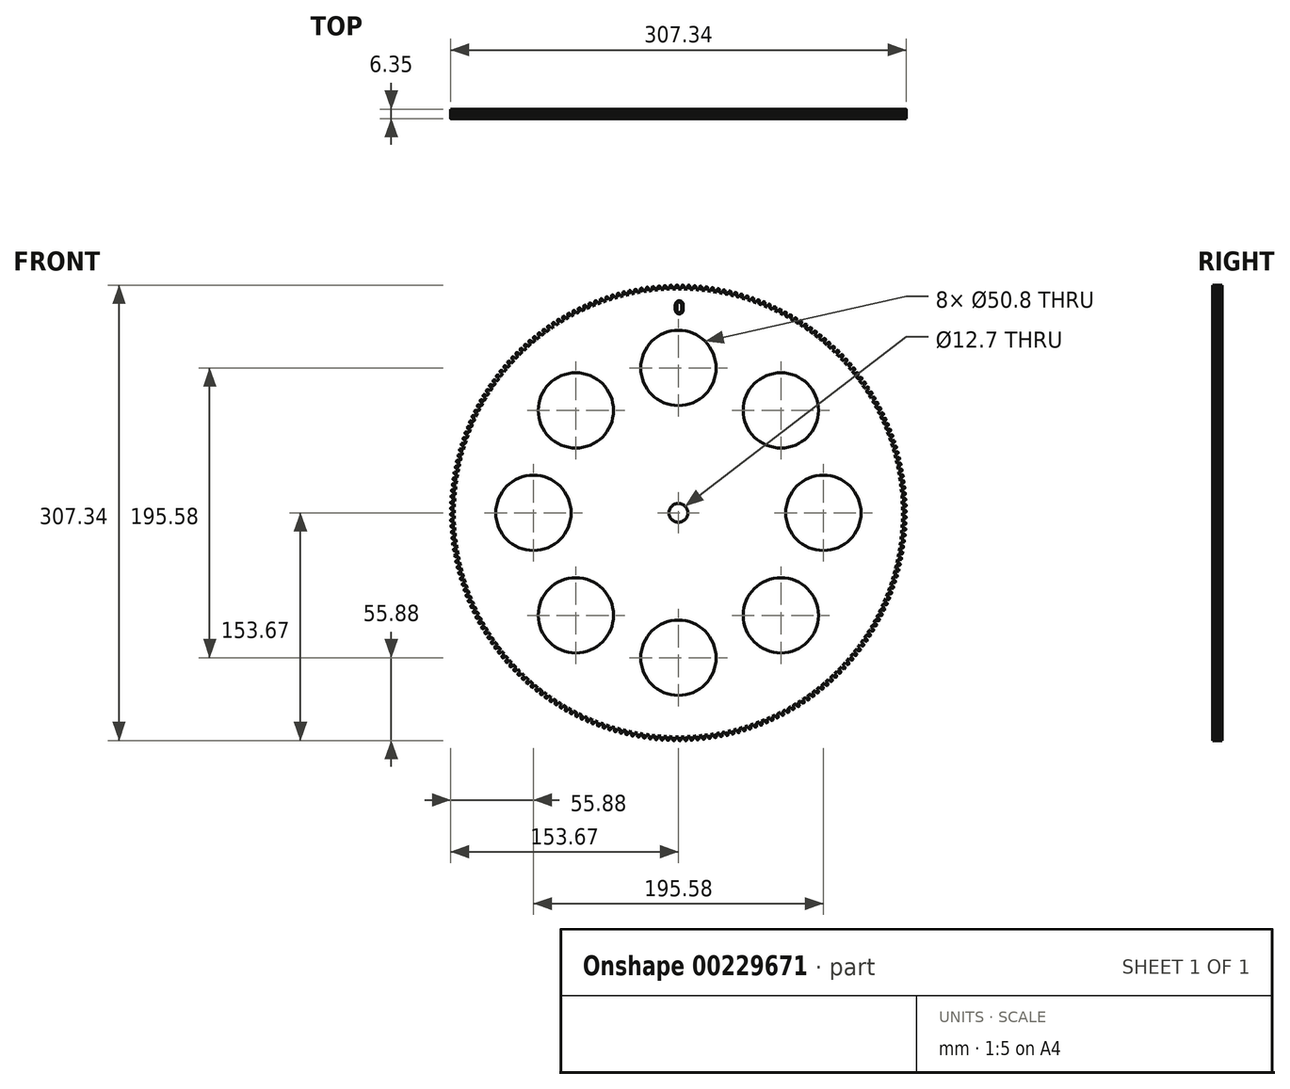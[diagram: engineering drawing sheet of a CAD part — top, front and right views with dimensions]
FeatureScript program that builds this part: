
annotation { "Feature Type Name" : "Feature", "Feature Type Description" : "" }
export const myFeature = defineFeature(function(context is Context, id is Id, definition is map)
    precondition{}
    {
        {
            var Q0;
            Q0=qCreatedBy(makeId("Front.planeOp"),FACE);
            var sketch = newSketch(context, id + "F0", { "sketchPlane" : qUnion([Q0])});
            skArc(sketch, "E0", {"start": v(-1.99, 151.12) * mm, "mid": v(0.99, -151.13) * mm, "end": v(0, 151.13) * mm});
            skArc(sketch, "E1.trimOffspring", {"start": v(0, 152.4) * mm, "mid": v(-0.24, 153.01) * mm, "end": v(-0.5, 153.63) * mm});
            skLineSegment(sketch, "E2", {"start": v(0, 152.4) * mm, "end": v(0, 151.13) * mm});
            skLineSegment(sketch, "E3", {"start": v(-0.56, 153.67) * mm, "end": v(-1, 153.67) * mm});
            skLineSegment(sketch, "E4.MirrorCS", {"start": v(-1.44, 153.66) * mm, "end": v(-1, 153.67) * mm});
            skArc(sketch, "E5.MirrorCS", {"start": v(-2, 152.39) * mm, "mid": v(-1.76, 153) * mm, "end": v(-1.52, 153.6) * mm});
            skLineSegment(sketch, "E6.MirrorCS", {"start": v(-2, 152.39) * mm, "end": v(-1.99, 151.12) * mm});
            skPoint(sketch, "E7.orphan", {"position": v(-1.98, 149.66) * mm});
            skPoint(sketch, "E8.orphan", {"position": v(0.02, 149.67) * mm});
            skPoint(sketch, "E9.visualSharp", {"position": v(-1.5, 153.66) * mm});
            skArc(sketch, "E9.filletArc", {"start": v(-1.44, 153.66) * mm, "mid": v(-1.48, 153.65) * mm, "end": v(-1.52, 153.6) * mm});
            skPoint(sketch, "E10.visualSharp", {"position": v(-0.52, 153.67) * mm});
            skArc(sketch, "E10.filletArc", {"start": v(-0.5, 153.63) * mm, "mid": v(-0.52, 153.66) * mm, "end": v(-0.56, 153.67) * mm});
            skLineSegment(sketch, "E11.1.0", {"start": v(-5.98, 152.28) * mm, "end": v(-5.94, 151.01) * mm});
            skArc(sketch, "E11.1.1", {"start": v(-5.98, 152.28) * mm, "mid": v(-5.77, 152.9) * mm, "end": v(-5.54, 153.52) * mm});
            skArc(sketch, "E11.1.2", {"start": v(-5.46, 153.57) * mm, "mid": v(-5.5, 153.56) * mm, "end": v(-5.54, 153.52) * mm});
            skLineSegment(sketch, "E11.1.3", {"start": v(-5.46, 153.57) * mm, "end": v(-5.03, 153.59) * mm});
            skLineSegment(sketch, "E11.1.4", {"start": v(-4.59, 153.6) * mm, "end": v(-5.03, 153.59) * mm});
            skArc(sketch, "E11.1.5", {"start": v(-4.52, 153.56) * mm, "mid": v(-4.55, 153.6) * mm, "end": v(-4.59, 153.6) * mm});
            skArc(sketch, "E11.1.6", {"start": v(-3.99, 152.35) * mm, "mid": v(-4.25, 152.96) * mm, "end": v(-4.52, 153.56) * mm});
            skLineSegment(sketch, "E11.1.7", {"start": v(-3.99, 152.35) * mm, "end": v(-3.95, 151.08) * mm});
            skLineSegment(sketch, "E11.2.0", {"start": v(-9.97, 152.07) * mm, "end": v(-9.9, 150.8) * mm});
            skArc(sketch, "E11.2.1", {"start": v(-9.97, 152.07) * mm, "mid": v(-9.77, 152.7) * mm, "end": v(-9.55, 153.32) * mm});
            skArc(sketch, "E11.2.2", {"start": v(-9.48, 153.38) * mm, "mid": v(-9.52, 153.36) * mm, "end": v(-9.55, 153.32) * mm});
            skLineSegment(sketch, "E11.2.3", {"start": v(-9.48, 153.38) * mm, "end": v(-9.05, 153.4) * mm});
            skLineSegment(sketch, "E11.2.4", {"start": v(-8.6, 153.43) * mm, "end": v(-9.05, 153.4) * mm});
            skArc(sketch, "E11.2.5", {"start": v(-8.54, 153.39) * mm, "mid": v(-8.57, 153.42) * mm, "end": v(-8.6, 153.43) * mm});
            skArc(sketch, "E11.2.6", {"start": v(-7.98, 152.2) * mm, "mid": v(-8.25, 152.8) * mm, "end": v(-8.54, 153.39) * mm});
            skLineSegment(sketch, "E11.2.7", {"start": v(-7.98, 152.2) * mm, "end": v(-7.9, 150.92) * mm});
            skLineSegment(sketch, "E11.3.0", {"start": v(-13.94, 151.76) * mm, "end": v(-13.84, 150.5) * mm});
            skArc(sketch, "E11.3.1", {"start": v(-13.94, 151.76) * mm, "mid": v(-13.76, 152.39) * mm, "end": v(-13.56, 153.02) * mm});
            skArc(sketch, "E11.3.2", {"start": v(-13.49, 153.08) * mm, "mid": v(-13.54, 153.06) * mm, "end": v(-13.56, 153.02) * mm});
            skLineSegment(sketch, "E11.3.3", {"start": v(-13.49, 153.08) * mm, "end": v(-13.06, 153.11) * mm});
            skLineSegment(sketch, "E11.3.4", {"start": v(-12.62, 153.15) * mm, "end": v(-13.06, 153.11) * mm});
            skArc(sketch, "E11.3.5", {"start": v(-12.55, 153.11) * mm, "mid": v(-12.58, 153.14) * mm, "end": v(-12.62, 153.15) * mm});
            skArc(sketch, "E11.3.6", {"start": v(-11.96, 151.93) * mm, "mid": v(-12.25, 152.52) * mm, "end": v(-12.55, 153.11) * mm});
            skLineSegment(sketch, "E11.3.7", {"start": v(-11.96, 151.93) * mm, "end": v(-11.85, 150.66) * mm});
            skLineSegment(sketch, "E11.4.0", {"start": v(-17.91, 151.34) * mm, "end": v(-17.77, 150.08) * mm});
            skArc(sketch, "E11.4.1", {"start": v(-17.91, 151.34) * mm, "mid": v(-17.74, 151.98) * mm, "end": v(-17.57, 152.6) * mm});
            skArc(sketch, "E11.4.2", {"start": v(-17.5, 152.67) * mm, "mid": v(-17.54, 152.65) * mm, "end": v(-17.57, 152.6) * mm});
            skLineSegment(sketch, "E11.4.3", {"start": v(-17.5, 152.67) * mm, "end": v(-17.06, 152.72) * mm});
            skLineSegment(sketch, "E11.4.4", {"start": v(-16.62, 152.77) * mm, "end": v(-17.06, 152.72) * mm});
            skArc(sketch, "E11.4.5", {"start": v(-16.55, 152.73) * mm, "mid": v(-16.58, 152.76) * mm, "end": v(-16.62, 152.77) * mm});
            skArc(sketch, "E11.4.6", {"start": v(-15.93, 151.57) * mm, "mid": v(-16.24, 152.15) * mm, "end": v(-16.55, 152.73) * mm});
            skLineSegment(sketch, "E11.4.7", {"start": v(-15.93, 151.57) * mm, "end": v(-15.79, 150.3) * mm});
            skLineSegment(sketch, "E11.5.0", {"start": v(-21.87, 150.82) * mm, "end": v(-21.7, 149.56) * mm});
            skArc(sketch, "E11.5.1", {"start": v(-21.87, 150.82) * mm, "mid": v(-21.72, 151.46) * mm, "end": v(-21.55, 152.1) * mm});
            skArc(sketch, "E11.5.2", {"start": v(-21.48, 152.16) * mm, "mid": v(-21.53, 152.14) * mm, "end": v(-21.55, 152.1) * mm});
            skLineSegment(sketch, "E11.5.3", {"start": v(-21.48, 152.16) * mm, "end": v(-21.05, 152.22) * mm});
            skLineSegment(sketch, "E11.5.4", {"start": v(-20.62, 152.28) * mm, "end": v(-21.05, 152.22) * mm});
            skArc(sketch, "E11.5.5", {"start": v(-20.55, 152.25) * mm, "mid": v(-20.58, 152.27) * mm, "end": v(-20.62, 152.28) * mm});
            skArc(sketch, "E11.5.6", {"start": v(-19.9, 151.1) * mm, "mid": v(-20.21, 151.67) * mm, "end": v(-20.55, 152.25) * mm});
            skLineSegment(sketch, "E11.5.7", {"start": v(-19.9, 151.1) * mm, "end": v(-19.72, 149.84) * mm});
            skLineSegment(sketch, "E11.6.0", {"start": v(-25.8, 150.2) * mm, "end": v(-25.6, 148.95) * mm});
            skArc(sketch, "E11.6.1", {"start": v(-25.8, 150.2) * mm, "mid": v(-25.67, 150.84) * mm, "end": v(-25.53, 151.48) * mm});
            skArc(sketch, "E11.6.2", {"start": v(-25.46, 151.55) * mm, "mid": v(-25.5, 151.52) * mm, "end": v(-25.53, 151.48) * mm});
            skLineSegment(sketch, "E11.6.3", {"start": v(-25.46, 151.55) * mm, "end": v(-25.03, 151.62) * mm});
            skLineSegment(sketch, "E11.6.4", {"start": v(-24.6, 151.69) * mm, "end": v(-25.03, 151.62) * mm});
            skArc(sketch, "E11.6.5", {"start": v(-24.52, 151.66) * mm, "mid": v(-24.56, 151.68) * mm, "end": v(-24.6, 151.69) * mm});
            skArc(sketch, "E11.6.6", {"start": v(-23.84, 150.52) * mm, "mid": v(-24.18, 151.1) * mm, "end": v(-24.52, 151.66) * mm});
            skLineSegment(sketch, "E11.6.7", {"start": v(-23.84, 150.52) * mm, "end": v(-23.63, 149.27) * mm});
            skLineSegment(sketch, "E11.7.0", {"start": v(-29.73, 149.47) * mm, "end": v(-29.5, 148.22) * mm});
            skArc(sketch, "E11.7.1", {"start": v(-29.73, 149.47) * mm, "mid": v(-29.61, 150.12) * mm, "end": v(-29.48, 150.76) * mm});
            skArc(sketch, "E11.7.2", {"start": v(-29.41, 150.83) * mm, "mid": v(-29.46, 150.8) * mm, "end": v(-29.48, 150.76) * mm});
            skLineSegment(sketch, "E11.7.3", {"start": v(-29.41, 150.83) * mm, "end": v(-29, 150.91) * mm});
            skLineSegment(sketch, "E11.7.4", {"start": v(-28.56, 151) * mm, "end": v(-29, 150.91) * mm});
            skArc(sketch, "E11.7.5", {"start": v(-28.49, 150.96) * mm, "mid": v(-28.52, 150.99) * mm, "end": v(-28.56, 151) * mm});
            skArc(sketch, "E11.7.6", {"start": v(-27.77, 149.85) * mm, "mid": v(-28.12, 150.4) * mm, "end": v(-28.49, 150.96) * mm});
            skLineSegment(sketch, "E11.7.7", {"start": v(-27.77, 149.85) * mm, "end": v(-27.53, 148.6) * mm});
            skLineSegment(sketch, "E11.8.0", {"start": v(-33.63, 148.64) * mm, "end": v(-33.36, 147.4) * mm});
            skArc(sketch, "E11.8.1", {"start": v(-33.63, 148.64) * mm, "mid": v(-33.53, 149.3) * mm, "end": v(-33.42, 149.94) * mm});
            skArc(sketch, "E11.8.2", {"start": v(-33.35, 150) * mm, "mid": v(-33.4, 149.98) * mm, "end": v(-33.42, 149.94) * mm});
            skLineSegment(sketch, "E11.8.3", {"start": v(-33.35, 150) * mm, "end": v(-32.93, 150.1) * mm});
            skLineSegment(sketch, "E11.8.4", {"start": v(-32.5, 150.2) * mm, "end": v(-32.93, 150.1) * mm});
            skArc(sketch, "E11.8.5", {"start": v(-32.43, 150.16) * mm, "mid": v(-32.46, 150.2) * mm, "end": v(-32.5, 150.2) * mm});
            skArc(sketch, "E11.8.6", {"start": v(-31.69, 149.07) * mm, "mid": v(-32.05, 149.62) * mm, "end": v(-32.43, 150.16) * mm});
            skLineSegment(sketch, "E11.8.7", {"start": v(-31.69, 149.07) * mm, "end": v(-31.41, 147.83) * mm});
            skLineSegment(sketch, "E11.9.0", {"start": v(-37.51, 147.71) * mm, "end": v(-37.2, 146.48) * mm});
            skArc(sketch, "E11.9.1", {"start": v(-37.51, 147.71) * mm, "mid": v(-37.43, 148.36) * mm, "end": v(-37.33, 149.01) * mm});
            skArc(sketch, "E11.9.2", {"start": v(-37.27, 149.08) * mm, "mid": v(-37.31, 149.06) * mm, "end": v(-37.33, 149.01) * mm});
            skLineSegment(sketch, "E11.9.3", {"start": v(-37.27, 149.08) * mm, "end": v(-36.85, 149.19) * mm});
            skLineSegment(sketch, "E11.9.4", {"start": v(-36.42, 149.3) * mm, "end": v(-36.85, 149.19) * mm});
            skArc(sketch, "E11.9.5", {"start": v(-36.35, 149.26) * mm, "mid": v(-36.38, 149.29) * mm, "end": v(-36.42, 149.3) * mm});
            skArc(sketch, "E11.9.6", {"start": v(-35.58, 148.19) * mm, "mid": v(-35.96, 148.73) * mm, "end": v(-36.35, 149.26) * mm});
            skLineSegment(sketch, "E11.9.7", {"start": v(-35.58, 148.19) * mm, "end": v(-35.27, 146.96) * mm});
            skLineSegment(sketch, "E11.10.0", {"start": v(-41.37, 146.68) * mm, "end": v(-41.03, 145.45) * mm});
            skArc(sketch, "E11.10.1", {"start": v(-41.37, 146.68) * mm, "mid": v(-41.3, 147.33) * mm, "end": v(-41.22, 147.98) * mm});
            skArc(sketch, "E11.10.2", {"start": v(-41.16, 148.06) * mm, "mid": v(-41.2, 148.03) * mm, "end": v(-41.22, 147.98) * mm});
            skLineSegment(sketch, "E11.10.3", {"start": v(-41.16, 148.06) * mm, "end": v(-40.74, 148.17) * mm});
            skLineSegment(sketch, "E11.10.4", {"start": v(-40.32, 148.29) * mm, "end": v(-40.74, 148.17) * mm});
            skArc(sketch, "E11.10.5", {"start": v(-40.24, 148.26) * mm, "mid": v(-40.28, 148.29) * mm, "end": v(-40.32, 148.29) * mm});
            skArc(sketch, "E11.10.6", {"start": v(-39.44, 147.2) * mm, "mid": v(-39.84, 147.74) * mm, "end": v(-40.24, 148.26) * mm});
            skLineSegment(sketch, "E11.10.7", {"start": v(-39.44, 147.2) * mm, "end": v(-39.1, 145.98) * mm});
            skLineSegment(sketch, "E11.11.0", {"start": v(-45.2, 145.55) * mm, "end": v(-44.82, 144.33) * mm});
            skArc(sketch, "E11.11.1", {"start": v(-45.2, 145.55) * mm, "mid": v(-45.14, 146.2) * mm, "end": v(-45.08, 146.85) * mm});
            skArc(sketch, "E11.11.2", {"start": v(-45.02, 146.93) * mm, "mid": v(-45.06, 146.9) * mm, "end": v(-45.08, 146.85) * mm});
            skLineSegment(sketch, "E11.11.3", {"start": v(-45.02, 146.93) * mm, "end": v(-44.6, 147.05) * mm});
            skLineSegment(sketch, "E11.11.4", {"start": v(-44.19, 147.18) * mm, "end": v(-44.6, 147.05) * mm});
            skArc(sketch, "E11.11.5", {"start": v(-44.1, 147.16) * mm, "mid": v(-44.14, 147.18) * mm, "end": v(-44.19, 147.18) * mm});
            skArc(sketch, "E11.11.6", {"start": v(-43.28, 146.12) * mm, "mid": v(-43.7, 146.64) * mm, "end": v(-44.1, 147.16) * mm});
            skLineSegment(sketch, "E11.11.7", {"start": v(-43.28, 146.12) * mm, "end": v(-42.92, 144.9) * mm});
            skLineSegment(sketch, "E11.12.0", {"start": v(-48.99, 144.31) * mm, "end": v(-48.59, 143.1) * mm});
            skArc(sketch, "E11.12.1", {"start": v(-48.99, 144.31) * mm, "mid": v(-48.95, 144.97) * mm, "end": v(-48.91, 145.62) * mm});
            skArc(sketch, "E11.12.2", {"start": v(-48.85, 145.7) * mm, "mid": v(-48.9, 145.67) * mm, "end": v(-48.91, 145.62) * mm});
            skLineSegment(sketch, "E11.12.3", {"start": v(-48.85, 145.7) * mm, "end": v(-48.44, 145.84) * mm});
            skLineSegment(sketch, "E11.12.4", {"start": v(-48.02, 145.97) * mm, "end": v(-48.44, 145.84) * mm});
            skArc(sketch, "E11.12.5", {"start": v(-47.95, 145.95) * mm, "mid": v(-47.98, 145.97) * mm, "end": v(-48.02, 145.97) * mm});
            skArc(sketch, "E11.12.6", {"start": v(-47.1, 144.94) * mm, "mid": v(-47.52, 145.45) * mm, "end": v(-47.95, 145.95) * mm});
            skLineSegment(sketch, "E11.12.7", {"start": v(-47.1, 144.94) * mm, "end": v(-46.7, 143.74) * mm});
            skLineSegment(sketch, "E11.13.0", {"start": v(-52.75, 142.98) * mm, "end": v(-52.32, 141.79) * mm});
            skArc(sketch, "E11.13.1", {"start": v(-52.75, 142.98) * mm, "mid": v(-52.73, 143.64) * mm, "end": v(-52.7, 144.3) * mm});
            skArc(sketch, "E11.13.2", {"start": v(-52.65, 144.37) * mm, "mid": v(-52.69, 144.34) * mm, "end": v(-52.7, 144.3) * mm});
            skLineSegment(sketch, "E11.13.3", {"start": v(-52.65, 144.37) * mm, "end": v(-52.24, 144.52) * mm});
            skLineSegment(sketch, "E11.13.4", {"start": v(-51.83, 144.67) * mm, "end": v(-52.24, 144.52) * mm});
            skArc(sketch, "E11.13.5", {"start": v(-51.75, 144.65) * mm, "mid": v(-51.79, 144.67) * mm, "end": v(-51.83, 144.67) * mm});
            skArc(sketch, "E11.13.6", {"start": v(-50.87, 143.66) * mm, "mid": v(-51.3, 144.16) * mm, "end": v(-51.75, 144.65) * mm});
            skLineSegment(sketch, "E11.13.7", {"start": v(-50.87, 143.66) * mm, "end": v(-50.44, 142.46) * mm});
            skLineSegment(sketch, "E11.14.0", {"start": v(-56.47, 141.55) * mm, "end": v(-56.01, 140.37) * mm});
            skArc(sketch, "E11.14.1", {"start": v(-56.47, 141.55) * mm, "mid": v(-56.47, 142.2) * mm, "end": v(-56.46, 142.86) * mm});
            skArc(sketch, "E11.14.2", {"start": v(-56.4, 142.94) * mm, "mid": v(-56.45, 142.91) * mm, "end": v(-56.46, 142.86) * mm});
            skLineSegment(sketch, "E11.14.3", {"start": v(-56.4, 142.94) * mm, "end": v(-56, 143.1) * mm});
            skLineSegment(sketch, "E11.14.4", {"start": v(-55.6, 143.26) * mm, "end": v(-56, 143.1) * mm});
            skArc(sketch, "E11.14.5", {"start": v(-55.52, 143.24) * mm, "mid": v(-55.56, 143.26) * mm, "end": v(-55.6, 143.26) * mm});
            skArc(sketch, "E11.14.6", {"start": v(-54.62, 142.28) * mm, "mid": v(-55.06, 142.76) * mm, "end": v(-55.52, 143.24) * mm});
            skLineSegment(sketch, "E11.14.7", {"start": v(-54.62, 142.28) * mm, "end": v(-54.15, 141.1) * mm});
            skLineSegment(sketch, "E11.15.0", {"start": v(-60.16, 140.02) * mm, "end": v(-59.67, 138.85) * mm});
            skArc(sketch, "E11.15.1", {"start": v(-60.16, 140.02) * mm, "mid": v(-60.18, 140.68) * mm, "end": v(-60.18, 141.34) * mm});
            skArc(sketch, "E11.15.2", {"start": v(-60.13, 141.42) * mm, "mid": v(-60.17, 141.38) * mm, "end": v(-60.18, 141.34) * mm});
            skLineSegment(sketch, "E11.15.3", {"start": v(-60.13, 141.42) * mm, "end": v(-59.74, 141.59) * mm});
            skLineSegment(sketch, "E11.15.4", {"start": v(-59.33, 141.76) * mm, "end": v(-59.74, 141.59) * mm});
            skArc(sketch, "E11.15.5", {"start": v(-59.25, 141.74) * mm, "mid": v(-59.29, 141.76) * mm, "end": v(-59.33, 141.76) * mm});
            skArc(sketch, "E11.15.6", {"start": v(-58.32, 140.8) * mm, "mid": v(-58.78, 141.27) * mm, "end": v(-59.25, 141.74) * mm});
            skLineSegment(sketch, "E11.15.7", {"start": v(-58.32, 140.8) * mm, "end": v(-57.83, 139.63) * mm});
            skLineSegment(sketch, "E11.16.0", {"start": v(-63.8, 138.4) * mm, "end": v(-63.28, 137.24) * mm});
            skArc(sketch, "E11.16.1", {"start": v(-63.8, 138.4) * mm, "mid": v(-63.84, 139.06) * mm, "end": v(-63.86, 139.71) * mm});
            skArc(sketch, "E11.16.2", {"start": v(-63.81, 139.8) * mm, "mid": v(-63.85, 139.76) * mm, "end": v(-63.86, 139.71) * mm});
            skLineSegment(sketch, "E11.16.3", {"start": v(-63.81, 139.8) * mm, "end": v(-63.42, 139.97) * mm});
            skLineSegment(sketch, "E11.16.4", {"start": v(-63.02, 140.15) * mm, "end": v(-63.42, 139.97) * mm});
            skArc(sketch, "E11.16.5", {"start": v(-62.94, 140.14) * mm, "mid": v(-62.98, 140.16) * mm, "end": v(-63.02, 140.15) * mm});
            skArc(sketch, "E11.16.6", {"start": v(-61.99, 139.22) * mm, "mid": v(-62.46, 139.69) * mm, "end": v(-62.94, 140.14) * mm});
            skLineSegment(sketch, "E11.16.7", {"start": v(-61.99, 139.22) * mm, "end": v(-61.46, 138.07) * mm});
            skLineSegment(sketch, "E11.17.0", {"start": v(-67.4, 136.68) * mm, "end": v(-66.85, 135.54) * mm});
            skArc(sketch, "E11.17.1", {"start": v(-67.4, 136.68) * mm, "mid": v(-67.46, 137.34) * mm, "end": v(-67.5, 138) * mm});
            skArc(sketch, "E11.17.2", {"start": v(-67.45, 138.08) * mm, "mid": v(-67.49, 138.04) * mm, "end": v(-67.5, 138) * mm});
            skLineSegment(sketch, "E11.17.3", {"start": v(-67.45, 138.08) * mm, "end": v(-67.06, 138.27) * mm});
            skLineSegment(sketch, "E11.17.4", {"start": v(-66.67, 138.46) * mm, "end": v(-67.06, 138.27) * mm});
            skArc(sketch, "E11.17.5", {"start": v(-66.59, 138.45) * mm, "mid": v(-66.62, 138.46) * mm, "end": v(-66.67, 138.46) * mm});
            skArc(sketch, "E11.17.6", {"start": v(-65.6, 137.55) * mm, "mid": v(-66.1, 138) * mm, "end": v(-66.59, 138.45) * mm});
            skLineSegment(sketch, "E11.17.7", {"start": v(-65.6, 137.55) * mm, "end": v(-65.06, 136.41) * mm});
            skLineSegment(sketch, "E11.18.0", {"start": v(-70.96, 134.87) * mm, "end": v(-70.38, 133.74) * mm});
            skArc(sketch, "E11.18.1", {"start": v(-70.96, 134.87) * mm, "mid": v(-71.03, 135.52) * mm, "end": v(-71.09, 136.18) * mm});
            skArc(sketch, "E11.18.2", {"start": v(-71.04, 136.26) * mm, "mid": v(-71.08, 136.23) * mm, "end": v(-71.09, 136.18) * mm});
            skLineSegment(sketch, "E11.18.3", {"start": v(-71.04, 136.26) * mm, "end": v(-70.66, 136.46) * mm});
            skLineSegment(sketch, "E11.18.4", {"start": v(-70.27, 136.66) * mm, "end": v(-70.66, 136.46) * mm});
            skArc(sketch, "E11.18.5", {"start": v(-70.19, 136.66) * mm, "mid": v(-70.23, 136.67) * mm, "end": v(-70.27, 136.66) * mm});
            skArc(sketch, "E11.18.6", {"start": v(-69.19, 135.79) * mm, "mid": v(-69.68, 136.23) * mm, "end": v(-70.19, 136.66) * mm});
            skLineSegment(sketch, "E11.18.7", {"start": v(-69.19, 135.79) * mm, "end": v(-68.6, 134.66) * mm});
            skLineSegment(sketch, "E11.19.0", {"start": v(-74.47, 132.97) * mm, "end": v(-73.85, 131.86) * mm});
            skArc(sketch, "E11.19.1", {"start": v(-74.47, 132.97) * mm, "mid": v(-74.55, 133.62) * mm, "end": v(-74.63, 134.27) * mm});
            skArc(sketch, "E11.19.2", {"start": v(-74.58, 134.36) * mm, "mid": v(-74.62, 134.32) * mm, "end": v(-74.63, 134.27) * mm});
            skLineSegment(sketch, "E11.19.3", {"start": v(-74.58, 134.36) * mm, "end": v(-74.2, 134.57) * mm});
            skLineSegment(sketch, "E11.19.4", {"start": v(-73.82, 134.78) * mm, "end": v(-74.2, 134.57) * mm});
            skArc(sketch, "E11.19.5", {"start": v(-73.74, 134.77) * mm, "mid": v(-73.78, 134.79) * mm, "end": v(-73.82, 134.78) * mm});
            skArc(sketch, "E11.19.6", {"start": v(-72.72, 133.93) * mm, "mid": v(-73.23, 134.36) * mm, "end": v(-73.74, 134.77) * mm});
            skLineSegment(sketch, "E11.19.7", {"start": v(-72.72, 133.93) * mm, "end": v(-72.1, 132.82) * mm});
            skLineSegment(sketch, "E11.20.0", {"start": v(-77.92, 130.97) * mm, "end": v(-77.28, 129.88) * mm});
            skArc(sketch, "E11.20.1", {"start": v(-77.92, 130.97) * mm, "mid": v(-78.03, 131.62) * mm, "end": v(-78.12, 132.27) * mm});
            skArc(sketch, "E11.20.2", {"start": v(-78.08, 132.36) * mm, "mid": v(-78.1, 132.32) * mm, "end": v(-78.12, 132.27) * mm});
            skLineSegment(sketch, "E11.20.3", {"start": v(-78.08, 132.36) * mm, "end": v(-77.7, 132.58) * mm});
            skLineSegment(sketch, "E11.20.4", {"start": v(-77.32, 132.8) * mm, "end": v(-77.7, 132.58) * mm});
            skArc(sketch, "E11.20.5", {"start": v(-77.24, 132.8) * mm, "mid": v(-77.28, 132.8) * mm, "end": v(-77.32, 132.8) * mm});
            skArc(sketch, "E11.20.6", {"start": v(-76.2, 131.98) * mm, "mid": v(-76.72, 132.4) * mm, "end": v(-77.24, 132.8) * mm});
            skLineSegment(sketch, "E11.20.7", {"start": v(-76.2, 131.98) * mm, "end": v(-75.56, 130.89) * mm});
            skLineSegment(sketch, "E11.21.0", {"start": v(-81.32, 128.89) * mm, "end": v(-80.65, 127.81) * mm});
            skArc(sketch, "E11.21.1", {"start": v(-81.32, 128.89) * mm, "mid": v(-81.44, 129.53) * mm, "end": v(-81.55, 130.18) * mm});
            skArc(sketch, "E11.21.2", {"start": v(-81.51, 130.27) * mm, "mid": v(-81.55, 130.23) * mm, "end": v(-81.55, 130.18) * mm});
            skLineSegment(sketch, "E11.21.3", {"start": v(-81.51, 130.27) * mm, "end": v(-81.15, 130.5) * mm});
            skLineSegment(sketch, "E11.21.4", {"start": v(-80.77, 130.73) * mm, "end": v(-81.15, 130.5) * mm});
            skArc(sketch, "E11.21.5", {"start": v(-80.7, 130.73) * mm, "mid": v(-80.73, 130.74) * mm, "end": v(-80.77, 130.73) * mm});
            skArc(sketch, "E11.21.6", {"start": v(-79.63, 129.94) * mm, "mid": v(-80.16, 130.34) * mm, "end": v(-80.7, 130.73) * mm});
            skLineSegment(sketch, "E11.21.7", {"start": v(-79.63, 129.94) * mm, "end": v(-78.96, 128.86) * mm});
            skLineSegment(sketch, "E11.22.0", {"start": v(-84.67, 126.72) * mm, "end": v(-83.97, 125.66) * mm});
            skArc(sketch, "E11.22.1", {"start": v(-84.67, 126.72) * mm, "mid": v(-84.8, 127.36) * mm, "end": v(-84.93, 128) * mm});
            skArc(sketch, "E11.22.2", {"start": v(-84.9, 128.1) * mm, "mid": v(-84.93, 128.05) * mm, "end": v(-84.93, 128) * mm});
            skLineSegment(sketch, "E11.22.3", {"start": v(-84.9, 128.1) * mm, "end": v(-84.54, 128.33) * mm});
            skLineSegment(sketch, "E11.22.4", {"start": v(-84.17, 128.57) * mm, "end": v(-84.54, 128.33) * mm});
            skArc(sketch, "E11.22.5", {"start": v(-84.09, 128.57) * mm, "mid": v(-84.13, 128.58) * mm, "end": v(-84.17, 128.57) * mm});
            skArc(sketch, "E11.22.6", {"start": v(-83, 127.81) * mm, "mid": v(-83.54, 128.2) * mm, "end": v(-84.09, 128.57) * mm});
            skLineSegment(sketch, "E11.22.7", {"start": v(-83, 127.81) * mm, "end": v(-82.3, 126.75) * mm});
            skLineSegment(sketch, "E11.23.0", {"start": v(-87.96, 124.46) * mm, "end": v(-87.23, 123.41) * mm});
            skArc(sketch, "E11.23.1", {"start": v(-87.96, 124.46) * mm, "mid": v(-88.11, 125.1) * mm, "end": v(-88.25, 125.73) * mm});
            skArc(sketch, "E11.23.2", {"start": v(-88.22, 125.82) * mm, "mid": v(-88.25, 125.78) * mm, "end": v(-88.25, 125.73) * mm});
            skLineSegment(sketch, "E11.23.3", {"start": v(-88.22, 125.82) * mm, "end": v(-87.87, 126.07) * mm});
            skLineSegment(sketch, "E11.23.4", {"start": v(-87.5, 126.32) * mm, "end": v(-87.87, 126.07) * mm});
            skArc(sketch, "E11.23.5", {"start": v(-87.43, 126.32) * mm, "mid": v(-87.46, 126.34) * mm, "end": v(-87.5, 126.32) * mm});
            skArc(sketch, "E11.23.6", {"start": v(-86.32, 125.6) * mm, "mid": v(-86.87, 125.97) * mm, "end": v(-87.43, 126.32) * mm});
            skLineSegment(sketch, "E11.23.7", {"start": v(-86.32, 125.6) * mm, "end": v(-85.6, 124.55) * mm});
            skLineSegment(sketch, "E11.24.0", {"start": v(-91.18, 122.11) * mm, "end": v(-90.43, 121.09) * mm});
            skArc(sketch, "E11.24.1", {"start": v(-91.18, 122.11) * mm, "mid": v(-91.36, 122.74) * mm, "end": v(-91.52, 123.38) * mm});
            skArc(sketch, "E11.24.2", {"start": v(-91.48, 123.47) * mm, "mid": v(-91.51, 123.43) * mm, "end": v(-91.52, 123.38) * mm});
            skLineSegment(sketch, "E11.24.3", {"start": v(-91.48, 123.47) * mm, "end": v(-91.14, 123.73) * mm});
            skLineSegment(sketch, "E11.24.4", {"start": v(-90.78, 123.99) * mm, "end": v(-91.14, 123.73) * mm});
            skArc(sketch, "E11.24.5", {"start": v(-90.7, 124) * mm, "mid": v(-90.74, 124) * mm, "end": v(-90.78, 123.99) * mm});
            skArc(sketch, "E11.24.6", {"start": v(-89.58, 123.3) * mm, "mid": v(-90.14, 123.65) * mm, "end": v(-90.7, 124) * mm});
            skLineSegment(sketch, "E11.24.7", {"start": v(-89.58, 123.3) * mm, "end": v(-88.83, 122.27) * mm});
            skLineSegment(sketch, "E11.25.0", {"start": v(-94.35, 119.68) * mm, "end": v(-93.57, 118.68) * mm});
            skArc(sketch, "E11.25.1", {"start": v(-94.35, 119.68) * mm, "mid": v(-94.54, 120.31) * mm, "end": v(-94.71, 120.94) * mm});
            skArc(sketch, "E11.25.2", {"start": v(-94.68, 121.04) * mm, "mid": v(-94.71, 121) * mm, "end": v(-94.71, 120.94) * mm});
            skLineSegment(sketch, "E11.25.3", {"start": v(-94.68, 121.04) * mm, "end": v(-94.34, 121.3) * mm});
            skLineSegment(sketch, "E11.25.4", {"start": v(-94, 121.57) * mm, "end": v(-94.34, 121.3) * mm});
            skArc(sketch, "E11.25.5", {"start": v(-93.92, 121.58) * mm, "mid": v(-93.96, 121.58) * mm, "end": v(-94, 121.57) * mm});
            skArc(sketch, "E11.25.6", {"start": v(-92.78, 120.9) * mm, "mid": v(-93.34, 121.25) * mm, "end": v(-93.92, 121.58) * mm});
            skLineSegment(sketch, "E11.25.7", {"start": v(-92.78, 120.9) * mm, "end": v(-92, 119.9) * mm});
            skLineSegment(sketch, "E11.26.0", {"start": v(-97.45, 117.17) * mm, "end": v(-96.64, 116.19) * mm});
            skArc(sketch, "E11.26.1", {"start": v(-97.45, 117.17) * mm, "mid": v(-97.65, 117.8) * mm, "end": v(-97.85, 118.42) * mm});
            skArc(sketch, "E11.26.2", {"start": v(-97.82, 118.52) * mm, "mid": v(-97.85, 118.47) * mm, "end": v(-97.85, 118.42) * mm});
            skLineSegment(sketch, "E11.26.3", {"start": v(-97.82, 118.52) * mm, "end": v(-97.49, 118.79) * mm});
            skLineSegment(sketch, "E11.26.4", {"start": v(-97.15, 119.07) * mm, "end": v(-97.49, 118.79) * mm});
            skArc(sketch, "E11.26.5", {"start": v(-97.07, 119.08) * mm, "mid": v(-97.1, 119.08) * mm, "end": v(-97.15, 119.07) * mm});
            skArc(sketch, "E11.26.6", {"start": v(-95.9, 118.44) * mm, "mid": v(-96.48, 118.76) * mm, "end": v(-97.07, 119.08) * mm});
            skLineSegment(sketch, "E11.26.7", {"start": v(-95.9, 118.44) * mm, "end": v(-95.1, 117.46) * mm});
            skLineSegment(sketch, "E11.27.0", {"start": v(-100.48, 114.58) * mm, "end": v(-99.65, 113.62) * mm});
            skArc(sketch, "E11.27.1", {"start": v(-100.48, 114.58) * mm, "mid": v(-100.7, 115.2) * mm, "end": v(-100.91, 115.82) * mm});
            skArc(sketch, "E11.27.2", {"start": v(-100.89, 115.91) * mm, "mid": v(-100.92, 115.87) * mm, "end": v(-100.91, 115.82) * mm});
            skLineSegment(sketch, "E11.27.3", {"start": v(-100.89, 115.91) * mm, "end": v(-100.56, 116.2) * mm});
            skLineSegment(sketch, "E11.27.4", {"start": v(-100.23, 116.48) * mm, "end": v(-100.56, 116.2) * mm});
            skArc(sketch, "E11.27.5", {"start": v(-100.15, 116.5) * mm, "mid": v(-100.2, 116.5) * mm, "end": v(-100.23, 116.48) * mm});
            skArc(sketch, "E11.27.6", {"start": v(-98.98, 115.89) * mm, "mid": v(-99.56, 116.2) * mm, "end": v(-100.15, 116.5) * mm});
            skLineSegment(sketch, "E11.27.7", {"start": v(-98.98, 115.89) * mm, "end": v(-98.14, 114.93) * mm});
            skLineSegment(sketch, "E11.28.0", {"start": v(-103.45, 111.91) * mm, "end": v(-102.6, 110.97) * mm});
            skArc(sketch, "E11.28.1", {"start": v(-103.45, 111.91) * mm, "mid": v(-103.69, 112.52) * mm, "end": v(-103.91, 113.14) * mm});
            skArc(sketch, "E11.28.2", {"start": v(-103.89, 113.23) * mm, "mid": v(-103.91, 113.19) * mm, "end": v(-103.91, 113.14) * mm});
            skLineSegment(sketch, "E11.28.3", {"start": v(-103.89, 113.23) * mm, "end": v(-103.57, 113.52) * mm});
            skLineSegment(sketch, "E11.28.4", {"start": v(-103.24, 113.82) * mm, "end": v(-103.57, 113.52) * mm});
            skArc(sketch, "E11.28.5", {"start": v(-103.17, 113.83) * mm, "mid": v(-103.2, 113.84) * mm, "end": v(-103.24, 113.82) * mm});
            skArc(sketch, "E11.28.6", {"start": v(-101.98, 113.26) * mm, "mid": v(-102.57, 113.55) * mm, "end": v(-103.17, 113.83) * mm});
            skLineSegment(sketch, "E11.28.7", {"start": v(-101.98, 113.26) * mm, "end": v(-101.12, 112.32) * mm});
            skLineSegment(sketch, "E11.29.0", {"start": v(-106.34, 109.16) * mm, "end": v(-105.46, 108.25) * mm});
            skArc(sketch, "E11.29.1", {"start": v(-106.34, 109.16) * mm, "mid": v(-106.6, 109.77) * mm, "end": v(-106.84, 110.38) * mm});
            skArc(sketch, "E11.29.2", {"start": v(-106.82, 110.48) * mm, "mid": v(-106.84, 110.43) * mm, "end": v(-106.84, 110.38) * mm});
            skLineSegment(sketch, "E11.29.3", {"start": v(-106.82, 110.48) * mm, "end": v(-106.5, 110.77) * mm});
            skLineSegment(sketch, "E11.29.4", {"start": v(-106.19, 111.08) * mm, "end": v(-106.5, 110.77) * mm});
            skArc(sketch, "E11.29.5", {"start": v(-106.11, 111.1) * mm, "mid": v(-106.15, 111.1) * mm, "end": v(-106.19, 111.08) * mm});
            skArc(sketch, "E11.29.6", {"start": v(-104.9, 110.55) * mm, "mid": v(-105.5, 110.83) * mm, "end": v(-106.11, 111.1) * mm});
            skLineSegment(sketch, "E11.29.7", {"start": v(-104.9, 110.55) * mm, "end": v(-104.02, 109.63) * mm});
            skLineSegment(sketch, "E11.30.0", {"start": v(-109.16, 106.34) * mm, "end": v(-108.26, 105.45) * mm});
            skArc(sketch, "E11.30.1", {"start": v(-109.16, 106.34) * mm, "mid": v(-109.43, 106.94) * mm, "end": v(-109.7, 107.54) * mm});
            skArc(sketch, "E11.30.2", {"start": v(-109.67, 107.64) * mm, "mid": v(-109.7, 107.6) * mm, "end": v(-109.7, 107.54) * mm});
            skLineSegment(sketch, "E11.30.3", {"start": v(-109.67, 107.64) * mm, "end": v(-109.37, 107.95) * mm});
            skLineSegment(sketch, "E11.30.4", {"start": v(-109.06, 108.26) * mm, "end": v(-109.37, 107.95) * mm});
            skArc(sketch, "E11.30.5", {"start": v(-108.98, 108.28) * mm, "mid": v(-109.02, 108.28) * mm, "end": v(-109.06, 108.26) * mm});
            skArc(sketch, "E11.30.6", {"start": v(-107.76, 107.76) * mm, "mid": v(-108.37, 108.03) * mm, "end": v(-108.98, 108.28) * mm});
            skLineSegment(sketch, "E11.30.7", {"start": v(-107.76, 107.76) * mm, "end": v(-106.86, 106.87) * mm});
            skLineSegment(sketch, "E11.31.0", {"start": v(-111.91, 103.45) * mm, "end": v(-110.98, 102.58) * mm});
            skArc(sketch, "E11.31.1", {"start": v(-111.91, 103.45) * mm, "mid": v(-112.2, 104.04) * mm, "end": v(-112.47, 104.64) * mm});
            skArc(sketch, "E11.31.2", {"start": v(-112.45, 104.73) * mm, "mid": v(-112.47, 104.69) * mm, "end": v(-112.47, 104.64) * mm});
            skLineSegment(sketch, "E11.31.3", {"start": v(-112.45, 104.73) * mm, "end": v(-112.16, 105.05) * mm});
            skLineSegment(sketch, "E11.31.4", {"start": v(-111.86, 105.37) * mm, "end": v(-112.16, 105.05) * mm});
            skArc(sketch, "E11.31.5", {"start": v(-111.78, 105.39) * mm, "mid": v(-111.82, 105.39) * mm, "end": v(-111.86, 105.37) * mm});
            skArc(sketch, "E11.31.6", {"start": v(-110.55, 104.9) * mm, "mid": v(-111.16, 105.15) * mm, "end": v(-111.78, 105.39) * mm});
            skLineSegment(sketch, "E11.31.7", {"start": v(-110.55, 104.9) * mm, "end": v(-109.62, 104.04) * mm});
            skLineSegment(sketch, "E11.32.0", {"start": v(-114.58, 100.48) * mm, "end": v(-113.63, 99.64) * mm});
            skArc(sketch, "E11.32.1", {"start": v(-114.58, 100.48) * mm, "mid": v(-114.88, 101.07) * mm, "end": v(-115.17, 101.66) * mm});
            skArc(sketch, "E11.32.2", {"start": v(-115.15, 101.75) * mm, "mid": v(-115.18, 101.7) * mm, "end": v(-115.17, 101.66) * mm});
            skLineSegment(sketch, "E11.32.3", {"start": v(-115.15, 101.75) * mm, "end": v(-114.87, 102.08) * mm});
            skLineSegment(sketch, "E11.32.4", {"start": v(-114.58, 102.4) * mm, "end": v(-114.87, 102.08) * mm});
            skArc(sketch, "E11.32.5", {"start": v(-114.5, 102.43) * mm, "mid": v(-114.54, 102.43) * mm, "end": v(-114.58, 102.4) * mm});
            skArc(sketch, "E11.32.6", {"start": v(-113.26, 101.98) * mm, "mid": v(-113.88, 102.2) * mm, "end": v(-114.5, 102.43) * mm});
            skLineSegment(sketch, "E11.32.7", {"start": v(-113.26, 101.98) * mm, "end": v(-112.3, 101.13) * mm});
            skLineSegment(sketch, "E11.33.0", {"start": v(-117.17, 97.45) * mm, "end": v(-116.2, 96.63) * mm});
            skArc(sketch, "E11.33.1", {"start": v(-117.17, 97.45) * mm, "mid": v(-117.49, 98.03) * mm, "end": v(-117.79, 98.6) * mm});
            skArc(sketch, "E11.33.2", {"start": v(-117.78, 98.7) * mm, "mid": v(-117.8, 98.66) * mm, "end": v(-117.79, 98.6) * mm});
            skLineSegment(sketch, "E11.33.3", {"start": v(-117.78, 98.7) * mm, "end": v(-117.5, 99.03) * mm});
            skLineSegment(sketch, "E11.33.4", {"start": v(-117.22, 99.37) * mm, "end": v(-117.5, 99.03) * mm});
            skArc(sketch, "E11.33.5", {"start": v(-117.14, 99.4) * mm, "mid": v(-117.18, 99.4) * mm, "end": v(-117.22, 99.37) * mm});
            skArc(sketch, "E11.33.6", {"start": v(-115.89, 98.98) * mm, "mid": v(-116.51, 99.19) * mm, "end": v(-117.14, 99.4) * mm});
            skLineSegment(sketch, "E11.33.7", {"start": v(-115.89, 98.98) * mm, "end": v(-114.91, 98.16) * mm});
            skLineSegment(sketch, "E11.34.0", {"start": v(-119.68, 94.35) * mm, "end": v(-118.7, 93.56) * mm});
            skArc(sketch, "E11.34.1", {"start": v(-119.68, 94.35) * mm, "mid": v(-120.01, 94.92) * mm, "end": v(-120.33, 95.5) * mm});
            skArc(sketch, "E11.34.2", {"start": v(-120.32, 95.59) * mm, "mid": v(-120.34, 95.54) * mm, "end": v(-120.33, 95.5) * mm});
            skLineSegment(sketch, "E11.34.3", {"start": v(-120.32, 95.59) * mm, "end": v(-120.06, 95.92) * mm});
            skLineSegment(sketch, "E11.34.4", {"start": v(-119.78, 96.27) * mm, "end": v(-120.06, 95.92) * mm});
            skArc(sketch, "E11.34.5", {"start": v(-119.7, 96.3) * mm, "mid": v(-119.74, 96.3) * mm, "end": v(-119.78, 96.27) * mm});
            skArc(sketch, "E11.34.6", {"start": v(-118.44, 95.9) * mm, "mid": v(-119.07, 96.1) * mm, "end": v(-119.7, 96.3) * mm});
            skLineSegment(sketch, "E11.34.7", {"start": v(-118.44, 95.9) * mm, "end": v(-117.44, 95.12) * mm});
            skLineSegment(sketch, "E11.35.0", {"start": v(-122.11, 91.18) * mm, "end": v(-121.1, 90.42) * mm});
            skArc(sketch, "E11.35.1", {"start": v(-122.11, 91.18) * mm, "mid": v(-122.45, 91.74) * mm, "end": v(-122.79, 92.3) * mm});
            skArc(sketch, "E11.35.2", {"start": v(-122.78, 92.4) * mm, "mid": v(-122.8, 92.36) * mm, "end": v(-122.79, 92.3) * mm});
            skLineSegment(sketch, "E11.35.3", {"start": v(-122.78, 92.4) * mm, "end": v(-122.52, 92.75) * mm});
            skLineSegment(sketch, "E11.35.4", {"start": v(-122.26, 93.1) * mm, "end": v(-122.52, 92.75) * mm});
            skArc(sketch, "E11.35.5", {"start": v(-122.18, 93.13) * mm, "mid": v(-122.22, 93.12) * mm, "end": v(-122.26, 93.1) * mm});
            skArc(sketch, "E11.35.6", {"start": v(-120.9, 92.78) * mm, "mid": v(-121.54, 92.96) * mm, "end": v(-122.18, 93.13) * mm});
            skLineSegment(sketch, "E11.35.7", {"start": v(-120.9, 92.78) * mm, "end": v(-119.9, 92) * mm});
            skLineSegment(sketch, "E11.36.0", {"start": v(-124.46, 87.96) * mm, "end": v(-123.42, 87.22) * mm});
            skArc(sketch, "E11.36.1", {"start": v(-124.46, 87.96) * mm, "mid": v(-124.81, 88.5) * mm, "end": v(-125.16, 89.06) * mm});
            skArc(sketch, "E11.36.2", {"start": v(-125.16, 89.16) * mm, "mid": v(-125.18, 89.11) * mm, "end": v(-125.16, 89.06) * mm});
            skLineSegment(sketch, "E11.36.3", {"start": v(-125.16, 89.16) * mm, "end": v(-124.91, 89.5) * mm});
            skLineSegment(sketch, "E11.36.4", {"start": v(-124.65, 89.87) * mm, "end": v(-124.91, 89.5) * mm});
            skArc(sketch, "E11.36.5", {"start": v(-124.58, 89.9) * mm, "mid": v(-124.62, 89.9) * mm, "end": v(-124.65, 89.87) * mm});
            skArc(sketch, "E11.36.6", {"start": v(-123.3, 89.58) * mm, "mid": v(-123.94, 89.74) * mm, "end": v(-124.58, 89.9) * mm});
            skLineSegment(sketch, "E11.36.7", {"start": v(-123.3, 89.58) * mm, "end": v(-122.26, 88.84) * mm});
            skLineSegment(sketch, "E11.37.0", {"start": v(-126.72, 84.67) * mm, "end": v(-125.66, 83.96) * mm});
            skArc(sketch, "E11.37.1", {"start": v(-126.72, 84.67) * mm, "mid": v(-127.09, 85.2) * mm, "end": v(-127.45, 85.75) * mm});
            skArc(sketch, "E11.37.2", {"start": v(-127.45, 85.85) * mm, "mid": v(-127.47, 85.8) * mm, "end": v(-127.45, 85.75) * mm});
            skLineSegment(sketch, "E11.37.3", {"start": v(-127.45, 85.85) * mm, "end": v(-127.21, 86.2) * mm});
            skLineSegment(sketch, "E11.37.4", {"start": v(-126.96, 86.57) * mm, "end": v(-127.21, 86.2) * mm});
            skArc(sketch, "E11.37.5", {"start": v(-126.89, 86.6) * mm, "mid": v(-126.93, 86.6) * mm, "end": v(-126.96, 86.57) * mm});
            skArc(sketch, "E11.37.6", {"start": v(-125.6, 86.32) * mm, "mid": v(-126.24, 86.47) * mm, "end": v(-126.89, 86.6) * mm});
            skLineSegment(sketch, "E11.37.7", {"start": v(-125.6, 86.32) * mm, "end": v(-124.55, 85.6) * mm});
            skLineSegment(sketch, "E11.38.0", {"start": v(-128.89, 81.32) * mm, "end": v(-127.82, 80.64) * mm});
            skArc(sketch, "E11.38.1", {"start": v(-128.89, 81.32) * mm, "mid": v(-129.28, 81.85) * mm, "end": v(-129.65, 82.39) * mm});
            skArc(sketch, "E11.38.2", {"start": v(-129.65, 82.49) * mm, "mid": v(-129.67, 82.44) * mm, "end": v(-129.65, 82.39) * mm});
            skLineSegment(sketch, "E11.38.3", {"start": v(-129.65, 82.49) * mm, "end": v(-129.42, 82.85) * mm});
            skLineSegment(sketch, "E11.38.4", {"start": v(-129.19, 83.22) * mm, "end": v(-129.42, 82.85) * mm});
            skArc(sketch, "E11.38.5", {"start": v(-129.11, 83.25) * mm, "mid": v(-129.15, 83.25) * mm, "end": v(-129.19, 83.22) * mm});
            skArc(sketch, "E11.38.6", {"start": v(-127.81, 83) * mm, "mid": v(-128.46, 83.13) * mm, "end": v(-129.11, 83.25) * mm});
            skLineSegment(sketch, "E11.38.7", {"start": v(-127.81, 83) * mm, "end": v(-126.74, 82.32) * mm});
            skLineSegment(sketch, "E11.39.0", {"start": v(-130.97, 77.92) * mm, "end": v(-129.89, 77.26) * mm});
            skArc(sketch, "E11.39.1", {"start": v(-130.97, 77.92) * mm, "mid": v(-131.37, 78.44) * mm, "end": v(-131.77, 78.97) * mm});
            skArc(sketch, "E11.39.2", {"start": v(-131.77, 79.06) * mm, "mid": v(-131.78, 79.02) * mm, "end": v(-131.77, 78.97) * mm});
            skLineSegment(sketch, "E11.39.3", {"start": v(-131.77, 79.06) * mm, "end": v(-131.55, 79.43) * mm});
            skLineSegment(sketch, "E11.39.4", {"start": v(-131.32, 79.81) * mm, "end": v(-131.55, 79.43) * mm});
            skArc(sketch, "E11.39.5", {"start": v(-131.25, 79.84) * mm, "mid": v(-131.29, 79.84) * mm, "end": v(-131.32, 79.81) * mm});
            skArc(sketch, "E11.39.6", {"start": v(-129.94, 79.63) * mm, "mid": v(-130.6, 79.74) * mm, "end": v(-131.25, 79.84) * mm});
            skLineSegment(sketch, "E11.39.7", {"start": v(-129.94, 79.63) * mm, "end": v(-128.86, 78.97) * mm});
            skLineSegment(sketch, "E11.40.0", {"start": v(-132.97, 74.47) * mm, "end": v(-131.86, 73.84) * mm});
            skArc(sketch, "E11.40.1", {"start": v(-132.97, 74.47) * mm, "mid": v(-133.38, 74.97) * mm, "end": v(-133.79, 75.5) * mm});
            skArc(sketch, "E11.40.2", {"start": v(-133.8, 75.59) * mm, "mid": v(-133.8, 75.54) * mm, "end": v(-133.79, 75.5) * mm});
            skLineSegment(sketch, "E11.40.3", {"start": v(-133.8, 75.59) * mm, "end": v(-133.58, 75.96) * mm});
            skLineSegment(sketch, "E11.40.4", {"start": v(-133.36, 76.35) * mm, "end": v(-133.58, 75.96) * mm});
            skArc(sketch, "E11.40.5", {"start": v(-133.3, 76.38) * mm, "mid": v(-133.33, 76.37) * mm, "end": v(-133.36, 76.35) * mm});
            skArc(sketch, "E11.40.6", {"start": v(-131.98, 76.2) * mm, "mid": v(-132.64, 76.3) * mm, "end": v(-133.3, 76.38) * mm});
            skLineSegment(sketch, "E11.40.7", {"start": v(-131.98, 76.2) * mm, "end": v(-130.88, 75.57) * mm});
            skLineSegment(sketch, "E11.41.0", {"start": v(-134.87, 70.96) * mm, "end": v(-133.75, 70.36) * mm});
            skArc(sketch, "E11.41.1", {"start": v(-134.87, 70.96) * mm, "mid": v(-135.3, 71.46) * mm, "end": v(-135.72, 71.96) * mm});
            skArc(sketch, "E11.41.2", {"start": v(-135.73, 72.06) * mm, "mid": v(-135.74, 72) * mm, "end": v(-135.72, 71.96) * mm});
            skLineSegment(sketch, "E11.41.3", {"start": v(-135.73, 72.06) * mm, "end": v(-135.53, 72.44) * mm});
            skLineSegment(sketch, "E11.41.4", {"start": v(-135.32, 72.83) * mm, "end": v(-135.53, 72.44) * mm});
            skArc(sketch, "E11.41.5", {"start": v(-135.25, 72.87) * mm, "mid": v(-135.29, 72.86) * mm, "end": v(-135.32, 72.83) * mm});
            skArc(sketch, "E11.41.6", {"start": v(-133.93, 72.72) * mm, "mid": v(-134.59, 72.8) * mm, "end": v(-135.25, 72.87) * mm});
            skLineSegment(sketch, "E11.41.7", {"start": v(-133.93, 72.72) * mm, "end": v(-132.81, 72.12) * mm});
            skLineSegment(sketch, "E11.42.0", {"start": v(-136.68, 67.4) * mm, "end": v(-135.55, 66.84) * mm});
            skArc(sketch, "E11.42.1", {"start": v(-136.68, 67.4) * mm, "mid": v(-137.12, 67.9) * mm, "end": v(-137.55, 68.39) * mm});
            skArc(sketch, "E11.42.2", {"start": v(-137.57, 68.48) * mm, "mid": v(-137.58, 68.43) * mm, "end": v(-137.55, 68.39) * mm});
            skLineSegment(sketch, "E11.42.3", {"start": v(-137.57, 68.48) * mm, "end": v(-137.38, 68.87) * mm});
            skLineSegment(sketch, "E11.42.4", {"start": v(-137.18, 69.26) * mm, "end": v(-137.38, 68.87) * mm});
            skArc(sketch, "E11.42.5", {"start": v(-137.1, 69.3) * mm, "mid": v(-137.15, 69.3) * mm, "end": v(-137.18, 69.26) * mm});
            skArc(sketch, "E11.42.6", {"start": v(-135.79, 69.19) * mm, "mid": v(-136.45, 69.25) * mm, "end": v(-137.1, 69.3) * mm});
            skLineSegment(sketch, "E11.42.7", {"start": v(-135.79, 69.19) * mm, "end": v(-134.65, 68.62) * mm});
            skLineSegment(sketch, "E11.43.0", {"start": v(-138.4, 63.8) * mm, "end": v(-137.25, 63.26) * mm});
            skArc(sketch, "E11.43.1", {"start": v(-138.4, 63.8) * mm, "mid": v(-138.85, 64.28) * mm, "end": v(-139.3, 64.76) * mm});
            skArc(sketch, "E11.43.2", {"start": v(-139.31, 64.86) * mm, "mid": v(-139.32, 64.8) * mm, "end": v(-139.3, 64.76) * mm});
            skLineSegment(sketch, "E11.43.3", {"start": v(-139.31, 64.86) * mm, "end": v(-139.13, 65.25) * mm});
            skLineSegment(sketch, "E11.43.4", {"start": v(-138.94, 65.65) * mm, "end": v(-139.13, 65.25) * mm});
            skArc(sketch, "E11.43.5", {"start": v(-138.87, 65.69) * mm, "mid": v(-138.91, 65.68) * mm, "end": v(-138.94, 65.65) * mm});
            skArc(sketch, "E11.43.6", {"start": v(-137.55, 65.6) * mm, "mid": v(-138.21, 65.65) * mm, "end": v(-138.87, 65.69) * mm});
            skLineSegment(sketch, "E11.43.7", {"start": v(-137.55, 65.6) * mm, "end": v(-136.4, 65.07) * mm});
            skLineSegment(sketch, "E11.44.0", {"start": v(-140.02, 60.16) * mm, "end": v(-138.86, 59.65) * mm});
            skArc(sketch, "E11.44.1", {"start": v(-140.02, 60.16) * mm, "mid": v(-140.49, 60.62) * mm, "end": v(-140.95, 61.1) * mm});
            skArc(sketch, "E11.44.2", {"start": v(-140.96, 61.19) * mm, "mid": v(-140.97, 61.14) * mm, "end": v(-140.95, 61.1) * mm});
            skLineSegment(sketch, "E11.44.3", {"start": v(-140.96, 61.19) * mm, "end": v(-140.8, 61.58) * mm});
            skLineSegment(sketch, "E11.44.4", {"start": v(-140.61, 61.99) * mm, "end": v(-140.8, 61.58) * mm});
            skArc(sketch, "E11.44.5", {"start": v(-140.55, 62.03) * mm, "mid": v(-140.59, 62.02) * mm, "end": v(-140.61, 61.99) * mm});
            skArc(sketch, "E11.44.6", {"start": v(-139.22, 61.99) * mm, "mid": v(-139.89, 62.01) * mm, "end": v(-140.55, 62.03) * mm});
            skLineSegment(sketch, "E11.44.7", {"start": v(-139.22, 61.99) * mm, "end": v(-138.06, 61.48) * mm});
            skLineSegment(sketch, "E11.45.0", {"start": v(-141.55, 56.47) * mm, "end": v(-140.37, 56) * mm});
            skArc(sketch, "E11.45.1", {"start": v(-141.55, 56.47) * mm, "mid": v(-142.03, 56.92) * mm, "end": v(-142.5, 57.38) * mm});
            skArc(sketch, "E11.45.2", {"start": v(-142.52, 57.48) * mm, "mid": v(-142.52, 57.43) * mm, "end": v(-142.5, 57.38) * mm});
            skLineSegment(sketch, "E11.45.3", {"start": v(-142.52, 57.48) * mm, "end": v(-142.36, 57.88) * mm});
            skLineSegment(sketch, "E11.45.4", {"start": v(-142.19, 58.29) * mm, "end": v(-142.36, 57.88) * mm});
            skArc(sketch, "E11.45.5", {"start": v(-142.12, 58.33) * mm, "mid": v(-142.16, 58.32) * mm, "end": v(-142.19, 58.29) * mm});
            skArc(sketch, "E11.45.6", {"start": v(-140.8, 58.32) * mm, "mid": v(-141.46, 58.33) * mm, "end": v(-142.12, 58.33) * mm});
            skLineSegment(sketch, "E11.45.7", {"start": v(-140.8, 58.32) * mm, "end": v(-139.62, 57.84) * mm});
            skLineSegment(sketch, "E11.46.0", {"start": v(-142.98, 52.75) * mm, "end": v(-141.8, 52.3) * mm});
            skArc(sketch, "E11.46.1", {"start": v(-142.98, 52.75) * mm, "mid": v(-143.47, 53.19) * mm, "end": v(-143.95, 53.63) * mm});
            skArc(sketch, "E11.46.2", {"start": v(-143.97, 53.73) * mm, "mid": v(-143.97, 53.68) * mm, "end": v(-143.95, 53.63) * mm});
            skLineSegment(sketch, "E11.46.3", {"start": v(-143.97, 53.73) * mm, "end": v(-143.82, 54.13) * mm});
            skLineSegment(sketch, "E11.46.4", {"start": v(-143.66, 54.54) * mm, "end": v(-143.82, 54.13) * mm});
            skArc(sketch, "E11.46.5", {"start": v(-143.6, 54.59) * mm, "mid": v(-143.64, 54.58) * mm, "end": v(-143.66, 54.54) * mm});
            skArc(sketch, "E11.46.6", {"start": v(-142.28, 54.62) * mm, "mid": v(-142.94, 54.6) * mm, "end": v(-143.6, 54.59) * mm});
            skLineSegment(sketch, "E11.46.7", {"start": v(-142.28, 54.62) * mm, "end": v(-141.09, 54.17) * mm});
            skLineSegment(sketch, "E11.47.0", {"start": v(-144.31, 48.99) * mm, "end": v(-143.11, 48.57) * mm});
            skArc(sketch, "E11.47.1", {"start": v(-144.31, 48.99) * mm, "mid": v(-144.81, 49.41) * mm, "end": v(-145.3, 49.85) * mm});
            skArc(sketch, "E11.47.2", {"start": v(-145.33, 49.94) * mm, "mid": v(-145.33, 49.89) * mm, "end": v(-145.3, 49.85) * mm});
            skLineSegment(sketch, "E11.47.3", {"start": v(-145.33, 49.94) * mm, "end": v(-145.19, 50.35) * mm});
            skLineSegment(sketch, "E11.47.4", {"start": v(-145.04, 50.76) * mm, "end": v(-145.19, 50.35) * mm});
            skArc(sketch, "E11.47.5", {"start": v(-144.98, 50.81) * mm, "mid": v(-145.02, 50.8) * mm, "end": v(-145.04, 50.76) * mm});
            skArc(sketch, "E11.47.6", {"start": v(-143.66, 50.87) * mm, "mid": v(-144.32, 50.85) * mm, "end": v(-144.98, 50.81) * mm});
            skLineSegment(sketch, "E11.47.7", {"start": v(-143.66, 50.87) * mm, "end": v(-142.46, 50.46) * mm});
            skLineSegment(sketch, "E11.48.0", {"start": v(-145.55, 45.2) * mm, "end": v(-144.33, 44.8) * mm});
            skArc(sketch, "E11.48.1", {"start": v(-145.55, 45.2) * mm, "mid": v(-146.06, 45.6) * mm, "end": v(-146.56, 46.02) * mm});
            skArc(sketch, "E11.48.2", {"start": v(-146.59, 46.12) * mm, "mid": v(-146.59, 46.07) * mm, "end": v(-146.56, 46.02) * mm});
            skLineSegment(sketch, "E11.48.3", {"start": v(-146.59, 46.12) * mm, "end": v(-146.46, 46.53) * mm});
            skLineSegment(sketch, "E11.48.4", {"start": v(-146.32, 46.95) * mm, "end": v(-146.46, 46.53) * mm});
            skArc(sketch, "E11.48.5", {"start": v(-146.26, 47) * mm, "mid": v(-146.3, 46.98) * mm, "end": v(-146.32, 46.95) * mm});
            skArc(sketch, "E11.48.6", {"start": v(-144.94, 47.1) * mm, "mid": v(-145.6, 47.05) * mm, "end": v(-146.26, 47) * mm});
            skLineSegment(sketch, "E11.48.7", {"start": v(-144.94, 47.1) * mm, "end": v(-143.73, 46.7) * mm});
            skLineSegment(sketch, "E11.49.0", {"start": v(-146.68, 41.37) * mm, "end": v(-145.46, 41.01) * mm});
            skArc(sketch, "E11.49.1", {"start": v(-146.68, 41.37) * mm, "mid": v(-147.2, 41.77) * mm, "end": v(-147.71, 42.17) * mm});
            skArc(sketch, "E11.49.2", {"start": v(-147.74, 42.27) * mm, "mid": v(-147.74, 42.21) * mm, "end": v(-147.71, 42.17) * mm});
            skLineSegment(sketch, "E11.49.3", {"start": v(-147.74, 42.27) * mm, "end": v(-147.63, 42.68) * mm});
            skLineSegment(sketch, "E11.49.4", {"start": v(-147.5, 43.1) * mm, "end": v(-147.63, 42.68) * mm});
            skArc(sketch, "E11.49.5", {"start": v(-147.44, 43.15) * mm, "mid": v(-147.48, 43.14) * mm, "end": v(-147.5, 43.1) * mm});
            skArc(sketch, "E11.49.6", {"start": v(-146.12, 43.28) * mm, "mid": v(-146.78, 43.22) * mm, "end": v(-147.44, 43.15) * mm});
            skLineSegment(sketch, "E11.49.7", {"start": v(-146.12, 43.28) * mm, "end": v(-144.9, 42.93) * mm});
            skLineSegment(sketch, "E11.50.0", {"start": v(-147.71, 37.51) * mm, "end": v(-146.48, 37.2) * mm});
            skArc(sketch, "E11.50.1", {"start": v(-147.71, 37.51) * mm, "mid": v(-148.24, 37.9) * mm, "end": v(-148.77, 38.3) * mm});
            skArc(sketch, "E11.50.2", {"start": v(-148.8, 38.38) * mm, "mid": v(-148.8, 38.33) * mm, "end": v(-148.77, 38.3) * mm});
            skLineSegment(sketch, "E11.50.3", {"start": v(-148.8, 38.38) * mm, "end": v(-148.7, 38.8) * mm});
            skLineSegment(sketch, "E11.50.4", {"start": v(-148.58, 39.23) * mm, "end": v(-148.7, 38.8) * mm});
            skArc(sketch, "E11.50.5", {"start": v(-148.52, 39.28) * mm, "mid": v(-148.56, 39.26) * mm, "end": v(-148.58, 39.23) * mm});
            skArc(sketch, "E11.50.6", {"start": v(-147.2, 39.44) * mm, "mid": v(-147.86, 39.37) * mm, "end": v(-148.52, 39.28) * mm});
            skLineSegment(sketch, "E11.50.7", {"start": v(-147.2, 39.44) * mm, "end": v(-145.98, 39.12) * mm});
            skLineSegment(sketch, "E11.51.0", {"start": v(-148.64, 33.63) * mm, "end": v(-147.4, 33.35) * mm});
            skArc(sketch, "E11.51.1", {"start": v(-148.64, 33.63) * mm, "mid": v(-149.18, 34) * mm, "end": v(-149.72, 34.38) * mm});
            skArc(sketch, "E11.51.2", {"start": v(-149.75, 34.48) * mm, "mid": v(-149.75, 34.42) * mm, "end": v(-149.72, 34.38) * mm});
            skLineSegment(sketch, "E11.51.3", {"start": v(-149.75, 34.48) * mm, "end": v(-149.66, 34.9) * mm});
            skLineSegment(sketch, "E11.51.4", {"start": v(-149.55, 35.32) * mm, "end": v(-149.66, 34.9) * mm});
            skArc(sketch, "E11.51.5", {"start": v(-149.5, 35.38) * mm, "mid": v(-149.53, 35.36) * mm, "end": v(-149.55, 35.32) * mm});
            skArc(sketch, "E11.51.6", {"start": v(-148.19, 35.58) * mm, "mid": v(-148.84, 35.48) * mm, "end": v(-149.5, 35.38) * mm});
            skLineSegment(sketch, "E11.51.7", {"start": v(-148.19, 35.58) * mm, "end": v(-146.95, 35.29) * mm});
            skLineSegment(sketch, "E11.52.0", {"start": v(-149.47, 29.73) * mm, "end": v(-148.23, 29.48) * mm});
            skArc(sketch, "E11.52.1", {"start": v(-149.47, 29.73) * mm, "mid": v(-150.02, 30.09) * mm, "end": v(-150.57, 30.45) * mm});
            skArc(sketch, "E11.52.2", {"start": v(-150.6, 30.54) * mm, "mid": v(-150.6, 30.5) * mm, "end": v(-150.57, 30.45) * mm});
            skLineSegment(sketch, "E11.52.3", {"start": v(-150.6, 30.54) * mm, "end": v(-150.52, 30.97) * mm});
            skLineSegment(sketch, "E11.52.4", {"start": v(-150.43, 31.4) * mm, "end": v(-150.52, 30.97) * mm});
            skArc(sketch, "E11.52.5", {"start": v(-150.37, 31.45) * mm, "mid": v(-150.4, 31.43) * mm, "end": v(-150.43, 31.4) * mm});
            skArc(sketch, "E11.52.6", {"start": v(-149.07, 31.69) * mm, "mid": v(-149.72, 31.58) * mm, "end": v(-150.37, 31.45) * mm});
            skLineSegment(sketch, "E11.52.7", {"start": v(-149.07, 31.69) * mm, "end": v(-147.83, 31.43) * mm});
            skLineSegment(sketch, "E11.53.0", {"start": v(-150.2, 25.8) * mm, "end": v(-148.95, 25.59) * mm});
            skArc(sketch, "E11.53.1", {"start": v(-150.2, 25.8) * mm, "mid": v(-150.76, 26.15) * mm, "end": v(-151.31, 26.5) * mm});
            skArc(sketch, "E11.53.2", {"start": v(-151.35, 26.6) * mm, "mid": v(-151.35, 26.54) * mm, "end": v(-151.31, 26.5) * mm});
            skLineSegment(sketch, "E11.53.3", {"start": v(-151.35, 26.6) * mm, "end": v(-151.28, 27.01) * mm});
            skLineSegment(sketch, "E11.53.4", {"start": v(-151.2, 27.45) * mm, "end": v(-151.28, 27.01) * mm});
            skArc(sketch, "E11.53.5", {"start": v(-151.14, 27.5) * mm, "mid": v(-151.18, 27.49) * mm, "end": v(-151.2, 27.45) * mm});
            skArc(sketch, "E11.53.6", {"start": v(-149.85, 27.77) * mm, "mid": v(-150.5, 27.64) * mm, "end": v(-151.14, 27.5) * mm});
            skLineSegment(sketch, "E11.53.7", {"start": v(-149.85, 27.77) * mm, "end": v(-148.6, 27.55) * mm});
            skLineSegment(sketch, "E11.54.0", {"start": v(-150.82, 21.87) * mm, "end": v(-149.57, 21.68) * mm});
            skArc(sketch, "E11.54.1", {"start": v(-150.82, 21.87) * mm, "mid": v(-151.4, 22.2) * mm, "end": v(-151.95, 22.53) * mm});
            skArc(sketch, "E11.54.2", {"start": v(-152, 22.62) * mm, "mid": v(-151.99, 22.57) * mm, "end": v(-151.95, 22.53) * mm});
            skLineSegment(sketch, "E11.54.3", {"start": v(-152, 22.62) * mm, "end": v(-151.93, 23.05) * mm});
            skLineSegment(sketch, "E11.54.4", {"start": v(-151.87, 23.48) * mm, "end": v(-151.93, 23.05) * mm});
            skArc(sketch, "E11.54.5", {"start": v(-151.81, 23.54) * mm, "mid": v(-151.85, 23.52) * mm, "end": v(-151.87, 23.48) * mm});
            skArc(sketch, "E11.54.6", {"start": v(-150.52, 23.84) * mm, "mid": v(-151.17, 23.7) * mm, "end": v(-151.81, 23.54) * mm});
            skLineSegment(sketch, "E11.54.7", {"start": v(-150.52, 23.84) * mm, "end": v(-149.27, 23.65) * mm});
            skLineSegment(sketch, "E11.55.0", {"start": v(-151.34, 17.91) * mm, "end": v(-150.08, 17.76) * mm});
            skArc(sketch, "E11.55.1", {"start": v(-151.34, 17.91) * mm, "mid": v(-151.92, 18.22) * mm, "end": v(-152.5, 18.55) * mm});
            skArc(sketch, "E11.55.2", {"start": v(-152.54, 18.63) * mm, "mid": v(-152.53, 18.58) * mm, "end": v(-152.5, 18.55) * mm});
            skLineSegment(sketch, "E11.55.3", {"start": v(-152.54, 18.63) * mm, "end": v(-152.48, 19.06) * mm});
            skLineSegment(sketch, "E11.55.4", {"start": v(-152.43, 19.5) * mm, "end": v(-152.48, 19.06) * mm});
            skArc(sketch, "E11.55.5", {"start": v(-152.38, 19.56) * mm, "mid": v(-152.41, 19.54) * mm, "end": v(-152.43, 19.5) * mm});
            skArc(sketch, "E11.55.6", {"start": v(-151.1, 19.9) * mm, "mid": v(-151.74, 19.73) * mm, "end": v(-152.38, 19.56) * mm});
            skLineSegment(sketch, "E11.55.7", {"start": v(-151.1, 19.9) * mm, "end": v(-149.84, 19.73) * mm});
            skLineSegment(sketch, "E11.56.0", {"start": v(-151.76, 13.94) * mm, "end": v(-150.5, 13.82) * mm});
            skArc(sketch, "E11.56.1", {"start": v(-151.76, 13.94) * mm, "mid": v(-152.35, 14.24) * mm, "end": v(-152.93, 14.55) * mm});
            skArc(sketch, "E11.56.2", {"start": v(-152.97, 14.63) * mm, "mid": v(-152.96, 14.58) * mm, "end": v(-152.93, 14.55) * mm});
            skLineSegment(sketch, "E11.56.3", {"start": v(-152.97, 14.63) * mm, "end": v(-152.93, 15.06) * mm});
            skLineSegment(sketch, "E11.56.4", {"start": v(-152.89, 15.5) * mm, "end": v(-152.93, 15.06) * mm});
            skArc(sketch, "E11.56.5", {"start": v(-152.84, 15.56) * mm, "mid": v(-152.87, 15.54) * mm, "end": v(-152.89, 15.5) * mm});
            skArc(sketch, "E11.56.6", {"start": v(-151.57, 15.93) * mm, "mid": v(-152.2, 15.75) * mm, "end": v(-152.84, 15.56) * mm});
            skLineSegment(sketch, "E11.56.7", {"start": v(-151.57, 15.93) * mm, "end": v(-150.3, 15.8) * mm});
            skLineSegment(sketch, "E11.57.0", {"start": v(-152.07, 9.97) * mm, "end": v(-150.8, 9.88) * mm});
            skArc(sketch, "E11.57.1", {"start": v(-152.07, 9.97) * mm, "mid": v(-152.67, 10.25) * mm, "end": v(-153.25, 10.54) * mm});
            skArc(sketch, "E11.57.2", {"start": v(-153.3, 10.62) * mm, "mid": v(-153.3, 10.58) * mm, "end": v(-153.25, 10.54) * mm});
            skLineSegment(sketch, "E11.57.3", {"start": v(-153.3, 10.62) * mm, "end": v(-153.27, 11.05) * mm});
            skLineSegment(sketch, "E11.57.4", {"start": v(-153.24, 11.5) * mm, "end": v(-153.27, 11.05) * mm});
            skArc(sketch, "E11.57.5", {"start": v(-153.2, 11.56) * mm, "mid": v(-153.22, 11.53) * mm, "end": v(-153.24, 11.5) * mm});
            skArc(sketch, "E11.57.6", {"start": v(-151.93, 11.96) * mm, "mid": v(-152.56, 11.76) * mm, "end": v(-153.2, 11.56) * mm});
            skLineSegment(sketch, "E11.57.7", {"start": v(-151.93, 11.96) * mm, "end": v(-150.66, 11.87) * mm});
            skLineSegment(sketch, "E11.58.0", {"start": v(-152.28, 5.98) * mm, "end": v(-151.01, 5.93) * mm});
            skArc(sketch, "E11.58.1", {"start": v(-152.28, 5.98) * mm, "mid": v(-152.88, 6.25) * mm, "end": v(-153.48, 6.52) * mm});
            skArc(sketch, "E11.58.2", {"start": v(-153.53, 6.6) * mm, "mid": v(-153.52, 6.56) * mm, "end": v(-153.48, 6.52) * mm});
            skLineSegment(sketch, "E11.58.3", {"start": v(-153.53, 6.6) * mm, "end": v(-153.5, 7.04) * mm});
            skLineSegment(sketch, "E11.58.4", {"start": v(-153.49, 7.48) * mm, "end": v(-153.5, 7.04) * mm});
            skArc(sketch, "E11.58.5", {"start": v(-153.44, 7.54) * mm, "mid": v(-153.47, 7.52) * mm, "end": v(-153.49, 7.48) * mm});
            skArc(sketch, "E11.58.6", {"start": v(-152.2, 7.98) * mm, "mid": v(-152.82, 7.76) * mm, "end": v(-153.44, 7.54) * mm});
            skLineSegment(sketch, "E11.58.7", {"start": v(-152.2, 7.98) * mm, "end": v(-150.92, 7.92) * mm});
            skLineSegment(sketch, "E11.59.0", {"start": v(-152.39, 2) * mm, "end": v(-151.12, 1.97) * mm});
            skArc(sketch, "E11.59.1", {"start": v(-152.39, 2) * mm, "mid": v(-153, 2.24) * mm, "end": v(-153.6, 2.5) * mm});
            skArc(sketch, "E11.59.2", {"start": v(-153.65, 2.59) * mm, "mid": v(-153.63, 2.54) * mm, "end": v(-153.6, 2.5) * mm});
            skLineSegment(sketch, "E11.59.3", {"start": v(-153.65, 2.59) * mm, "end": v(-153.64, 3.02) * mm});
            skLineSegment(sketch, "E11.59.4", {"start": v(-153.63, 3.46) * mm, "end": v(-153.64, 3.02) * mm});
            skArc(sketch, "E11.59.5", {"start": v(-153.59, 3.52) * mm, "mid": v(-153.62, 3.5) * mm, "end": v(-153.63, 3.46) * mm});
            skArc(sketch, "E11.59.6", {"start": v(-152.35, 3.99) * mm, "mid": v(-152.97, 3.76) * mm, "end": v(-153.59, 3.52) * mm});
            skLineSegment(sketch, "E11.59.7", {"start": v(-152.35, 3.99) * mm, "end": v(-151.08, 3.96) * mm});
            skLineSegment(sketch, "E11.60.0", {"start": v(-152.39, -2) * mm, "end": v(-151.12, -1.99) * mm});
            skArc(sketch, "E11.60.1", {"start": v(-152.39, -2) * mm, "mid": v(-153, -1.76) * mm, "end": v(-153.6, -1.52) * mm});
            skArc(sketch, "E11.60.2", {"start": v(-153.66, -1.44) * mm, "mid": v(-153.65, -1.48) * mm, "end": v(-153.6, -1.52) * mm});
            skLineSegment(sketch, "E11.60.3", {"start": v(-153.66, -1.44) * mm, "end": v(-153.67, -1) * mm});
            skLineSegment(sketch, "E11.60.4", {"start": v(-153.67, -0.56) * mm, "end": v(-153.67, -1) * mm});
            skArc(sketch, "E11.60.5", {"start": v(-153.63, -0.5) * mm, "mid": v(-153.66, -0.52) * mm, "end": v(-153.67, -0.56) * mm});
            skArc(sketch, "E11.60.6", {"start": v(-152.4, 0) * mm, "mid": v(-153.01, -0.24) * mm, "end": v(-153.63, -0.5) * mm});
            skLineSegment(sketch, "E11.60.7", {"start": v(-152.4, 0) * mm, "end": v(-151.13, 0) * mm});
            skLineSegment(sketch, "E11.61.0", {"start": v(-152.28, -5.98) * mm, "end": v(-151.01, -5.94) * mm});
            skArc(sketch, "E11.61.1", {"start": v(-152.28, -5.98) * mm, "mid": v(-152.9, -5.77) * mm, "end": v(-153.52, -5.54) * mm});
            skArc(sketch, "E11.61.2", {"start": v(-153.57, -5.46) * mm, "mid": v(-153.56, -5.5) * mm, "end": v(-153.52, -5.54) * mm});
            skLineSegment(sketch, "E11.61.3", {"start": v(-153.57, -5.46) * mm, "end": v(-153.59, -5.03) * mm});
            skLineSegment(sketch, "E11.61.4", {"start": v(-153.6, -4.59) * mm, "end": v(-153.59, -5.03) * mm});
            skArc(sketch, "E11.61.5", {"start": v(-153.56, -4.52) * mm, "mid": v(-153.6, -4.55) * mm, "end": v(-153.6, -4.59) * mm});
            skArc(sketch, "E11.61.6", {"start": v(-152.35, -3.99) * mm, "mid": v(-152.96, -4.25) * mm, "end": v(-153.56, -4.52) * mm});
            skLineSegment(sketch, "E11.61.7", {"start": v(-152.35, -3.99) * mm, "end": v(-151.08, -3.95) * mm});
            skLineSegment(sketch, "E11.62.0", {"start": v(-152.07, -9.97) * mm, "end": v(-150.8, -9.9) * mm});
            skArc(sketch, "E11.62.1", {"start": v(-152.07, -9.97) * mm, "mid": v(-152.7, -9.77) * mm, "end": v(-153.32, -9.55) * mm});
            skArc(sketch, "E11.62.2", {"start": v(-153.38, -9.48) * mm, "mid": v(-153.36, -9.52) * mm, "end": v(-153.32, -9.55) * mm});
            skLineSegment(sketch, "E11.62.3", {"start": v(-153.38, -9.48) * mm, "end": v(-153.4, -9.05) * mm});
            skLineSegment(sketch, "E11.62.4", {"start": v(-153.43, -8.6) * mm, "end": v(-153.4, -9.05) * mm});
            skArc(sketch, "E11.62.5", {"start": v(-153.39, -8.54) * mm, "mid": v(-153.42, -8.57) * mm, "end": v(-153.43, -8.6) * mm});
            skArc(sketch, "E11.62.6", {"start": v(-152.2, -7.98) * mm, "mid": v(-152.8, -8.25) * mm, "end": v(-153.39, -8.54) * mm});
            skLineSegment(sketch, "E11.62.7", {"start": v(-152.2, -7.98) * mm, "end": v(-150.92, -7.9) * mm});
            skLineSegment(sketch, "E11.63.0", {"start": v(-151.76, -13.94) * mm, "end": v(-150.5, -13.84) * mm});
            skArc(sketch, "E11.63.1", {"start": v(-151.76, -13.94) * mm, "mid": v(-152.39, -13.76) * mm, "end": v(-153.02, -13.56) * mm});
            skArc(sketch, "E11.63.2", {"start": v(-153.08, -13.49) * mm, "mid": v(-153.06, -13.54) * mm, "end": v(-153.02, -13.56) * mm});
            skLineSegment(sketch, "E11.63.3", {"start": v(-153.08, -13.49) * mm, "end": v(-153.11, -13.06) * mm});
            skLineSegment(sketch, "E11.63.4", {"start": v(-153.15, -12.62) * mm, "end": v(-153.11, -13.06) * mm});
            skArc(sketch, "E11.63.5", {"start": v(-153.11, -12.55) * mm, "mid": v(-153.14, -12.58) * mm, "end": v(-153.15, -12.62) * mm});
            skArc(sketch, "E11.63.6", {"start": v(-151.93, -11.96) * mm, "mid": v(-152.52, -12.25) * mm, "end": v(-153.11, -12.55) * mm});
            skLineSegment(sketch, "E11.63.7", {"start": v(-151.93, -11.96) * mm, "end": v(-150.66, -11.85) * mm});
            skLineSegment(sketch, "E11.64.0", {"start": v(-151.34, -17.91) * mm, "end": v(-150.08, -17.77) * mm});
            skArc(sketch, "E11.64.1", {"start": v(-151.34, -17.91) * mm, "mid": v(-151.98, -17.74) * mm, "end": v(-152.6, -17.57) * mm});
            skArc(sketch, "E11.64.2", {"start": v(-152.67, -17.5) * mm, "mid": v(-152.65, -17.54) * mm, "end": v(-152.6, -17.57) * mm});
            skLineSegment(sketch, "E11.64.3", {"start": v(-152.67, -17.5) * mm, "end": v(-152.72, -17.06) * mm});
            skLineSegment(sketch, "E11.64.4", {"start": v(-152.77, -16.62) * mm, "end": v(-152.72, -17.06) * mm});
            skArc(sketch, "E11.64.5", {"start": v(-152.73, -16.55) * mm, "mid": v(-152.76, -16.58) * mm, "end": v(-152.77, -16.62) * mm});
            skArc(sketch, "E11.64.6", {"start": v(-151.57, -15.93) * mm, "mid": v(-152.15, -16.24) * mm, "end": v(-152.73, -16.55) * mm});
            skLineSegment(sketch, "E11.64.7", {"start": v(-151.57, -15.93) * mm, "end": v(-150.3, -15.79) * mm});
            skLineSegment(sketch, "E11.65.0", {"start": v(-150.82, -21.87) * mm, "end": v(-149.56, -21.7) * mm});
            skArc(sketch, "E11.65.1", {"start": v(-150.82, -21.87) * mm, "mid": v(-151.46, -21.72) * mm, "end": v(-152.1, -21.55) * mm});
            skArc(sketch, "E11.65.2", {"start": v(-152.16, -21.48) * mm, "mid": v(-152.14, -21.53) * mm, "end": v(-152.1, -21.55) * mm});
            skLineSegment(sketch, "E11.65.3", {"start": v(-152.16, -21.48) * mm, "end": v(-152.22, -21.05) * mm});
            skLineSegment(sketch, "E11.65.4", {"start": v(-152.28, -20.62) * mm, "end": v(-152.22, -21.05) * mm});
            skArc(sketch, "E11.65.5", {"start": v(-152.25, -20.55) * mm, "mid": v(-152.27, -20.58) * mm, "end": v(-152.28, -20.62) * mm});
            skArc(sketch, "E11.65.6", {"start": v(-151.1, -19.9) * mm, "mid": v(-151.67, -20.21) * mm, "end": v(-152.25, -20.55) * mm});
            skLineSegment(sketch, "E11.65.7", {"start": v(-151.1, -19.9) * mm, "end": v(-149.84, -19.72) * mm});
            skLineSegment(sketch, "E11.66.0", {"start": v(-150.2, -25.8) * mm, "end": v(-148.95, -25.6) * mm});
            skArc(sketch, "E11.66.1", {"start": v(-150.2, -25.8) * mm, "mid": v(-150.84, -25.67) * mm, "end": v(-151.48, -25.53) * mm});
            skArc(sketch, "E11.66.2", {"start": v(-151.55, -25.46) * mm, "mid": v(-151.52, -25.5) * mm, "end": v(-151.48, -25.53) * mm});
            skLineSegment(sketch, "E11.66.3", {"start": v(-151.55, -25.46) * mm, "end": v(-151.62, -25.03) * mm});
            skLineSegment(sketch, "E11.66.4", {"start": v(-151.69, -24.6) * mm, "end": v(-151.62, -25.03) * mm});
            skArc(sketch, "E11.66.5", {"start": v(-151.66, -24.52) * mm, "mid": v(-151.68, -24.56) * mm, "end": v(-151.69, -24.6) * mm});
            skArc(sketch, "E11.66.6", {"start": v(-150.52, -23.84) * mm, "mid": v(-151.1, -24.18) * mm, "end": v(-151.66, -24.52) * mm});
            skLineSegment(sketch, "E11.66.7", {"start": v(-150.52, -23.84) * mm, "end": v(-149.27, -23.63) * mm});
            skLineSegment(sketch, "E11.67.0", {"start": v(-149.47, -29.73) * mm, "end": v(-148.22, -29.5) * mm});
            skArc(sketch, "E11.67.1", {"start": v(-149.47, -29.73) * mm, "mid": v(-150.12, -29.61) * mm, "end": v(-150.76, -29.48) * mm});
            skArc(sketch, "E11.67.2", {"start": v(-150.83, -29.41) * mm, "mid": v(-150.8, -29.46) * mm, "end": v(-150.76, -29.48) * mm});
            skLineSegment(sketch, "E11.67.3", {"start": v(-150.83, -29.41) * mm, "end": v(-150.91, -29) * mm});
            skLineSegment(sketch, "E11.67.4", {"start": v(-151, -28.56) * mm, "end": v(-150.91, -29) * mm});
            skArc(sketch, "E11.67.5", {"start": v(-150.96, -28.49) * mm, "mid": v(-150.99, -28.52) * mm, "end": v(-151, -28.56) * mm});
            skArc(sketch, "E11.67.6", {"start": v(-149.85, -27.77) * mm, "mid": v(-150.4, -28.12) * mm, "end": v(-150.96, -28.49) * mm});
            skLineSegment(sketch, "E11.67.7", {"start": v(-149.85, -27.77) * mm, "end": v(-148.6, -27.53) * mm});
            skLineSegment(sketch, "E11.68.0", {"start": v(-148.64, -33.63) * mm, "end": v(-147.4, -33.36) * mm});
            skArc(sketch, "E11.68.1", {"start": v(-148.64, -33.63) * mm, "mid": v(-149.3, -33.53) * mm, "end": v(-149.94, -33.42) * mm});
            skArc(sketch, "E11.68.2", {"start": v(-150, -33.35) * mm, "mid": v(-149.98, -33.4) * mm, "end": v(-149.94, -33.42) * mm});
            skLineSegment(sketch, "E11.68.3", {"start": v(-150, -33.35) * mm, "end": v(-150.1, -32.93) * mm});
            skLineSegment(sketch, "E11.68.4", {"start": v(-150.2, -32.5) * mm, "end": v(-150.1, -32.93) * mm});
            skArc(sketch, "E11.68.5", {"start": v(-150.16, -32.43) * mm, "mid": v(-150.2, -32.46) * mm, "end": v(-150.2, -32.5) * mm});
            skArc(sketch, "E11.68.6", {"start": v(-149.07, -31.69) * mm, "mid": v(-149.62, -32.05) * mm, "end": v(-150.16, -32.43) * mm});
            skLineSegment(sketch, "E11.68.7", {"start": v(-149.07, -31.69) * mm, "end": v(-147.83, -31.41) * mm});
            skLineSegment(sketch, "E11.69.0", {"start": v(-147.71, -37.51) * mm, "end": v(-146.48, -37.2) * mm});
            skArc(sketch, "E11.69.1", {"start": v(-147.71, -37.51) * mm, "mid": v(-148.36, -37.43) * mm, "end": v(-149.01, -37.33) * mm});
            skArc(sketch, "E11.69.2", {"start": v(-149.08, -37.27) * mm, "mid": v(-149.06, -37.31) * mm, "end": v(-149.01, -37.33) * mm});
            skLineSegment(sketch, "E11.69.3", {"start": v(-149.08, -37.27) * mm, "end": v(-149.19, -36.85) * mm});
            skLineSegment(sketch, "E11.69.4", {"start": v(-149.3, -36.42) * mm, "end": v(-149.19, -36.85) * mm});
            skArc(sketch, "E11.69.5", {"start": v(-149.26, -36.35) * mm, "mid": v(-149.29, -36.38) * mm, "end": v(-149.3, -36.42) * mm});
            skArc(sketch, "E11.69.6", {"start": v(-148.19, -35.58) * mm, "mid": v(-148.73, -35.96) * mm, "end": v(-149.26, -36.35) * mm});
            skLineSegment(sketch, "E11.69.7", {"start": v(-148.19, -35.58) * mm, "end": v(-146.96, -35.27) * mm});
            skLineSegment(sketch, "E11.70.0", {"start": v(-146.68, -41.37) * mm, "end": v(-145.45, -41.03) * mm});
            skArc(sketch, "E11.70.1", {"start": v(-146.68, -41.37) * mm, "mid": v(-147.33, -41.3) * mm, "end": v(-147.98, -41.22) * mm});
            skArc(sketch, "E11.70.2", {"start": v(-148.06, -41.16) * mm, "mid": v(-148.03, -41.2) * mm, "end": v(-147.98, -41.22) * mm});
            skLineSegment(sketch, "E11.70.3", {"start": v(-148.06, -41.16) * mm, "end": v(-148.17, -40.74) * mm});
            skLineSegment(sketch, "E11.70.4", {"start": v(-148.29, -40.32) * mm, "end": v(-148.17, -40.74) * mm});
            skArc(sketch, "E11.70.5", {"start": v(-148.26, -40.24) * mm, "mid": v(-148.29, -40.28) * mm, "end": v(-148.29, -40.32) * mm});
            skArc(sketch, "E11.70.6", {"start": v(-147.2, -39.44) * mm, "mid": v(-147.74, -39.84) * mm, "end": v(-148.26, -40.24) * mm});
            skLineSegment(sketch, "E11.70.7", {"start": v(-147.2, -39.44) * mm, "end": v(-145.98, -39.1) * mm});
            skLineSegment(sketch, "E11.71.0", {"start": v(-145.55, -45.2) * mm, "end": v(-144.33, -44.82) * mm});
            skArc(sketch, "E11.71.1", {"start": v(-145.55, -45.2) * mm, "mid": v(-146.2, -45.14) * mm, "end": v(-146.85, -45.08) * mm});
            skArc(sketch, "E11.71.2", {"start": v(-146.93, -45.02) * mm, "mid": v(-146.9, -45.06) * mm, "end": v(-146.85, -45.08) * mm});
            skLineSegment(sketch, "E11.71.3", {"start": v(-146.93, -45.02) * mm, "end": v(-147.05, -44.6) * mm});
            skLineSegment(sketch, "E11.71.4", {"start": v(-147.18, -44.19) * mm, "end": v(-147.05, -44.6) * mm});
            skArc(sketch, "E11.71.5", {"start": v(-147.16, -44.1) * mm, "mid": v(-147.18, -44.14) * mm, "end": v(-147.18, -44.19) * mm});
            skArc(sketch, "E11.71.6", {"start": v(-146.12, -43.28) * mm, "mid": v(-146.64, -43.7) * mm, "end": v(-147.16, -44.1) * mm});
            skLineSegment(sketch, "E11.71.7", {"start": v(-146.12, -43.28) * mm, "end": v(-144.9, -42.92) * mm});
            skLineSegment(sketch, "E11.72.0", {"start": v(-144.31, -48.99) * mm, "end": v(-143.1, -48.59) * mm});
            skArc(sketch, "E11.72.1", {"start": v(-144.31, -48.99) * mm, "mid": v(-144.97, -48.95) * mm, "end": v(-145.62, -48.91) * mm});
            skArc(sketch, "E11.72.2", {"start": v(-145.7, -48.85) * mm, "mid": v(-145.67, -48.9) * mm, "end": v(-145.62, -48.91) * mm});
            skLineSegment(sketch, "E11.72.3", {"start": v(-145.7, -48.85) * mm, "end": v(-145.84, -48.44) * mm});
            skLineSegment(sketch, "E11.72.4", {"start": v(-145.97, -48.02) * mm, "end": v(-145.84, -48.44) * mm});
            skArc(sketch, "E11.72.5", {"start": v(-145.95, -47.95) * mm, "mid": v(-145.97, -47.98) * mm, "end": v(-145.97, -48.02) * mm});
            skArc(sketch, "E11.72.6", {"start": v(-144.94, -47.1) * mm, "mid": v(-145.45, -47.52) * mm, "end": v(-145.95, -47.95) * mm});
            skLineSegment(sketch, "E11.72.7", {"start": v(-144.94, -47.1) * mm, "end": v(-143.74, -46.7) * mm});
            skLineSegment(sketch, "E11.73.0", {"start": v(-142.98, -52.75) * mm, "end": v(-141.79, -52.32) * mm});
            skArc(sketch, "E11.73.1", {"start": v(-142.98, -52.75) * mm, "mid": v(-143.64, -52.73) * mm, "end": v(-144.3, -52.7) * mm});
            skArc(sketch, "E11.73.2", {"start": v(-144.37, -52.65) * mm, "mid": v(-144.34, -52.69) * mm, "end": v(-144.3, -52.7) * mm});
            skLineSegment(sketch, "E11.73.3", {"start": v(-144.37, -52.65) * mm, "end": v(-144.52, -52.24) * mm});
            skLineSegment(sketch, "E11.73.4", {"start": v(-144.67, -51.83) * mm, "end": v(-144.52, -52.24) * mm});
            skArc(sketch, "E11.73.5", {"start": v(-144.65, -51.75) * mm, "mid": v(-144.67, -51.79) * mm, "end": v(-144.67, -51.83) * mm});
            skArc(sketch, "E11.73.6", {"start": v(-143.66, -50.87) * mm, "mid": v(-144.16, -51.3) * mm, "end": v(-144.65, -51.75) * mm});
            skLineSegment(sketch, "E11.73.7", {"start": v(-143.66, -50.87) * mm, "end": v(-142.46, -50.44) * mm});
            skLineSegment(sketch, "E11.74.0", {"start": v(-141.55, -56.47) * mm, "end": v(-140.37, -56.01) * mm});
            skArc(sketch, "E11.74.1", {"start": v(-141.55, -56.47) * mm, "mid": v(-142.2, -56.47) * mm, "end": v(-142.86, -56.46) * mm});
            skArc(sketch, "E11.74.2", {"start": v(-142.94, -56.4) * mm, "mid": v(-142.91, -56.45) * mm, "end": v(-142.86, -56.46) * mm});
            skLineSegment(sketch, "E11.74.3", {"start": v(-142.94, -56.4) * mm, "end": v(-143.1, -56) * mm});
            skLineSegment(sketch, "E11.74.4", {"start": v(-143.26, -55.6) * mm, "end": v(-143.1, -56) * mm});
            skArc(sketch, "E11.74.5", {"start": v(-143.24, -55.52) * mm, "mid": v(-143.26, -55.56) * mm, "end": v(-143.26, -55.6) * mm});
            skArc(sketch, "E11.74.6", {"start": v(-142.28, -54.62) * mm, "mid": v(-142.76, -55.06) * mm, "end": v(-143.24, -55.52) * mm});
            skLineSegment(sketch, "E11.74.7", {"start": v(-142.28, -54.62) * mm, "end": v(-141.1, -54.15) * mm});
            skLineSegment(sketch, "E11.75.0", {"start": v(-140.02, -60.16) * mm, "end": v(-138.85, -59.67) * mm});
            skArc(sketch, "E11.75.1", {"start": v(-140.02, -60.16) * mm, "mid": v(-140.68, -60.18) * mm, "end": v(-141.34, -60.18) * mm});
            skArc(sketch, "E11.75.2", {"start": v(-141.42, -60.13) * mm, "mid": v(-141.38, -60.17) * mm, "end": v(-141.34, -60.18) * mm});
            skLineSegment(sketch, "E11.75.3", {"start": v(-141.42, -60.13) * mm, "end": v(-141.59, -59.74) * mm});
            skLineSegment(sketch, "E11.75.4", {"start": v(-141.76, -59.33) * mm, "end": v(-141.59, -59.74) * mm});
            skArc(sketch, "E11.75.5", {"start": v(-141.74, -59.25) * mm, "mid": v(-141.76, -59.29) * mm, "end": v(-141.76, -59.33) * mm});
            skArc(sketch, "E11.75.6", {"start": v(-140.8, -58.32) * mm, "mid": v(-141.27, -58.78) * mm, "end": v(-141.74, -59.25) * mm});
            skLineSegment(sketch, "E11.75.7", {"start": v(-140.8, -58.32) * mm, "end": v(-139.63, -57.83) * mm});
            skLineSegment(sketch, "E11.76.0", {"start": v(-138.4, -63.8) * mm, "end": v(-137.24, -63.28) * mm});
            skArc(sketch, "E11.76.1", {"start": v(-138.4, -63.8) * mm, "mid": v(-139.06, -63.84) * mm, "end": v(-139.71, -63.86) * mm});
            skArc(sketch, "E11.76.2", {"start": v(-139.8, -63.81) * mm, "mid": v(-139.76, -63.85) * mm, "end": v(-139.71, -63.86) * mm});
            skLineSegment(sketch, "E11.76.3", {"start": v(-139.8, -63.81) * mm, "end": v(-139.97, -63.42) * mm});
            skLineSegment(sketch, "E11.76.4", {"start": v(-140.15, -63.02) * mm, "end": v(-139.97, -63.42) * mm});
            skArc(sketch, "E11.76.5", {"start": v(-140.14, -62.94) * mm, "mid": v(-140.16, -62.98) * mm, "end": v(-140.15, -63.02) * mm});
            skArc(sketch, "E11.76.6", {"start": v(-139.22, -61.99) * mm, "mid": v(-139.69, -62.46) * mm, "end": v(-140.14, -62.94) * mm});
            skLineSegment(sketch, "E11.76.7", {"start": v(-139.22, -61.99) * mm, "end": v(-138.07, -61.46) * mm});
            skLineSegment(sketch, "E11.77.0", {"start": v(-136.68, -67.4) * mm, "end": v(-135.54, -66.85) * mm});
            skArc(sketch, "E11.77.1", {"start": v(-136.68, -67.4) * mm, "mid": v(-137.34, -67.46) * mm, "end": v(-138, -67.5) * mm});
            skArc(sketch, "E11.77.2", {"start": v(-138.08, -67.45) * mm, "mid": v(-138.04, -67.49) * mm, "end": v(-138, -67.5) * mm});
            skLineSegment(sketch, "E11.77.3", {"start": v(-138.08, -67.45) * mm, "end": v(-138.27, -67.06) * mm});
            skLineSegment(sketch, "E11.77.4", {"start": v(-138.46, -66.67) * mm, "end": v(-138.27, -67.06) * mm});
            skArc(sketch, "E11.77.5", {"start": v(-138.45, -66.59) * mm, "mid": v(-138.46, -66.62) * mm, "end": v(-138.46, -66.67) * mm});
            skArc(sketch, "E11.77.6", {"start": v(-137.55, -65.6) * mm, "mid": v(-138, -66.1) * mm, "end": v(-138.45, -66.59) * mm});
            skLineSegment(sketch, "E11.77.7", {"start": v(-137.55, -65.6) * mm, "end": v(-136.41, -65.06) * mm});
            skLineSegment(sketch, "E11.78.0", {"start": v(-134.87, -70.96) * mm, "end": v(-133.74, -70.38) * mm});
            skArc(sketch, "E11.78.1", {"start": v(-134.87, -70.96) * mm, "mid": v(-135.52, -71.03) * mm, "end": v(-136.18, -71.09) * mm});
            skArc(sketch, "E11.78.2", {"start": v(-136.26, -71.04) * mm, "mid": v(-136.23, -71.08) * mm, "end": v(-136.18, -71.09) * mm});
            skLineSegment(sketch, "E11.78.3", {"start": v(-136.26, -71.04) * mm, "end": v(-136.46, -70.66) * mm});
            skLineSegment(sketch, "E11.78.4", {"start": v(-136.66, -70.27) * mm, "end": v(-136.46, -70.66) * mm});
            skArc(sketch, "E11.78.5", {"start": v(-136.66, -70.19) * mm, "mid": v(-136.67, -70.23) * mm, "end": v(-136.66, -70.27) * mm});
            skArc(sketch, "E11.78.6", {"start": v(-135.79, -69.19) * mm, "mid": v(-136.23, -69.68) * mm, "end": v(-136.66, -70.19) * mm});
            skLineSegment(sketch, "E11.78.7", {"start": v(-135.79, -69.19) * mm, "end": v(-134.66, -68.6) * mm});
            skLineSegment(sketch, "E11.79.0", {"start": v(-132.97, -74.47) * mm, "end": v(-131.86, -73.85) * mm});
            skArc(sketch, "E11.79.1", {"start": v(-132.97, -74.47) * mm, "mid": v(-133.62, -74.55) * mm, "end": v(-134.27, -74.63) * mm});
            skArc(sketch, "E11.79.2", {"start": v(-134.36, -74.58) * mm, "mid": v(-134.32, -74.62) * mm, "end": v(-134.27, -74.63) * mm});
            skLineSegment(sketch, "E11.79.3", {"start": v(-134.36, -74.58) * mm, "end": v(-134.57, -74.2) * mm});
            skLineSegment(sketch, "E11.79.4", {"start": v(-134.78, -73.82) * mm, "end": v(-134.57, -74.2) * mm});
            skArc(sketch, "E11.79.5", {"start": v(-134.77, -73.74) * mm, "mid": v(-134.79, -73.78) * mm, "end": v(-134.78, -73.82) * mm});
            skArc(sketch, "E11.79.6", {"start": v(-133.93, -72.72) * mm, "mid": v(-134.36, -73.23) * mm, "end": v(-134.77, -73.74) * mm});
            skLineSegment(sketch, "E11.79.7", {"start": v(-133.93, -72.72) * mm, "end": v(-132.82, -72.1) * mm});
            skLineSegment(sketch, "E11.80.0", {"start": v(-130.97, -77.92) * mm, "end": v(-129.88, -77.28) * mm});
            skArc(sketch, "E11.80.1", {"start": v(-130.97, -77.92) * mm, "mid": v(-131.62, -78.03) * mm, "end": v(-132.27, -78.12) * mm});
            skArc(sketch, "E11.80.2", {"start": v(-132.36, -78.08) * mm, "mid": v(-132.32, -78.1) * mm, "end": v(-132.27, -78.12) * mm});
            skLineSegment(sketch, "E11.80.3", {"start": v(-132.36, -78.08) * mm, "end": v(-132.58, -77.7) * mm});
            skLineSegment(sketch, "E11.80.4", {"start": v(-132.8, -77.32) * mm, "end": v(-132.58, -77.7) * mm});
            skArc(sketch, "E11.80.5", {"start": v(-132.8, -77.24) * mm, "mid": v(-132.8, -77.28) * mm, "end": v(-132.8, -77.32) * mm});
            skArc(sketch, "E11.80.6", {"start": v(-131.98, -76.2) * mm, "mid": v(-132.4, -76.72) * mm, "end": v(-132.8, -77.24) * mm});
            skLineSegment(sketch, "E11.80.7", {"start": v(-131.98, -76.2) * mm, "end": v(-130.89, -75.56) * mm});
            skLineSegment(sketch, "E11.81.0", {"start": v(-128.89, -81.32) * mm, "end": v(-127.81, -80.65) * mm});
            skArc(sketch, "E11.81.1", {"start": v(-128.89, -81.32) * mm, "mid": v(-129.53, -81.44) * mm, "end": v(-130.18, -81.55) * mm});
            skArc(sketch, "E11.81.2", {"start": v(-130.27, -81.51) * mm, "mid": v(-130.23, -81.55) * mm, "end": v(-130.18, -81.55) * mm});
            skLineSegment(sketch, "E11.81.3", {"start": v(-130.27, -81.51) * mm, "end": v(-130.5, -81.15) * mm});
            skLineSegment(sketch, "E11.81.4", {"start": v(-130.73, -80.77) * mm, "end": v(-130.5, -81.15) * mm});
            skArc(sketch, "E11.81.5", {"start": v(-130.73, -80.7) * mm, "mid": v(-130.74, -80.73) * mm, "end": v(-130.73, -80.77) * mm});
            skArc(sketch, "E11.81.6", {"start": v(-129.94, -79.63) * mm, "mid": v(-130.34, -80.16) * mm, "end": v(-130.73, -80.7) * mm});
            skLineSegment(sketch, "E11.81.7", {"start": v(-129.94, -79.63) * mm, "end": v(-128.86, -78.96) * mm});
            skLineSegment(sketch, "E11.82.0", {"start": v(-126.72, -84.67) * mm, "end": v(-125.66, -83.97) * mm});
            skArc(sketch, "E11.82.1", {"start": v(-126.72, -84.67) * mm, "mid": v(-127.36, -84.8) * mm, "end": v(-128, -84.93) * mm});
            skArc(sketch, "E11.82.2", {"start": v(-128.1, -84.9) * mm, "mid": v(-128.05, -84.93) * mm, "end": v(-128, -84.93) * mm});
            skLineSegment(sketch, "E11.82.3", {"start": v(-128.1, -84.9) * mm, "end": v(-128.33, -84.54) * mm});
            skLineSegment(sketch, "E11.82.4", {"start": v(-128.57, -84.17) * mm, "end": v(-128.33, -84.54) * mm});
            skArc(sketch, "E11.82.5", {"start": v(-128.57, -84.09) * mm, "mid": v(-128.58, -84.13) * mm, "end": v(-128.57, -84.17) * mm});
            skArc(sketch, "E11.82.6", {"start": v(-127.81, -83) * mm, "mid": v(-128.2, -83.54) * mm, "end": v(-128.57, -84.09) * mm});
            skLineSegment(sketch, "E11.82.7", {"start": v(-127.81, -83) * mm, "end": v(-126.75, -82.3) * mm});
            skLineSegment(sketch, "E11.83.0", {"start": v(-124.46, -87.96) * mm, "end": v(-123.41, -87.23) * mm});
            skArc(sketch, "E11.83.1", {"start": v(-124.46, -87.96) * mm, "mid": v(-125.1, -88.11) * mm, "end": v(-125.73, -88.25) * mm});
            skArc(sketch, "E11.83.2", {"start": v(-125.82, -88.22) * mm, "mid": v(-125.78, -88.25) * mm, "end": v(-125.73, -88.25) * mm});
            skLineSegment(sketch, "E11.83.3", {"start": v(-125.82, -88.22) * mm, "end": v(-126.07, -87.87) * mm});
            skLineSegment(sketch, "E11.83.4", {"start": v(-126.32, -87.5) * mm, "end": v(-126.07, -87.87) * mm});
            skArc(sketch, "E11.83.5", {"start": v(-126.32, -87.43) * mm, "mid": v(-126.34, -87.46) * mm, "end": v(-126.32, -87.5) * mm});
            skArc(sketch, "E11.83.6", {"start": v(-125.6, -86.32) * mm, "mid": v(-125.97, -86.87) * mm, "end": v(-126.32, -87.43) * mm});
            skLineSegment(sketch, "E11.83.7", {"start": v(-125.6, -86.32) * mm, "end": v(-124.55, -85.6) * mm});
            skLineSegment(sketch, "E11.84.0", {"start": v(-122.11, -91.18) * mm, "end": v(-121.09, -90.43) * mm});
            skArc(sketch, "E11.84.1", {"start": v(-122.11, -91.18) * mm, "mid": v(-122.74, -91.36) * mm, "end": v(-123.38, -91.52) * mm});
            skArc(sketch, "E11.84.2", {"start": v(-123.47, -91.48) * mm, "mid": v(-123.43, -91.51) * mm, "end": v(-123.38, -91.52) * mm});
            skLineSegment(sketch, "E11.84.3", {"start": v(-123.47, -91.48) * mm, "end": v(-123.73, -91.14) * mm});
            skLineSegment(sketch, "E11.84.4", {"start": v(-123.99, -90.78) * mm, "end": v(-123.73, -91.14) * mm});
            skArc(sketch, "E11.84.5", {"start": v(-124, -90.7) * mm, "mid": v(-124, -90.74) * mm, "end": v(-123.99, -90.78) * mm});
            skArc(sketch, "E11.84.6", {"start": v(-123.3, -89.58) * mm, "mid": v(-123.65, -90.14) * mm, "end": v(-124, -90.7) * mm});
            skLineSegment(sketch, "E11.84.7", {"start": v(-123.3, -89.58) * mm, "end": v(-122.27, -88.83) * mm});
            skLineSegment(sketch, "E11.85.0", {"start": v(-119.68, -94.35) * mm, "end": v(-118.68, -93.57) * mm});
            skArc(sketch, "E11.85.1", {"start": v(-119.68, -94.35) * mm, "mid": v(-120.31, -94.54) * mm, "end": v(-120.94, -94.71) * mm});
            skArc(sketch, "E11.85.2", {"start": v(-121.04, -94.68) * mm, "mid": v(-121, -94.71) * mm, "end": v(-120.94, -94.71) * mm});
            skLineSegment(sketch, "E11.85.3", {"start": v(-121.04, -94.68) * mm, "end": v(-121.3, -94.34) * mm});
            skLineSegment(sketch, "E11.85.4", {"start": v(-121.57, -94) * mm, "end": v(-121.3, -94.34) * mm});
            skArc(sketch, "E11.85.5", {"start": v(-121.58, -93.92) * mm, "mid": v(-121.58, -93.96) * mm, "end": v(-121.57, -94) * mm});
            skArc(sketch, "E11.85.6", {"start": v(-120.9, -92.78) * mm, "mid": v(-121.25, -93.34) * mm, "end": v(-121.58, -93.92) * mm});
            skLineSegment(sketch, "E11.85.7", {"start": v(-120.9, -92.78) * mm, "end": v(-119.9, -92) * mm});
            skLineSegment(sketch, "E11.86.0", {"start": v(-117.17, -97.45) * mm, "end": v(-116.19, -96.64) * mm});
            skArc(sketch, "E11.86.1", {"start": v(-117.17, -97.45) * mm, "mid": v(-117.8, -97.65) * mm, "end": v(-118.42, -97.85) * mm});
            skArc(sketch, "E11.86.2", {"start": v(-118.52, -97.82) * mm, "mid": v(-118.47, -97.85) * mm, "end": v(-118.42, -97.85) * mm});
            skLineSegment(sketch, "E11.86.3", {"start": v(-118.52, -97.82) * mm, "end": v(-118.79, -97.49) * mm});
            skLineSegment(sketch, "E11.86.4", {"start": v(-119.07, -97.15) * mm, "end": v(-118.79, -97.49) * mm});
            skArc(sketch, "E11.86.5", {"start": v(-119.08, -97.07) * mm, "mid": v(-119.08, -97.1) * mm, "end": v(-119.07, -97.15) * mm});
            skArc(sketch, "E11.86.6", {"start": v(-118.44, -95.9) * mm, "mid": v(-118.76, -96.48) * mm, "end": v(-119.08, -97.07) * mm});
            skLineSegment(sketch, "E11.86.7", {"start": v(-118.44, -95.9) * mm, "end": v(-117.46, -95.1) * mm});
            skLineSegment(sketch, "E11.87.0", {"start": v(-114.58, -100.48) * mm, "end": v(-113.62, -99.65) * mm});
            skArc(sketch, "E11.87.1", {"start": v(-114.58, -100.48) * mm, "mid": v(-115.2, -100.7) * mm, "end": v(-115.82, -100.91) * mm});
            skArc(sketch, "E11.87.2", {"start": v(-115.91, -100.89) * mm, "mid": v(-115.87, -100.92) * mm, "end": v(-115.82, -100.91) * mm});
            skLineSegment(sketch, "E11.87.3", {"start": v(-115.91, -100.89) * mm, "end": v(-116.2, -100.56) * mm});
            skLineSegment(sketch, "E11.87.4", {"start": v(-116.48, -100.23) * mm, "end": v(-116.2, -100.56) * mm});
            skArc(sketch, "E11.87.5", {"start": v(-116.5, -100.15) * mm, "mid": v(-116.5, -100.2) * mm, "end": v(-116.48, -100.23) * mm});
            skArc(sketch, "E11.87.6", {"start": v(-115.89, -98.98) * mm, "mid": v(-116.2, -99.56) * mm, "end": v(-116.5, -100.15) * mm});
            skLineSegment(sketch, "E11.87.7", {"start": v(-115.89, -98.98) * mm, "end": v(-114.93, -98.14) * mm});
            skLineSegment(sketch, "E11.88.0", {"start": v(-111.91, -103.45) * mm, "end": v(-110.97, -102.6) * mm});
            skArc(sketch, "E11.88.1", {"start": v(-111.91, -103.45) * mm, "mid": v(-112.52, -103.69) * mm, "end": v(-113.14, -103.91) * mm});
            skArc(sketch, "E11.88.2", {"start": v(-113.23, -103.89) * mm, "mid": v(-113.19, -103.91) * mm, "end": v(-113.14, -103.91) * mm});
            skLineSegment(sketch, "E11.88.3", {"start": v(-113.23, -103.89) * mm, "end": v(-113.52, -103.57) * mm});
            skLineSegment(sketch, "E11.88.4", {"start": v(-113.82, -103.24) * mm, "end": v(-113.52, -103.57) * mm});
            skArc(sketch, "E11.88.5", {"start": v(-113.83, -103.17) * mm, "mid": v(-113.84, -103.2) * mm, "end": v(-113.82, -103.24) * mm});
            skArc(sketch, "E11.88.6", {"start": v(-113.26, -101.98) * mm, "mid": v(-113.55, -102.57) * mm, "end": v(-113.83, -103.17) * mm});
            skLineSegment(sketch, "E11.88.7", {"start": v(-113.26, -101.98) * mm, "end": v(-112.32, -101.12) * mm});
            skLineSegment(sketch, "E11.89.0", {"start": v(-109.16, -106.34) * mm, "end": v(-108.25, -105.46) * mm});
            skArc(sketch, "E11.89.1", {"start": v(-109.16, -106.34) * mm, "mid": v(-109.77, -106.6) * mm, "end": v(-110.38, -106.84) * mm});
            skArc(sketch, "E11.89.2", {"start": v(-110.48, -106.82) * mm, "mid": v(-110.43, -106.84) * mm, "end": v(-110.38, -106.84) * mm});
            skLineSegment(sketch, "E11.89.3", {"start": v(-110.48, -106.82) * mm, "end": v(-110.77, -106.5) * mm});
            skLineSegment(sketch, "E11.89.4", {"start": v(-111.08, -106.19) * mm, "end": v(-110.77, -106.5) * mm});
            skArc(sketch, "E11.89.5", {"start": v(-111.1, -106.11) * mm, "mid": v(-111.1, -106.15) * mm, "end": v(-111.08, -106.19) * mm});
            skArc(sketch, "E11.89.6", {"start": v(-110.55, -104.9) * mm, "mid": v(-110.83, -105.5) * mm, "end": v(-111.1, -106.11) * mm});
            skLineSegment(sketch, "E11.89.7", {"start": v(-110.55, -104.9) * mm, "end": v(-109.63, -104.02) * mm});
            skLineSegment(sketch, "E11.90.0", {"start": v(-106.34, -109.16) * mm, "end": v(-105.45, -108.26) * mm});
            skArc(sketch, "E11.90.1", {"start": v(-106.34, -109.16) * mm, "mid": v(-106.94, -109.43) * mm, "end": v(-107.54, -109.7) * mm});
            skArc(sketch, "E11.90.2", {"start": v(-107.64, -109.67) * mm, "mid": v(-107.6, -109.7) * mm, "end": v(-107.54, -109.7) * mm});
            skLineSegment(sketch, "E11.90.3", {"start": v(-107.64, -109.67) * mm, "end": v(-107.95, -109.37) * mm});
            skLineSegment(sketch, "E11.90.4", {"start": v(-108.26, -109.06) * mm, "end": v(-107.95, -109.37) * mm});
            skArc(sketch, "E11.90.5", {"start": v(-108.28, -108.98) * mm, "mid": v(-108.28, -109.02) * mm, "end": v(-108.26, -109.06) * mm});
            skArc(sketch, "E11.90.6", {"start": v(-107.76, -107.76) * mm, "mid": v(-108.03, -108.37) * mm, "end": v(-108.28, -108.98) * mm});
            skLineSegment(sketch, "E11.90.7", {"start": v(-107.76, -107.76) * mm, "end": v(-106.87, -106.86) * mm});
            skLineSegment(sketch, "E11.91.0", {"start": v(-103.45, -111.91) * mm, "end": v(-102.58, -110.98) * mm});
            skArc(sketch, "E11.91.1", {"start": v(-103.45, -111.91) * mm, "mid": v(-104.04, -112.2) * mm, "end": v(-104.64, -112.47) * mm});
            skArc(sketch, "E11.91.2", {"start": v(-104.73, -112.45) * mm, "mid": v(-104.69, -112.47) * mm, "end": v(-104.64, -112.47) * mm});
            skLineSegment(sketch, "E11.91.3", {"start": v(-104.73, -112.45) * mm, "end": v(-105.05, -112.16) * mm});
            skLineSegment(sketch, "E11.91.4", {"start": v(-105.37, -111.86) * mm, "end": v(-105.05, -112.16) * mm});
            skArc(sketch, "E11.91.5", {"start": v(-105.39, -111.78) * mm, "mid": v(-105.39, -111.82) * mm, "end": v(-105.37, -111.86) * mm});
            skArc(sketch, "E11.91.6", {"start": v(-104.9, -110.55) * mm, "mid": v(-105.15, -111.16) * mm, "end": v(-105.39, -111.78) * mm});
            skLineSegment(sketch, "E11.91.7", {"start": v(-104.9, -110.55) * mm, "end": v(-104.04, -109.62) * mm});
            skLineSegment(sketch, "E11.92.0", {"start": v(-100.48, -114.58) * mm, "end": v(-99.64, -113.63) * mm});
            skArc(sketch, "E11.92.1", {"start": v(-100.48, -114.58) * mm, "mid": v(-101.07, -114.88) * mm, "end": v(-101.66, -115.17) * mm});
            skArc(sketch, "E11.92.2", {"start": v(-101.75, -115.15) * mm, "mid": v(-101.7, -115.18) * mm, "end": v(-101.66, -115.17) * mm});
            skLineSegment(sketch, "E11.92.3", {"start": v(-101.75, -115.15) * mm, "end": v(-102.08, -114.87) * mm});
            skLineSegment(sketch, "E11.92.4", {"start": v(-102.4, -114.58) * mm, "end": v(-102.08, -114.87) * mm});
            skArc(sketch, "E11.92.5", {"start": v(-102.43, -114.5) * mm, "mid": v(-102.43, -114.54) * mm, "end": v(-102.4, -114.58) * mm});
            skArc(sketch, "E11.92.6", {"start": v(-101.98, -113.26) * mm, "mid": v(-102.2, -113.88) * mm, "end": v(-102.43, -114.5) * mm});
            skLineSegment(sketch, "E11.92.7", {"start": v(-101.98, -113.26) * mm, "end": v(-101.13, -112.3) * mm});
            skLineSegment(sketch, "E11.93.0", {"start": v(-97.45, -117.17) * mm, "end": v(-96.63, -116.2) * mm});
            skArc(sketch, "E11.93.1", {"start": v(-97.45, -117.17) * mm, "mid": v(-98.03, -117.49) * mm, "end": v(-98.6, -117.79) * mm});
            skArc(sketch, "E11.93.2", {"start": v(-98.7, -117.78) * mm, "mid": v(-98.66, -117.8) * mm, "end": v(-98.6, -117.79) * mm});
            skLineSegment(sketch, "E11.93.3", {"start": v(-98.7, -117.78) * mm, "end": v(-99.03, -117.5) * mm});
            skLineSegment(sketch, "E11.93.4", {"start": v(-99.37, -117.22) * mm, "end": v(-99.03, -117.5) * mm});
            skArc(sketch, "E11.93.5", {"start": v(-99.4, -117.14) * mm, "mid": v(-99.4, -117.18) * mm, "end": v(-99.37, -117.22) * mm});
            skArc(sketch, "E11.93.6", {"start": v(-98.98, -115.89) * mm, "mid": v(-99.19, -116.51) * mm, "end": v(-99.4, -117.14) * mm});
            skLineSegment(sketch, "E11.93.7", {"start": v(-98.98, -115.89) * mm, "end": v(-98.16, -114.91) * mm});
            skLineSegment(sketch, "E11.94.0", {"start": v(-94.35, -119.68) * mm, "end": v(-93.56, -118.7) * mm});
            skArc(sketch, "E11.94.1", {"start": v(-94.35, -119.68) * mm, "mid": v(-94.92, -120.01) * mm, "end": v(-95.5, -120.33) * mm});
            skArc(sketch, "E11.94.2", {"start": v(-95.59, -120.32) * mm, "mid": v(-95.54, -120.34) * mm, "end": v(-95.5, -120.33) * mm});
            skLineSegment(sketch, "E11.94.3", {"start": v(-95.59, -120.32) * mm, "end": v(-95.92, -120.06) * mm});
            skLineSegment(sketch, "E11.94.4", {"start": v(-96.27, -119.78) * mm, "end": v(-95.92, -120.06) * mm});
            skArc(sketch, "E11.94.5", {"start": v(-96.3, -119.7) * mm, "mid": v(-96.3, -119.74) * mm, "end": v(-96.27, -119.78) * mm});
            skArc(sketch, "E11.94.6", {"start": v(-95.9, -118.44) * mm, "mid": v(-96.1, -119.07) * mm, "end": v(-96.3, -119.7) * mm});
            skLineSegment(sketch, "E11.94.7", {"start": v(-95.9, -118.44) * mm, "end": v(-95.12, -117.44) * mm});
            skLineSegment(sketch, "E11.95.0", {"start": v(-91.18, -122.11) * mm, "end": v(-90.42, -121.1) * mm});
            skArc(sketch, "E11.95.1", {"start": v(-91.18, -122.11) * mm, "mid": v(-91.74, -122.45) * mm, "end": v(-92.3, -122.79) * mm});
            skArc(sketch, "E11.95.2", {"start": v(-92.4, -122.78) * mm, "mid": v(-92.36, -122.8) * mm, "end": v(-92.3, -122.79) * mm});
            skLineSegment(sketch, "E11.95.3", {"start": v(-92.4, -122.78) * mm, "end": v(-92.75, -122.52) * mm});
            skLineSegment(sketch, "E11.95.4", {"start": v(-93.1, -122.26) * mm, "end": v(-92.75, -122.52) * mm});
            skArc(sketch, "E11.95.5", {"start": v(-93.13, -122.18) * mm, "mid": v(-93.12, -122.22) * mm, "end": v(-93.1, -122.26) * mm});
            skArc(sketch, "E11.95.6", {"start": v(-92.78, -120.9) * mm, "mid": v(-92.96, -121.54) * mm, "end": v(-93.13, -122.18) * mm});
            skLineSegment(sketch, "E11.95.7", {"start": v(-92.78, -120.9) * mm, "end": v(-92, -119.9) * mm});
            skLineSegment(sketch, "E11.96.0", {"start": v(-87.96, -124.46) * mm, "end": v(-87.22, -123.42) * mm});
            skArc(sketch, "E11.96.1", {"start": v(-87.96, -124.46) * mm, "mid": v(-88.5, -124.81) * mm, "end": v(-89.06, -125.16) * mm});
            skArc(sketch, "E11.96.2", {"start": v(-89.16, -125.16) * mm, "mid": v(-89.11, -125.18) * mm, "end": v(-89.06, -125.16) * mm});
            skLineSegment(sketch, "E11.96.3", {"start": v(-89.16, -125.16) * mm, "end": v(-89.5, -124.91) * mm});
            skLineSegment(sketch, "E11.96.4", {"start": v(-89.87, -124.65) * mm, "end": v(-89.5, -124.91) * mm});
            skArc(sketch, "E11.96.5", {"start": v(-89.9, -124.58) * mm, "mid": v(-89.9, -124.62) * mm, "end": v(-89.87, -124.65) * mm});
            skArc(sketch, "E11.96.6", {"start": v(-89.58, -123.3) * mm, "mid": v(-89.74, -123.94) * mm, "end": v(-89.9, -124.58) * mm});
            skLineSegment(sketch, "E11.96.7", {"start": v(-89.58, -123.3) * mm, "end": v(-88.84, -122.26) * mm});
            skLineSegment(sketch, "E11.97.0", {"start": v(-84.67, -126.72) * mm, "end": v(-83.96, -125.66) * mm});
            skArc(sketch, "E11.97.1", {"start": v(-84.67, -126.72) * mm, "mid": v(-85.2, -127.09) * mm, "end": v(-85.75, -127.45) * mm});
            skArc(sketch, "E11.97.2", {"start": v(-85.85, -127.45) * mm, "mid": v(-85.8, -127.47) * mm, "end": v(-85.75, -127.45) * mm});
            skLineSegment(sketch, "E11.97.3", {"start": v(-85.85, -127.45) * mm, "end": v(-86.2, -127.21) * mm});
            skLineSegment(sketch, "E11.97.4", {"start": v(-86.57, -126.96) * mm, "end": v(-86.2, -127.21) * mm});
            skArc(sketch, "E11.97.5", {"start": v(-86.6, -126.89) * mm, "mid": v(-86.6, -126.93) * mm, "end": v(-86.57, -126.96) * mm});
            skArc(sketch, "E11.97.6", {"start": v(-86.32, -125.6) * mm, "mid": v(-86.47, -126.24) * mm, "end": v(-86.6, -126.89) * mm});
            skLineSegment(sketch, "E11.97.7", {"start": v(-86.32, -125.6) * mm, "end": v(-85.6, -124.55) * mm});
            skLineSegment(sketch, "E11.98.0", {"start": v(-81.32, -128.89) * mm, "end": v(-80.64, -127.82) * mm});
            skArc(sketch, "E11.98.1", {"start": v(-81.32, -128.89) * mm, "mid": v(-81.85, -129.28) * mm, "end": v(-82.39, -129.65) * mm});
            skArc(sketch, "E11.98.2", {"start": v(-82.49, -129.65) * mm, "mid": v(-82.44, -129.67) * mm, "end": v(-82.39, -129.65) * mm});
            skLineSegment(sketch, "E11.98.3", {"start": v(-82.49, -129.65) * mm, "end": v(-82.85, -129.42) * mm});
            skLineSegment(sketch, "E11.98.4", {"start": v(-83.22, -129.19) * mm, "end": v(-82.85, -129.42) * mm});
            skArc(sketch, "E11.98.5", {"start": v(-83.25, -129.11) * mm, "mid": v(-83.25, -129.15) * mm, "end": v(-83.22, -129.19) * mm});
            skArc(sketch, "E11.98.6", {"start": v(-83, -127.81) * mm, "mid": v(-83.13, -128.46) * mm, "end": v(-83.25, -129.11) * mm});
            skLineSegment(sketch, "E11.98.7", {"start": v(-83, -127.81) * mm, "end": v(-82.32, -126.74) * mm});
            skLineSegment(sketch, "E11.99.0", {"start": v(-77.92, -130.97) * mm, "end": v(-77.26, -129.89) * mm});
            skArc(sketch, "E11.99.1", {"start": v(-77.92, -130.97) * mm, "mid": v(-78.44, -131.37) * mm, "end": v(-78.97, -131.77) * mm});
            skArc(sketch, "E11.99.2", {"start": v(-79.06, -131.77) * mm, "mid": v(-79.02, -131.78) * mm, "end": v(-78.97, -131.77) * mm});
            skLineSegment(sketch, "E11.99.3", {"start": v(-79.06, -131.77) * mm, "end": v(-79.43, -131.55) * mm});
            skLineSegment(sketch, "E11.99.4", {"start": v(-79.81, -131.32) * mm, "end": v(-79.43, -131.55) * mm});
            skArc(sketch, "E11.99.5", {"start": v(-79.84, -131.25) * mm, "mid": v(-79.84, -131.29) * mm, "end": v(-79.81, -131.32) * mm});
            skArc(sketch, "E11.99.6", {"start": v(-79.63, -129.94) * mm, "mid": v(-79.74, -130.6) * mm, "end": v(-79.84, -131.25) * mm});
            skLineSegment(sketch, "E11.99.7", {"start": v(-79.63, -129.94) * mm, "end": v(-78.97, -128.86) * mm});
            skLineSegment(sketch, "E11.100.0", {"start": v(-74.47, -132.97) * mm, "end": v(-73.84, -131.86) * mm});
            skArc(sketch, "E11.100.1", {"start": v(-74.47, -132.97) * mm, "mid": v(-74.97, -133.38) * mm, "end": v(-75.5, -133.79) * mm});
            skArc(sketch, "E11.100.2", {"start": v(-75.59, -133.8) * mm, "mid": v(-75.54, -133.8) * mm, "end": v(-75.5, -133.79) * mm});
            skLineSegment(sketch, "E11.100.3", {"start": v(-75.59, -133.8) * mm, "end": v(-75.96, -133.58) * mm});
            skLineSegment(sketch, "E11.100.4", {"start": v(-76.35, -133.36) * mm, "end": v(-75.96, -133.58) * mm});
            skArc(sketch, "E11.100.5", {"start": v(-76.38, -133.3) * mm, "mid": v(-76.37, -133.33) * mm, "end": v(-76.35, -133.36) * mm});
            skArc(sketch, "E11.100.6", {"start": v(-76.2, -131.98) * mm, "mid": v(-76.3, -132.64) * mm, "end": v(-76.38, -133.3) * mm});
            skLineSegment(sketch, "E11.100.7", {"start": v(-76.2, -131.98) * mm, "end": v(-75.57, -130.88) * mm});
            skLineSegment(sketch, "E11.101.0", {"start": v(-70.96, -134.87) * mm, "end": v(-70.36, -133.75) * mm});
            skArc(sketch, "E11.101.1", {"start": v(-70.96, -134.87) * mm, "mid": v(-71.46, -135.3) * mm, "end": v(-71.96, -135.72) * mm});
            skArc(sketch, "E11.101.2", {"start": v(-72.06, -135.73) * mm, "mid": v(-72, -135.74) * mm, "end": v(-71.96, -135.72) * mm});
            skLineSegment(sketch, "E11.101.3", {"start": v(-72.06, -135.73) * mm, "end": v(-72.44, -135.53) * mm});
            skLineSegment(sketch, "E11.101.4", {"start": v(-72.83, -135.32) * mm, "end": v(-72.44, -135.53) * mm});
            skArc(sketch, "E11.101.5", {"start": v(-72.87, -135.25) * mm, "mid": v(-72.86, -135.29) * mm, "end": v(-72.83, -135.32) * mm});
            skArc(sketch, "E11.101.6", {"start": v(-72.72, -133.93) * mm, "mid": v(-72.8, -134.59) * mm, "end": v(-72.87, -135.25) * mm});
            skLineSegment(sketch, "E11.101.7", {"start": v(-72.72, -133.93) * mm, "end": v(-72.12, -132.81) * mm});
            skLineSegment(sketch, "E11.102.0", {"start": v(-67.4, -136.68) * mm, "end": v(-66.84, -135.55) * mm});
            skArc(sketch, "E11.102.1", {"start": v(-67.4, -136.68) * mm, "mid": v(-67.9, -137.12) * mm, "end": v(-68.39, -137.55) * mm});
            skArc(sketch, "E11.102.2", {"start": v(-68.48, -137.57) * mm, "mid": v(-68.43, -137.58) * mm, "end": v(-68.39, -137.55) * mm});
            skLineSegment(sketch, "E11.102.3", {"start": v(-68.48, -137.57) * mm, "end": v(-68.87, -137.38) * mm});
            skLineSegment(sketch, "E11.102.4", {"start": v(-69.26, -137.18) * mm, "end": v(-68.87, -137.38) * mm});
            skArc(sketch, "E11.102.5", {"start": v(-69.3, -137.1) * mm, "mid": v(-69.3, -137.15) * mm, "end": v(-69.26, -137.18) * mm});
            skArc(sketch, "E11.102.6", {"start": v(-69.19, -135.79) * mm, "mid": v(-69.25, -136.45) * mm, "end": v(-69.3, -137.1) * mm});
            skLineSegment(sketch, "E11.102.7", {"start": v(-69.19, -135.79) * mm, "end": v(-68.62, -134.65) * mm});
            skLineSegment(sketch, "E11.103.0", {"start": v(-63.8, -138.4) * mm, "end": v(-63.26, -137.25) * mm});
            skArc(sketch, "E11.103.1", {"start": v(-63.8, -138.4) * mm, "mid": v(-64.28, -138.85) * mm, "end": v(-64.76, -139.3) * mm});
            skArc(sketch, "E11.103.2", {"start": v(-64.86, -139.31) * mm, "mid": v(-64.8, -139.32) * mm, "end": v(-64.76, -139.3) * mm});
            skLineSegment(sketch, "E11.103.3", {"start": v(-64.86, -139.31) * mm, "end": v(-65.25, -139.13) * mm});
            skLineSegment(sketch, "E11.103.4", {"start": v(-65.65, -138.94) * mm, "end": v(-65.25, -139.13) * mm});
            skArc(sketch, "E11.103.5", {"start": v(-65.69, -138.87) * mm, "mid": v(-65.68, -138.91) * mm, "end": v(-65.65, -138.94) * mm});
            skArc(sketch, "E11.103.6", {"start": v(-65.6, -137.55) * mm, "mid": v(-65.65, -138.21) * mm, "end": v(-65.69, -138.87) * mm});
            skLineSegment(sketch, "E11.103.7", {"start": v(-65.6, -137.55) * mm, "end": v(-65.07, -136.4) * mm});
            skLineSegment(sketch, "E11.104.0", {"start": v(-60.16, -140.02) * mm, "end": v(-59.65, -138.86) * mm});
            skArc(sketch, "E11.104.1", {"start": v(-60.16, -140.02) * mm, "mid": v(-60.62, -140.49) * mm, "end": v(-61.1, -140.95) * mm});
            skArc(sketch, "E11.104.2", {"start": v(-61.19, -140.96) * mm, "mid": v(-61.14, -140.97) * mm, "end": v(-61.1, -140.95) * mm});
            skLineSegment(sketch, "E11.104.3", {"start": v(-61.19, -140.96) * mm, "end": v(-61.58, -140.8) * mm});
            skLineSegment(sketch, "E11.104.4", {"start": v(-61.99, -140.61) * mm, "end": v(-61.58, -140.8) * mm});
            skArc(sketch, "E11.104.5", {"start": v(-62.03, -140.55) * mm, "mid": v(-62.02, -140.59) * mm, "end": v(-61.99, -140.61) * mm});
            skArc(sketch, "E11.104.6", {"start": v(-61.99, -139.22) * mm, "mid": v(-62.01, -139.89) * mm, "end": v(-62.03, -140.55) * mm});
            skLineSegment(sketch, "E11.104.7", {"start": v(-61.99, -139.22) * mm, "end": v(-61.48, -138.06) * mm});
            skLineSegment(sketch, "E11.105.0", {"start": v(-56.47, -141.55) * mm, "end": v(-56, -140.37) * mm});
            skArc(sketch, "E11.105.1", {"start": v(-56.47, -141.55) * mm, "mid": v(-56.92, -142.03) * mm, "end": v(-57.38, -142.5) * mm});
            skArc(sketch, "E11.105.2", {"start": v(-57.48, -142.52) * mm, "mid": v(-57.43, -142.52) * mm, "end": v(-57.38, -142.5) * mm});
            skLineSegment(sketch, "E11.105.3", {"start": v(-57.48, -142.52) * mm, "end": v(-57.88, -142.36) * mm});
            skLineSegment(sketch, "E11.105.4", {"start": v(-58.29, -142.19) * mm, "end": v(-57.88, -142.36) * mm});
            skArc(sketch, "E11.105.5", {"start": v(-58.33, -142.12) * mm, "mid": v(-58.32, -142.16) * mm, "end": v(-58.29, -142.19) * mm});
            skArc(sketch, "E11.105.6", {"start": v(-58.32, -140.8) * mm, "mid": v(-58.33, -141.46) * mm, "end": v(-58.33, -142.12) * mm});
            skLineSegment(sketch, "E11.105.7", {"start": v(-58.32, -140.8) * mm, "end": v(-57.84, -139.62) * mm});
            skLineSegment(sketch, "E11.106.0", {"start": v(-52.75, -142.98) * mm, "end": v(-52.3, -141.8) * mm});
            skArc(sketch, "E11.106.1", {"start": v(-52.75, -142.98) * mm, "mid": v(-53.19, -143.47) * mm, "end": v(-53.63, -143.95) * mm});
            skArc(sketch, "E11.106.2", {"start": v(-53.73, -143.97) * mm, "mid": v(-53.68, -143.97) * mm, "end": v(-53.63, -143.95) * mm});
            skLineSegment(sketch, "E11.106.3", {"start": v(-53.73, -143.97) * mm, "end": v(-54.13, -143.82) * mm});
            skLineSegment(sketch, "E11.106.4", {"start": v(-54.54, -143.66) * mm, "end": v(-54.13, -143.82) * mm});
            skArc(sketch, "E11.106.5", {"start": v(-54.59, -143.6) * mm, "mid": v(-54.58, -143.64) * mm, "end": v(-54.54, -143.66) * mm});
            skArc(sketch, "E11.106.6", {"start": v(-54.62, -142.28) * mm, "mid": v(-54.6, -142.94) * mm, "end": v(-54.59, -143.6) * mm});
            skLineSegment(sketch, "E11.106.7", {"start": v(-54.62, -142.28) * mm, "end": v(-54.17, -141.09) * mm});
            skLineSegment(sketch, "E11.107.0", {"start": v(-48.99, -144.31) * mm, "end": v(-48.57, -143.11) * mm});
            skArc(sketch, "E11.107.1", {"start": v(-48.99, -144.31) * mm, "mid": v(-49.41, -144.81) * mm, "end": v(-49.85, -145.3) * mm});
            skArc(sketch, "E11.107.2", {"start": v(-49.94, -145.33) * mm, "mid": v(-49.89, -145.33) * mm, "end": v(-49.85, -145.3) * mm});
            skLineSegment(sketch, "E11.107.3", {"start": v(-49.94, -145.33) * mm, "end": v(-50.35, -145.19) * mm});
            skLineSegment(sketch, "E11.107.4", {"start": v(-50.76, -145.04) * mm, "end": v(-50.35, -145.19) * mm});
            skArc(sketch, "E11.107.5", {"start": v(-50.81, -144.98) * mm, "mid": v(-50.8, -145.02) * mm, "end": v(-50.76, -145.04) * mm});
            skArc(sketch, "E11.107.6", {"start": v(-50.87, -143.66) * mm, "mid": v(-50.85, -144.32) * mm, "end": v(-50.81, -144.98) * mm});
            skLineSegment(sketch, "E11.107.7", {"start": v(-50.87, -143.66) * mm, "end": v(-50.46, -142.46) * mm});
            skLineSegment(sketch, "E11.108.0", {"start": v(-45.2, -145.55) * mm, "end": v(-44.8, -144.33) * mm});
            skArc(sketch, "E11.108.1", {"start": v(-45.2, -145.55) * mm, "mid": v(-45.6, -146.06) * mm, "end": v(-46.02, -146.56) * mm});
            skArc(sketch, "E11.108.2", {"start": v(-46.12, -146.59) * mm, "mid": v(-46.07, -146.59) * mm, "end": v(-46.02, -146.56) * mm});
            skLineSegment(sketch, "E11.108.3", {"start": v(-46.12, -146.59) * mm, "end": v(-46.53, -146.46) * mm});
            skLineSegment(sketch, "E11.108.4", {"start": v(-46.95, -146.32) * mm, "end": v(-46.53, -146.46) * mm});
            skArc(sketch, "E11.108.5", {"start": v(-47, -146.26) * mm, "mid": v(-46.98, -146.3) * mm, "end": v(-46.95, -146.32) * mm});
            skArc(sketch, "E11.108.6", {"start": v(-47.1, -144.94) * mm, "mid": v(-47.05, -145.6) * mm, "end": v(-47, -146.26) * mm});
            skLineSegment(sketch, "E11.108.7", {"start": v(-47.1, -144.94) * mm, "end": v(-46.7, -143.73) * mm});
            skLineSegment(sketch, "E11.109.0", {"start": v(-41.37, -146.68) * mm, "end": v(-41.01, -145.46) * mm});
            skArc(sketch, "E11.109.1", {"start": v(-41.37, -146.68) * mm, "mid": v(-41.77, -147.2) * mm, "end": v(-42.17, -147.71) * mm});
            skArc(sketch, "E11.109.2", {"start": v(-42.27, -147.74) * mm, "mid": v(-42.21, -147.74) * mm, "end": v(-42.17, -147.71) * mm});
            skLineSegment(sketch, "E11.109.3", {"start": v(-42.27, -147.74) * mm, "end": v(-42.68, -147.63) * mm});
            skLineSegment(sketch, "E11.109.4", {"start": v(-43.1, -147.5) * mm, "end": v(-42.68, -147.63) * mm});
            skArc(sketch, "E11.109.5", {"start": v(-43.15, -147.44) * mm, "mid": v(-43.14, -147.48) * mm, "end": v(-43.1, -147.5) * mm});
            skArc(sketch, "E11.109.6", {"start": v(-43.28, -146.12) * mm, "mid": v(-43.22, -146.78) * mm, "end": v(-43.15, -147.44) * mm});
            skLineSegment(sketch, "E11.109.7", {"start": v(-43.28, -146.12) * mm, "end": v(-42.93, -144.9) * mm});
            skLineSegment(sketch, "E11.110.0", {"start": v(-37.51, -147.71) * mm, "end": v(-37.2, -146.48) * mm});
            skArc(sketch, "E11.110.1", {"start": v(-37.51, -147.71) * mm, "mid": v(-37.9, -148.24) * mm, "end": v(-38.3, -148.77) * mm});
            skArc(sketch, "E11.110.2", {"start": v(-38.38, -148.8) * mm, "mid": v(-38.33, -148.8) * mm, "end": v(-38.3, -148.77) * mm});
            skLineSegment(sketch, "E11.110.3", {"start": v(-38.38, -148.8) * mm, "end": v(-38.8, -148.7) * mm});
            skLineSegment(sketch, "E11.110.4", {"start": v(-39.23, -148.58) * mm, "end": v(-38.8, -148.7) * mm});
            skArc(sketch, "E11.110.5", {"start": v(-39.28, -148.52) * mm, "mid": v(-39.26, -148.56) * mm, "end": v(-39.23, -148.58) * mm});
            skArc(sketch, "E11.110.6", {"start": v(-39.44, -147.2) * mm, "mid": v(-39.37, -147.86) * mm, "end": v(-39.28, -148.52) * mm});
            skLineSegment(sketch, "E11.110.7", {"start": v(-39.44, -147.2) * mm, "end": v(-39.12, -145.98) * mm});
            skLineSegment(sketch, "E11.111.0", {"start": v(-33.63, -148.64) * mm, "end": v(-33.35, -147.4) * mm});
            skArc(sketch, "E11.111.1", {"start": v(-33.63, -148.64) * mm, "mid": v(-34, -149.18) * mm, "end": v(-34.38, -149.72) * mm});
            skArc(sketch, "E11.111.2", {"start": v(-34.48, -149.75) * mm, "mid": v(-34.42, -149.75) * mm, "end": v(-34.38, -149.72) * mm});
            skLineSegment(sketch, "E11.111.3", {"start": v(-34.48, -149.75) * mm, "end": v(-34.9, -149.66) * mm});
            skLineSegment(sketch, "E11.111.4", {"start": v(-35.32, -149.55) * mm, "end": v(-34.9, -149.66) * mm});
            skArc(sketch, "E11.111.5", {"start": v(-35.38, -149.5) * mm, "mid": v(-35.36, -149.53) * mm, "end": v(-35.32, -149.55) * mm});
            skArc(sketch, "E11.111.6", {"start": v(-35.58, -148.19) * mm, "mid": v(-35.48, -148.84) * mm, "end": v(-35.38, -149.5) * mm});
            skLineSegment(sketch, "E11.111.7", {"start": v(-35.58, -148.19) * mm, "end": v(-35.29, -146.95) * mm});
            skLineSegment(sketch, "E11.112.0", {"start": v(-29.73, -149.47) * mm, "end": v(-29.48, -148.23) * mm});
            skArc(sketch, "E11.112.1", {"start": v(-29.73, -149.47) * mm, "mid": v(-30.09, -150.02) * mm, "end": v(-30.45, -150.57) * mm});
            skArc(sketch, "E11.112.2", {"start": v(-30.54, -150.6) * mm, "mid": v(-30.5, -150.6) * mm, "end": v(-30.45, -150.57) * mm});
            skLineSegment(sketch, "E11.112.3", {"start": v(-30.54, -150.6) * mm, "end": v(-30.97, -150.52) * mm});
            skLineSegment(sketch, "E11.112.4", {"start": v(-31.4, -150.43) * mm, "end": v(-30.97, -150.52) * mm});
            skArc(sketch, "E11.112.5", {"start": v(-31.45, -150.37) * mm, "mid": v(-31.43, -150.4) * mm, "end": v(-31.4, -150.43) * mm});
            skArc(sketch, "E11.112.6", {"start": v(-31.69, -149.07) * mm, "mid": v(-31.58, -149.72) * mm, "end": v(-31.45, -150.37) * mm});
            skLineSegment(sketch, "E11.112.7", {"start": v(-31.69, -149.07) * mm, "end": v(-31.43, -147.83) * mm});
            skLineSegment(sketch, "E11.113.0", {"start": v(-25.8, -150.2) * mm, "end": v(-25.59, -148.95) * mm});
            skArc(sketch, "E11.113.1", {"start": v(-25.8, -150.2) * mm, "mid": v(-26.15, -150.76) * mm, "end": v(-26.5, -151.31) * mm});
            skArc(sketch, "E11.113.2", {"start": v(-26.6, -151.35) * mm, "mid": v(-26.54, -151.35) * mm, "end": v(-26.5, -151.31) * mm});
            skLineSegment(sketch, "E11.113.3", {"start": v(-26.6, -151.35) * mm, "end": v(-27.01, -151.28) * mm});
            skLineSegment(sketch, "E11.113.4", {"start": v(-27.45, -151.2) * mm, "end": v(-27.01, -151.28) * mm});
            skArc(sketch, "E11.113.5", {"start": v(-27.5, -151.14) * mm, "mid": v(-27.49, -151.18) * mm, "end": v(-27.45, -151.2) * mm});
            skArc(sketch, "E11.113.6", {"start": v(-27.77, -149.85) * mm, "mid": v(-27.64, -150.5) * mm, "end": v(-27.5, -151.14) * mm});
            skLineSegment(sketch, "E11.113.7", {"start": v(-27.77, -149.85) * mm, "end": v(-27.55, -148.6) * mm});
            skLineSegment(sketch, "E11.114.0", {"start": v(-21.87, -150.82) * mm, "end": v(-21.68, -149.57) * mm});
            skArc(sketch, "E11.114.1", {"start": v(-21.87, -150.82) * mm, "mid": v(-22.2, -151.4) * mm, "end": v(-22.53, -151.95) * mm});
            skArc(sketch, "E11.114.2", {"start": v(-22.62, -152) * mm, "mid": v(-22.57, -151.99) * mm, "end": v(-22.53, -151.95) * mm});
            skLineSegment(sketch, "E11.114.3", {"start": v(-22.62, -152) * mm, "end": v(-23.05, -151.93) * mm});
            skLineSegment(sketch, "E11.114.4", {"start": v(-23.48, -151.87) * mm, "end": v(-23.05, -151.93) * mm});
            skArc(sketch, "E11.114.5", {"start": v(-23.54, -151.81) * mm, "mid": v(-23.52, -151.85) * mm, "end": v(-23.48, -151.87) * mm});
            skArc(sketch, "E11.114.6", {"start": v(-23.84, -150.52) * mm, "mid": v(-23.7, -151.17) * mm, "end": v(-23.54, -151.81) * mm});
            skLineSegment(sketch, "E11.114.7", {"start": v(-23.84, -150.52) * mm, "end": v(-23.65, -149.27) * mm});
            skLineSegment(sketch, "E11.115.0", {"start": v(-17.91, -151.34) * mm, "end": v(-17.76, -150.08) * mm});
            skArc(sketch, "E11.115.1", {"start": v(-17.91, -151.34) * mm, "mid": v(-18.22, -151.92) * mm, "end": v(-18.55, -152.5) * mm});
            skArc(sketch, "E11.115.2", {"start": v(-18.63, -152.54) * mm, "mid": v(-18.58, -152.53) * mm, "end": v(-18.55, -152.5) * mm});
            skLineSegment(sketch, "E11.115.3", {"start": v(-18.63, -152.54) * mm, "end": v(-19.06, -152.48) * mm});
            skLineSegment(sketch, "E11.115.4", {"start": v(-19.5, -152.43) * mm, "end": v(-19.06, -152.48) * mm});
            skArc(sketch, "E11.115.5", {"start": v(-19.56, -152.38) * mm, "mid": v(-19.54, -152.41) * mm, "end": v(-19.5, -152.43) * mm});
            skArc(sketch, "E11.115.6", {"start": v(-19.9, -151.1) * mm, "mid": v(-19.73, -151.74) * mm, "end": v(-19.56, -152.38) * mm});
            skLineSegment(sketch, "E11.115.7", {"start": v(-19.9, -151.1) * mm, "end": v(-19.73, -149.84) * mm});
            skLineSegment(sketch, "E11.116.0", {"start": v(-13.94, -151.76) * mm, "end": v(-13.82, -150.5) * mm});
            skArc(sketch, "E11.116.1", {"start": v(-13.94, -151.76) * mm, "mid": v(-14.24, -152.35) * mm, "end": v(-14.55, -152.93) * mm});
            skArc(sketch, "E11.116.2", {"start": v(-14.63, -152.97) * mm, "mid": v(-14.58, -152.96) * mm, "end": v(-14.55, -152.93) * mm});
            skLineSegment(sketch, "E11.116.3", {"start": v(-14.63, -152.97) * mm, "end": v(-15.06, -152.93) * mm});
            skLineSegment(sketch, "E11.116.4", {"start": v(-15.5, -152.89) * mm, "end": v(-15.06, -152.93) * mm});
            skArc(sketch, "E11.116.5", {"start": v(-15.56, -152.84) * mm, "mid": v(-15.54, -152.87) * mm, "end": v(-15.5, -152.89) * mm});
            skArc(sketch, "E11.116.6", {"start": v(-15.93, -151.57) * mm, "mid": v(-15.75, -152.2) * mm, "end": v(-15.56, -152.84) * mm});
            skLineSegment(sketch, "E11.116.7", {"start": v(-15.93, -151.57) * mm, "end": v(-15.8, -150.3) * mm});
            skLineSegment(sketch, "E11.117.0", {"start": v(-9.97, -152.07) * mm, "end": v(-9.88, -150.8) * mm});
            skArc(sketch, "E11.117.1", {"start": v(-9.97, -152.07) * mm, "mid": v(-10.25, -152.67) * mm, "end": v(-10.54, -153.25) * mm});
            skArc(sketch, "E11.117.2", {"start": v(-10.62, -153.3) * mm, "mid": v(-10.58, -153.3) * mm, "end": v(-10.54, -153.25) * mm});
            skLineSegment(sketch, "E11.117.3", {"start": v(-10.62, -153.3) * mm, "end": v(-11.05, -153.27) * mm});
            skLineSegment(sketch, "E11.117.4", {"start": v(-11.5, -153.24) * mm, "end": v(-11.05, -153.27) * mm});
            skArc(sketch, "E11.117.5", {"start": v(-11.56, -153.2) * mm, "mid": v(-11.53, -153.22) * mm, "end": v(-11.5, -153.24) * mm});
            skArc(sketch, "E11.117.6", {"start": v(-11.96, -151.93) * mm, "mid": v(-11.76, -152.56) * mm, "end": v(-11.56, -153.2) * mm});
            skLineSegment(sketch, "E11.117.7", {"start": v(-11.96, -151.93) * mm, "end": v(-11.87, -150.66) * mm});
            skLineSegment(sketch, "E11.118.0", {"start": v(-5.98, -152.28) * mm, "end": v(-5.93, -151.01) * mm});
            skArc(sketch, "E11.118.1", {"start": v(-5.98, -152.28) * mm, "mid": v(-6.25, -152.88) * mm, "end": v(-6.52, -153.48) * mm});
            skArc(sketch, "E11.118.2", {"start": v(-6.6, -153.53) * mm, "mid": v(-6.56, -153.52) * mm, "end": v(-6.52, -153.48) * mm});
            skLineSegment(sketch, "E11.118.3", {"start": v(-6.6, -153.53) * mm, "end": v(-7.04, -153.5) * mm});
            skLineSegment(sketch, "E11.118.4", {"start": v(-7.48, -153.49) * mm, "end": v(-7.04, -153.5) * mm});
            skArc(sketch, "E11.118.5", {"start": v(-7.54, -153.44) * mm, "mid": v(-7.52, -153.47) * mm, "end": v(-7.48, -153.49) * mm});
            skArc(sketch, "E11.118.6", {"start": v(-7.98, -152.2) * mm, "mid": v(-7.76, -152.82) * mm, "end": v(-7.54, -153.44) * mm});
            skLineSegment(sketch, "E11.118.7", {"start": v(-7.98, -152.2) * mm, "end": v(-7.92, -150.92) * mm});
            skLineSegment(sketch, "E11.119.0", {"start": v(-2, -152.39) * mm, "end": v(-1.97, -151.12) * mm});
            skArc(sketch, "E11.119.1", {"start": v(-2, -152.39) * mm, "mid": v(-2.24, -153) * mm, "end": v(-2.5, -153.6) * mm});
            skArc(sketch, "E11.119.2", {"start": v(-2.59, -153.65) * mm, "mid": v(-2.54, -153.63) * mm, "end": v(-2.5, -153.6) * mm});
            skLineSegment(sketch, "E11.119.3", {"start": v(-2.59, -153.65) * mm, "end": v(-3.02, -153.64) * mm});
            skLineSegment(sketch, "E11.119.4", {"start": v(-3.46, -153.63) * mm, "end": v(-3.02, -153.64) * mm});
            skArc(sketch, "E11.119.5", {"start": v(-3.52, -153.59) * mm, "mid": v(-3.5, -153.62) * mm, "end": v(-3.46, -153.63) * mm});
            skArc(sketch, "E11.119.6", {"start": v(-3.99, -152.35) * mm, "mid": v(-3.76, -152.97) * mm, "end": v(-3.52, -153.59) * mm});
            skLineSegment(sketch, "E11.119.7", {"start": v(-3.99, -152.35) * mm, "end": v(-3.96, -151.08) * mm});
            skLineSegment(sketch, "E11.120.0", {"start": v(2, -152.39) * mm, "end": v(1.99, -151.12) * mm});
            skArc(sketch, "E11.120.1", {"start": v(2, -152.39) * mm, "mid": v(1.76, -153) * mm, "end": v(1.52, -153.6) * mm});
            skArc(sketch, "E11.120.2", {"start": v(1.44, -153.66) * mm, "mid": v(1.48, -153.65) * mm, "end": v(1.52, -153.6) * mm});
            skLineSegment(sketch, "E11.120.3", {"start": v(1.44, -153.66) * mm, "end": v(1, -153.67) * mm});
            skLineSegment(sketch, "E11.120.4", {"start": v(0.56, -153.67) * mm, "end": v(1, -153.67) * mm});
            skArc(sketch, "E11.120.5", {"start": v(0.5, -153.63) * mm, "mid": v(0.52, -153.66) * mm, "end": v(0.56, -153.67) * mm});
            skArc(sketch, "E11.120.6", {"start": v(0, -152.4) * mm, "mid": v(0.24, -153.01) * mm, "end": v(0.5, -153.63) * mm});
            skLineSegment(sketch, "E11.120.7", {"start": v(0, -152.4) * mm, "end": v(0, -151.13) * mm});
            skLineSegment(sketch, "E11.121.0", {"start": v(5.98, -152.28) * mm, "end": v(5.94, -151.01) * mm});
            skArc(sketch, "E11.121.1", {"start": v(5.98, -152.28) * mm, "mid": v(5.77, -152.9) * mm, "end": v(5.54, -153.52) * mm});
            skArc(sketch, "E11.121.2", {"start": v(5.46, -153.57) * mm, "mid": v(5.5, -153.56) * mm, "end": v(5.54, -153.52) * mm});
            skLineSegment(sketch, "E11.121.3", {"start": v(5.46, -153.57) * mm, "end": v(5.03, -153.59) * mm});
            skLineSegment(sketch, "E11.121.4", {"start": v(4.59, -153.6) * mm, "end": v(5.03, -153.59) * mm});
            skArc(sketch, "E11.121.5", {"start": v(4.52, -153.56) * mm, "mid": v(4.55, -153.6) * mm, "end": v(4.59, -153.6) * mm});
            skArc(sketch, "E11.121.6", {"start": v(3.99, -152.35) * mm, "mid": v(4.25, -152.96) * mm, "end": v(4.52, -153.56) * mm});
            skLineSegment(sketch, "E11.121.7", {"start": v(3.99, -152.35) * mm, "end": v(3.95, -151.08) * mm});
            skLineSegment(sketch, "E11.122.0", {"start": v(9.97, -152.07) * mm, "end": v(9.9, -150.8) * mm});
            skArc(sketch, "E11.122.1", {"start": v(9.97, -152.07) * mm, "mid": v(9.77, -152.7) * mm, "end": v(9.55, -153.32) * mm});
            skArc(sketch, "E11.122.2", {"start": v(9.48, -153.38) * mm, "mid": v(9.52, -153.36) * mm, "end": v(9.55, -153.32) * mm});
            skLineSegment(sketch, "E11.122.3", {"start": v(9.48, -153.38) * mm, "end": v(9.05, -153.4) * mm});
            skLineSegment(sketch, "E11.122.4", {"start": v(8.6, -153.43) * mm, "end": v(9.05, -153.4) * mm});
            skArc(sketch, "E11.122.5", {"start": v(8.54, -153.39) * mm, "mid": v(8.57, -153.42) * mm, "end": v(8.6, -153.43) * mm});
            skArc(sketch, "E11.122.6", {"start": v(7.98, -152.2) * mm, "mid": v(8.25, -152.8) * mm, "end": v(8.54, -153.39) * mm});
            skLineSegment(sketch, "E11.122.7", {"start": v(7.98, -152.2) * mm, "end": v(7.9, -150.92) * mm});
            skLineSegment(sketch, "E11.123.0", {"start": v(13.94, -151.76) * mm, "end": v(13.84, -150.5) * mm});
            skArc(sketch, "E11.123.1", {"start": v(13.94, -151.76) * mm, "mid": v(13.76, -152.39) * mm, "end": v(13.56, -153.02) * mm});
            skArc(sketch, "E11.123.2", {"start": v(13.49, -153.08) * mm, "mid": v(13.54, -153.06) * mm, "end": v(13.56, -153.02) * mm});
            skLineSegment(sketch, "E11.123.3", {"start": v(13.49, -153.08) * mm, "end": v(13.06, -153.11) * mm});
            skLineSegment(sketch, "E11.123.4", {"start": v(12.62, -153.15) * mm, "end": v(13.06, -153.11) * mm});
            skArc(sketch, "E11.123.5", {"start": v(12.55, -153.11) * mm, "mid": v(12.58, -153.14) * mm, "end": v(12.62, -153.15) * mm});
            skArc(sketch, "E11.123.6", {"start": v(11.96, -151.93) * mm, "mid": v(12.25, -152.52) * mm, "end": v(12.55, -153.11) * mm});
            skLineSegment(sketch, "E11.123.7", {"start": v(11.96, -151.93) * mm, "end": v(11.85, -150.66) * mm});
            skLineSegment(sketch, "E11.124.0", {"start": v(17.91, -151.34) * mm, "end": v(17.77, -150.08) * mm});
            skArc(sketch, "E11.124.1", {"start": v(17.91, -151.34) * mm, "mid": v(17.74, -151.98) * mm, "end": v(17.57, -152.6) * mm});
            skArc(sketch, "E11.124.2", {"start": v(17.5, -152.67) * mm, "mid": v(17.54, -152.65) * mm, "end": v(17.57, -152.6) * mm});
            skLineSegment(sketch, "E11.124.3", {"start": v(17.5, -152.67) * mm, "end": v(17.06, -152.72) * mm});
            skLineSegment(sketch, "E11.124.4", {"start": v(16.62, -152.77) * mm, "end": v(17.06, -152.72) * mm});
            skArc(sketch, "E11.124.5", {"start": v(16.55, -152.73) * mm, "mid": v(16.58, -152.76) * mm, "end": v(16.62, -152.77) * mm});
            skArc(sketch, "E11.124.6", {"start": v(15.93, -151.57) * mm, "mid": v(16.24, -152.15) * mm, "end": v(16.55, -152.73) * mm});
            skLineSegment(sketch, "E11.124.7", {"start": v(15.93, -151.57) * mm, "end": v(15.79, -150.3) * mm});
            skLineSegment(sketch, "E11.125.0", {"start": v(21.87, -150.82) * mm, "end": v(21.7, -149.56) * mm});
            skArc(sketch, "E11.125.1", {"start": v(21.87, -150.82) * mm, "mid": v(21.72, -151.46) * mm, "end": v(21.55, -152.1) * mm});
            skArc(sketch, "E11.125.2", {"start": v(21.48, -152.16) * mm, "mid": v(21.53, -152.14) * mm, "end": v(21.55, -152.1) * mm});
            skLineSegment(sketch, "E11.125.3", {"start": v(21.48, -152.16) * mm, "end": v(21.05, -152.22) * mm});
            skLineSegment(sketch, "E11.125.4", {"start": v(20.62, -152.28) * mm, "end": v(21.05, -152.22) * mm});
            skArc(sketch, "E11.125.5", {"start": v(20.55, -152.25) * mm, "mid": v(20.58, -152.27) * mm, "end": v(20.62, -152.28) * mm});
            skArc(sketch, "E11.125.6", {"start": v(19.9, -151.1) * mm, "mid": v(20.21, -151.67) * mm, "end": v(20.55, -152.25) * mm});
            skLineSegment(sketch, "E11.125.7", {"start": v(19.9, -151.1) * mm, "end": v(19.72, -149.84) * mm});
            skLineSegment(sketch, "E11.126.0", {"start": v(25.8, -150.2) * mm, "end": v(25.6, -148.95) * mm});
            skArc(sketch, "E11.126.1", {"start": v(25.8, -150.2) * mm, "mid": v(25.67, -150.84) * mm, "end": v(25.53, -151.48) * mm});
            skArc(sketch, "E11.126.2", {"start": v(25.46, -151.55) * mm, "mid": v(25.5, -151.52) * mm, "end": v(25.53, -151.48) * mm});
            skLineSegment(sketch, "E11.126.3", {"start": v(25.46, -151.55) * mm, "end": v(25.03, -151.62) * mm});
            skLineSegment(sketch, "E11.126.4", {"start": v(24.6, -151.69) * mm, "end": v(25.03, -151.62) * mm});
            skArc(sketch, "E11.126.5", {"start": v(24.52, -151.66) * mm, "mid": v(24.56, -151.68) * mm, "end": v(24.6, -151.69) * mm});
            skArc(sketch, "E11.126.6", {"start": v(23.84, -150.52) * mm, "mid": v(24.18, -151.1) * mm, "end": v(24.52, -151.66) * mm});
            skLineSegment(sketch, "E11.126.7", {"start": v(23.84, -150.52) * mm, "end": v(23.63, -149.27) * mm});
            skLineSegment(sketch, "E11.127.0", {"start": v(29.73, -149.47) * mm, "end": v(29.5, -148.22) * mm});
            skArc(sketch, "E11.127.1", {"start": v(29.73, -149.47) * mm, "mid": v(29.61, -150.12) * mm, "end": v(29.48, -150.76) * mm});
            skArc(sketch, "E11.127.2", {"start": v(29.41, -150.83) * mm, "mid": v(29.46, -150.8) * mm, "end": v(29.48, -150.76) * mm});
            skLineSegment(sketch, "E11.127.3", {"start": v(29.41, -150.83) * mm, "end": v(29, -150.91) * mm});
            skLineSegment(sketch, "E11.127.4", {"start": v(28.56, -151) * mm, "end": v(29, -150.91) * mm});
            skArc(sketch, "E11.127.5", {"start": v(28.49, -150.96) * mm, "mid": v(28.52, -150.99) * mm, "end": v(28.56, -151) * mm});
            skArc(sketch, "E11.127.6", {"start": v(27.77, -149.85) * mm, "mid": v(28.12, -150.4) * mm, "end": v(28.49, -150.96) * mm});
            skLineSegment(sketch, "E11.127.7", {"start": v(27.77, -149.85) * mm, "end": v(27.53, -148.6) * mm});
            skLineSegment(sketch, "E11.128.0", {"start": v(33.63, -148.64) * mm, "end": v(33.36, -147.4) * mm});
            skArc(sketch, "E11.128.1", {"start": v(33.63, -148.64) * mm, "mid": v(33.53, -149.3) * mm, "end": v(33.42, -149.94) * mm});
            skArc(sketch, "E11.128.2", {"start": v(33.35, -150) * mm, "mid": v(33.4, -149.98) * mm, "end": v(33.42, -149.94) * mm});
            skLineSegment(sketch, "E11.128.3", {"start": v(33.35, -150) * mm, "end": v(32.93, -150.1) * mm});
            skLineSegment(sketch, "E11.128.4", {"start": v(32.5, -150.2) * mm, "end": v(32.93, -150.1) * mm});
            skArc(sketch, "E11.128.5", {"start": v(32.43, -150.16) * mm, "mid": v(32.46, -150.2) * mm, "end": v(32.5, -150.2) * mm});
            skArc(sketch, "E11.128.6", {"start": v(31.69, -149.07) * mm, "mid": v(32.05, -149.62) * mm, "end": v(32.43, -150.16) * mm});
            skLineSegment(sketch, "E11.128.7", {"start": v(31.69, -149.07) * mm, "end": v(31.41, -147.83) * mm});
            skLineSegment(sketch, "E11.129.0", {"start": v(37.51, -147.71) * mm, "end": v(37.2, -146.48) * mm});
            skArc(sketch, "E11.129.1", {"start": v(37.51, -147.71) * mm, "mid": v(37.43, -148.36) * mm, "end": v(37.33, -149.01) * mm});
            skArc(sketch, "E11.129.2", {"start": v(37.27, -149.08) * mm, "mid": v(37.31, -149.06) * mm, "end": v(37.33, -149.01) * mm});
            skLineSegment(sketch, "E11.129.3", {"start": v(37.27, -149.08) * mm, "end": v(36.85, -149.19) * mm});
            skLineSegment(sketch, "E11.129.4", {"start": v(36.42, -149.3) * mm, "end": v(36.85, -149.19) * mm});
            skArc(sketch, "E11.129.5", {"start": v(36.35, -149.26) * mm, "mid": v(36.38, -149.29) * mm, "end": v(36.42, -149.3) * mm});
            skArc(sketch, "E11.129.6", {"start": v(35.58, -148.19) * mm, "mid": v(35.96, -148.73) * mm, "end": v(36.35, -149.26) * mm});
            skLineSegment(sketch, "E11.129.7", {"start": v(35.58, -148.19) * mm, "end": v(35.27, -146.96) * mm});
            skLineSegment(sketch, "E11.130.0", {"start": v(41.37, -146.68) * mm, "end": v(41.03, -145.45) * mm});
            skArc(sketch, "E11.130.1", {"start": v(41.37, -146.68) * mm, "mid": v(41.3, -147.33) * mm, "end": v(41.22, -147.98) * mm});
            skArc(sketch, "E11.130.2", {"start": v(41.16, -148.06) * mm, "mid": v(41.2, -148.03) * mm, "end": v(41.22, -147.98) * mm});
            skLineSegment(sketch, "E11.130.3", {"start": v(41.16, -148.06) * mm, "end": v(40.74, -148.17) * mm});
            skLineSegment(sketch, "E11.130.4", {"start": v(40.32, -148.29) * mm, "end": v(40.74, -148.17) * mm});
            skArc(sketch, "E11.130.5", {"start": v(40.24, -148.26) * mm, "mid": v(40.28, -148.29) * mm, "end": v(40.32, -148.29) * mm});
            skArc(sketch, "E11.130.6", {"start": v(39.44, -147.2) * mm, "mid": v(39.84, -147.74) * mm, "end": v(40.24, -148.26) * mm});
            skLineSegment(sketch, "E11.130.7", {"start": v(39.44, -147.2) * mm, "end": v(39.1, -145.98) * mm});
            skLineSegment(sketch, "E11.131.0", {"start": v(45.2, -145.55) * mm, "end": v(44.82, -144.33) * mm});
            skArc(sketch, "E11.131.1", {"start": v(45.2, -145.55) * mm, "mid": v(45.14, -146.2) * mm, "end": v(45.08, -146.85) * mm});
            skArc(sketch, "E11.131.2", {"start": v(45.02, -146.93) * mm, "mid": v(45.06, -146.9) * mm, "end": v(45.08, -146.85) * mm});
            skLineSegment(sketch, "E11.131.3", {"start": v(45.02, -146.93) * mm, "end": v(44.6, -147.05) * mm});
            skLineSegment(sketch, "E11.131.4", {"start": v(44.19, -147.18) * mm, "end": v(44.6, -147.05) * mm});
            skArc(sketch, "E11.131.5", {"start": v(44.1, -147.16) * mm, "mid": v(44.14, -147.18) * mm, "end": v(44.19, -147.18) * mm});
            skArc(sketch, "E11.131.6", {"start": v(43.28, -146.12) * mm, "mid": v(43.7, -146.64) * mm, "end": v(44.1, -147.16) * mm});
            skLineSegment(sketch, "E11.131.7", {"start": v(43.28, -146.12) * mm, "end": v(42.92, -144.9) * mm});
            skLineSegment(sketch, "E11.132.0", {"start": v(48.99, -144.31) * mm, "end": v(48.59, -143.1) * mm});
            skArc(sketch, "E11.132.1", {"start": v(48.99, -144.31) * mm, "mid": v(48.95, -144.97) * mm, "end": v(48.91, -145.62) * mm});
            skArc(sketch, "E11.132.2", {"start": v(48.85, -145.7) * mm, "mid": v(48.9, -145.67) * mm, "end": v(48.91, -145.62) * mm});
            skLineSegment(sketch, "E11.132.3", {"start": v(48.85, -145.7) * mm, "end": v(48.44, -145.84) * mm});
            skLineSegment(sketch, "E11.132.4", {"start": v(48.02, -145.97) * mm, "end": v(48.44, -145.84) * mm});
            skArc(sketch, "E11.132.5", {"start": v(47.95, -145.95) * mm, "mid": v(47.98, -145.97) * mm, "end": v(48.02, -145.97) * mm});
            skArc(sketch, "E11.132.6", {"start": v(47.1, -144.94) * mm, "mid": v(47.52, -145.45) * mm, "end": v(47.95, -145.95) * mm});
            skLineSegment(sketch, "E11.132.7", {"start": v(47.1, -144.94) * mm, "end": v(46.7, -143.74) * mm});
            skLineSegment(sketch, "E11.133.0", {"start": v(52.75, -142.98) * mm, "end": v(52.32, -141.79) * mm});
            skArc(sketch, "E11.133.1", {"start": v(52.75, -142.98) * mm, "mid": v(52.73, -143.64) * mm, "end": v(52.7, -144.3) * mm});
            skArc(sketch, "E11.133.2", {"start": v(52.65, -144.37) * mm, "mid": v(52.69, -144.34) * mm, "end": v(52.7, -144.3) * mm});
            skLineSegment(sketch, "E11.133.3", {"start": v(52.65, -144.37) * mm, "end": v(52.24, -144.52) * mm});
            skLineSegment(sketch, "E11.133.4", {"start": v(51.83, -144.67) * mm, "end": v(52.24, -144.52) * mm});
            skArc(sketch, "E11.133.5", {"start": v(51.75, -144.65) * mm, "mid": v(51.79, -144.67) * mm, "end": v(51.83, -144.67) * mm});
            skArc(sketch, "E11.133.6", {"start": v(50.87, -143.66) * mm, "mid": v(51.3, -144.16) * mm, "end": v(51.75, -144.65) * mm});
            skLineSegment(sketch, "E11.133.7", {"start": v(50.87, -143.66) * mm, "end": v(50.44, -142.46) * mm});
            skLineSegment(sketch, "E11.134.0", {"start": v(56.47, -141.55) * mm, "end": v(56.01, -140.37) * mm});
            skArc(sketch, "E11.134.1", {"start": v(56.47, -141.55) * mm, "mid": v(56.47, -142.2) * mm, "end": v(56.46, -142.86) * mm});
            skArc(sketch, "E11.134.2", {"start": v(56.4, -142.94) * mm, "mid": v(56.45, -142.91) * mm, "end": v(56.46, -142.86) * mm});
            skLineSegment(sketch, "E11.134.3", {"start": v(56.4, -142.94) * mm, "end": v(56, -143.1) * mm});
            skLineSegment(sketch, "E11.134.4", {"start": v(55.6, -143.26) * mm, "end": v(56, -143.1) * mm});
            skArc(sketch, "E11.134.5", {"start": v(55.52, -143.24) * mm, "mid": v(55.56, -143.26) * mm, "end": v(55.6, -143.26) * mm});
            skArc(sketch, "E11.134.6", {"start": v(54.62, -142.28) * mm, "mid": v(55.06, -142.76) * mm, "end": v(55.52, -143.24) * mm});
            skLineSegment(sketch, "E11.134.7", {"start": v(54.62, -142.28) * mm, "end": v(54.15, -141.1) * mm});
            skLineSegment(sketch, "E11.135.0", {"start": v(60.16, -140.02) * mm, "end": v(59.67, -138.85) * mm});
            skArc(sketch, "E11.135.1", {"start": v(60.16, -140.02) * mm, "mid": v(60.18, -140.68) * mm, "end": v(60.18, -141.34) * mm});
            skArc(sketch, "E11.135.2", {"start": v(60.13, -141.42) * mm, "mid": v(60.17, -141.38) * mm, "end": v(60.18, -141.34) * mm});
            skLineSegment(sketch, "E11.135.3", {"start": v(60.13, -141.42) * mm, "end": v(59.74, -141.59) * mm});
            skLineSegment(sketch, "E11.135.4", {"start": v(59.33, -141.76) * mm, "end": v(59.74, -141.59) * mm});
            skArc(sketch, "E11.135.5", {"start": v(59.25, -141.74) * mm, "mid": v(59.29, -141.76) * mm, "end": v(59.33, -141.76) * mm});
            skArc(sketch, "E11.135.6", {"start": v(58.32, -140.8) * mm, "mid": v(58.78, -141.27) * mm, "end": v(59.25, -141.74) * mm});
            skLineSegment(sketch, "E11.135.7", {"start": v(58.32, -140.8) * mm, "end": v(57.83, -139.63) * mm});
            skLineSegment(sketch, "E11.136.0", {"start": v(63.8, -138.4) * mm, "end": v(63.28, -137.24) * mm});
            skArc(sketch, "E11.136.1", {"start": v(63.8, -138.4) * mm, "mid": v(63.84, -139.06) * mm, "end": v(63.86, -139.71) * mm});
            skArc(sketch, "E11.136.2", {"start": v(63.81, -139.8) * mm, "mid": v(63.85, -139.76) * mm, "end": v(63.86, -139.71) * mm});
            skLineSegment(sketch, "E11.136.3", {"start": v(63.81, -139.8) * mm, "end": v(63.42, -139.97) * mm});
            skLineSegment(sketch, "E11.136.4", {"start": v(63.02, -140.15) * mm, "end": v(63.42, -139.97) * mm});
            skArc(sketch, "E11.136.5", {"start": v(62.94, -140.14) * mm, "mid": v(62.98, -140.16) * mm, "end": v(63.02, -140.15) * mm});
            skArc(sketch, "E11.136.6", {"start": v(61.99, -139.22) * mm, "mid": v(62.46, -139.69) * mm, "end": v(62.94, -140.14) * mm});
            skLineSegment(sketch, "E11.136.7", {"start": v(61.99, -139.22) * mm, "end": v(61.46, -138.07) * mm});
            skLineSegment(sketch, "E11.137.0", {"start": v(67.4, -136.68) * mm, "end": v(66.85, -135.54) * mm});
            skArc(sketch, "E11.137.1", {"start": v(67.4, -136.68) * mm, "mid": v(67.46, -137.34) * mm, "end": v(67.5, -138) * mm});
            skArc(sketch, "E11.137.2", {"start": v(67.45, -138.08) * mm, "mid": v(67.49, -138.04) * mm, "end": v(67.5, -138) * mm});
            skLineSegment(sketch, "E11.137.3", {"start": v(67.45, -138.08) * mm, "end": v(67.06, -138.27) * mm});
            skLineSegment(sketch, "E11.137.4", {"start": v(66.67, -138.46) * mm, "end": v(67.06, -138.27) * mm});
            skArc(sketch, "E11.137.5", {"start": v(66.59, -138.45) * mm, "mid": v(66.62, -138.46) * mm, "end": v(66.67, -138.46) * mm});
            skArc(sketch, "E11.137.6", {"start": v(65.6, -137.55) * mm, "mid": v(66.1, -138) * mm, "end": v(66.59, -138.45) * mm});
            skLineSegment(sketch, "E11.137.7", {"start": v(65.6, -137.55) * mm, "end": v(65.06, -136.41) * mm});
            skLineSegment(sketch, "E11.138.0", {"start": v(70.96, -134.87) * mm, "end": v(70.38, -133.74) * mm});
            skArc(sketch, "E11.138.1", {"start": v(70.96, -134.87) * mm, "mid": v(71.03, -135.52) * mm, "end": v(71.09, -136.18) * mm});
            skArc(sketch, "E11.138.2", {"start": v(71.04, -136.26) * mm, "mid": v(71.08, -136.23) * mm, "end": v(71.09, -136.18) * mm});
            skLineSegment(sketch, "E11.138.3", {"start": v(71.04, -136.26) * mm, "end": v(70.66, -136.46) * mm});
            skLineSegment(sketch, "E11.138.4", {"start": v(70.27, -136.66) * mm, "end": v(70.66, -136.46) * mm});
            skArc(sketch, "E11.138.5", {"start": v(70.19, -136.66) * mm, "mid": v(70.23, -136.67) * mm, "end": v(70.27, -136.66) * mm});
            skArc(sketch, "E11.138.6", {"start": v(69.19, -135.79) * mm, "mid": v(69.68, -136.23) * mm, "end": v(70.19, -136.66) * mm});
            skLineSegment(sketch, "E11.138.7", {"start": v(69.19, -135.79) * mm, "end": v(68.6, -134.66) * mm});
            skLineSegment(sketch, "E11.139.0", {"start": v(74.47, -132.97) * mm, "end": v(73.85, -131.86) * mm});
            skArc(sketch, "E11.139.1", {"start": v(74.47, -132.97) * mm, "mid": v(74.55, -133.62) * mm, "end": v(74.63, -134.27) * mm});
            skArc(sketch, "E11.139.2", {"start": v(74.58, -134.36) * mm, "mid": v(74.62, -134.32) * mm, "end": v(74.63, -134.27) * mm});
            skLineSegment(sketch, "E11.139.3", {"start": v(74.58, -134.36) * mm, "end": v(74.2, -134.57) * mm});
            skLineSegment(sketch, "E11.139.4", {"start": v(73.82, -134.78) * mm, "end": v(74.2, -134.57) * mm});
            skArc(sketch, "E11.139.5", {"start": v(73.74, -134.77) * mm, "mid": v(73.78, -134.79) * mm, "end": v(73.82, -134.78) * mm});
            skArc(sketch, "E11.139.6", {"start": v(72.72, -133.93) * mm, "mid": v(73.23, -134.36) * mm, "end": v(73.74, -134.77) * mm});
            skLineSegment(sketch, "E11.139.7", {"start": v(72.72, -133.93) * mm, "end": v(72.1, -132.82) * mm});
            skLineSegment(sketch, "E11.140.0", {"start": v(77.92, -130.97) * mm, "end": v(77.28, -129.88) * mm});
            skArc(sketch, "E11.140.1", {"start": v(77.92, -130.97) * mm, "mid": v(78.03, -131.62) * mm, "end": v(78.12, -132.27) * mm});
            skArc(sketch, "E11.140.2", {"start": v(78.08, -132.36) * mm, "mid": v(78.1, -132.32) * mm, "end": v(78.12, -132.27) * mm});
            skLineSegment(sketch, "E11.140.3", {"start": v(78.08, -132.36) * mm, "end": v(77.7, -132.58) * mm});
            skLineSegment(sketch, "E11.140.4", {"start": v(77.32, -132.8) * mm, "end": v(77.7, -132.58) * mm});
            skArc(sketch, "E11.140.5", {"start": v(77.24, -132.8) * mm, "mid": v(77.28, -132.8) * mm, "end": v(77.32, -132.8) * mm});
            skArc(sketch, "E11.140.6", {"start": v(76.2, -131.98) * mm, "mid": v(76.72, -132.4) * mm, "end": v(77.24, -132.8) * mm});
            skLineSegment(sketch, "E11.140.7", {"start": v(76.2, -131.98) * mm, "end": v(75.56, -130.89) * mm});
            skLineSegment(sketch, "E11.141.0", {"start": v(81.32, -128.89) * mm, "end": v(80.65, -127.81) * mm});
            skArc(sketch, "E11.141.1", {"start": v(81.32, -128.89) * mm, "mid": v(81.44, -129.53) * mm, "end": v(81.55, -130.18) * mm});
            skArc(sketch, "E11.141.2", {"start": v(81.51, -130.27) * mm, "mid": v(81.55, -130.23) * mm, "end": v(81.55, -130.18) * mm});
            skLineSegment(sketch, "E11.141.3", {"start": v(81.51, -130.27) * mm, "end": v(81.15, -130.5) * mm});
            skLineSegment(sketch, "E11.141.4", {"start": v(80.77, -130.73) * mm, "end": v(81.15, -130.5) * mm});
            skArc(sketch, "E11.141.5", {"start": v(80.7, -130.73) * mm, "mid": v(80.73, -130.74) * mm, "end": v(80.77, -130.73) * mm});
            skArc(sketch, "E11.141.6", {"start": v(79.63, -129.94) * mm, "mid": v(80.16, -130.34) * mm, "end": v(80.7, -130.73) * mm});
            skLineSegment(sketch, "E11.141.7", {"start": v(79.63, -129.94) * mm, "end": v(78.96, -128.86) * mm});
            skLineSegment(sketch, "E11.142.0", {"start": v(84.67, -126.72) * mm, "end": v(83.97, -125.66) * mm});
            skArc(sketch, "E11.142.1", {"start": v(84.67, -126.72) * mm, "mid": v(84.8, -127.36) * mm, "end": v(84.93, -128) * mm});
            skArc(sketch, "E11.142.2", {"start": v(84.9, -128.1) * mm, "mid": v(84.93, -128.05) * mm, "end": v(84.93, -128) * mm});
            skLineSegment(sketch, "E11.142.3", {"start": v(84.9, -128.1) * mm, "end": v(84.54, -128.33) * mm});
            skLineSegment(sketch, "E11.142.4", {"start": v(84.17, -128.57) * mm, "end": v(84.54, -128.33) * mm});
            skArc(sketch, "E11.142.5", {"start": v(84.09, -128.57) * mm, "mid": v(84.13, -128.58) * mm, "end": v(84.17, -128.57) * mm});
            skArc(sketch, "E11.142.6", {"start": v(83, -127.81) * mm, "mid": v(83.54, -128.2) * mm, "end": v(84.09, -128.57) * mm});
            skLineSegment(sketch, "E11.142.7", {"start": v(83, -127.81) * mm, "end": v(82.3, -126.75) * mm});
            skLineSegment(sketch, "E11.143.0", {"start": v(87.96, -124.46) * mm, "end": v(87.23, -123.41) * mm});
            skArc(sketch, "E11.143.1", {"start": v(87.96, -124.46) * mm, "mid": v(88.11, -125.1) * mm, "end": v(88.25, -125.73) * mm});
            skArc(sketch, "E11.143.2", {"start": v(88.22, -125.82) * mm, "mid": v(88.25, -125.78) * mm, "end": v(88.25, -125.73) * mm});
            skLineSegment(sketch, "E11.143.3", {"start": v(88.22, -125.82) * mm, "end": v(87.87, -126.07) * mm});
            skLineSegment(sketch, "E11.143.4", {"start": v(87.5, -126.32) * mm, "end": v(87.87, -126.07) * mm});
            skArc(sketch, "E11.143.5", {"start": v(87.43, -126.32) * mm, "mid": v(87.46, -126.34) * mm, "end": v(87.5, -126.32) * mm});
            skArc(sketch, "E11.143.6", {"start": v(86.32, -125.6) * mm, "mid": v(86.87, -125.97) * mm, "end": v(87.43, -126.32) * mm});
            skLineSegment(sketch, "E11.143.7", {"start": v(86.32, -125.6) * mm, "end": v(85.6, -124.55) * mm});
            skLineSegment(sketch, "E11.144.0", {"start": v(91.18, -122.11) * mm, "end": v(90.43, -121.09) * mm});
            skArc(sketch, "E11.144.1", {"start": v(91.18, -122.11) * mm, "mid": v(91.36, -122.74) * mm, "end": v(91.52, -123.38) * mm});
            skArc(sketch, "E11.144.2", {"start": v(91.48, -123.47) * mm, "mid": v(91.51, -123.43) * mm, "end": v(91.52, -123.38) * mm});
            skLineSegment(sketch, "E11.144.3", {"start": v(91.48, -123.47) * mm, "end": v(91.14, -123.73) * mm});
            skLineSegment(sketch, "E11.144.4", {"start": v(90.78, -123.99) * mm, "end": v(91.14, -123.73) * mm});
            skArc(sketch, "E11.144.5", {"start": v(90.7, -124) * mm, "mid": v(90.74, -124) * mm, "end": v(90.78, -123.99) * mm});
            skArc(sketch, "E11.144.6", {"start": v(89.58, -123.3) * mm, "mid": v(90.14, -123.65) * mm, "end": v(90.7, -124) * mm});
            skLineSegment(sketch, "E11.144.7", {"start": v(89.58, -123.3) * mm, "end": v(88.83, -122.27) * mm});
            skLineSegment(sketch, "E11.145.0", {"start": v(94.35, -119.68) * mm, "end": v(93.57, -118.68) * mm});
            skArc(sketch, "E11.145.1", {"start": v(94.35, -119.68) * mm, "mid": v(94.54, -120.31) * mm, "end": v(94.71, -120.94) * mm});
            skArc(sketch, "E11.145.2", {"start": v(94.68, -121.04) * mm, "mid": v(94.71, -121) * mm, "end": v(94.71, -120.94) * mm});
            skLineSegment(sketch, "E11.145.3", {"start": v(94.68, -121.04) * mm, "end": v(94.34, -121.3) * mm});
            skLineSegment(sketch, "E11.145.4", {"start": v(94, -121.57) * mm, "end": v(94.34, -121.3) * mm});
            skArc(sketch, "E11.145.5", {"start": v(93.92, -121.58) * mm, "mid": v(93.96, -121.58) * mm, "end": v(94, -121.57) * mm});
            skArc(sketch, "E11.145.6", {"start": v(92.78, -120.9) * mm, "mid": v(93.34, -121.25) * mm, "end": v(93.92, -121.58) * mm});
            skLineSegment(sketch, "E11.145.7", {"start": v(92.78, -120.9) * mm, "end": v(92, -119.9) * mm});
            skLineSegment(sketch, "E11.146.0", {"start": v(97.45, -117.17) * mm, "end": v(96.64, -116.19) * mm});
            skArc(sketch, "E11.146.1", {"start": v(97.45, -117.17) * mm, "mid": v(97.65, -117.8) * mm, "end": v(97.85, -118.42) * mm});
            skArc(sketch, "E11.146.2", {"start": v(97.82, -118.52) * mm, "mid": v(97.85, -118.47) * mm, "end": v(97.85, -118.42) * mm});
            skLineSegment(sketch, "E11.146.3", {"start": v(97.82, -118.52) * mm, "end": v(97.49, -118.79) * mm});
            skLineSegment(sketch, "E11.146.4", {"start": v(97.15, -119.07) * mm, "end": v(97.49, -118.79) * mm});
            skArc(sketch, "E11.146.5", {"start": v(97.07, -119.08) * mm, "mid": v(97.1, -119.08) * mm, "end": v(97.15, -119.07) * mm});
            skArc(sketch, "E11.146.6", {"start": v(95.9, -118.44) * mm, "mid": v(96.48, -118.76) * mm, "end": v(97.07, -119.08) * mm});
            skLineSegment(sketch, "E11.146.7", {"start": v(95.9, -118.44) * mm, "end": v(95.1, -117.46) * mm});
            skLineSegment(sketch, "E11.147.0", {"start": v(100.48, -114.58) * mm, "end": v(99.65, -113.62) * mm});
            skArc(sketch, "E11.147.1", {"start": v(100.48, -114.58) * mm, "mid": v(100.7, -115.2) * mm, "end": v(100.91, -115.82) * mm});
            skArc(sketch, "E11.147.2", {"start": v(100.89, -115.91) * mm, "mid": v(100.92, -115.87) * mm, "end": v(100.91, -115.82) * mm});
            skLineSegment(sketch, "E11.147.3", {"start": v(100.89, -115.91) * mm, "end": v(100.56, -116.2) * mm});
            skLineSegment(sketch, "E11.147.4", {"start": v(100.23, -116.48) * mm, "end": v(100.56, -116.2) * mm});
            skArc(sketch, "E11.147.5", {"start": v(100.15, -116.5) * mm, "mid": v(100.2, -116.5) * mm, "end": v(100.23, -116.48) * mm});
            skArc(sketch, "E11.147.6", {"start": v(98.98, -115.89) * mm, "mid": v(99.56, -116.2) * mm, "end": v(100.15, -116.5) * mm});
            skLineSegment(sketch, "E11.147.7", {"start": v(98.98, -115.89) * mm, "end": v(98.14, -114.93) * mm});
            skLineSegment(sketch, "E11.148.0", {"start": v(103.45, -111.91) * mm, "end": v(102.6, -110.97) * mm});
            skArc(sketch, "E11.148.1", {"start": v(103.45, -111.91) * mm, "mid": v(103.69, -112.52) * mm, "end": v(103.91, -113.14) * mm});
            skArc(sketch, "E11.148.2", {"start": v(103.89, -113.23) * mm, "mid": v(103.91, -113.19) * mm, "end": v(103.91, -113.14) * mm});
            skLineSegment(sketch, "E11.148.3", {"start": v(103.89, -113.23) * mm, "end": v(103.57, -113.52) * mm});
            skLineSegment(sketch, "E11.148.4", {"start": v(103.24, -113.82) * mm, "end": v(103.57, -113.52) * mm});
            skArc(sketch, "E11.148.5", {"start": v(103.17, -113.83) * mm, "mid": v(103.2, -113.84) * mm, "end": v(103.24, -113.82) * mm});
            skArc(sketch, "E11.148.6", {"start": v(101.98, -113.26) * mm, "mid": v(102.57, -113.55) * mm, "end": v(103.17, -113.83) * mm});
            skLineSegment(sketch, "E11.148.7", {"start": v(101.98, -113.26) * mm, "end": v(101.12, -112.32) * mm});
            skLineSegment(sketch, "E11.149.0", {"start": v(106.34, -109.16) * mm, "end": v(105.46, -108.25) * mm});
            skArc(sketch, "E11.149.1", {"start": v(106.34, -109.16) * mm, "mid": v(106.6, -109.77) * mm, "end": v(106.84, -110.38) * mm});
            skArc(sketch, "E11.149.2", {"start": v(106.82, -110.48) * mm, "mid": v(106.84, -110.43) * mm, "end": v(106.84, -110.38) * mm});
            skLineSegment(sketch, "E11.149.3", {"start": v(106.82, -110.48) * mm, "end": v(106.5, -110.77) * mm});
            skLineSegment(sketch, "E11.149.4", {"start": v(106.19, -111.08) * mm, "end": v(106.5, -110.77) * mm});
            skArc(sketch, "E11.149.5", {"start": v(106.11, -111.1) * mm, "mid": v(106.15, -111.1) * mm, "end": v(106.19, -111.08) * mm});
            skArc(sketch, "E11.149.6", {"start": v(104.9, -110.55) * mm, "mid": v(105.5, -110.83) * mm, "end": v(106.11, -111.1) * mm});
            skLineSegment(sketch, "E11.149.7", {"start": v(104.9, -110.55) * mm, "end": v(104.02, -109.63) * mm});
            skLineSegment(sketch, "E11.150.0", {"start": v(109.16, -106.34) * mm, "end": v(108.26, -105.45) * mm});
            skArc(sketch, "E11.150.1", {"start": v(109.16, -106.34) * mm, "mid": v(109.43, -106.94) * mm, "end": v(109.7, -107.54) * mm});
            skArc(sketch, "E11.150.2", {"start": v(109.67, -107.64) * mm, "mid": v(109.7, -107.6) * mm, "end": v(109.7, -107.54) * mm});
            skLineSegment(sketch, "E11.150.3", {"start": v(109.67, -107.64) * mm, "end": v(109.37, -107.95) * mm});
            skLineSegment(sketch, "E11.150.4", {"start": v(109.06, -108.26) * mm, "end": v(109.37, -107.95) * mm});
            skArc(sketch, "E11.150.5", {"start": v(108.98, -108.28) * mm, "mid": v(109.02, -108.28) * mm, "end": v(109.06, -108.26) * mm});
            skArc(sketch, "E11.150.6", {"start": v(107.76, -107.76) * mm, "mid": v(108.37, -108.03) * mm, "end": v(108.98, -108.28) * mm});
            skLineSegment(sketch, "E11.150.7", {"start": v(107.76, -107.76) * mm, "end": v(106.86, -106.87) * mm});
            skLineSegment(sketch, "E11.151.0", {"start": v(111.91, -103.45) * mm, "end": v(110.98, -102.58) * mm});
            skArc(sketch, "E11.151.1", {"start": v(111.91, -103.45) * mm, "mid": v(112.2, -104.04) * mm, "end": v(112.47, -104.64) * mm});
            skArc(sketch, "E11.151.2", {"start": v(112.45, -104.73) * mm, "mid": v(112.47, -104.69) * mm, "end": v(112.47, -104.64) * mm});
            skLineSegment(sketch, "E11.151.3", {"start": v(112.45, -104.73) * mm, "end": v(112.16, -105.05) * mm});
            skLineSegment(sketch, "E11.151.4", {"start": v(111.86, -105.37) * mm, "end": v(112.16, -105.05) * mm});
            skArc(sketch, "E11.151.5", {"start": v(111.78, -105.39) * mm, "mid": v(111.82, -105.39) * mm, "end": v(111.86, -105.37) * mm});
            skArc(sketch, "E11.151.6", {"start": v(110.55, -104.9) * mm, "mid": v(111.16, -105.15) * mm, "end": v(111.78, -105.39) * mm});
            skLineSegment(sketch, "E11.151.7", {"start": v(110.55, -104.9) * mm, "end": v(109.62, -104.04) * mm});
            skLineSegment(sketch, "E11.152.0", {"start": v(114.58, -100.48) * mm, "end": v(113.63, -99.64) * mm});
            skArc(sketch, "E11.152.1", {"start": v(114.58, -100.48) * mm, "mid": v(114.88, -101.07) * mm, "end": v(115.17, -101.66) * mm});
            skArc(sketch, "E11.152.2", {"start": v(115.15, -101.75) * mm, "mid": v(115.18, -101.7) * mm, "end": v(115.17, -101.66) * mm});
            skLineSegment(sketch, "E11.152.3", {"start": v(115.15, -101.75) * mm, "end": v(114.87, -102.08) * mm});
            skLineSegment(sketch, "E11.152.4", {"start": v(114.58, -102.4) * mm, "end": v(114.87, -102.08) * mm});
            skArc(sketch, "E11.152.5", {"start": v(114.5, -102.43) * mm, "mid": v(114.54, -102.43) * mm, "end": v(114.58, -102.4) * mm});
            skArc(sketch, "E11.152.6", {"start": v(113.26, -101.98) * mm, "mid": v(113.88, -102.2) * mm, "end": v(114.5, -102.43) * mm});
            skLineSegment(sketch, "E11.152.7", {"start": v(113.26, -101.98) * mm, "end": v(112.3, -101.13) * mm});
            skLineSegment(sketch, "E11.153.0", {"start": v(117.17, -97.45) * mm, "end": v(116.2, -96.63) * mm});
            skArc(sketch, "E11.153.1", {"start": v(117.17, -97.45) * mm, "mid": v(117.49, -98.03) * mm, "end": v(117.79, -98.6) * mm});
            skArc(sketch, "E11.153.2", {"start": v(117.78, -98.7) * mm, "mid": v(117.8, -98.66) * mm, "end": v(117.79, -98.6) * mm});
            skLineSegment(sketch, "E11.153.3", {"start": v(117.78, -98.7) * mm, "end": v(117.5, -99.03) * mm});
            skLineSegment(sketch, "E11.153.4", {"start": v(117.22, -99.37) * mm, "end": v(117.5, -99.03) * mm});
            skArc(sketch, "E11.153.5", {"start": v(117.14, -99.4) * mm, "mid": v(117.18, -99.4) * mm, "end": v(117.22, -99.37) * mm});
            skArc(sketch, "E11.153.6", {"start": v(115.89, -98.98) * mm, "mid": v(116.51, -99.19) * mm, "end": v(117.14, -99.4) * mm});
            skLineSegment(sketch, "E11.153.7", {"start": v(115.89, -98.98) * mm, "end": v(114.91, -98.16) * mm});
            skLineSegment(sketch, "E11.154.0", {"start": v(119.68, -94.35) * mm, "end": v(118.7, -93.56) * mm});
            skArc(sketch, "E11.154.1", {"start": v(119.68, -94.35) * mm, "mid": v(120.01, -94.92) * mm, "end": v(120.33, -95.5) * mm});
            skArc(sketch, "E11.154.2", {"start": v(120.32, -95.59) * mm, "mid": v(120.34, -95.54) * mm, "end": v(120.33, -95.5) * mm});
            skLineSegment(sketch, "E11.154.3", {"start": v(120.32, -95.59) * mm, "end": v(120.06, -95.92) * mm});
            skLineSegment(sketch, "E11.154.4", {"start": v(119.78, -96.27) * mm, "end": v(120.06, -95.92) * mm});
            skArc(sketch, "E11.154.5", {"start": v(119.7, -96.3) * mm, "mid": v(119.74, -96.3) * mm, "end": v(119.78, -96.27) * mm});
            skArc(sketch, "E11.154.6", {"start": v(118.44, -95.9) * mm, "mid": v(119.07, -96.1) * mm, "end": v(119.7, -96.3) * mm});
            skLineSegment(sketch, "E11.154.7", {"start": v(118.44, -95.9) * mm, "end": v(117.44, -95.12) * mm});
            skLineSegment(sketch, "E11.155.0", {"start": v(122.11, -91.18) * mm, "end": v(121.1, -90.42) * mm});
            skArc(sketch, "E11.155.1", {"start": v(122.11, -91.18) * mm, "mid": v(122.45, -91.74) * mm, "end": v(122.79, -92.3) * mm});
            skArc(sketch, "E11.155.2", {"start": v(122.78, -92.4) * mm, "mid": v(122.8, -92.36) * mm, "end": v(122.79, -92.3) * mm});
            skLineSegment(sketch, "E11.155.3", {"start": v(122.78, -92.4) * mm, "end": v(122.52, -92.75) * mm});
            skLineSegment(sketch, "E11.155.4", {"start": v(122.26, -93.1) * mm, "end": v(122.52, -92.75) * mm});
            skArc(sketch, "E11.155.5", {"start": v(122.18, -93.13) * mm, "mid": v(122.22, -93.12) * mm, "end": v(122.26, -93.1) * mm});
            skArc(sketch, "E11.155.6", {"start": v(120.9, -92.78) * mm, "mid": v(121.54, -92.96) * mm, "end": v(122.18, -93.13) * mm});
            skLineSegment(sketch, "E11.155.7", {"start": v(120.9, -92.78) * mm, "end": v(119.9, -92) * mm});
            skLineSegment(sketch, "E11.156.0", {"start": v(124.46, -87.96) * mm, "end": v(123.42, -87.22) * mm});
            skArc(sketch, "E11.156.1", {"start": v(124.46, -87.96) * mm, "mid": v(124.81, -88.5) * mm, "end": v(125.16, -89.06) * mm});
            skArc(sketch, "E11.156.2", {"start": v(125.16, -89.16) * mm, "mid": v(125.18, -89.11) * mm, "end": v(125.16, -89.06) * mm});
            skLineSegment(sketch, "E11.156.3", {"start": v(125.16, -89.16) * mm, "end": v(124.91, -89.5) * mm});
            skLineSegment(sketch, "E11.156.4", {"start": v(124.65, -89.87) * mm, "end": v(124.91, -89.5) * mm});
            skArc(sketch, "E11.156.5", {"start": v(124.58, -89.9) * mm, "mid": v(124.62, -89.9) * mm, "end": v(124.65, -89.87) * mm});
            skArc(sketch, "E11.156.6", {"start": v(123.3, -89.58) * mm, "mid": v(123.94, -89.74) * mm, "end": v(124.58, -89.9) * mm});
            skLineSegment(sketch, "E11.156.7", {"start": v(123.3, -89.58) * mm, "end": v(122.26, -88.84) * mm});
            skLineSegment(sketch, "E11.157.0", {"start": v(126.72, -84.67) * mm, "end": v(125.66, -83.96) * mm});
            skArc(sketch, "E11.157.1", {"start": v(126.72, -84.67) * mm, "mid": v(127.09, -85.2) * mm, "end": v(127.45, -85.75) * mm});
            skArc(sketch, "E11.157.2", {"start": v(127.45, -85.85) * mm, "mid": v(127.47, -85.8) * mm, "end": v(127.45, -85.75) * mm});
            skLineSegment(sketch, "E11.157.3", {"start": v(127.45, -85.85) * mm, "end": v(127.21, -86.2) * mm});
            skLineSegment(sketch, "E11.157.4", {"start": v(126.96, -86.57) * mm, "end": v(127.21, -86.2) * mm});
            skArc(sketch, "E11.157.5", {"start": v(126.89, -86.6) * mm, "mid": v(126.93, -86.6) * mm, "end": v(126.96, -86.57) * mm});
            skArc(sketch, "E11.157.6", {"start": v(125.6, -86.32) * mm, "mid": v(126.24, -86.47) * mm, "end": v(126.89, -86.6) * mm});
            skLineSegment(sketch, "E11.157.7", {"start": v(125.6, -86.32) * mm, "end": v(124.55, -85.6) * mm});
            skLineSegment(sketch, "E11.158.0", {"start": v(128.89, -81.32) * mm, "end": v(127.82, -80.64) * mm});
            skArc(sketch, "E11.158.1", {"start": v(128.89, -81.32) * mm, "mid": v(129.28, -81.85) * mm, "end": v(129.65, -82.39) * mm});
            skArc(sketch, "E11.158.2", {"start": v(129.65, -82.49) * mm, "mid": v(129.67, -82.44) * mm, "end": v(129.65, -82.39) * mm});
            skLineSegment(sketch, "E11.158.3", {"start": v(129.65, -82.49) * mm, "end": v(129.42, -82.85) * mm});
            skLineSegment(sketch, "E11.158.4", {"start": v(129.19, -83.22) * mm, "end": v(129.42, -82.85) * mm});
            skArc(sketch, "E11.158.5", {"start": v(129.11, -83.25) * mm, "mid": v(129.15, -83.25) * mm, "end": v(129.19, -83.22) * mm});
            skArc(sketch, "E11.158.6", {"start": v(127.81, -83) * mm, "mid": v(128.46, -83.13) * mm, "end": v(129.11, -83.25) * mm});
            skLineSegment(sketch, "E11.158.7", {"start": v(127.81, -83) * mm, "end": v(126.74, -82.32) * mm});
            skLineSegment(sketch, "E11.159.0", {"start": v(130.97, -77.92) * mm, "end": v(129.89, -77.26) * mm});
            skArc(sketch, "E11.159.1", {"start": v(130.97, -77.92) * mm, "mid": v(131.37, -78.44) * mm, "end": v(131.77, -78.97) * mm});
            skArc(sketch, "E11.159.2", {"start": v(131.77, -79.06) * mm, "mid": v(131.78, -79.02) * mm, "end": v(131.77, -78.97) * mm});
            skLineSegment(sketch, "E11.159.3", {"start": v(131.77, -79.06) * mm, "end": v(131.55, -79.43) * mm});
            skLineSegment(sketch, "E11.159.4", {"start": v(131.32, -79.81) * mm, "end": v(131.55, -79.43) * mm});
            skArc(sketch, "E11.159.5", {"start": v(131.25, -79.84) * mm, "mid": v(131.29, -79.84) * mm, "end": v(131.32, -79.81) * mm});
            skArc(sketch, "E11.159.6", {"start": v(129.94, -79.63) * mm, "mid": v(130.6, -79.74) * mm, "end": v(131.25, -79.84) * mm});
            skLineSegment(sketch, "E11.159.7", {"start": v(129.94, -79.63) * mm, "end": v(128.86, -78.97) * mm});
            skLineSegment(sketch, "E11.160.0", {"start": v(132.97, -74.47) * mm, "end": v(131.86, -73.84) * mm});
            skArc(sketch, "E11.160.1", {"start": v(132.97, -74.47) * mm, "mid": v(133.38, -74.97) * mm, "end": v(133.79, -75.5) * mm});
            skArc(sketch, "E11.160.2", {"start": v(133.8, -75.59) * mm, "mid": v(133.8, -75.54) * mm, "end": v(133.79, -75.5) * mm});
            skLineSegment(sketch, "E11.160.3", {"start": v(133.8, -75.59) * mm, "end": v(133.58, -75.96) * mm});
            skLineSegment(sketch, "E11.160.4", {"start": v(133.36, -76.35) * mm, "end": v(133.58, -75.96) * mm});
            skArc(sketch, "E11.160.5", {"start": v(133.3, -76.38) * mm, "mid": v(133.33, -76.37) * mm, "end": v(133.36, -76.35) * mm});
            skArc(sketch, "E11.160.6", {"start": v(131.98, -76.2) * mm, "mid": v(132.64, -76.3) * mm, "end": v(133.3, -76.38) * mm});
            skLineSegment(sketch, "E11.160.7", {"start": v(131.98, -76.2) * mm, "end": v(130.88, -75.57) * mm});
            skLineSegment(sketch, "E11.161.0", {"start": v(134.87, -70.96) * mm, "end": v(133.75, -70.36) * mm});
            skArc(sketch, "E11.161.1", {"start": v(134.87, -70.96) * mm, "mid": v(135.3, -71.46) * mm, "end": v(135.72, -71.96) * mm});
            skArc(sketch, "E11.161.2", {"start": v(135.73, -72.06) * mm, "mid": v(135.74, -72) * mm, "end": v(135.72, -71.96) * mm});
            skLineSegment(sketch, "E11.161.3", {"start": v(135.73, -72.06) * mm, "end": v(135.53, -72.44) * mm});
            skLineSegment(sketch, "E11.161.4", {"start": v(135.32, -72.83) * mm, "end": v(135.53, -72.44) * mm});
            skArc(sketch, "E11.161.5", {"start": v(135.25, -72.87) * mm, "mid": v(135.29, -72.86) * mm, "end": v(135.32, -72.83) * mm});
            skArc(sketch, "E11.161.6", {"start": v(133.93, -72.72) * mm, "mid": v(134.59, -72.8) * mm, "end": v(135.25, -72.87) * mm});
            skLineSegment(sketch, "E11.161.7", {"start": v(133.93, -72.72) * mm, "end": v(132.81, -72.12) * mm});
            skLineSegment(sketch, "E11.162.0", {"start": v(136.68, -67.4) * mm, "end": v(135.55, -66.84) * mm});
            skArc(sketch, "E11.162.1", {"start": v(136.68, -67.4) * mm, "mid": v(137.12, -67.9) * mm, "end": v(137.55, -68.39) * mm});
            skArc(sketch, "E11.162.2", {"start": v(137.57, -68.48) * mm, "mid": v(137.58, -68.43) * mm, "end": v(137.55, -68.39) * mm});
            skLineSegment(sketch, "E11.162.3", {"start": v(137.57, -68.48) * mm, "end": v(137.38, -68.87) * mm});
            skLineSegment(sketch, "E11.162.4", {"start": v(137.18, -69.26) * mm, "end": v(137.38, -68.87) * mm});
            skArc(sketch, "E11.162.5", {"start": v(137.1, -69.3) * mm, "mid": v(137.15, -69.3) * mm, "end": v(137.18, -69.26) * mm});
            skArc(sketch, "E11.162.6", {"start": v(135.79, -69.19) * mm, "mid": v(136.45, -69.25) * mm, "end": v(137.1, -69.3) * mm});
            skLineSegment(sketch, "E11.162.7", {"start": v(135.79, -69.19) * mm, "end": v(134.65, -68.62) * mm});
            skLineSegment(sketch, "E11.163.0", {"start": v(138.4, -63.8) * mm, "end": v(137.25, -63.26) * mm});
            skArc(sketch, "E11.163.1", {"start": v(138.4, -63.8) * mm, "mid": v(138.85, -64.28) * mm, "end": v(139.3, -64.76) * mm});
            skArc(sketch, "E11.163.2", {"start": v(139.31, -64.86) * mm, "mid": v(139.32, -64.8) * mm, "end": v(139.3, -64.76) * mm});
            skLineSegment(sketch, "E11.163.3", {"start": v(139.31, -64.86) * mm, "end": v(139.13, -65.25) * mm});
            skLineSegment(sketch, "E11.163.4", {"start": v(138.94, -65.65) * mm, "end": v(139.13, -65.25) * mm});
            skArc(sketch, "E11.163.5", {"start": v(138.87, -65.69) * mm, "mid": v(138.91, -65.68) * mm, "end": v(138.94, -65.65) * mm});
            skArc(sketch, "E11.163.6", {"start": v(137.55, -65.6) * mm, "mid": v(138.21, -65.65) * mm, "end": v(138.87, -65.69) * mm});
            skLineSegment(sketch, "E11.163.7", {"start": v(137.55, -65.6) * mm, "end": v(136.4, -65.07) * mm});
            skLineSegment(sketch, "E11.164.0", {"start": v(140.02, -60.16) * mm, "end": v(138.86, -59.65) * mm});
            skArc(sketch, "E11.164.1", {"start": v(140.02, -60.16) * mm, "mid": v(140.49, -60.62) * mm, "end": v(140.95, -61.1) * mm});
            skArc(sketch, "E11.164.2", {"start": v(140.96, -61.19) * mm, "mid": v(140.97, -61.14) * mm, "end": v(140.95, -61.1) * mm});
            skLineSegment(sketch, "E11.164.3", {"start": v(140.96, -61.19) * mm, "end": v(140.8, -61.58) * mm});
            skLineSegment(sketch, "E11.164.4", {"start": v(140.61, -61.99) * mm, "end": v(140.8, -61.58) * mm});
            skArc(sketch, "E11.164.5", {"start": v(140.55, -62.03) * mm, "mid": v(140.59, -62.02) * mm, "end": v(140.61, -61.99) * mm});
            skArc(sketch, "E11.164.6", {"start": v(139.22, -61.99) * mm, "mid": v(139.89, -62.01) * mm, "end": v(140.55, -62.03) * mm});
            skLineSegment(sketch, "E11.164.7", {"start": v(139.22, -61.99) * mm, "end": v(138.06, -61.48) * mm});
            skLineSegment(sketch, "E11.165.0", {"start": v(141.55, -56.47) * mm, "end": v(140.37, -56) * mm});
            skArc(sketch, "E11.165.1", {"start": v(141.55, -56.47) * mm, "mid": v(142.03, -56.92) * mm, "end": v(142.5, -57.38) * mm});
            skArc(sketch, "E11.165.2", {"start": v(142.52, -57.48) * mm, "mid": v(142.52, -57.43) * mm, "end": v(142.5, -57.38) * mm});
            skLineSegment(sketch, "E11.165.3", {"start": v(142.52, -57.48) * mm, "end": v(142.36, -57.88) * mm});
            skLineSegment(sketch, "E11.165.4", {"start": v(142.19, -58.29) * mm, "end": v(142.36, -57.88) * mm});
            skArc(sketch, "E11.165.5", {"start": v(142.12, -58.33) * mm, "mid": v(142.16, -58.32) * mm, "end": v(142.19, -58.29) * mm});
            skArc(sketch, "E11.165.6", {"start": v(140.8, -58.32) * mm, "mid": v(141.46, -58.33) * mm, "end": v(142.12, -58.33) * mm});
            skLineSegment(sketch, "E11.165.7", {"start": v(140.8, -58.32) * mm, "end": v(139.62, -57.84) * mm});
            skLineSegment(sketch, "E11.166.0", {"start": v(142.98, -52.75) * mm, "end": v(141.8, -52.3) * mm});
            skArc(sketch, "E11.166.1", {"start": v(142.98, -52.75) * mm, "mid": v(143.47, -53.19) * mm, "end": v(143.95, -53.63) * mm});
            skArc(sketch, "E11.166.2", {"start": v(143.97, -53.73) * mm, "mid": v(143.97, -53.68) * mm, "end": v(143.95, -53.63) * mm});
            skLineSegment(sketch, "E11.166.3", {"start": v(143.97, -53.73) * mm, "end": v(143.82, -54.13) * mm});
            skLineSegment(sketch, "E11.166.4", {"start": v(143.66, -54.54) * mm, "end": v(143.82, -54.13) * mm});
            skArc(sketch, "E11.166.5", {"start": v(143.6, -54.59) * mm, "mid": v(143.64, -54.58) * mm, "end": v(143.66, -54.54) * mm});
            skArc(sketch, "E11.166.6", {"start": v(142.28, -54.62) * mm, "mid": v(142.94, -54.6) * mm, "end": v(143.6, -54.59) * mm});
            skLineSegment(sketch, "E11.166.7", {"start": v(142.28, -54.62) * mm, "end": v(141.09, -54.17) * mm});
            skLineSegment(sketch, "E11.167.0", {"start": v(144.31, -48.99) * mm, "end": v(143.11, -48.57) * mm});
            skArc(sketch, "E11.167.1", {"start": v(144.31, -48.99) * mm, "mid": v(144.81, -49.41) * mm, "end": v(145.3, -49.85) * mm});
            skArc(sketch, "E11.167.2", {"start": v(145.33, -49.94) * mm, "mid": v(145.33, -49.89) * mm, "end": v(145.3, -49.85) * mm});
            skLineSegment(sketch, "E11.167.3", {"start": v(145.33, -49.94) * mm, "end": v(145.19, -50.35) * mm});
            skLineSegment(sketch, "E11.167.4", {"start": v(145.04, -50.76) * mm, "end": v(145.19, -50.35) * mm});
            skArc(sketch, "E11.167.5", {"start": v(144.98, -50.81) * mm, "mid": v(145.02, -50.8) * mm, "end": v(145.04, -50.76) * mm});
            skArc(sketch, "E11.167.6", {"start": v(143.66, -50.87) * mm, "mid": v(144.32, -50.85) * mm, "end": v(144.98, -50.81) * mm});
            skLineSegment(sketch, "E11.167.7", {"start": v(143.66, -50.87) * mm, "end": v(142.46, -50.46) * mm});
            skLineSegment(sketch, "E11.168.0", {"start": v(145.55, -45.2) * mm, "end": v(144.33, -44.8) * mm});
            skArc(sketch, "E11.168.1", {"start": v(145.55, -45.2) * mm, "mid": v(146.06, -45.6) * mm, "end": v(146.56, -46.02) * mm});
            skArc(sketch, "E11.168.2", {"start": v(146.59, -46.12) * mm, "mid": v(146.59, -46.07) * mm, "end": v(146.56, -46.02) * mm});
            skLineSegment(sketch, "E11.168.3", {"start": v(146.59, -46.12) * mm, "end": v(146.46, -46.53) * mm});
            skLineSegment(sketch, "E11.168.4", {"start": v(146.32, -46.95) * mm, "end": v(146.46, -46.53) * mm});
            skArc(sketch, "E11.168.5", {"start": v(146.26, -47) * mm, "mid": v(146.3, -46.98) * mm, "end": v(146.32, -46.95) * mm});
            skArc(sketch, "E11.168.6", {"start": v(144.94, -47.1) * mm, "mid": v(145.6, -47.05) * mm, "end": v(146.26, -47) * mm});
            skLineSegment(sketch, "E11.168.7", {"start": v(144.94, -47.1) * mm, "end": v(143.73, -46.7) * mm});
            skLineSegment(sketch, "E11.169.0", {"start": v(146.68, -41.37) * mm, "end": v(145.46, -41.01) * mm});
            skArc(sketch, "E11.169.1", {"start": v(146.68, -41.37) * mm, "mid": v(147.2, -41.77) * mm, "end": v(147.71, -42.17) * mm});
            skArc(sketch, "E11.169.2", {"start": v(147.74, -42.27) * mm, "mid": v(147.74, -42.21) * mm, "end": v(147.71, -42.17) * mm});
            skLineSegment(sketch, "E11.169.3", {"start": v(147.74, -42.27) * mm, "end": v(147.63, -42.68) * mm});
            skLineSegment(sketch, "E11.169.4", {"start": v(147.5, -43.1) * mm, "end": v(147.63, -42.68) * mm});
            skArc(sketch, "E11.169.5", {"start": v(147.44, -43.15) * mm, "mid": v(147.48, -43.14) * mm, "end": v(147.5, -43.1) * mm});
            skArc(sketch, "E11.169.6", {"start": v(146.12, -43.28) * mm, "mid": v(146.78, -43.22) * mm, "end": v(147.44, -43.15) * mm});
            skLineSegment(sketch, "E11.169.7", {"start": v(146.12, -43.28) * mm, "end": v(144.9, -42.93) * mm});
            skLineSegment(sketch, "E11.170.0", {"start": v(147.71, -37.51) * mm, "end": v(146.48, -37.2) * mm});
            skArc(sketch, "E11.170.1", {"start": v(147.71, -37.51) * mm, "mid": v(148.24, -37.9) * mm, "end": v(148.77, -38.3) * mm});
            skArc(sketch, "E11.170.2", {"start": v(148.8, -38.38) * mm, "mid": v(148.8, -38.33) * mm, "end": v(148.77, -38.3) * mm});
            skLineSegment(sketch, "E11.170.3", {"start": v(148.8, -38.38) * mm, "end": v(148.7, -38.8) * mm});
            skLineSegment(sketch, "E11.170.4", {"start": v(148.58, -39.23) * mm, "end": v(148.7, -38.8) * mm});
            skArc(sketch, "E11.170.5", {"start": v(148.52, -39.28) * mm, "mid": v(148.56, -39.26) * mm, "end": v(148.58, -39.23) * mm});
            skArc(sketch, "E11.170.6", {"start": v(147.2, -39.44) * mm, "mid": v(147.86, -39.37) * mm, "end": v(148.52, -39.28) * mm});
            skLineSegment(sketch, "E11.170.7", {"start": v(147.2, -39.44) * mm, "end": v(145.98, -39.12) * mm});
            skLineSegment(sketch, "E11.171.0", {"start": v(148.64, -33.63) * mm, "end": v(147.4, -33.35) * mm});
            skArc(sketch, "E11.171.1", {"start": v(148.64, -33.63) * mm, "mid": v(149.18, -34) * mm, "end": v(149.72, -34.38) * mm});
            skArc(sketch, "E11.171.2", {"start": v(149.75, -34.48) * mm, "mid": v(149.75, -34.42) * mm, "end": v(149.72, -34.38) * mm});
            skLineSegment(sketch, "E11.171.3", {"start": v(149.75, -34.48) * mm, "end": v(149.66, -34.9) * mm});
            skLineSegment(sketch, "E11.171.4", {"start": v(149.55, -35.32) * mm, "end": v(149.66, -34.9) * mm});
            skArc(sketch, "E11.171.5", {"start": v(149.5, -35.38) * mm, "mid": v(149.53, -35.36) * mm, "end": v(149.55, -35.32) * mm});
            skArc(sketch, "E11.171.6", {"start": v(148.19, -35.58) * mm, "mid": v(148.84, -35.48) * mm, "end": v(149.5, -35.38) * mm});
            skLineSegment(sketch, "E11.171.7", {"start": v(148.19, -35.58) * mm, "end": v(146.95, -35.29) * mm});
            skLineSegment(sketch, "E11.172.0", {"start": v(149.47, -29.73) * mm, "end": v(148.23, -29.48) * mm});
            skArc(sketch, "E11.172.1", {"start": v(149.47, -29.73) * mm, "mid": v(150.02, -30.09) * mm, "end": v(150.57, -30.45) * mm});
            skArc(sketch, "E11.172.2", {"start": v(150.6, -30.54) * mm, "mid": v(150.6, -30.5) * mm, "end": v(150.57, -30.45) * mm});
            skLineSegment(sketch, "E11.172.3", {"start": v(150.6, -30.54) * mm, "end": v(150.52, -30.97) * mm});
            skLineSegment(sketch, "E11.172.4", {"start": v(150.43, -31.4) * mm, "end": v(150.52, -30.97) * mm});
            skArc(sketch, "E11.172.5", {"start": v(150.37, -31.45) * mm, "mid": v(150.4, -31.43) * mm, "end": v(150.43, -31.4) * mm});
            skArc(sketch, "E11.172.6", {"start": v(149.07, -31.69) * mm, "mid": v(149.72, -31.58) * mm, "end": v(150.37, -31.45) * mm});
            skLineSegment(sketch, "E11.172.7", {"start": v(149.07, -31.69) * mm, "end": v(147.83, -31.43) * mm});
            skLineSegment(sketch, "E11.173.0", {"start": v(150.2, -25.8) * mm, "end": v(148.95, -25.59) * mm});
            skArc(sketch, "E11.173.1", {"start": v(150.2, -25.8) * mm, "mid": v(150.76, -26.15) * mm, "end": v(151.31, -26.5) * mm});
            skArc(sketch, "E11.173.2", {"start": v(151.35, -26.6) * mm, "mid": v(151.35, -26.54) * mm, "end": v(151.31, -26.5) * mm});
            skLineSegment(sketch, "E11.173.3", {"start": v(151.35, -26.6) * mm, "end": v(151.28, -27.01) * mm});
            skLineSegment(sketch, "E11.173.4", {"start": v(151.2, -27.45) * mm, "end": v(151.28, -27.01) * mm});
            skArc(sketch, "E11.173.5", {"start": v(151.14, -27.5) * mm, "mid": v(151.18, -27.49) * mm, "end": v(151.2, -27.45) * mm});
            skArc(sketch, "E11.173.6", {"start": v(149.85, -27.77) * mm, "mid": v(150.5, -27.64) * mm, "end": v(151.14, -27.5) * mm});
            skLineSegment(sketch, "E11.173.7", {"start": v(149.85, -27.77) * mm, "end": v(148.6, -27.55) * mm});
            skLineSegment(sketch, "E11.174.0", {"start": v(150.82, -21.87) * mm, "end": v(149.57, -21.68) * mm});
            skArc(sketch, "E11.174.1", {"start": v(150.82, -21.87) * mm, "mid": v(151.4, -22.2) * mm, "end": v(151.95, -22.53) * mm});
            skArc(sketch, "E11.174.2", {"start": v(152, -22.62) * mm, "mid": v(151.99, -22.57) * mm, "end": v(151.95, -22.53) * mm});
            skLineSegment(sketch, "E11.174.3", {"start": v(152, -22.62) * mm, "end": v(151.93, -23.05) * mm});
            skLineSegment(sketch, "E11.174.4", {"start": v(151.87, -23.48) * mm, "end": v(151.93, -23.05) * mm});
            skArc(sketch, "E11.174.5", {"start": v(151.81, -23.54) * mm, "mid": v(151.85, -23.52) * mm, "end": v(151.87, -23.48) * mm});
            skArc(sketch, "E11.174.6", {"start": v(150.52, -23.84) * mm, "mid": v(151.17, -23.7) * mm, "end": v(151.81, -23.54) * mm});
            skLineSegment(sketch, "E11.174.7", {"start": v(150.52, -23.84) * mm, "end": v(149.27, -23.65) * mm});
            skLineSegment(sketch, "E11.175.0", {"start": v(151.34, -17.91) * mm, "end": v(150.08, -17.76) * mm});
            skArc(sketch, "E11.175.1", {"start": v(151.34, -17.91) * mm, "mid": v(151.92, -18.22) * mm, "end": v(152.5, -18.55) * mm});
            skArc(sketch, "E11.175.2", {"start": v(152.54, -18.63) * mm, "mid": v(152.53, -18.58) * mm, "end": v(152.5, -18.55) * mm});
            skLineSegment(sketch, "E11.175.3", {"start": v(152.54, -18.63) * mm, "end": v(152.48, -19.06) * mm});
            skLineSegment(sketch, "E11.175.4", {"start": v(152.43, -19.5) * mm, "end": v(152.48, -19.06) * mm});
            skArc(sketch, "E11.175.5", {"start": v(152.38, -19.56) * mm, "mid": v(152.41, -19.54) * mm, "end": v(152.43, -19.5) * mm});
            skArc(sketch, "E11.175.6", {"start": v(151.1, -19.9) * mm, "mid": v(151.74, -19.73) * mm, "end": v(152.38, -19.56) * mm});
            skLineSegment(sketch, "E11.175.7", {"start": v(151.1, -19.9) * mm, "end": v(149.84, -19.73) * mm});
            skLineSegment(sketch, "E11.176.0", {"start": v(151.76, -13.94) * mm, "end": v(150.5, -13.82) * mm});
            skArc(sketch, "E11.176.1", {"start": v(151.76, -13.94) * mm, "mid": v(152.35, -14.24) * mm, "end": v(152.93, -14.55) * mm});
            skArc(sketch, "E11.176.2", {"start": v(152.97, -14.63) * mm, "mid": v(152.96, -14.58) * mm, "end": v(152.93, -14.55) * mm});
            skLineSegment(sketch, "E11.176.3", {"start": v(152.97, -14.63) * mm, "end": v(152.93, -15.06) * mm});
            skLineSegment(sketch, "E11.176.4", {"start": v(152.89, -15.5) * mm, "end": v(152.93, -15.06) * mm});
            skArc(sketch, "E11.176.5", {"start": v(152.84, -15.56) * mm, "mid": v(152.87, -15.54) * mm, "end": v(152.89, -15.5) * mm});
            skArc(sketch, "E11.176.6", {"start": v(151.57, -15.93) * mm, "mid": v(152.2, -15.75) * mm, "end": v(152.84, -15.56) * mm});
            skLineSegment(sketch, "E11.176.7", {"start": v(151.57, -15.93) * mm, "end": v(150.3, -15.8) * mm});
            skLineSegment(sketch, "E11.177.0", {"start": v(152.07, -9.97) * mm, "end": v(150.8, -9.88) * mm});
            skArc(sketch, "E11.177.1", {"start": v(152.07, -9.97) * mm, "mid": v(152.67, -10.25) * mm, "end": v(153.25, -10.54) * mm});
            skArc(sketch, "E11.177.2", {"start": v(153.3, -10.62) * mm, "mid": v(153.3, -10.58) * mm, "end": v(153.25, -10.54) * mm});
            skLineSegment(sketch, "E11.177.3", {"start": v(153.3, -10.62) * mm, "end": v(153.27, -11.05) * mm});
            skLineSegment(sketch, "E11.177.4", {"start": v(153.24, -11.5) * mm, "end": v(153.27, -11.05) * mm});
            skArc(sketch, "E11.177.5", {"start": v(153.2, -11.56) * mm, "mid": v(153.22, -11.53) * mm, "end": v(153.24, -11.5) * mm});
            skArc(sketch, "E11.177.6", {"start": v(151.93, -11.96) * mm, "mid": v(152.56, -11.76) * mm, "end": v(153.2, -11.56) * mm});
            skLineSegment(sketch, "E11.177.7", {"start": v(151.93, -11.96) * mm, "end": v(150.66, -11.87) * mm});
            skLineSegment(sketch, "E11.178.0", {"start": v(152.28, -5.98) * mm, "end": v(151.01, -5.93) * mm});
            skArc(sketch, "E11.178.1", {"start": v(152.28, -5.98) * mm, "mid": v(152.88, -6.25) * mm, "end": v(153.48, -6.52) * mm});
            skArc(sketch, "E11.178.2", {"start": v(153.53, -6.6) * mm, "mid": v(153.52, -6.56) * mm, "end": v(153.48, -6.52) * mm});
            skLineSegment(sketch, "E11.178.3", {"start": v(153.53, -6.6) * mm, "end": v(153.5, -7.04) * mm});
            skLineSegment(sketch, "E11.178.4", {"start": v(153.49, -7.48) * mm, "end": v(153.5, -7.04) * mm});
            skArc(sketch, "E11.178.5", {"start": v(153.44, -7.54) * mm, "mid": v(153.47, -7.52) * mm, "end": v(153.49, -7.48) * mm});
            skArc(sketch, "E11.178.6", {"start": v(152.2, -7.98) * mm, "mid": v(152.82, -7.76) * mm, "end": v(153.44, -7.54) * mm});
            skLineSegment(sketch, "E11.178.7", {"start": v(152.2, -7.98) * mm, "end": v(150.92, -7.92) * mm});
            skLineSegment(sketch, "E11.179.0", {"start": v(152.39, -2) * mm, "end": v(151.12, -1.97) * mm});
            skArc(sketch, "E11.179.1", {"start": v(152.39, -2) * mm, "mid": v(153, -2.24) * mm, "end": v(153.6, -2.5) * mm});
            skArc(sketch, "E11.179.2", {"start": v(153.65, -2.59) * mm, "mid": v(153.63, -2.54) * mm, "end": v(153.6, -2.5) * mm});
            skLineSegment(sketch, "E11.179.3", {"start": v(153.65, -2.59) * mm, "end": v(153.64, -3.02) * mm});
            skLineSegment(sketch, "E11.179.4", {"start": v(153.63, -3.46) * mm, "end": v(153.64, -3.02) * mm});
            skArc(sketch, "E11.179.5", {"start": v(153.59, -3.52) * mm, "mid": v(153.62, -3.5) * mm, "end": v(153.63, -3.46) * mm});
            skArc(sketch, "E11.179.6", {"start": v(152.35, -3.99) * mm, "mid": v(152.97, -3.76) * mm, "end": v(153.59, -3.52) * mm});
            skLineSegment(sketch, "E11.179.7", {"start": v(152.35, -3.99) * mm, "end": v(151.08, -3.96) * mm});
            skLineSegment(sketch, "E11.180.0", {"start": v(152.39, 2) * mm, "end": v(151.12, 1.99) * mm});
            skArc(sketch, "E11.180.1", {"start": v(152.39, 2) * mm, "mid": v(153, 1.76) * mm, "end": v(153.6, 1.52) * mm});
            skArc(sketch, "E11.180.2", {"start": v(153.66, 1.44) * mm, "mid": v(153.65, 1.48) * mm, "end": v(153.6, 1.52) * mm});
            skLineSegment(sketch, "E11.180.3", {"start": v(153.66, 1.44) * mm, "end": v(153.67, 1) * mm});
            skLineSegment(sketch, "E11.180.4", {"start": v(153.67, 0.56) * mm, "end": v(153.67, 1) * mm});
            skArc(sketch, "E11.180.5", {"start": v(153.63, 0.5) * mm, "mid": v(153.66, 0.52) * mm, "end": v(153.67, 0.56) * mm});
            skArc(sketch, "E11.180.6", {"start": v(152.4, 0) * mm, "mid": v(153.01, 0.24) * mm, "end": v(153.63, 0.5) * mm});
            skLineSegment(sketch, "E11.180.7", {"start": v(152.4, 0) * mm, "end": v(151.13, 0) * mm});
            skLineSegment(sketch, "E11.181.0", {"start": v(152.28, 5.98) * mm, "end": v(151.01, 5.94) * mm});
            skArc(sketch, "E11.181.1", {"start": v(152.28, 5.98) * mm, "mid": v(152.9, 5.77) * mm, "end": v(153.52, 5.54) * mm});
            skArc(sketch, "E11.181.2", {"start": v(153.57, 5.46) * mm, "mid": v(153.56, 5.5) * mm, "end": v(153.52, 5.54) * mm});
            skLineSegment(sketch, "E11.181.3", {"start": v(153.57, 5.46) * mm, "end": v(153.59, 5.03) * mm});
            skLineSegment(sketch, "E11.181.4", {"start": v(153.6, 4.59) * mm, "end": v(153.59, 5.03) * mm});
            skArc(sketch, "E11.181.5", {"start": v(153.56, 4.52) * mm, "mid": v(153.6, 4.55) * mm, "end": v(153.6, 4.59) * mm});
            skArc(sketch, "E11.181.6", {"start": v(152.35, 3.99) * mm, "mid": v(152.96, 4.25) * mm, "end": v(153.56, 4.52) * mm});
            skLineSegment(sketch, "E11.181.7", {"start": v(152.35, 3.99) * mm, "end": v(151.08, 3.95) * mm});
            skLineSegment(sketch, "E11.182.0", {"start": v(152.07, 9.97) * mm, "end": v(150.8, 9.9) * mm});
            skArc(sketch, "E11.182.1", {"start": v(152.07, 9.97) * mm, "mid": v(152.7, 9.77) * mm, "end": v(153.32, 9.55) * mm});
            skArc(sketch, "E11.182.2", {"start": v(153.38, 9.48) * mm, "mid": v(153.36, 9.52) * mm, "end": v(153.32, 9.55) * mm});
            skLineSegment(sketch, "E11.182.3", {"start": v(153.38, 9.48) * mm, "end": v(153.4, 9.05) * mm});
            skLineSegment(sketch, "E11.182.4", {"start": v(153.43, 8.6) * mm, "end": v(153.4, 9.05) * mm});
            skArc(sketch, "E11.182.5", {"start": v(153.39, 8.54) * mm, "mid": v(153.42, 8.57) * mm, "end": v(153.43, 8.6) * mm});
            skArc(sketch, "E11.182.6", {"start": v(152.2, 7.98) * mm, "mid": v(152.8, 8.25) * mm, "end": v(153.39, 8.54) * mm});
            skLineSegment(sketch, "E11.182.7", {"start": v(152.2, 7.98) * mm, "end": v(150.92, 7.9) * mm});
            skLineSegment(sketch, "E11.183.0", {"start": v(151.76, 13.94) * mm, "end": v(150.5, 13.84) * mm});
            skArc(sketch, "E11.183.1", {"start": v(151.76, 13.94) * mm, "mid": v(152.39, 13.76) * mm, "end": v(153.02, 13.56) * mm});
            skArc(sketch, "E11.183.2", {"start": v(153.08, 13.49) * mm, "mid": v(153.06, 13.54) * mm, "end": v(153.02, 13.56) * mm});
            skLineSegment(sketch, "E11.183.3", {"start": v(153.08, 13.49) * mm, "end": v(153.11, 13.06) * mm});
            skLineSegment(sketch, "E11.183.4", {"start": v(153.15, 12.62) * mm, "end": v(153.11, 13.06) * mm});
            skArc(sketch, "E11.183.5", {"start": v(153.11, 12.55) * mm, "mid": v(153.14, 12.58) * mm, "end": v(153.15, 12.62) * mm});
            skArc(sketch, "E11.183.6", {"start": v(151.93, 11.96) * mm, "mid": v(152.52, 12.25) * mm, "end": v(153.11, 12.55) * mm});
            skLineSegment(sketch, "E11.183.7", {"start": v(151.93, 11.96) * mm, "end": v(150.66, 11.85) * mm});
            skLineSegment(sketch, "E11.184.0", {"start": v(151.34, 17.91) * mm, "end": v(150.08, 17.77) * mm});
            skArc(sketch, "E11.184.1", {"start": v(151.34, 17.91) * mm, "mid": v(151.98, 17.74) * mm, "end": v(152.6, 17.57) * mm});
            skArc(sketch, "E11.184.2", {"start": v(152.67, 17.5) * mm, "mid": v(152.65, 17.54) * mm, "end": v(152.6, 17.57) * mm});
            skLineSegment(sketch, "E11.184.3", {"start": v(152.67, 17.5) * mm, "end": v(152.72, 17.06) * mm});
            skLineSegment(sketch, "E11.184.4", {"start": v(152.77, 16.62) * mm, "end": v(152.72, 17.06) * mm});
            skArc(sketch, "E11.184.5", {"start": v(152.73, 16.55) * mm, "mid": v(152.76, 16.58) * mm, "end": v(152.77, 16.62) * mm});
            skArc(sketch, "E11.184.6", {"start": v(151.57, 15.93) * mm, "mid": v(152.15, 16.24) * mm, "end": v(152.73, 16.55) * mm});
            skLineSegment(sketch, "E11.184.7", {"start": v(151.57, 15.93) * mm, "end": v(150.3, 15.79) * mm});
            skLineSegment(sketch, "E11.185.0", {"start": v(150.82, 21.87) * mm, "end": v(149.56, 21.7) * mm});
            skArc(sketch, "E11.185.1", {"start": v(150.82, 21.87) * mm, "mid": v(151.46, 21.72) * mm, "end": v(152.1, 21.55) * mm});
            skArc(sketch, "E11.185.2", {"start": v(152.16, 21.48) * mm, "mid": v(152.14, 21.53) * mm, "end": v(152.1, 21.55) * mm});
            skLineSegment(sketch, "E11.185.3", {"start": v(152.16, 21.48) * mm, "end": v(152.22, 21.05) * mm});
            skLineSegment(sketch, "E11.185.4", {"start": v(152.28, 20.62) * mm, "end": v(152.22, 21.05) * mm});
            skArc(sketch, "E11.185.5", {"start": v(152.25, 20.55) * mm, "mid": v(152.27, 20.58) * mm, "end": v(152.28, 20.62) * mm});
            skArc(sketch, "E11.185.6", {"start": v(151.1, 19.9) * mm, "mid": v(151.67, 20.21) * mm, "end": v(152.25, 20.55) * mm});
            skLineSegment(sketch, "E11.185.7", {"start": v(151.1, 19.9) * mm, "end": v(149.84, 19.72) * mm});
            skLineSegment(sketch, "E11.186.0", {"start": v(150.2, 25.8) * mm, "end": v(148.95, 25.6) * mm});
            skArc(sketch, "E11.186.1", {"start": v(150.2, 25.8) * mm, "mid": v(150.84, 25.67) * mm, "end": v(151.48, 25.53) * mm});
            skArc(sketch, "E11.186.2", {"start": v(151.55, 25.46) * mm, "mid": v(151.52, 25.5) * mm, "end": v(151.48, 25.53) * mm});
            skLineSegment(sketch, "E11.186.3", {"start": v(151.55, 25.46) * mm, "end": v(151.62, 25.03) * mm});
            skLineSegment(sketch, "E11.186.4", {"start": v(151.69, 24.6) * mm, "end": v(151.62, 25.03) * mm});
            skArc(sketch, "E11.186.5", {"start": v(151.66, 24.52) * mm, "mid": v(151.68, 24.56) * mm, "end": v(151.69, 24.6) * mm});
            skArc(sketch, "E11.186.6", {"start": v(150.52, 23.84) * mm, "mid": v(151.1, 24.18) * mm, "end": v(151.66, 24.52) * mm});
            skLineSegment(sketch, "E11.186.7", {"start": v(150.52, 23.84) * mm, "end": v(149.27, 23.63) * mm});
            skLineSegment(sketch, "E11.187.0", {"start": v(149.47, 29.73) * mm, "end": v(148.22, 29.5) * mm});
            skArc(sketch, "E11.187.1", {"start": v(149.47, 29.73) * mm, "mid": v(150.12, 29.61) * mm, "end": v(150.76, 29.48) * mm});
            skArc(sketch, "E11.187.2", {"start": v(150.83, 29.41) * mm, "mid": v(150.8, 29.46) * mm, "end": v(150.76, 29.48) * mm});
            skLineSegment(sketch, "E11.187.3", {"start": v(150.83, 29.41) * mm, "end": v(150.91, 29) * mm});
            skLineSegment(sketch, "E11.187.4", {"start": v(151, 28.56) * mm, "end": v(150.91, 29) * mm});
            skArc(sketch, "E11.187.5", {"start": v(150.96, 28.49) * mm, "mid": v(150.99, 28.52) * mm, "end": v(151, 28.56) * mm});
            skArc(sketch, "E11.187.6", {"start": v(149.85, 27.77) * mm, "mid": v(150.4, 28.12) * mm, "end": v(150.96, 28.49) * mm});
            skLineSegment(sketch, "E11.187.7", {"start": v(149.85, 27.77) * mm, "end": v(148.6, 27.53) * mm});
            skLineSegment(sketch, "E11.188.0", {"start": v(148.64, 33.63) * mm, "end": v(147.4, 33.36) * mm});
            skArc(sketch, "E11.188.1", {"start": v(148.64, 33.63) * mm, "mid": v(149.3, 33.53) * mm, "end": v(149.94, 33.42) * mm});
            skArc(sketch, "E11.188.2", {"start": v(150, 33.35) * mm, "mid": v(149.98, 33.4) * mm, "end": v(149.94, 33.42) * mm});
            skLineSegment(sketch, "E11.188.3", {"start": v(150, 33.35) * mm, "end": v(150.1, 32.93) * mm});
            skLineSegment(sketch, "E11.188.4", {"start": v(150.2, 32.5) * mm, "end": v(150.1, 32.93) * mm});
            skArc(sketch, "E11.188.5", {"start": v(150.16, 32.43) * mm, "mid": v(150.2, 32.46) * mm, "end": v(150.2, 32.5) * mm});
            skArc(sketch, "E11.188.6", {"start": v(149.07, 31.69) * mm, "mid": v(149.62, 32.05) * mm, "end": v(150.16, 32.43) * mm});
            skLineSegment(sketch, "E11.188.7", {"start": v(149.07, 31.69) * mm, "end": v(147.83, 31.41) * mm});
            skLineSegment(sketch, "E11.189.0", {"start": v(147.71, 37.51) * mm, "end": v(146.48, 37.2) * mm});
            skArc(sketch, "E11.189.1", {"start": v(147.71, 37.51) * mm, "mid": v(148.36, 37.43) * mm, "end": v(149.01, 37.33) * mm});
            skArc(sketch, "E11.189.2", {"start": v(149.08, 37.27) * mm, "mid": v(149.06, 37.31) * mm, "end": v(149.01, 37.33) * mm});
            skLineSegment(sketch, "E11.189.3", {"start": v(149.08, 37.27) * mm, "end": v(149.19, 36.85) * mm});
            skLineSegment(sketch, "E11.189.4", {"start": v(149.3, 36.42) * mm, "end": v(149.19, 36.85) * mm});
            skArc(sketch, "E11.189.5", {"start": v(149.26, 36.35) * mm, "mid": v(149.29, 36.38) * mm, "end": v(149.3, 36.42) * mm});
            skArc(sketch, "E11.189.6", {"start": v(148.19, 35.58) * mm, "mid": v(148.73, 35.96) * mm, "end": v(149.26, 36.35) * mm});
            skLineSegment(sketch, "E11.189.7", {"start": v(148.19, 35.58) * mm, "end": v(146.96, 35.27) * mm});
            skLineSegment(sketch, "E11.190.0", {"start": v(146.68, 41.37) * mm, "end": v(145.45, 41.03) * mm});
            skArc(sketch, "E11.190.1", {"start": v(146.68, 41.37) * mm, "mid": v(147.33, 41.3) * mm, "end": v(147.98, 41.22) * mm});
            skArc(sketch, "E11.190.2", {"start": v(148.06, 41.16) * mm, "mid": v(148.03, 41.2) * mm, "end": v(147.98, 41.22) * mm});
            skLineSegment(sketch, "E11.190.3", {"start": v(148.06, 41.16) * mm, "end": v(148.17, 40.74) * mm});
            skLineSegment(sketch, "E11.190.4", {"start": v(148.29, 40.32) * mm, "end": v(148.17, 40.74) * mm});
            skArc(sketch, "E11.190.5", {"start": v(148.26, 40.24) * mm, "mid": v(148.29, 40.28) * mm, "end": v(148.29, 40.32) * mm});
            skArc(sketch, "E11.190.6", {"start": v(147.2, 39.44) * mm, "mid": v(147.74, 39.84) * mm, "end": v(148.26, 40.24) * mm});
            skLineSegment(sketch, "E11.190.7", {"start": v(147.2, 39.44) * mm, "end": v(145.98, 39.1) * mm});
            skLineSegment(sketch, "E11.191.0", {"start": v(145.55, 45.2) * mm, "end": v(144.33, 44.82) * mm});
            skArc(sketch, "E11.191.1", {"start": v(145.55, 45.2) * mm, "mid": v(146.2, 45.14) * mm, "end": v(146.85, 45.08) * mm});
            skArc(sketch, "E11.191.2", {"start": v(146.93, 45.02) * mm, "mid": v(146.9, 45.06) * mm, "end": v(146.85, 45.08) * mm});
            skLineSegment(sketch, "E11.191.3", {"start": v(146.93, 45.02) * mm, "end": v(147.05, 44.6) * mm});
            skLineSegment(sketch, "E11.191.4", {"start": v(147.18, 44.19) * mm, "end": v(147.05, 44.6) * mm});
            skArc(sketch, "E11.191.5", {"start": v(147.16, 44.1) * mm, "mid": v(147.18, 44.14) * mm, "end": v(147.18, 44.19) * mm});
            skArc(sketch, "E11.191.6", {"start": v(146.12, 43.28) * mm, "mid": v(146.64, 43.7) * mm, "end": v(147.16, 44.1) * mm});
            skLineSegment(sketch, "E11.191.7", {"start": v(146.12, 43.28) * mm, "end": v(144.9, 42.92) * mm});
            skLineSegment(sketch, "E11.192.0", {"start": v(144.31, 48.99) * mm, "end": v(143.1, 48.59) * mm});
            skArc(sketch, "E11.192.1", {"start": v(144.31, 48.99) * mm, "mid": v(144.97, 48.95) * mm, "end": v(145.62, 48.91) * mm});
            skArc(sketch, "E11.192.2", {"start": v(145.7, 48.85) * mm, "mid": v(145.67, 48.9) * mm, "end": v(145.62, 48.91) * mm});
            skLineSegment(sketch, "E11.192.3", {"start": v(145.7, 48.85) * mm, "end": v(145.84, 48.44) * mm});
            skLineSegment(sketch, "E11.192.4", {"start": v(145.97, 48.02) * mm, "end": v(145.84, 48.44) * mm});
            skArc(sketch, "E11.192.5", {"start": v(145.95, 47.95) * mm, "mid": v(145.97, 47.98) * mm, "end": v(145.97, 48.02) * mm});
            skArc(sketch, "E11.192.6", {"start": v(144.94, 47.1) * mm, "mid": v(145.45, 47.52) * mm, "end": v(145.95, 47.95) * mm});
            skLineSegment(sketch, "E11.192.7", {"start": v(144.94, 47.1) * mm, "end": v(143.74, 46.7) * mm});
            skLineSegment(sketch, "E11.193.0", {"start": v(142.98, 52.75) * mm, "end": v(141.79, 52.32) * mm});
            skArc(sketch, "E11.193.1", {"start": v(142.98, 52.75) * mm, "mid": v(143.64, 52.73) * mm, "end": v(144.3, 52.7) * mm});
            skArc(sketch, "E11.193.2", {"start": v(144.37, 52.65) * mm, "mid": v(144.34, 52.69) * mm, "end": v(144.3, 52.7) * mm});
            skLineSegment(sketch, "E11.193.3", {"start": v(144.37, 52.65) * mm, "end": v(144.52, 52.24) * mm});
            skLineSegment(sketch, "E11.193.4", {"start": v(144.67, 51.83) * mm, "end": v(144.52, 52.24) * mm});
            skArc(sketch, "E11.193.5", {"start": v(144.65, 51.75) * mm, "mid": v(144.67, 51.79) * mm, "end": v(144.67, 51.83) * mm});
            skArc(sketch, "E11.193.6", {"start": v(143.66, 50.87) * mm, "mid": v(144.16, 51.3) * mm, "end": v(144.65, 51.75) * mm});
            skLineSegment(sketch, "E11.193.7", {"start": v(143.66, 50.87) * mm, "end": v(142.46, 50.44) * mm});
            skLineSegment(sketch, "E11.194.0", {"start": v(141.55, 56.47) * mm, "end": v(140.37, 56.01) * mm});
            skArc(sketch, "E11.194.1", {"start": v(141.55, 56.47) * mm, "mid": v(142.2, 56.47) * mm, "end": v(142.86, 56.46) * mm});
            skArc(sketch, "E11.194.2", {"start": v(142.94, 56.4) * mm, "mid": v(142.91, 56.45) * mm, "end": v(142.86, 56.46) * mm});
            skLineSegment(sketch, "E11.194.3", {"start": v(142.94, 56.4) * mm, "end": v(143.1, 56) * mm});
            skLineSegment(sketch, "E11.194.4", {"start": v(143.26, 55.6) * mm, "end": v(143.1, 56) * mm});
            skArc(sketch, "E11.194.5", {"start": v(143.24, 55.52) * mm, "mid": v(143.26, 55.56) * mm, "end": v(143.26, 55.6) * mm});
            skArc(sketch, "E11.194.6", {"start": v(142.28, 54.62) * mm, "mid": v(142.76, 55.06) * mm, "end": v(143.24, 55.52) * mm});
            skLineSegment(sketch, "E11.194.7", {"start": v(142.28, 54.62) * mm, "end": v(141.1, 54.15) * mm});
            skLineSegment(sketch, "E11.195.0", {"start": v(140.02, 60.16) * mm, "end": v(138.85, 59.67) * mm});
            skArc(sketch, "E11.195.1", {"start": v(140.02, 60.16) * mm, "mid": v(140.68, 60.18) * mm, "end": v(141.34, 60.18) * mm});
            skArc(sketch, "E11.195.2", {"start": v(141.42, 60.13) * mm, "mid": v(141.38, 60.17) * mm, "end": v(141.34, 60.18) * mm});
            skLineSegment(sketch, "E11.195.3", {"start": v(141.42, 60.13) * mm, "end": v(141.59, 59.74) * mm});
            skLineSegment(sketch, "E11.195.4", {"start": v(141.76, 59.33) * mm, "end": v(141.59, 59.74) * mm});
            skArc(sketch, "E11.195.5", {"start": v(141.74, 59.25) * mm, "mid": v(141.76, 59.29) * mm, "end": v(141.76, 59.33) * mm});
            skArc(sketch, "E11.195.6", {"start": v(140.8, 58.32) * mm, "mid": v(141.27, 58.78) * mm, "end": v(141.74, 59.25) * mm});
            skLineSegment(sketch, "E11.195.7", {"start": v(140.8, 58.32) * mm, "end": v(139.63, 57.83) * mm});
            skLineSegment(sketch, "E11.196.0", {"start": v(138.4, 63.8) * mm, "end": v(137.24, 63.28) * mm});
            skArc(sketch, "E11.196.1", {"start": v(138.4, 63.8) * mm, "mid": v(139.06, 63.84) * mm, "end": v(139.71, 63.86) * mm});
            skArc(sketch, "E11.196.2", {"start": v(139.8, 63.81) * mm, "mid": v(139.76, 63.85) * mm, "end": v(139.71, 63.86) * mm});
            skLineSegment(sketch, "E11.196.3", {"start": v(139.8, 63.81) * mm, "end": v(139.97, 63.42) * mm});
            skLineSegment(sketch, "E11.196.4", {"start": v(140.15, 63.02) * mm, "end": v(139.97, 63.42) * mm});
            skArc(sketch, "E11.196.5", {"start": v(140.14, 62.94) * mm, "mid": v(140.16, 62.98) * mm, "end": v(140.15, 63.02) * mm});
            skArc(sketch, "E11.196.6", {"start": v(139.22, 61.99) * mm, "mid": v(139.69, 62.46) * mm, "end": v(140.14, 62.94) * mm});
            skLineSegment(sketch, "E11.196.7", {"start": v(139.22, 61.99) * mm, "end": v(138.07, 61.46) * mm});
            skLineSegment(sketch, "E11.197.0", {"start": v(136.68, 67.4) * mm, "end": v(135.54, 66.85) * mm});
            skArc(sketch, "E11.197.1", {"start": v(136.68, 67.4) * mm, "mid": v(137.34, 67.46) * mm, "end": v(138, 67.5) * mm});
            skArc(sketch, "E11.197.2", {"start": v(138.08, 67.45) * mm, "mid": v(138.04, 67.49) * mm, "end": v(138, 67.5) * mm});
            skLineSegment(sketch, "E11.197.3", {"start": v(138.08, 67.45) * mm, "end": v(138.27, 67.06) * mm});
            skLineSegment(sketch, "E11.197.4", {"start": v(138.46, 66.67) * mm, "end": v(138.27, 67.06) * mm});
            skArc(sketch, "E11.197.5", {"start": v(138.45, 66.59) * mm, "mid": v(138.46, 66.62) * mm, "end": v(138.46, 66.67) * mm});
            skArc(sketch, "E11.197.6", {"start": v(137.55, 65.6) * mm, "mid": v(138, 66.1) * mm, "end": v(138.45, 66.59) * mm});
            skLineSegment(sketch, "E11.197.7", {"start": v(137.55, 65.6) * mm, "end": v(136.41, 65.06) * mm});
            skLineSegment(sketch, "E11.198.0", {"start": v(134.87, 70.96) * mm, "end": v(133.74, 70.38) * mm});
            skArc(sketch, "E11.198.1", {"start": v(134.87, 70.96) * mm, "mid": v(135.52, 71.03) * mm, "end": v(136.18, 71.09) * mm});
            skArc(sketch, "E11.198.2", {"start": v(136.26, 71.04) * mm, "mid": v(136.23, 71.08) * mm, "end": v(136.18, 71.09) * mm});
            skLineSegment(sketch, "E11.198.3", {"start": v(136.26, 71.04) * mm, "end": v(136.46, 70.66) * mm});
            skLineSegment(sketch, "E11.198.4", {"start": v(136.66, 70.27) * mm, "end": v(136.46, 70.66) * mm});
            skArc(sketch, "E11.198.5", {"start": v(136.66, 70.19) * mm, "mid": v(136.67, 70.23) * mm, "end": v(136.66, 70.27) * mm});
            skArc(sketch, "E11.198.6", {"start": v(135.79, 69.19) * mm, "mid": v(136.23, 69.68) * mm, "end": v(136.66, 70.19) * mm});
            skLineSegment(sketch, "E11.198.7", {"start": v(135.79, 69.19) * mm, "end": v(134.66, 68.6) * mm});
            skLineSegment(sketch, "E11.199.0", {"start": v(132.97, 74.47) * mm, "end": v(131.86, 73.85) * mm});
            skArc(sketch, "E11.199.1", {"start": v(132.97, 74.47) * mm, "mid": v(133.62, 74.55) * mm, "end": v(134.27, 74.63) * mm});
            skArc(sketch, "E11.199.2", {"start": v(134.36, 74.58) * mm, "mid": v(134.32, 74.62) * mm, "end": v(134.27, 74.63) * mm});
            skLineSegment(sketch, "E11.199.3", {"start": v(134.36, 74.58) * mm, "end": v(134.57, 74.2) * mm});
            skLineSegment(sketch, "E11.199.4", {"start": v(134.78, 73.82) * mm, "end": v(134.57, 74.2) * mm});
            skArc(sketch, "E11.199.5", {"start": v(134.77, 73.74) * mm, "mid": v(134.79, 73.78) * mm, "end": v(134.78, 73.82) * mm});
            skArc(sketch, "E11.199.6", {"start": v(133.93, 72.72) * mm, "mid": v(134.36, 73.23) * mm, "end": v(134.77, 73.74) * mm});
            skLineSegment(sketch, "E11.199.7", {"start": v(133.93, 72.72) * mm, "end": v(132.82, 72.1) * mm});
            skLineSegment(sketch, "E11.200.0", {"start": v(130.97, 77.92) * mm, "end": v(129.88, 77.28) * mm});
            skArc(sketch, "E11.200.1", {"start": v(130.97, 77.92) * mm, "mid": v(131.62, 78.03) * mm, "end": v(132.27, 78.12) * mm});
            skArc(sketch, "E11.200.2", {"start": v(132.36, 78.08) * mm, "mid": v(132.32, 78.1) * mm, "end": v(132.27, 78.12) * mm});
            skLineSegment(sketch, "E11.200.3", {"start": v(132.36, 78.08) * mm, "end": v(132.58, 77.7) * mm});
            skLineSegment(sketch, "E11.200.4", {"start": v(132.8, 77.32) * mm, "end": v(132.58, 77.7) * mm});
            skArc(sketch, "E11.200.5", {"start": v(132.8, 77.24) * mm, "mid": v(132.8, 77.28) * mm, "end": v(132.8, 77.32) * mm});
            skArc(sketch, "E11.200.6", {"start": v(131.98, 76.2) * mm, "mid": v(132.4, 76.72) * mm, "end": v(132.8, 77.24) * mm});
            skLineSegment(sketch, "E11.200.7", {"start": v(131.98, 76.2) * mm, "end": v(130.89, 75.56) * mm});
            skLineSegment(sketch, "E11.201.0", {"start": v(128.89, 81.32) * mm, "end": v(127.81, 80.65) * mm});
            skArc(sketch, "E11.201.1", {"start": v(128.89, 81.32) * mm, "mid": v(129.53, 81.44) * mm, "end": v(130.18, 81.55) * mm});
            skArc(sketch, "E11.201.2", {"start": v(130.27, 81.51) * mm, "mid": v(130.23, 81.55) * mm, "end": v(130.18, 81.55) * mm});
            skLineSegment(sketch, "E11.201.3", {"start": v(130.27, 81.51) * mm, "end": v(130.5, 81.15) * mm});
            skLineSegment(sketch, "E11.201.4", {"start": v(130.73, 80.77) * mm, "end": v(130.5, 81.15) * mm});
            skArc(sketch, "E11.201.5", {"start": v(130.73, 80.7) * mm, "mid": v(130.74, 80.73) * mm, "end": v(130.73, 80.77) * mm});
            skArc(sketch, "E11.201.6", {"start": v(129.94, 79.63) * mm, "mid": v(130.34, 80.16) * mm, "end": v(130.73, 80.7) * mm});
            skLineSegment(sketch, "E11.201.7", {"start": v(129.94, 79.63) * mm, "end": v(128.86, 78.96) * mm});
            skLineSegment(sketch, "E11.202.0", {"start": v(126.72, 84.67) * mm, "end": v(125.66, 83.97) * mm});
            skArc(sketch, "E11.202.1", {"start": v(126.72, 84.67) * mm, "mid": v(127.36, 84.8) * mm, "end": v(128, 84.93) * mm});
            skArc(sketch, "E11.202.2", {"start": v(128.1, 84.9) * mm, "mid": v(128.05, 84.93) * mm, "end": v(128, 84.93) * mm});
            skLineSegment(sketch, "E11.202.3", {"start": v(128.1, 84.9) * mm, "end": v(128.33, 84.54) * mm});
            skLineSegment(sketch, "E11.202.4", {"start": v(128.57, 84.17) * mm, "end": v(128.33, 84.54) * mm});
            skArc(sketch, "E11.202.5", {"start": v(128.57, 84.09) * mm, "mid": v(128.58, 84.13) * mm, "end": v(128.57, 84.17) * mm});
            skArc(sketch, "E11.202.6", {"start": v(127.81, 83) * mm, "mid": v(128.2, 83.54) * mm, "end": v(128.57, 84.09) * mm});
            skLineSegment(sketch, "E11.202.7", {"start": v(127.81, 83) * mm, "end": v(126.75, 82.3) * mm});
            skLineSegment(sketch, "E11.203.0", {"start": v(124.46, 87.96) * mm, "end": v(123.41, 87.23) * mm});
            skArc(sketch, "E11.203.1", {"start": v(124.46, 87.96) * mm, "mid": v(125.1, 88.11) * mm, "end": v(125.73, 88.25) * mm});
            skArc(sketch, "E11.203.2", {"start": v(125.82, 88.22) * mm, "mid": v(125.78, 88.25) * mm, "end": v(125.73, 88.25) * mm});
            skLineSegment(sketch, "E11.203.3", {"start": v(125.82, 88.22) * mm, "end": v(126.07, 87.87) * mm});
            skLineSegment(sketch, "E11.203.4", {"start": v(126.32, 87.5) * mm, "end": v(126.07, 87.87) * mm});
            skArc(sketch, "E11.203.5", {"start": v(126.32, 87.43) * mm, "mid": v(126.34, 87.46) * mm, "end": v(126.32, 87.5) * mm});
            skArc(sketch, "E11.203.6", {"start": v(125.6, 86.32) * mm, "mid": v(125.97, 86.87) * mm, "end": v(126.32, 87.43) * mm});
            skLineSegment(sketch, "E11.203.7", {"start": v(125.6, 86.32) * mm, "end": v(124.55, 85.6) * mm});
            skLineSegment(sketch, "E11.204.0", {"start": v(122.11, 91.18) * mm, "end": v(121.09, 90.43) * mm});
            skArc(sketch, "E11.204.1", {"start": v(122.11, 91.18) * mm, "mid": v(122.74, 91.36) * mm, "end": v(123.38, 91.52) * mm});
            skArc(sketch, "E11.204.2", {"start": v(123.47, 91.48) * mm, "mid": v(123.43, 91.51) * mm, "end": v(123.38, 91.52) * mm});
            skLineSegment(sketch, "E11.204.3", {"start": v(123.47, 91.48) * mm, "end": v(123.73, 91.14) * mm});
            skLineSegment(sketch, "E11.204.4", {"start": v(123.99, 90.78) * mm, "end": v(123.73, 91.14) * mm});
            skArc(sketch, "E11.204.5", {"start": v(124, 90.7) * mm, "mid": v(124, 90.74) * mm, "end": v(123.99, 90.78) * mm});
            skArc(sketch, "E11.204.6", {"start": v(123.3, 89.58) * mm, "mid": v(123.65, 90.14) * mm, "end": v(124, 90.7) * mm});
            skLineSegment(sketch, "E11.204.7", {"start": v(123.3, 89.58) * mm, "end": v(122.27, 88.83) * mm});
            skLineSegment(sketch, "E11.205.0", {"start": v(119.68, 94.35) * mm, "end": v(118.68, 93.57) * mm});
            skArc(sketch, "E11.205.1", {"start": v(119.68, 94.35) * mm, "mid": v(120.31, 94.54) * mm, "end": v(120.94, 94.71) * mm});
            skArc(sketch, "E11.205.2", {"start": v(121.04, 94.68) * mm, "mid": v(121, 94.71) * mm, "end": v(120.94, 94.71) * mm});
            skLineSegment(sketch, "E11.205.3", {"start": v(121.04, 94.68) * mm, "end": v(121.3, 94.34) * mm});
            skLineSegment(sketch, "E11.205.4", {"start": v(121.57, 94) * mm, "end": v(121.3, 94.34) * mm});
            skArc(sketch, "E11.205.5", {"start": v(121.58, 93.92) * mm, "mid": v(121.58, 93.96) * mm, "end": v(121.57, 94) * mm});
            skArc(sketch, "E11.205.6", {"start": v(120.9, 92.78) * mm, "mid": v(121.25, 93.34) * mm, "end": v(121.58, 93.92) * mm});
            skLineSegment(sketch, "E11.205.7", {"start": v(120.9, 92.78) * mm, "end": v(119.9, 92) * mm});
            skLineSegment(sketch, "E11.206.0", {"start": v(117.17, 97.45) * mm, "end": v(116.19, 96.64) * mm});
            skArc(sketch, "E11.206.1", {"start": v(117.17, 97.45) * mm, "mid": v(117.8, 97.65) * mm, "end": v(118.42, 97.85) * mm});
            skArc(sketch, "E11.206.2", {"start": v(118.52, 97.82) * mm, "mid": v(118.47, 97.85) * mm, "end": v(118.42, 97.85) * mm});
            skLineSegment(sketch, "E11.206.3", {"start": v(118.52, 97.82) * mm, "end": v(118.79, 97.49) * mm});
            skLineSegment(sketch, "E11.206.4", {"start": v(119.07, 97.15) * mm, "end": v(118.79, 97.49) * mm});
            skArc(sketch, "E11.206.5", {"start": v(119.08, 97.07) * mm, "mid": v(119.08, 97.1) * mm, "end": v(119.07, 97.15) * mm});
            skArc(sketch, "E11.206.6", {"start": v(118.44, 95.9) * mm, "mid": v(118.76, 96.48) * mm, "end": v(119.08, 97.07) * mm});
            skLineSegment(sketch, "E11.206.7", {"start": v(118.44, 95.9) * mm, "end": v(117.46, 95.1) * mm});
            skLineSegment(sketch, "E11.207.0", {"start": v(114.58, 100.48) * mm, "end": v(113.62, 99.65) * mm});
            skArc(sketch, "E11.207.1", {"start": v(114.58, 100.48) * mm, "mid": v(115.2, 100.7) * mm, "end": v(115.82, 100.91) * mm});
            skArc(sketch, "E11.207.2", {"start": v(115.91, 100.89) * mm, "mid": v(115.87, 100.92) * mm, "end": v(115.82, 100.91) * mm});
            skLineSegment(sketch, "E11.207.3", {"start": v(115.91, 100.89) * mm, "end": v(116.2, 100.56) * mm});
            skLineSegment(sketch, "E11.207.4", {"start": v(116.48, 100.23) * mm, "end": v(116.2, 100.56) * mm});
            skArc(sketch, "E11.207.5", {"start": v(116.5, 100.15) * mm, "mid": v(116.5, 100.2) * mm, "end": v(116.48, 100.23) * mm});
            skArc(sketch, "E11.207.6", {"start": v(115.89, 98.98) * mm, "mid": v(116.2, 99.56) * mm, "end": v(116.5, 100.15) * mm});
            skLineSegment(sketch, "E11.207.7", {"start": v(115.89, 98.98) * mm, "end": v(114.93, 98.14) * mm});
            skLineSegment(sketch, "E11.208.0", {"start": v(111.91, 103.45) * mm, "end": v(110.97, 102.6) * mm});
            skArc(sketch, "E11.208.1", {"start": v(111.91, 103.45) * mm, "mid": v(112.52, 103.69) * mm, "end": v(113.14, 103.91) * mm});
            skArc(sketch, "E11.208.2", {"start": v(113.23, 103.89) * mm, "mid": v(113.19, 103.91) * mm, "end": v(113.14, 103.91) * mm});
            skLineSegment(sketch, "E11.208.3", {"start": v(113.23, 103.89) * mm, "end": v(113.52, 103.57) * mm});
            skLineSegment(sketch, "E11.208.4", {"start": v(113.82, 103.24) * mm, "end": v(113.52, 103.57) * mm});
            skArc(sketch, "E11.208.5", {"start": v(113.83, 103.17) * mm, "mid": v(113.84, 103.2) * mm, "end": v(113.82, 103.24) * mm});
            skArc(sketch, "E11.208.6", {"start": v(113.26, 101.98) * mm, "mid": v(113.55, 102.57) * mm, "end": v(113.83, 103.17) * mm});
            skLineSegment(sketch, "E11.208.7", {"start": v(113.26, 101.98) * mm, "end": v(112.32, 101.12) * mm});
            skLineSegment(sketch, "E11.209.0", {"start": v(109.16, 106.34) * mm, "end": v(108.25, 105.46) * mm});
            skArc(sketch, "E11.209.1", {"start": v(109.16, 106.34) * mm, "mid": v(109.77, 106.6) * mm, "end": v(110.38, 106.84) * mm});
            skArc(sketch, "E11.209.2", {"start": v(110.48, 106.82) * mm, "mid": v(110.43, 106.84) * mm, "end": v(110.38, 106.84) * mm});
            skLineSegment(sketch, "E11.209.3", {"start": v(110.48, 106.82) * mm, "end": v(110.77, 106.5) * mm});
            skLineSegment(sketch, "E11.209.4", {"start": v(111.08, 106.19) * mm, "end": v(110.77, 106.5) * mm});
            skArc(sketch, "E11.209.5", {"start": v(111.1, 106.11) * mm, "mid": v(111.1, 106.15) * mm, "end": v(111.08, 106.19) * mm});
            skArc(sketch, "E11.209.6", {"start": v(110.55, 104.9) * mm, "mid": v(110.83, 105.5) * mm, "end": v(111.1, 106.11) * mm});
            skLineSegment(sketch, "E11.209.7", {"start": v(110.55, 104.9) * mm, "end": v(109.63, 104.02) * mm});
            skLineSegment(sketch, "E11.210.0", {"start": v(106.34, 109.16) * mm, "end": v(105.45, 108.26) * mm});
            skArc(sketch, "E11.210.1", {"start": v(106.34, 109.16) * mm, "mid": v(106.94, 109.43) * mm, "end": v(107.54, 109.7) * mm});
            skArc(sketch, "E11.210.2", {"start": v(107.64, 109.67) * mm, "mid": v(107.6, 109.7) * mm, "end": v(107.54, 109.7) * mm});
            skLineSegment(sketch, "E11.210.3", {"start": v(107.64, 109.67) * mm, "end": v(107.95, 109.37) * mm});
            skLineSegment(sketch, "E11.210.4", {"start": v(108.26, 109.06) * mm, "end": v(107.95, 109.37) * mm});
            skArc(sketch, "E11.210.5", {"start": v(108.28, 108.98) * mm, "mid": v(108.28, 109.02) * mm, "end": v(108.26, 109.06) * mm});
            skArc(sketch, "E11.210.6", {"start": v(107.76, 107.76) * mm, "mid": v(108.03, 108.37) * mm, "end": v(108.28, 108.98) * mm});
            skLineSegment(sketch, "E11.210.7", {"start": v(107.76, 107.76) * mm, "end": v(106.87, 106.86) * mm});
            skLineSegment(sketch, "E11.211.0", {"start": v(103.45, 111.91) * mm, "end": v(102.58, 110.98) * mm});
            skArc(sketch, "E11.211.1", {"start": v(103.45, 111.91) * mm, "mid": v(104.04, 112.2) * mm, "end": v(104.64, 112.47) * mm});
            skArc(sketch, "E11.211.2", {"start": v(104.73, 112.45) * mm, "mid": v(104.69, 112.47) * mm, "end": v(104.64, 112.47) * mm});
            skLineSegment(sketch, "E11.211.3", {"start": v(104.73, 112.45) * mm, "end": v(105.05, 112.16) * mm});
            skLineSegment(sketch, "E11.211.4", {"start": v(105.37, 111.86) * mm, "end": v(105.05, 112.16) * mm});
            skArc(sketch, "E11.211.5", {"start": v(105.39, 111.78) * mm, "mid": v(105.39, 111.82) * mm, "end": v(105.37, 111.86) * mm});
            skArc(sketch, "E11.211.6", {"start": v(104.9, 110.55) * mm, "mid": v(105.15, 111.16) * mm, "end": v(105.39, 111.78) * mm});
            skLineSegment(sketch, "E11.211.7", {"start": v(104.9, 110.55) * mm, "end": v(104.04, 109.62) * mm});
            skLineSegment(sketch, "E11.212.0", {"start": v(100.48, 114.58) * mm, "end": v(99.64, 113.63) * mm});
            skArc(sketch, "E11.212.1", {"start": v(100.48, 114.58) * mm, "mid": v(101.07, 114.88) * mm, "end": v(101.66, 115.17) * mm});
            skArc(sketch, "E11.212.2", {"start": v(101.75, 115.15) * mm, "mid": v(101.7, 115.18) * mm, "end": v(101.66, 115.17) * mm});
            skLineSegment(sketch, "E11.212.3", {"start": v(101.75, 115.15) * mm, "end": v(102.08, 114.87) * mm});
            skLineSegment(sketch, "E11.212.4", {"start": v(102.4, 114.58) * mm, "end": v(102.08, 114.87) * mm});
            skArc(sketch, "E11.212.5", {"start": v(102.43, 114.5) * mm, "mid": v(102.43, 114.54) * mm, "end": v(102.4, 114.58) * mm});
            skArc(sketch, "E11.212.6", {"start": v(101.98, 113.26) * mm, "mid": v(102.2, 113.88) * mm, "end": v(102.43, 114.5) * mm});
            skLineSegment(sketch, "E11.212.7", {"start": v(101.98, 113.26) * mm, "end": v(101.13, 112.3) * mm});
            skLineSegment(sketch, "E11.213.0", {"start": v(97.45, 117.17) * mm, "end": v(96.63, 116.2) * mm});
            skArc(sketch, "E11.213.1", {"start": v(97.45, 117.17) * mm, "mid": v(98.03, 117.49) * mm, "end": v(98.6, 117.79) * mm});
            skArc(sketch, "E11.213.2", {"start": v(98.7, 117.78) * mm, "mid": v(98.66, 117.8) * mm, "end": v(98.6, 117.79) * mm});
            skLineSegment(sketch, "E11.213.3", {"start": v(98.7, 117.78) * mm, "end": v(99.03, 117.5) * mm});
            skLineSegment(sketch, "E11.213.4", {"start": v(99.37, 117.22) * mm, "end": v(99.03, 117.5) * mm});
            skArc(sketch, "E11.213.5", {"start": v(99.4, 117.14) * mm, "mid": v(99.4, 117.18) * mm, "end": v(99.37, 117.22) * mm});
            skArc(sketch, "E11.213.6", {"start": v(98.98, 115.89) * mm, "mid": v(99.19, 116.51) * mm, "end": v(99.4, 117.14) * mm});
            skLineSegment(sketch, "E11.213.7", {"start": v(98.98, 115.89) * mm, "end": v(98.16, 114.91) * mm});
            skLineSegment(sketch, "E11.214.0", {"start": v(94.35, 119.68) * mm, "end": v(93.56, 118.7) * mm});
            skArc(sketch, "E11.214.1", {"start": v(94.35, 119.68) * mm, "mid": v(94.92, 120.01) * mm, "end": v(95.5, 120.33) * mm});
            skArc(sketch, "E11.214.2", {"start": v(95.59, 120.32) * mm, "mid": v(95.54, 120.34) * mm, "end": v(95.5, 120.33) * mm});
            skLineSegment(sketch, "E11.214.3", {"start": v(95.59, 120.32) * mm, "end": v(95.92, 120.06) * mm});
            skLineSegment(sketch, "E11.214.4", {"start": v(96.27, 119.78) * mm, "end": v(95.92, 120.06) * mm});
            skArc(sketch, "E11.214.5", {"start": v(96.3, 119.7) * mm, "mid": v(96.3, 119.74) * mm, "end": v(96.27, 119.78) * mm});
            skArc(sketch, "E11.214.6", {"start": v(95.9, 118.44) * mm, "mid": v(96.1, 119.07) * mm, "end": v(96.3, 119.7) * mm});
            skLineSegment(sketch, "E11.214.7", {"start": v(95.9, 118.44) * mm, "end": v(95.12, 117.44) * mm});
            skLineSegment(sketch, "E11.215.0", {"start": v(91.18, 122.11) * mm, "end": v(90.42, 121.1) * mm});
            skArc(sketch, "E11.215.1", {"start": v(91.18, 122.11) * mm, "mid": v(91.74, 122.45) * mm, "end": v(92.3, 122.79) * mm});
            skArc(sketch, "E11.215.2", {"start": v(92.4, 122.78) * mm, "mid": v(92.36, 122.8) * mm, "end": v(92.3, 122.79) * mm});
            skLineSegment(sketch, "E11.215.3", {"start": v(92.4, 122.78) * mm, "end": v(92.75, 122.52) * mm});
            skLineSegment(sketch, "E11.215.4", {"start": v(93.1, 122.26) * mm, "end": v(92.75, 122.52) * mm});
            skArc(sketch, "E11.215.5", {"start": v(93.13, 122.18) * mm, "mid": v(93.12, 122.22) * mm, "end": v(93.1, 122.26) * mm});
            skArc(sketch, "E11.215.6", {"start": v(92.78, 120.9) * mm, "mid": v(92.96, 121.54) * mm, "end": v(93.13, 122.18) * mm});
            skLineSegment(sketch, "E11.215.7", {"start": v(92.78, 120.9) * mm, "end": v(92, 119.9) * mm});
            skLineSegment(sketch, "E11.216.0", {"start": v(87.96, 124.46) * mm, "end": v(87.22, 123.42) * mm});
            skArc(sketch, "E11.216.1", {"start": v(87.96, 124.46) * mm, "mid": v(88.5, 124.81) * mm, "end": v(89.06, 125.16) * mm});
            skArc(sketch, "E11.216.2", {"start": v(89.16, 125.16) * mm, "mid": v(89.11, 125.18) * mm, "end": v(89.06, 125.16) * mm});
            skLineSegment(sketch, "E11.216.3", {"start": v(89.16, 125.16) * mm, "end": v(89.5, 124.91) * mm});
            skLineSegment(sketch, "E11.216.4", {"start": v(89.87, 124.65) * mm, "end": v(89.5, 124.91) * mm});
            skArc(sketch, "E11.216.5", {"start": v(89.9, 124.58) * mm, "mid": v(89.9, 124.62) * mm, "end": v(89.87, 124.65) * mm});
            skArc(sketch, "E11.216.6", {"start": v(89.58, 123.3) * mm, "mid": v(89.74, 123.94) * mm, "end": v(89.9, 124.58) * mm});
            skLineSegment(sketch, "E11.216.7", {"start": v(89.58, 123.3) * mm, "end": v(88.84, 122.26) * mm});
            skLineSegment(sketch, "E11.217.0", {"start": v(84.67, 126.72) * mm, "end": v(83.96, 125.66) * mm});
            skArc(sketch, "E11.217.1", {"start": v(84.67, 126.72) * mm, "mid": v(85.2, 127.09) * mm, "end": v(85.75, 127.45) * mm});
            skArc(sketch, "E11.217.2", {"start": v(85.85, 127.45) * mm, "mid": v(85.8, 127.47) * mm, "end": v(85.75, 127.45) * mm});
            skLineSegment(sketch, "E11.217.3", {"start": v(85.85, 127.45) * mm, "end": v(86.2, 127.21) * mm});
            skLineSegment(sketch, "E11.217.4", {"start": v(86.57, 126.96) * mm, "end": v(86.2, 127.21) * mm});
            skArc(sketch, "E11.217.5", {"start": v(86.6, 126.89) * mm, "mid": v(86.6, 126.93) * mm, "end": v(86.57, 126.96) * mm});
            skArc(sketch, "E11.217.6", {"start": v(86.32, 125.6) * mm, "mid": v(86.47, 126.24) * mm, "end": v(86.6, 126.89) * mm});
            skLineSegment(sketch, "E11.217.7", {"start": v(86.32, 125.6) * mm, "end": v(85.6, 124.55) * mm});
            skLineSegment(sketch, "E11.218.0", {"start": v(81.32, 128.89) * mm, "end": v(80.64, 127.82) * mm});
            skArc(sketch, "E11.218.1", {"start": v(81.32, 128.89) * mm, "mid": v(81.85, 129.28) * mm, "end": v(82.39, 129.65) * mm});
            skArc(sketch, "E11.218.2", {"start": v(82.49, 129.65) * mm, "mid": v(82.44, 129.67) * mm, "end": v(82.39, 129.65) * mm});
            skLineSegment(sketch, "E11.218.3", {"start": v(82.49, 129.65) * mm, "end": v(82.85, 129.42) * mm});
            skLineSegment(sketch, "E11.218.4", {"start": v(83.22, 129.19) * mm, "end": v(82.85, 129.42) * mm});
            skArc(sketch, "E11.218.5", {"start": v(83.25, 129.11) * mm, "mid": v(83.25, 129.15) * mm, "end": v(83.22, 129.19) * mm});
            skArc(sketch, "E11.218.6", {"start": v(83, 127.81) * mm, "mid": v(83.13, 128.46) * mm, "end": v(83.25, 129.11) * mm});
            skLineSegment(sketch, "E11.218.7", {"start": v(83, 127.81) * mm, "end": v(82.32, 126.74) * mm});
            skLineSegment(sketch, "E11.219.0", {"start": v(77.92, 130.97) * mm, "end": v(77.26, 129.89) * mm});
            skArc(sketch, "E11.219.1", {"start": v(77.92, 130.97) * mm, "mid": v(78.44, 131.37) * mm, "end": v(78.97, 131.77) * mm});
            skArc(sketch, "E11.219.2", {"start": v(79.06, 131.77) * mm, "mid": v(79.02, 131.78) * mm, "end": v(78.97, 131.77) * mm});
            skLineSegment(sketch, "E11.219.3", {"start": v(79.06, 131.77) * mm, "end": v(79.43, 131.55) * mm});
            skLineSegment(sketch, "E11.219.4", {"start": v(79.81, 131.32) * mm, "end": v(79.43, 131.55) * mm});
            skArc(sketch, "E11.219.5", {"start": v(79.84, 131.25) * mm, "mid": v(79.84, 131.29) * mm, "end": v(79.81, 131.32) * mm});
            skArc(sketch, "E11.219.6", {"start": v(79.63, 129.94) * mm, "mid": v(79.74, 130.6) * mm, "end": v(79.84, 131.25) * mm});
            skLineSegment(sketch, "E11.219.7", {"start": v(79.63, 129.94) * mm, "end": v(78.97, 128.86) * mm});
            skLineSegment(sketch, "E11.220.0", {"start": v(74.47, 132.97) * mm, "end": v(73.84, 131.86) * mm});
            skArc(sketch, "E11.220.1", {"start": v(74.47, 132.97) * mm, "mid": v(74.97, 133.38) * mm, "end": v(75.5, 133.79) * mm});
            skArc(sketch, "E11.220.2", {"start": v(75.59, 133.8) * mm, "mid": v(75.54, 133.8) * mm, "end": v(75.5, 133.79) * mm});
            skLineSegment(sketch, "E11.220.3", {"start": v(75.59, 133.8) * mm, "end": v(75.96, 133.58) * mm});
            skLineSegment(sketch, "E11.220.4", {"start": v(76.35, 133.36) * mm, "end": v(75.96, 133.58) * mm});
            skArc(sketch, "E11.220.5", {"start": v(76.38, 133.3) * mm, "mid": v(76.37, 133.33) * mm, "end": v(76.35, 133.36) * mm});
            skArc(sketch, "E11.220.6", {"start": v(76.2, 131.98) * mm, "mid": v(76.3, 132.64) * mm, "end": v(76.38, 133.3) * mm});
            skLineSegment(sketch, "E11.220.7", {"start": v(76.2, 131.98) * mm, "end": v(75.57, 130.88) * mm});
            skLineSegment(sketch, "E11.221.0", {"start": v(70.96, 134.87) * mm, "end": v(70.36, 133.75) * mm});
            skArc(sketch, "E11.221.1", {"start": v(70.96, 134.87) * mm, "mid": v(71.46, 135.3) * mm, "end": v(71.96, 135.72) * mm});
            skArc(sketch, "E11.221.2", {"start": v(72.06, 135.73) * mm, "mid": v(72, 135.74) * mm, "end": v(71.96, 135.72) * mm});
            skLineSegment(sketch, "E11.221.3", {"start": v(72.06, 135.73) * mm, "end": v(72.44, 135.53) * mm});
            skLineSegment(sketch, "E11.221.4", {"start": v(72.83, 135.32) * mm, "end": v(72.44, 135.53) * mm});
            skArc(sketch, "E11.221.5", {"start": v(72.87, 135.25) * mm, "mid": v(72.86, 135.29) * mm, "end": v(72.83, 135.32) * mm});
            skArc(sketch, "E11.221.6", {"start": v(72.72, 133.93) * mm, "mid": v(72.8, 134.59) * mm, "end": v(72.87, 135.25) * mm});
            skLineSegment(sketch, "E11.221.7", {"start": v(72.72, 133.93) * mm, "end": v(72.12, 132.81) * mm});
            skLineSegment(sketch, "E11.222.0", {"start": v(67.4, 136.68) * mm, "end": v(66.84, 135.55) * mm});
            skArc(sketch, "E11.222.1", {"start": v(67.4, 136.68) * mm, "mid": v(67.9, 137.12) * mm, "end": v(68.39, 137.55) * mm});
            skArc(sketch, "E11.222.2", {"start": v(68.48, 137.57) * mm, "mid": v(68.43, 137.58) * mm, "end": v(68.39, 137.55) * mm});
            skLineSegment(sketch, "E11.222.3", {"start": v(68.48, 137.57) * mm, "end": v(68.87, 137.38) * mm});
            skLineSegment(sketch, "E11.222.4", {"start": v(69.26, 137.18) * mm, "end": v(68.87, 137.38) * mm});
            skArc(sketch, "E11.222.5", {"start": v(69.3, 137.1) * mm, "mid": v(69.3, 137.15) * mm, "end": v(69.26, 137.18) * mm});
            skArc(sketch, "E11.222.6", {"start": v(69.19, 135.79) * mm, "mid": v(69.25, 136.45) * mm, "end": v(69.3, 137.1) * mm});
            skLineSegment(sketch, "E11.222.7", {"start": v(69.19, 135.79) * mm, "end": v(68.62, 134.65) * mm});
            skLineSegment(sketch, "E11.223.0", {"start": v(63.8, 138.4) * mm, "end": v(63.26, 137.25) * mm});
            skArc(sketch, "E11.223.1", {"start": v(63.8, 138.4) * mm, "mid": v(64.28, 138.85) * mm, "end": v(64.76, 139.3) * mm});
            skArc(sketch, "E11.223.2", {"start": v(64.86, 139.31) * mm, "mid": v(64.8, 139.32) * mm, "end": v(64.76, 139.3) * mm});
            skLineSegment(sketch, "E11.223.3", {"start": v(64.86, 139.31) * mm, "end": v(65.25, 139.13) * mm});
            skLineSegment(sketch, "E11.223.4", {"start": v(65.65, 138.94) * mm, "end": v(65.25, 139.13) * mm});
            skArc(sketch, "E11.223.5", {"start": v(65.69, 138.87) * mm, "mid": v(65.68, 138.91) * mm, "end": v(65.65, 138.94) * mm});
            skArc(sketch, "E11.223.6", {"start": v(65.6, 137.55) * mm, "mid": v(65.65, 138.21) * mm, "end": v(65.69, 138.87) * mm});
            skLineSegment(sketch, "E11.223.7", {"start": v(65.6, 137.55) * mm, "end": v(65.07, 136.4) * mm});
            skLineSegment(sketch, "E11.224.0", {"start": v(60.16, 140.02) * mm, "end": v(59.65, 138.86) * mm});
            skArc(sketch, "E11.224.1", {"start": v(60.16, 140.02) * mm, "mid": v(60.62, 140.49) * mm, "end": v(61.1, 140.95) * mm});
            skArc(sketch, "E11.224.2", {"start": v(61.19, 140.96) * mm, "mid": v(61.14, 140.97) * mm, "end": v(61.1, 140.95) * mm});
            skLineSegment(sketch, "E11.224.3", {"start": v(61.19, 140.96) * mm, "end": v(61.58, 140.8) * mm});
            skLineSegment(sketch, "E11.224.4", {"start": v(61.99, 140.61) * mm, "end": v(61.58, 140.8) * mm});
            skArc(sketch, "E11.224.5", {"start": v(62.03, 140.55) * mm, "mid": v(62.02, 140.59) * mm, "end": v(61.99, 140.61) * mm});
            skArc(sketch, "E11.224.6", {"start": v(61.99, 139.22) * mm, "mid": v(62.01, 139.89) * mm, "end": v(62.03, 140.55) * mm});
            skLineSegment(sketch, "E11.224.7", {"start": v(61.99, 139.22) * mm, "end": v(61.48, 138.06) * mm});
            skLineSegment(sketch, "E11.225.0", {"start": v(56.47, 141.55) * mm, "end": v(56, 140.37) * mm});
            skArc(sketch, "E11.225.1", {"start": v(56.47, 141.55) * mm, "mid": v(56.92, 142.03) * mm, "end": v(57.38, 142.5) * mm});
            skArc(sketch, "E11.225.2", {"start": v(57.48, 142.52) * mm, "mid": v(57.43, 142.52) * mm, "end": v(57.38, 142.5) * mm});
            skLineSegment(sketch, "E11.225.3", {"start": v(57.48, 142.52) * mm, "end": v(57.88, 142.36) * mm});
            skLineSegment(sketch, "E11.225.4", {"start": v(58.29, 142.19) * mm, "end": v(57.88, 142.36) * mm});
            skArc(sketch, "E11.225.5", {"start": v(58.33, 142.12) * mm, "mid": v(58.32, 142.16) * mm, "end": v(58.29, 142.19) * mm});
            skArc(sketch, "E11.225.6", {"start": v(58.32, 140.8) * mm, "mid": v(58.33, 141.46) * mm, "end": v(58.33, 142.12) * mm});
            skLineSegment(sketch, "E11.225.7", {"start": v(58.32, 140.8) * mm, "end": v(57.84, 139.62) * mm});
            skLineSegment(sketch, "E11.226.0", {"start": v(52.75, 142.98) * mm, "end": v(52.3, 141.8) * mm});
            skArc(sketch, "E11.226.1", {"start": v(52.75, 142.98) * mm, "mid": v(53.19, 143.47) * mm, "end": v(53.63, 143.95) * mm});
            skArc(sketch, "E11.226.2", {"start": v(53.73, 143.97) * mm, "mid": v(53.68, 143.97) * mm, "end": v(53.63, 143.95) * mm});
            skLineSegment(sketch, "E11.226.3", {"start": v(53.73, 143.97) * mm, "end": v(54.13, 143.82) * mm});
            skLineSegment(sketch, "E11.226.4", {"start": v(54.54, 143.66) * mm, "end": v(54.13, 143.82) * mm});
            skArc(sketch, "E11.226.5", {"start": v(54.59, 143.6) * mm, "mid": v(54.58, 143.64) * mm, "end": v(54.54, 143.66) * mm});
            skArc(sketch, "E11.226.6", {"start": v(54.62, 142.28) * mm, "mid": v(54.6, 142.94) * mm, "end": v(54.59, 143.6) * mm});
            skLineSegment(sketch, "E11.226.7", {"start": v(54.62, 142.28) * mm, "end": v(54.17, 141.09) * mm});
            skLineSegment(sketch, "E11.227.0", {"start": v(48.99, 144.31) * mm, "end": v(48.57, 143.11) * mm});
            skArc(sketch, "E11.227.1", {"start": v(48.99, 144.31) * mm, "mid": v(49.41, 144.81) * mm, "end": v(49.85, 145.3) * mm});
            skArc(sketch, "E11.227.2", {"start": v(49.94, 145.33) * mm, "mid": v(49.89, 145.33) * mm, "end": v(49.85, 145.3) * mm});
            skLineSegment(sketch, "E11.227.3", {"start": v(49.94, 145.33) * mm, "end": v(50.35, 145.19) * mm});
            skLineSegment(sketch, "E11.227.4", {"start": v(50.76, 145.04) * mm, "end": v(50.35, 145.19) * mm});
            skArc(sketch, "E11.227.5", {"start": v(50.81, 144.98) * mm, "mid": v(50.8, 145.02) * mm, "end": v(50.76, 145.04) * mm});
            skArc(sketch, "E11.227.6", {"start": v(50.87, 143.66) * mm, "mid": v(50.85, 144.32) * mm, "end": v(50.81, 144.98) * mm});
            skLineSegment(sketch, "E11.227.7", {"start": v(50.87, 143.66) * mm, "end": v(50.46, 142.46) * mm});
            skLineSegment(sketch, "E11.228.0", {"start": v(45.2, 145.55) * mm, "end": v(44.8, 144.33) * mm});
            skArc(sketch, "E11.228.1", {"start": v(45.2, 145.55) * mm, "mid": v(45.6, 146.06) * mm, "end": v(46.02, 146.56) * mm});
            skArc(sketch, "E11.228.2", {"start": v(46.12, 146.59) * mm, "mid": v(46.07, 146.59) * mm, "end": v(46.02, 146.56) * mm});
            skLineSegment(sketch, "E11.228.3", {"start": v(46.12, 146.59) * mm, "end": v(46.53, 146.46) * mm});
            skLineSegment(sketch, "E11.228.4", {"start": v(46.95, 146.32) * mm, "end": v(46.53, 146.46) * mm});
            skArc(sketch, "E11.228.5", {"start": v(47, 146.26) * mm, "mid": v(46.98, 146.3) * mm, "end": v(46.95, 146.32) * mm});
            skArc(sketch, "E11.228.6", {"start": v(47.1, 144.94) * mm, "mid": v(47.05, 145.6) * mm, "end": v(47, 146.26) * mm});
            skLineSegment(sketch, "E11.228.7", {"start": v(47.1, 144.94) * mm, "end": v(46.7, 143.73) * mm});
            skLineSegment(sketch, "E11.229.0", {"start": v(41.37, 146.68) * mm, "end": v(41.01, 145.46) * mm});
            skArc(sketch, "E11.229.1", {"start": v(41.37, 146.68) * mm, "mid": v(41.77, 147.2) * mm, "end": v(42.17, 147.71) * mm});
            skArc(sketch, "E11.229.2", {"start": v(42.27, 147.74) * mm, "mid": v(42.21, 147.74) * mm, "end": v(42.17, 147.71) * mm});
            skLineSegment(sketch, "E11.229.3", {"start": v(42.27, 147.74) * mm, "end": v(42.68, 147.63) * mm});
            skLineSegment(sketch, "E11.229.4", {"start": v(43.1, 147.5) * mm, "end": v(42.68, 147.63) * mm});
            skArc(sketch, "E11.229.5", {"start": v(43.15, 147.44) * mm, "mid": v(43.14, 147.48) * mm, "end": v(43.1, 147.5) * mm});
            skArc(sketch, "E11.229.6", {"start": v(43.28, 146.12) * mm, "mid": v(43.22, 146.78) * mm, "end": v(43.15, 147.44) * mm});
            skLineSegment(sketch, "E11.229.7", {"start": v(43.28, 146.12) * mm, "end": v(42.93, 144.9) * mm});
            skLineSegment(sketch, "E11.230.0", {"start": v(37.51, 147.71) * mm, "end": v(37.2, 146.48) * mm});
            skArc(sketch, "E11.230.1", {"start": v(37.51, 147.71) * mm, "mid": v(37.9, 148.24) * mm, "end": v(38.3, 148.77) * mm});
            skArc(sketch, "E11.230.2", {"start": v(38.38, 148.8) * mm, "mid": v(38.33, 148.8) * mm, "end": v(38.3, 148.77) * mm});
            skLineSegment(sketch, "E11.230.3", {"start": v(38.38, 148.8) * mm, "end": v(38.8, 148.7) * mm});
            skLineSegment(sketch, "E11.230.4", {"start": v(39.23, 148.58) * mm, "end": v(38.8, 148.7) * mm});
            skArc(sketch, "E11.230.5", {"start": v(39.28, 148.52) * mm, "mid": v(39.26, 148.56) * mm, "end": v(39.23, 148.58) * mm});
            skArc(sketch, "E11.230.6", {"start": v(39.44, 147.2) * mm, "mid": v(39.37, 147.86) * mm, "end": v(39.28, 148.52) * mm});
            skLineSegment(sketch, "E11.230.7", {"start": v(39.44, 147.2) * mm, "end": v(39.12, 145.98) * mm});
            skLineSegment(sketch, "E11.231.0", {"start": v(33.63, 148.64) * mm, "end": v(33.35, 147.4) * mm});
            skArc(sketch, "E11.231.1", {"start": v(33.63, 148.64) * mm, "mid": v(34, 149.18) * mm, "end": v(34.38, 149.72) * mm});
            skArc(sketch, "E11.231.2", {"start": v(34.48, 149.75) * mm, "mid": v(34.42, 149.75) * mm, "end": v(34.38, 149.72) * mm});
            skLineSegment(sketch, "E11.231.3", {"start": v(34.48, 149.75) * mm, "end": v(34.9, 149.66) * mm});
            skLineSegment(sketch, "E11.231.4", {"start": v(35.32, 149.55) * mm, "end": v(34.9, 149.66) * mm});
            skArc(sketch, "E11.231.5", {"start": v(35.38, 149.5) * mm, "mid": v(35.36, 149.53) * mm, "end": v(35.32, 149.55) * mm});
            skArc(sketch, "E11.231.6", {"start": v(35.58, 148.19) * mm, "mid": v(35.48, 148.84) * mm, "end": v(35.38, 149.5) * mm});
            skLineSegment(sketch, "E11.231.7", {"start": v(35.58, 148.19) * mm, "end": v(35.29, 146.95) * mm});
            skLineSegment(sketch, "E11.232.0", {"start": v(29.73, 149.47) * mm, "end": v(29.48, 148.23) * mm});
            skArc(sketch, "E11.232.1", {"start": v(29.73, 149.47) * mm, "mid": v(30.09, 150.02) * mm, "end": v(30.45, 150.57) * mm});
            skArc(sketch, "E11.232.2", {"start": v(30.54, 150.6) * mm, "mid": v(30.5, 150.6) * mm, "end": v(30.45, 150.57) * mm});
            skLineSegment(sketch, "E11.232.3", {"start": v(30.54, 150.6) * mm, "end": v(30.97, 150.52) * mm});
            skLineSegment(sketch, "E11.232.4", {"start": v(31.4, 150.43) * mm, "end": v(30.97, 150.52) * mm});
            skArc(sketch, "E11.232.5", {"start": v(31.45, 150.37) * mm, "mid": v(31.43, 150.4) * mm, "end": v(31.4, 150.43) * mm});
            skArc(sketch, "E11.232.6", {"start": v(31.69, 149.07) * mm, "mid": v(31.58, 149.72) * mm, "end": v(31.45, 150.37) * mm});
            skLineSegment(sketch, "E11.232.7", {"start": v(31.69, 149.07) * mm, "end": v(31.43, 147.83) * mm});
            skLineSegment(sketch, "E11.233.0", {"start": v(25.8, 150.2) * mm, "end": v(25.59, 148.95) * mm});
            skArc(sketch, "E11.233.1", {"start": v(25.8, 150.2) * mm, "mid": v(26.15, 150.76) * mm, "end": v(26.5, 151.31) * mm});
            skArc(sketch, "E11.233.2", {"start": v(26.6, 151.35) * mm, "mid": v(26.54, 151.35) * mm, "end": v(26.5, 151.31) * mm});
            skLineSegment(sketch, "E11.233.3", {"start": v(26.6, 151.35) * mm, "end": v(27.01, 151.28) * mm});
            skLineSegment(sketch, "E11.233.4", {"start": v(27.45, 151.2) * mm, "end": v(27.01, 151.28) * mm});
            skArc(sketch, "E11.233.5", {"start": v(27.5, 151.14) * mm, "mid": v(27.49, 151.18) * mm, "end": v(27.45, 151.2) * mm});
            skArc(sketch, "E11.233.6", {"start": v(27.77, 149.85) * mm, "mid": v(27.64, 150.5) * mm, "end": v(27.5, 151.14) * mm});
            skLineSegment(sketch, "E11.233.7", {"start": v(27.77, 149.85) * mm, "end": v(27.55, 148.6) * mm});
            skLineSegment(sketch, "E11.234.0", {"start": v(21.87, 150.82) * mm, "end": v(21.68, 149.57) * mm});
            skArc(sketch, "E11.234.1", {"start": v(21.87, 150.82) * mm, "mid": v(22.2, 151.4) * mm, "end": v(22.53, 151.95) * mm});
            skArc(sketch, "E11.234.2", {"start": v(22.62, 152) * mm, "mid": v(22.57, 151.99) * mm, "end": v(22.53, 151.95) * mm});
            skLineSegment(sketch, "E11.234.3", {"start": v(22.62, 152) * mm, "end": v(23.05, 151.93) * mm});
            skLineSegment(sketch, "E11.234.4", {"start": v(23.48, 151.87) * mm, "end": v(23.05, 151.93) * mm});
            skArc(sketch, "E11.234.5", {"start": v(23.54, 151.81) * mm, "mid": v(23.52, 151.85) * mm, "end": v(23.48, 151.87) * mm});
            skArc(sketch, "E11.234.6", {"start": v(23.84, 150.52) * mm, "mid": v(23.7, 151.17) * mm, "end": v(23.54, 151.81) * mm});
            skLineSegment(sketch, "E11.234.7", {"start": v(23.84, 150.52) * mm, "end": v(23.65, 149.27) * mm});
            skLineSegment(sketch, "E11.235.0", {"start": v(17.91, 151.34) * mm, "end": v(17.76, 150.08) * mm});
            skArc(sketch, "E11.235.1", {"start": v(17.91, 151.34) * mm, "mid": v(18.22, 151.92) * mm, "end": v(18.55, 152.5) * mm});
            skArc(sketch, "E11.235.2", {"start": v(18.63, 152.54) * mm, "mid": v(18.58, 152.53) * mm, "end": v(18.55, 152.5) * mm});
            skLineSegment(sketch, "E11.235.3", {"start": v(18.63, 152.54) * mm, "end": v(19.06, 152.48) * mm});
            skLineSegment(sketch, "E11.235.4", {"start": v(19.5, 152.43) * mm, "end": v(19.06, 152.48) * mm});
            skArc(sketch, "E11.235.5", {"start": v(19.56, 152.38) * mm, "mid": v(19.54, 152.41) * mm, "end": v(19.5, 152.43) * mm});
            skArc(sketch, "E11.235.6", {"start": v(19.9, 151.1) * mm, "mid": v(19.73, 151.74) * mm, "end": v(19.56, 152.38) * mm});
            skLineSegment(sketch, "E11.235.7", {"start": v(19.9, 151.1) * mm, "end": v(19.73, 149.84) * mm});
            skLineSegment(sketch, "E11.236.0", {"start": v(13.94, 151.76) * mm, "end": v(13.82, 150.5) * mm});
            skArc(sketch, "E11.236.1", {"start": v(13.94, 151.76) * mm, "mid": v(14.24, 152.35) * mm, "end": v(14.55, 152.93) * mm});
            skArc(sketch, "E11.236.2", {"start": v(14.63, 152.97) * mm, "mid": v(14.58, 152.96) * mm, "end": v(14.55, 152.93) * mm});
            skLineSegment(sketch, "E11.236.3", {"start": v(14.63, 152.97) * mm, "end": v(15.06, 152.93) * mm});
            skLineSegment(sketch, "E11.236.4", {"start": v(15.5, 152.89) * mm, "end": v(15.06, 152.93) * mm});
            skArc(sketch, "E11.236.5", {"start": v(15.56, 152.84) * mm, "mid": v(15.54, 152.87) * mm, "end": v(15.5, 152.89) * mm});
            skArc(sketch, "E11.236.6", {"start": v(15.93, 151.57) * mm, "mid": v(15.75, 152.2) * mm, "end": v(15.56, 152.84) * mm});
            skLineSegment(sketch, "E11.236.7", {"start": v(15.93, 151.57) * mm, "end": v(15.8, 150.3) * mm});
            skLineSegment(sketch, "E11.237.0", {"start": v(9.97, 152.07) * mm, "end": v(9.88, 150.8) * mm});
            skArc(sketch, "E11.237.1", {"start": v(9.97, 152.07) * mm, "mid": v(10.25, 152.67) * mm, "end": v(10.54, 153.25) * mm});
            skArc(sketch, "E11.237.2", {"start": v(10.62, 153.3) * mm, "mid": v(10.58, 153.3) * mm, "end": v(10.54, 153.25) * mm});
            skLineSegment(sketch, "E11.237.3", {"start": v(10.62, 153.3) * mm, "end": v(11.05, 153.27) * mm});
            skLineSegment(sketch, "E11.237.4", {"start": v(11.5, 153.24) * mm, "end": v(11.05, 153.27) * mm});
            skArc(sketch, "E11.237.5", {"start": v(11.56, 153.2) * mm, "mid": v(11.53, 153.22) * mm, "end": v(11.5, 153.24) * mm});
            skArc(sketch, "E11.237.6", {"start": v(11.96, 151.93) * mm, "mid": v(11.76, 152.56) * mm, "end": v(11.56, 153.2) * mm});
            skLineSegment(sketch, "E11.237.7", {"start": v(11.96, 151.93) * mm, "end": v(11.87, 150.66) * mm});
            skLineSegment(sketch, "E11.238.0", {"start": v(5.98, 152.28) * mm, "end": v(5.93, 151.01) * mm});
            skArc(sketch, "E11.238.1", {"start": v(5.98, 152.28) * mm, "mid": v(6.25, 152.88) * mm, "end": v(6.52, 153.48) * mm});
            skArc(sketch, "E11.238.2", {"start": v(6.6, 153.53) * mm, "mid": v(6.56, 153.52) * mm, "end": v(6.52, 153.48) * mm});
            skLineSegment(sketch, "E11.238.3", {"start": v(6.6, 153.53) * mm, "end": v(7.04, 153.5) * mm});
            skLineSegment(sketch, "E11.238.4", {"start": v(7.48, 153.49) * mm, "end": v(7.04, 153.5) * mm});
            skArc(sketch, "E11.238.5", {"start": v(7.54, 153.44) * mm, "mid": v(7.52, 153.47) * mm, "end": v(7.48, 153.49) * mm});
            skArc(sketch, "E11.238.6", {"start": v(7.98, 152.2) * mm, "mid": v(7.76, 152.82) * mm, "end": v(7.54, 153.44) * mm});
            skLineSegment(sketch, "E11.238.7", {"start": v(7.98, 152.2) * mm, "end": v(7.92, 150.92) * mm});
            skLineSegment(sketch, "E11.239.0", {"start": v(2, 152.39) * mm, "end": v(1.97, 151.12) * mm});
            skArc(sketch, "E11.239.1", {"start": v(2, 152.39) * mm, "mid": v(2.24, 153) * mm, "end": v(2.5, 153.6) * mm});
            skArc(sketch, "E11.239.2", {"start": v(2.59, 153.65) * mm, "mid": v(2.54, 153.63) * mm, "end": v(2.5, 153.6) * mm});
            skLineSegment(sketch, "E11.239.3", {"start": v(2.59, 153.65) * mm, "end": v(3.02, 153.64) * mm});
            skLineSegment(sketch, "E11.239.4", {"start": v(3.46, 153.63) * mm, "end": v(3.02, 153.64) * mm});
            skArc(sketch, "E11.239.5", {"start": v(3.52, 153.59) * mm, "mid": v(3.5, 153.62) * mm, "end": v(3.46, 153.63) * mm});
            skArc(sketch, "E11.239.6", {"start": v(3.99, 152.35) * mm, "mid": v(3.76, 152.97) * mm, "end": v(3.52, 153.59) * mm});
            skLineSegment(sketch, "E11.239.7", {"start": v(3.99, 152.35) * mm, "end": v(3.96, 151.08) * mm});
            skLineSegment(sketch, "E12", {"start": v(0, 0) * mm, "end": v(0, 97.8) * mm, "construction": true});
            skCircle(sketch, "E13", {"center": v(0, 97.8) * mm, "radius": 25.4 * mm});
            skCircle(sketch, "E14.1.0", {"center": v(-69.15, 69.15) * mm, "radius": 25.4 * mm});
            skCircle(sketch, "E14.2.0", {"center": v(-97.8, 0) * mm, "radius": 25.4 * mm});
            skCircle(sketch, "E14.3.0", {"center": v(-69.15, -69.15) * mm, "radius": 25.4 * mm});
            skCircle(sketch, "E14.4.0", {"center": v(0, -97.8) * mm, "radius": 25.4 * mm});
            skCircle(sketch, "E14.5.0", {"center": v(69.15, -69.15) * mm, "radius": 25.4 * mm});
            skCircle(sketch, "E14.6.0", {"center": v(97.8, 0) * mm, "radius": 25.4 * mm});
            skCircle(sketch, "E14.7.0", {"center": v(69.15, 69.15) * mm, "radius": 25.4 * mm});
            skCircle(sketch, "E15", {"center": v(0, 0) * mm, "radius": 6.35 * mm});
            skSolve(sketch);
        }
        {
            var Q0;
            {var subQ0=sQuery(id+"F0.wireOp",EDGE,"E11.1.0");Q0=makeQuery(id+"F0.imprint","IMPRINT",FACE,{"disambiguationData":[TD([[makeQuery(id+"F0.imprint","IMPRINT",EDGE,{"derivedFrom":subQ0}),1.0]])]});}
            var Q1;
            {var subQ0=sQuery(id+"F0.wireOp",EDGE,"E11.2.0");Q1=makeQuery(id+"F0.imprint","IMPRINT",FACE,{"disambiguationData":[TD([[makeQuery(id+"F0.imprint","IMPRINT",EDGE,{"derivedFrom":subQ0}),1.0]])]});}
            var Q2;
            {var subQ0=sQuery(id+"F0.wireOp",EDGE,"E11.3.0");Q2=makeQuery(id+"F0.imprint","IMPRINT",FACE,{"disambiguationData":[TD([[makeQuery(id+"F0.imprint","IMPRINT",EDGE,{"derivedFrom":subQ0}),1.0]])]});}
            var Q3;
            {var subQ0=sQuery(id+"F0.wireOp",EDGE,"E11.4.0");Q3=makeQuery(id+"F0.imprint","IMPRINT",FACE,{"disambiguationData":[TD([[makeQuery(id+"F0.imprint","IMPRINT",EDGE,{"derivedFrom":subQ0}),1.0]])]});}
            var Q4;
            {var subQ0=sQuery(id+"F0.wireOp",EDGE,"E11.5.0");Q4=makeQuery(id+"F0.imprint","IMPRINT",FACE,{"disambiguationData":[TD([[makeQuery(id+"F0.imprint","IMPRINT",EDGE,{"derivedFrom":subQ0}),1.0]])]});}
            var Q5;
            {var subQ0=sQuery(id+"F0.wireOp",EDGE,"E11.6.0");Q5=makeQuery(id+"F0.imprint","IMPRINT",FACE,{"disambiguationData":[TD([[makeQuery(id+"F0.imprint","IMPRINT",EDGE,{"derivedFrom":subQ0}),1.0]])]});}
            var Q6;
            {var subQ0=sQuery(id+"F0.wireOp",EDGE,"E11.7.0");Q6=makeQuery(id+"F0.imprint","IMPRINT",FACE,{"disambiguationData":[TD([[makeQuery(id+"F0.imprint","IMPRINT",EDGE,{"derivedFrom":subQ0}),1.0]])]});}
            var Q7;
            {var subQ0=sQuery(id+"F0.wireOp",EDGE,"E11.8.0");Q7=makeQuery(id+"F0.imprint","IMPRINT",FACE,{"disambiguationData":[TD([[makeQuery(id+"F0.imprint","IMPRINT",EDGE,{"derivedFrom":subQ0}),1.0]])]});}
            var Q8;
            {var subQ1=sQuery(id+"F0.wireOp",EDGE,"E11.9.0");Q8=makeQuery(id+"F0.imprint","IMPRINT",FACE,{"disambiguationData":[TD([[makeQuery(id+"F0.imprint","IMPRINT",EDGE,{"derivedFrom":subQ1}),1.0]])]});}
            var Q9;
            {var subQ0=sQuery(id+"F0.wireOp",EDGE,"E11.10.0");Q9=makeQuery(id+"F0.imprint","IMPRINT",FACE,{"disambiguationData":[TD([[makeQuery(id+"F0.imprint","IMPRINT",EDGE,{"derivedFrom":subQ0}),1.0]])]});}
            var Q10;
            {var subQ0=sQuery(id+"F0.wireOp",EDGE,"E11.11.0");Q10=makeQuery(id+"F0.imprint","IMPRINT",FACE,{"disambiguationData":[TD([[makeQuery(id+"F0.imprint","IMPRINT",EDGE,{"derivedFrom":subQ0}),1.0]])]});}
            var Q11;
            {var subQ0=sQuery(id+"F0.wireOp",EDGE,"E11.12.0");Q11=makeQuery(id+"F0.imprint","IMPRINT",FACE,{"disambiguationData":[TD([[makeQuery(id+"F0.imprint","IMPRINT",EDGE,{"derivedFrom":subQ0}),1.0]])]});}
            var Q12;
            {var subQ0=sQuery(id+"F0.wireOp",EDGE,"E11.13.0");Q12=makeQuery(id+"F0.imprint","IMPRINT",FACE,{"disambiguationData":[TD([[makeQuery(id+"F0.imprint","IMPRINT",EDGE,{"derivedFrom":subQ0}),1.0]])]});}
            var Q13;
            {var subQ0=sQuery(id+"F0.wireOp",EDGE,"E11.14.0");Q13=makeQuery(id+"F0.imprint","IMPRINT",FACE,{"disambiguationData":[TD([[makeQuery(id+"F0.imprint","IMPRINT",EDGE,{"derivedFrom":subQ0}),1.0]])]});}
            var Q14;
            {var subQ0=sQuery(id+"F0.wireOp",EDGE,"E11.15.0");Q14=makeQuery(id+"F0.imprint","IMPRINT",FACE,{"disambiguationData":[TD([[makeQuery(id+"F0.imprint","IMPRINT",EDGE,{"derivedFrom":subQ0}),1.0]])]});}
            var Q15;
            {var subQ0=sQuery(id+"F0.wireOp",EDGE,"E11.16.0");Q15=makeQuery(id+"F0.imprint","IMPRINT",FACE,{"disambiguationData":[TD([[makeQuery(id+"F0.imprint","IMPRINT",EDGE,{"derivedFrom":subQ0}),1.0]])]});}
            var Q16;
            {var subQ1=sQuery(id+"F0.wireOp",EDGE,"E11.17.0");Q16=makeQuery(id+"F0.imprint","IMPRINT",FACE,{"disambiguationData":[TD([[makeQuery(id+"F0.imprint","IMPRINT",EDGE,{"derivedFrom":subQ1}),1.0]])]});}
            var Q17;
            {var subQ0=sQuery(id+"F0.wireOp",EDGE,"E11.18.0");Q17=makeQuery(id+"F0.imprint","IMPRINT",FACE,{"disambiguationData":[TD([[makeQuery(id+"F0.imprint","IMPRINT",EDGE,{"derivedFrom":subQ0}),1.0]])]});}
            var Q18;
            {var subQ0=sQuery(id+"F0.wireOp",EDGE,"E11.19.0");Q18=makeQuery(id+"F0.imprint","IMPRINT",FACE,{"disambiguationData":[TD([[makeQuery(id+"F0.imprint","IMPRINT",EDGE,{"derivedFrom":subQ0}),1.0]])]});}
            var Q19;
            {var subQ0=sQuery(id+"F0.wireOp",EDGE,"E11.20.0");Q19=makeQuery(id+"F0.imprint","IMPRINT",FACE,{"disambiguationData":[TD([[makeQuery(id+"F0.imprint","IMPRINT",EDGE,{"derivedFrom":subQ0}),1.0]])]});}
            var Q20;
            {var subQ0=sQuery(id+"F0.wireOp",EDGE,"E11.21.0");Q20=makeQuery(id+"F0.imprint","IMPRINT",FACE,{"disambiguationData":[TD([[makeQuery(id+"F0.imprint","IMPRINT",EDGE,{"derivedFrom":subQ0}),1.0]])]});}
            var Q21;
            {var subQ0=sQuery(id+"F0.wireOp",EDGE,"E11.22.0");Q21=makeQuery(id+"F0.imprint","IMPRINT",FACE,{"disambiguationData":[TD([[makeQuery(id+"F0.imprint","IMPRINT",EDGE,{"derivedFrom":subQ0}),1.0]])]});}
            var Q22;
            {var subQ0=sQuery(id+"F0.wireOp",EDGE,"E11.23.0");Q22=makeQuery(id+"F0.imprint","IMPRINT",FACE,{"disambiguationData":[TD([[makeQuery(id+"F0.imprint","IMPRINT",EDGE,{"derivedFrom":subQ0}),1.0]])]});}
            var Q23;
            {var subQ1=sQuery(id+"F0.wireOp",EDGE,"E11.24.0");Q23=makeQuery(id+"F0.imprint","IMPRINT",FACE,{"disambiguationData":[TD([[makeQuery(id+"F0.imprint","IMPRINT",EDGE,{"derivedFrom":subQ1}),1.0]])]});}
            var Q24;
            {var subQ0=sQuery(id+"F0.wireOp",EDGE,"E11.25.0");Q24=makeQuery(id+"F0.imprint","IMPRINT",FACE,{"disambiguationData":[TD([[makeQuery(id+"F0.imprint","IMPRINT",EDGE,{"derivedFrom":subQ0}),1.0]])]});}
            var Q25;
            {var subQ0=sQuery(id+"F0.wireOp",EDGE,"E11.26.0");Q25=makeQuery(id+"F0.imprint","IMPRINT",FACE,{"disambiguationData":[TD([[makeQuery(id+"F0.imprint","IMPRINT",EDGE,{"derivedFrom":subQ0}),1.0]])]});}
            var Q26;
            {var subQ0=sQuery(id+"F0.wireOp",EDGE,"E11.27.0");Q26=makeQuery(id+"F0.imprint","IMPRINT",FACE,{"disambiguationData":[TD([[makeQuery(id+"F0.imprint","IMPRINT",EDGE,{"derivedFrom":subQ0}),1.0]])]});}
            var Q27;
            {var subQ0=sQuery(id+"F0.wireOp",EDGE,"E11.28.0");Q27=makeQuery(id+"F0.imprint","IMPRINT",FACE,{"disambiguationData":[TD([[makeQuery(id+"F0.imprint","IMPRINT",EDGE,{"derivedFrom":subQ0}),1.0]])]});}
            var Q28;
            {var subQ0=sQuery(id+"F0.wireOp",EDGE,"E11.29.0");Q28=makeQuery(id+"F0.imprint","IMPRINT",FACE,{"disambiguationData":[TD([[makeQuery(id+"F0.imprint","IMPRINT",EDGE,{"derivedFrom":subQ0}),1.0]])]});}
            var Q29;
            {var subQ0=sQuery(id+"F0.wireOp",EDGE,"E11.30.0");Q29=makeQuery(id+"F0.imprint","IMPRINT",FACE,{"disambiguationData":[TD([[makeQuery(id+"F0.imprint","IMPRINT",EDGE,{"derivedFrom":subQ0}),1.0]])]});}
            var Q30;
            {var subQ0=sQuery(id+"F0.wireOp",EDGE,"E11.31.0");Q30=makeQuery(id+"F0.imprint","IMPRINT",FACE,{"disambiguationData":[TD([[makeQuery(id+"F0.imprint","IMPRINT",EDGE,{"derivedFrom":subQ0}),1.0]])]});}
            var Q31;
            {var subQ1=sQuery(id+"F0.wireOp",EDGE,"E11.32.0");Q31=makeQuery(id+"F0.imprint","IMPRINT",FACE,{"disambiguationData":[TD([[makeQuery(id+"F0.imprint","IMPRINT",EDGE,{"derivedFrom":subQ1}),1.0]])]});}
            var Q32;
            {var subQ0=sQuery(id+"F0.wireOp",EDGE,"E11.33.0");Q32=makeQuery(id+"F0.imprint","IMPRINT",FACE,{"disambiguationData":[TD([[makeQuery(id+"F0.imprint","IMPRINT",EDGE,{"derivedFrom":subQ0}),1.0]])]});}
            var Q33;
            {var subQ0=sQuery(id+"F0.wireOp",EDGE,"E11.34.0");Q33=makeQuery(id+"F0.imprint","IMPRINT",FACE,{"disambiguationData":[TD([[makeQuery(id+"F0.imprint","IMPRINT",EDGE,{"derivedFrom":subQ0}),1.0]])]});}
            var Q34;
            {var subQ0=sQuery(id+"F0.wireOp",EDGE,"E11.35.0");Q34=makeQuery(id+"F0.imprint","IMPRINT",FACE,{"disambiguationData":[TD([[makeQuery(id+"F0.imprint","IMPRINT",EDGE,{"derivedFrom":subQ0}),1.0]])]});}
            var Q35;
            {var subQ0=sQuery(id+"F0.wireOp",EDGE,"E11.36.0");Q35=makeQuery(id+"F0.imprint","IMPRINT",FACE,{"disambiguationData":[TD([[makeQuery(id+"F0.imprint","IMPRINT",EDGE,{"derivedFrom":subQ0}),1.0]])]});}
            var Q36;
            {var subQ0=sQuery(id+"F0.wireOp",EDGE,"E11.37.0");Q36=makeQuery(id+"F0.imprint","IMPRINT",FACE,{"disambiguationData":[TD([[makeQuery(id+"F0.imprint","IMPRINT",EDGE,{"derivedFrom":subQ0}),1.0]])]});}
            var Q37;
            {var subQ0=sQuery(id+"F0.wireOp",EDGE,"E11.38.0");Q37=makeQuery(id+"F0.imprint","IMPRINT",FACE,{"disambiguationData":[TD([[makeQuery(id+"F0.imprint","IMPRINT",EDGE,{"derivedFrom":subQ0}),1.0]])]});}
            var Q38;
            {var subQ0=sQuery(id+"F0.wireOp",EDGE,"E11.39.0");Q38=makeQuery(id+"F0.imprint","IMPRINT",FACE,{"disambiguationData":[TD([[makeQuery(id+"F0.imprint","IMPRINT",EDGE,{"derivedFrom":subQ0}),1.0]])]});}
            var Q39;
            {var subQ0=sQuery(id+"F0.wireOp",EDGE,"E11.40.0");Q39=makeQuery(id+"F0.imprint","IMPRINT",FACE,{"disambiguationData":[TD([[makeQuery(id+"F0.imprint","IMPRINT",EDGE,{"derivedFrom":subQ0}),1.0]])]});}
            var Q40;
            {var subQ1=sQuery(id+"F0.wireOp",EDGE,"E11.41.0");Q40=makeQuery(id+"F0.imprint","IMPRINT",FACE,{"disambiguationData":[TD([[makeQuery(id+"F0.imprint","IMPRINT",EDGE,{"derivedFrom":subQ1}),1.0]])]});}
            var Q41;
            {var subQ0=sQuery(id+"F0.wireOp",EDGE,"E11.42.0");Q41=makeQuery(id+"F0.imprint","IMPRINT",FACE,{"disambiguationData":[TD([[makeQuery(id+"F0.imprint","IMPRINT",EDGE,{"derivedFrom":subQ0}),1.0]])]});}
            var Q42;
            {var subQ0=sQuery(id+"F0.wireOp",EDGE,"E11.43.0");Q42=makeQuery(id+"F0.imprint","IMPRINT",FACE,{"disambiguationData":[TD([[makeQuery(id+"F0.imprint","IMPRINT",EDGE,{"derivedFrom":subQ0}),1.0]])]});}
            var Q43;
            {var subQ0=sQuery(id+"F0.wireOp",EDGE,"E11.44.0");Q43=makeQuery(id+"F0.imprint","IMPRINT",FACE,{"disambiguationData":[TD([[makeQuery(id+"F0.imprint","IMPRINT",EDGE,{"derivedFrom":subQ0}),1.0]])]});}
            var Q44;
            {var subQ0=sQuery(id+"F0.wireOp",EDGE,"E11.45.0");Q44=makeQuery(id+"F0.imprint","IMPRINT",FACE,{"disambiguationData":[TD([[makeQuery(id+"F0.imprint","IMPRINT",EDGE,{"derivedFrom":subQ0}),1.0]])]});}
            var Q45;
            {var subQ0=sQuery(id+"F0.wireOp",EDGE,"E11.46.0");Q45=makeQuery(id+"F0.imprint","IMPRINT",FACE,{"disambiguationData":[TD([[makeQuery(id+"F0.imprint","IMPRINT",EDGE,{"derivedFrom":subQ0}),1.0]])]});}
            var Q46;
            {var subQ0=sQuery(id+"F0.wireOp",EDGE,"E11.47.0");Q46=makeQuery(id+"F0.imprint","IMPRINT",FACE,{"disambiguationData":[TD([[makeQuery(id+"F0.imprint","IMPRINT",EDGE,{"derivedFrom":subQ0}),1.0]])]});}
            var Q47;
            {var subQ0=sQuery(id+"F0.wireOp",EDGE,"E11.48.0");Q47=makeQuery(id+"F0.imprint","IMPRINT",FACE,{"disambiguationData":[TD([[makeQuery(id+"F0.imprint","IMPRINT",EDGE,{"derivedFrom":subQ0}),1.0]])]});}
            var Q48;
            {var subQ1=sQuery(id+"F0.wireOp",EDGE,"E11.49.0");Q48=makeQuery(id+"F0.imprint","IMPRINT",FACE,{"disambiguationData":[TD([[makeQuery(id+"F0.imprint","IMPRINT",EDGE,{"derivedFrom":subQ1}),1.0]])]});}
            var Q49;
            {var subQ0=sQuery(id+"F0.wireOp",EDGE,"E11.50.0");Q49=makeQuery(id+"F0.imprint","IMPRINT",FACE,{"disambiguationData":[TD([[makeQuery(id+"F0.imprint","IMPRINT",EDGE,{"derivedFrom":subQ0}),1.0]])]});}
            var Q50;
            {var subQ0=sQuery(id+"F0.wireOp",EDGE,"E11.51.0");Q50=makeQuery(id+"F0.imprint","IMPRINT",FACE,{"disambiguationData":[TD([[makeQuery(id+"F0.imprint","IMPRINT",EDGE,{"derivedFrom":subQ0}),1.0]])]});}
            var Q51;
            {var subQ0=sQuery(id+"F0.wireOp",EDGE,"E11.52.0");Q51=makeQuery(id+"F0.imprint","IMPRINT",FACE,{"disambiguationData":[TD([[makeQuery(id+"F0.imprint","IMPRINT",EDGE,{"derivedFrom":subQ0}),1.0]])]});}
            var Q52;
            {var subQ0=sQuery(id+"F0.wireOp",EDGE,"E11.53.0");Q52=makeQuery(id+"F0.imprint","IMPRINT",FACE,{"disambiguationData":[TD([[makeQuery(id+"F0.imprint","IMPRINT",EDGE,{"derivedFrom":subQ0}),1.0]])]});}
            var Q53;
            {var subQ0=sQuery(id+"F0.wireOp",EDGE,"E11.54.0");Q53=makeQuery(id+"F0.imprint","IMPRINT",FACE,{"disambiguationData":[TD([[makeQuery(id+"F0.imprint","IMPRINT",EDGE,{"derivedFrom":subQ0}),1.0]])]});}
            var Q54;
            {var subQ0=sQuery(id+"F0.wireOp",EDGE,"E11.55.0");Q54=makeQuery(id+"F0.imprint","IMPRINT",FACE,{"disambiguationData":[TD([[makeQuery(id+"F0.imprint","IMPRINT",EDGE,{"derivedFrom":subQ0}),1.0]])]});}
            var Q55;
            {var subQ1=sQuery(id+"F0.wireOp",EDGE,"E11.56.0");Q55=makeQuery(id+"F0.imprint","IMPRINT",FACE,{"disambiguationData":[TD([[makeQuery(id+"F0.imprint","IMPRINT",EDGE,{"derivedFrom":subQ1}),1.0]])]});}
            var Q56;
            {var subQ0=sQuery(id+"F0.wireOp",EDGE,"E11.57.0");Q56=makeQuery(id+"F0.imprint","IMPRINT",FACE,{"disambiguationData":[TD([[makeQuery(id+"F0.imprint","IMPRINT",EDGE,{"derivedFrom":subQ0}),1.0]])]});}
            var Q57;
            {var subQ0=sQuery(id+"F0.wireOp",EDGE,"E11.58.0");Q57=makeQuery(id+"F0.imprint","IMPRINT",FACE,{"disambiguationData":[TD([[makeQuery(id+"F0.imprint","IMPRINT",EDGE,{"derivedFrom":subQ0}),1.0]])]});}
            var Q58;
            {var subQ0=sQuery(id+"F0.wireOp",EDGE,"E11.59.0");Q58=makeQuery(id+"F0.imprint","IMPRINT",FACE,{"disambiguationData":[TD([[makeQuery(id+"F0.imprint","IMPRINT",EDGE,{"derivedFrom":subQ0}),1.0]])]});}
            var Q59;
            {var subQ0=sQuery(id+"F0.wireOp",EDGE,"E11.60.0");Q59=makeQuery(id+"F0.imprint","IMPRINT",FACE,{"disambiguationData":[TD([[makeQuery(id+"F0.imprint","IMPRINT",EDGE,{"derivedFrom":subQ0}),1.0]])]});}
            var Q60;
            {var subQ0=sQuery(id+"F0.wireOp",EDGE,"E11.61.0");Q60=makeQuery(id+"F0.imprint","IMPRINT",FACE,{"disambiguationData":[TD([[makeQuery(id+"F0.imprint","IMPRINT",EDGE,{"derivedFrom":subQ0}),1.0]])]});}
            var Q61;
            {var subQ0=sQuery(id+"F0.wireOp",EDGE,"E11.62.0");Q61=makeQuery(id+"F0.imprint","IMPRINT",FACE,{"disambiguationData":[TD([[makeQuery(id+"F0.imprint","IMPRINT",EDGE,{"derivedFrom":subQ0}),1.0]])]});}
            var Q62;
            {var subQ0=sQuery(id+"F0.wireOp",EDGE,"E11.63.0");Q62=makeQuery(id+"F0.imprint","IMPRINT",FACE,{"disambiguationData":[TD([[makeQuery(id+"F0.imprint","IMPRINT",EDGE,{"derivedFrom":subQ0}),1.0]])]});}
            var Q63;
            {var subQ1=sQuery(id+"F0.wireOp",EDGE,"E11.64.0");Q63=makeQuery(id+"F0.imprint","IMPRINT",FACE,{"disambiguationData":[TD([[makeQuery(id+"F0.imprint","IMPRINT",EDGE,{"derivedFrom":subQ1}),1.0]])]});}
            var Q64;
            {var subQ0=sQuery(id+"F0.wireOp",EDGE,"E11.65.0");Q64=makeQuery(id+"F0.imprint","IMPRINT",FACE,{"disambiguationData":[TD([[makeQuery(id+"F0.imprint","IMPRINT",EDGE,{"derivedFrom":subQ0}),1.0]])]});}
            var Q65;
            {var subQ0=sQuery(id+"F0.wireOp",EDGE,"E11.66.0");Q65=makeQuery(id+"F0.imprint","IMPRINT",FACE,{"disambiguationData":[TD([[makeQuery(id+"F0.imprint","IMPRINT",EDGE,{"derivedFrom":subQ0}),1.0]])]});}
            var Q66;
            {var subQ0=sQuery(id+"F0.wireOp",EDGE,"E11.67.0");Q66=makeQuery(id+"F0.imprint","IMPRINT",FACE,{"disambiguationData":[TD([[makeQuery(id+"F0.imprint","IMPRINT",EDGE,{"derivedFrom":subQ0}),1.0]])]});}
            var Q67;
            {var subQ0=sQuery(id+"F0.wireOp",EDGE,"E11.68.0");Q67=makeQuery(id+"F0.imprint","IMPRINT",FACE,{"disambiguationData":[TD([[makeQuery(id+"F0.imprint","IMPRINT",EDGE,{"derivedFrom":subQ0}),1.0]])]});}
            var Q68;
            {var subQ0=sQuery(id+"F0.wireOp",EDGE,"E11.69.0");Q68=makeQuery(id+"F0.imprint","IMPRINT",FACE,{"disambiguationData":[TD([[makeQuery(id+"F0.imprint","IMPRINT",EDGE,{"derivedFrom":subQ0}),1.0]])]});}
            var Q69;
            {var subQ0=sQuery(id+"F0.wireOp",EDGE,"E11.70.0");Q69=makeQuery(id+"F0.imprint","IMPRINT",FACE,{"disambiguationData":[TD([[makeQuery(id+"F0.imprint","IMPRINT",EDGE,{"derivedFrom":subQ0}),1.0]])]});}
            var Q70;
            {var subQ0=sQuery(id+"F0.wireOp",EDGE,"E11.71.0");Q70=makeQuery(id+"F0.imprint","IMPRINT",FACE,{"disambiguationData":[TD([[makeQuery(id+"F0.imprint","IMPRINT",EDGE,{"derivedFrom":subQ0}),1.0]])]});}
            var Q71;
            {var subQ0=sQuery(id+"F0.wireOp",EDGE,"E11.72.0");Q71=makeQuery(id+"F0.imprint","IMPRINT",FACE,{"disambiguationData":[TD([[makeQuery(id+"F0.imprint","IMPRINT",EDGE,{"derivedFrom":subQ0}),1.0]])]});}
            var Q72;
            {var subQ0=sQuery(id+"F0.wireOp",EDGE,"E11.73.0");Q72=makeQuery(id+"F0.imprint","IMPRINT",FACE,{"disambiguationData":[TD([[makeQuery(id+"F0.imprint","IMPRINT",EDGE,{"derivedFrom":subQ0}),1.0]])]});}
            var Q73;
            {var subQ0=sQuery(id+"F0.wireOp",EDGE,"E11.74.0");Q73=makeQuery(id+"F0.imprint","IMPRINT",FACE,{"disambiguationData":[TD([[makeQuery(id+"F0.imprint","IMPRINT",EDGE,{"derivedFrom":subQ0}),1.0]])]});}
            var Q74;
            {var subQ0=sQuery(id+"F0.wireOp",EDGE,"E11.75.0");Q74=makeQuery(id+"F0.imprint","IMPRINT",FACE,{"disambiguationData":[TD([[makeQuery(id+"F0.imprint","IMPRINT",EDGE,{"derivedFrom":subQ0}),1.0]])]});}
            var Q75;
            {var subQ0=sQuery(id+"F0.wireOp",EDGE,"E11.76.0");Q75=makeQuery(id+"F0.imprint","IMPRINT",FACE,{"disambiguationData":[TD([[makeQuery(id+"F0.imprint","IMPRINT",EDGE,{"derivedFrom":subQ0}),1.0]])]});}
            var Q76;
            {var subQ0=sQuery(id+"F0.wireOp",EDGE,"E11.77.0");Q76=makeQuery(id+"F0.imprint","IMPRINT",FACE,{"disambiguationData":[TD([[makeQuery(id+"F0.imprint","IMPRINT",EDGE,{"derivedFrom":subQ0}),1.0]])]});}
            var Q77;
            {var subQ0=sQuery(id+"F0.wireOp",EDGE,"E11.78.0");Q77=makeQuery(id+"F0.imprint","IMPRINT",FACE,{"disambiguationData":[TD([[makeQuery(id+"F0.imprint","IMPRINT",EDGE,{"derivedFrom":subQ0}),1.0]])]});}
            var Q78;
            {var subQ0=sQuery(id+"F0.wireOp",EDGE,"E11.79.0");Q78=makeQuery(id+"F0.imprint","IMPRINT",FACE,{"disambiguationData":[TD([[makeQuery(id+"F0.imprint","IMPRINT",EDGE,{"derivedFrom":subQ0}),1.0]])]});}
            var Q79;
            {var subQ0=sQuery(id+"F0.wireOp",EDGE,"E11.80.0");Q79=makeQuery(id+"F0.imprint","IMPRINT",FACE,{"disambiguationData":[TD([[makeQuery(id+"F0.imprint","IMPRINT",EDGE,{"derivedFrom":subQ0}),1.0]])]});}
            var Q80;
            {var subQ1=sQuery(id+"F0.wireOp",EDGE,"E11.81.0");Q80=makeQuery(id+"F0.imprint","IMPRINT",FACE,{"disambiguationData":[TD([[makeQuery(id+"F0.imprint","IMPRINT",EDGE,{"derivedFrom":subQ1}),1.0]])]});}
            var Q81;
            {var subQ0=sQuery(id+"F0.wireOp",EDGE,"E11.82.0");Q81=makeQuery(id+"F0.imprint","IMPRINT",FACE,{"disambiguationData":[TD([[makeQuery(id+"F0.imprint","IMPRINT",EDGE,{"derivedFrom":subQ0}),1.0]])]});}
            var Q82;
            {var subQ0=sQuery(id+"F0.wireOp",EDGE,"E11.83.0");Q82=makeQuery(id+"F0.imprint","IMPRINT",FACE,{"disambiguationData":[TD([[makeQuery(id+"F0.imprint","IMPRINT",EDGE,{"derivedFrom":subQ0}),1.0]])]});}
            var Q83;
            {var subQ0=sQuery(id+"F0.wireOp",EDGE,"E11.84.0");Q83=makeQuery(id+"F0.imprint","IMPRINT",FACE,{"disambiguationData":[TD([[makeQuery(id+"F0.imprint","IMPRINT",EDGE,{"derivedFrom":subQ0}),1.0]])]});}
            var Q84;
            {var subQ0=sQuery(id+"F0.wireOp",EDGE,"E11.85.0");Q84=makeQuery(id+"F0.imprint","IMPRINT",FACE,{"disambiguationData":[TD([[makeQuery(id+"F0.imprint","IMPRINT",EDGE,{"derivedFrom":subQ0}),1.0]])]});}
            var Q85;
            {var subQ0=sQuery(id+"F0.wireOp",EDGE,"E11.86.0");Q85=makeQuery(id+"F0.imprint","IMPRINT",FACE,{"disambiguationData":[TD([[makeQuery(id+"F0.imprint","IMPRINT",EDGE,{"derivedFrom":subQ0}),1.0]])]});}
            var Q86;
            {var subQ0=sQuery(id+"F0.wireOp",EDGE,"E11.87.0");Q86=makeQuery(id+"F0.imprint","IMPRINT",FACE,{"disambiguationData":[TD([[makeQuery(id+"F0.imprint","IMPRINT",EDGE,{"derivedFrom":subQ0}),1.0]])]});}
            var Q87;
            {var subQ1=sQuery(id+"F0.wireOp",EDGE,"E11.88.0");Q87=makeQuery(id+"F0.imprint","IMPRINT",FACE,{"disambiguationData":[TD([[makeQuery(id+"F0.imprint","IMPRINT",EDGE,{"derivedFrom":subQ1}),1.0]])]});}
            var Q88;
            {var subQ0=sQuery(id+"F0.wireOp",EDGE,"E11.89.0");Q88=makeQuery(id+"F0.imprint","IMPRINT",FACE,{"disambiguationData":[TD([[makeQuery(id+"F0.imprint","IMPRINT",EDGE,{"derivedFrom":subQ0}),1.0]])]});}
            var Q89;
            {var subQ0=sQuery(id+"F0.wireOp",EDGE,"E11.90.0");Q89=makeQuery(id+"F0.imprint","IMPRINT",FACE,{"disambiguationData":[TD([[makeQuery(id+"F0.imprint","IMPRINT",EDGE,{"derivedFrom":subQ0}),1.0]])]});}
            var Q90;
            {var subQ0=sQuery(id+"F0.wireOp",EDGE,"E11.91.0");Q90=makeQuery(id+"F0.imprint","IMPRINT",FACE,{"disambiguationData":[TD([[makeQuery(id+"F0.imprint","IMPRINT",EDGE,{"derivedFrom":subQ0}),1.0]])]});}
            var Q91;
            {var subQ0=sQuery(id+"F0.wireOp",EDGE,"E11.92.0");Q91=makeQuery(id+"F0.imprint","IMPRINT",FACE,{"disambiguationData":[TD([[makeQuery(id+"F0.imprint","IMPRINT",EDGE,{"derivedFrom":subQ0}),1.0]])]});}
            var Q92;
            {var subQ0=sQuery(id+"F0.wireOp",EDGE,"E11.93.0");Q92=makeQuery(id+"F0.imprint","IMPRINT",FACE,{"disambiguationData":[TD([[makeQuery(id+"F0.imprint","IMPRINT",EDGE,{"derivedFrom":subQ0}),1.0]])]});}
            var Q93;
            {var subQ0=sQuery(id+"F0.wireOp",EDGE,"E11.94.0");Q93=makeQuery(id+"F0.imprint","IMPRINT",FACE,{"disambiguationData":[TD([[makeQuery(id+"F0.imprint","IMPRINT",EDGE,{"derivedFrom":subQ0}),1.0]])]});}
            var Q94;
            {var subQ0=sQuery(id+"F0.wireOp",EDGE,"E11.95.0");Q94=makeQuery(id+"F0.imprint","IMPRINT",FACE,{"disambiguationData":[TD([[makeQuery(id+"F0.imprint","IMPRINT",EDGE,{"derivedFrom":subQ0}),1.0]])]});}
            var Q95;
            {var subQ1=sQuery(id+"F0.wireOp",EDGE,"E11.96.0");Q95=makeQuery(id+"F0.imprint","IMPRINT",FACE,{"disambiguationData":[TD([[makeQuery(id+"F0.imprint","IMPRINT",EDGE,{"derivedFrom":subQ1}),1.0]])]});}
            var Q96;
            {var subQ0=sQuery(id+"F0.wireOp",EDGE,"E11.97.0");Q96=makeQuery(id+"F0.imprint","IMPRINT",FACE,{"disambiguationData":[TD([[makeQuery(id+"F0.imprint","IMPRINT",EDGE,{"derivedFrom":subQ0}),1.0]])]});}
            var Q97;
            {var subQ0=sQuery(id+"F0.wireOp",EDGE,"E11.98.0");Q97=makeQuery(id+"F0.imprint","IMPRINT",FACE,{"disambiguationData":[TD([[makeQuery(id+"F0.imprint","IMPRINT",EDGE,{"derivedFrom":subQ0}),1.0]])]});}
            var Q98;
            {var subQ0=sQuery(id+"F0.wireOp",EDGE,"E11.99.0");Q98=makeQuery(id+"F0.imprint","IMPRINT",FACE,{"disambiguationData":[TD([[makeQuery(id+"F0.imprint","IMPRINT",EDGE,{"derivedFrom":subQ0}),1.0]])]});}
            var Q99;
            {var subQ0=sQuery(id+"F0.wireOp",EDGE,"E11.100.0");Q99=makeQuery(id+"F0.imprint","IMPRINT",FACE,{"disambiguationData":[TD([[makeQuery(id+"F0.imprint","IMPRINT",EDGE,{"derivedFrom":subQ0}),1.0]])]});}
            var Q100;
            {var subQ0=sQuery(id+"F0.wireOp",EDGE,"E11.101.0");Q100=makeQuery(id+"F0.imprint","IMPRINT",FACE,{"disambiguationData":[TD([[makeQuery(id+"F0.imprint","IMPRINT",EDGE,{"derivedFrom":subQ0}),1.0]])]});}
            var Q101;
            {var subQ0=sQuery(id+"F0.wireOp",EDGE,"E11.102.0");Q101=makeQuery(id+"F0.imprint","IMPRINT",FACE,{"disambiguationData":[TD([[makeQuery(id+"F0.imprint","IMPRINT",EDGE,{"derivedFrom":subQ0}),1.0]])]});}
            var Q102;
            {var subQ0=sQuery(id+"F0.wireOp",EDGE,"E11.103.0");Q102=makeQuery(id+"F0.imprint","IMPRINT",FACE,{"disambiguationData":[TD([[makeQuery(id+"F0.imprint","IMPRINT",EDGE,{"derivedFrom":subQ0}),1.0]])]});}
            var Q103;
            {var subQ0=sQuery(id+"F0.wireOp",EDGE,"E11.104.0");Q103=makeQuery(id+"F0.imprint","IMPRINT",FACE,{"disambiguationData":[TD([[makeQuery(id+"F0.imprint","IMPRINT",EDGE,{"derivedFrom":subQ0}),1.0]])]});}
            var Q104;
            {var subQ1=sQuery(id+"F0.wireOp",EDGE,"E11.105.0");Q104=makeQuery(id+"F0.imprint","IMPRINT",FACE,{"disambiguationData":[TD([[makeQuery(id+"F0.imprint","IMPRINT",EDGE,{"derivedFrom":subQ1}),1.0]])]});}
            var Q105;
            {var subQ0=sQuery(id+"F0.wireOp",EDGE,"E11.106.0");Q105=makeQuery(id+"F0.imprint","IMPRINT",FACE,{"disambiguationData":[TD([[makeQuery(id+"F0.imprint","IMPRINT",EDGE,{"derivedFrom":subQ0}),1.0]])]});}
            var Q106;
            {var subQ0=sQuery(id+"F0.wireOp",EDGE,"E11.107.0");Q106=makeQuery(id+"F0.imprint","IMPRINT",FACE,{"disambiguationData":[TD([[makeQuery(id+"F0.imprint","IMPRINT",EDGE,{"derivedFrom":subQ0}),1.0]])]});}
            var Q107;
            {var subQ0=sQuery(id+"F0.wireOp",EDGE,"E11.108.0");Q107=makeQuery(id+"F0.imprint","IMPRINT",FACE,{"disambiguationData":[TD([[makeQuery(id+"F0.imprint","IMPRINT",EDGE,{"derivedFrom":subQ0}),1.0]])]});}
            var Q108;
            {var subQ0=sQuery(id+"F0.wireOp",EDGE,"E11.109.0");Q108=makeQuery(id+"F0.imprint","IMPRINT",FACE,{"disambiguationData":[TD([[makeQuery(id+"F0.imprint","IMPRINT",EDGE,{"derivedFrom":subQ0}),1.0]])]});}
            var Q109;
            {var subQ0=sQuery(id+"F0.wireOp",EDGE,"E11.110.0");Q109=makeQuery(id+"F0.imprint","IMPRINT",FACE,{"disambiguationData":[TD([[makeQuery(id+"F0.imprint","IMPRINT",EDGE,{"derivedFrom":subQ0}),1.0]])]});}
            var Q110;
            {var subQ0=sQuery(id+"F0.wireOp",EDGE,"E11.111.0");Q110=makeQuery(id+"F0.imprint","IMPRINT",FACE,{"disambiguationData":[TD([[makeQuery(id+"F0.imprint","IMPRINT",EDGE,{"derivedFrom":subQ0}),1.0]])]});}
            var Q111;
            {var subQ0=sQuery(id+"F0.wireOp",EDGE,"E11.112.0");Q111=makeQuery(id+"F0.imprint","IMPRINT",FACE,{"disambiguationData":[TD([[makeQuery(id+"F0.imprint","IMPRINT",EDGE,{"derivedFrom":subQ0}),1.0]])]});}
            var Q112;
            {var subQ1=sQuery(id+"F0.wireOp",EDGE,"E11.113.0");Q112=makeQuery(id+"F0.imprint","IMPRINT",FACE,{"disambiguationData":[TD([[makeQuery(id+"F0.imprint","IMPRINT",EDGE,{"derivedFrom":subQ1}),1.0]])]});}
            var Q113;
            {var subQ0=sQuery(id+"F0.wireOp",EDGE,"E11.114.0");Q113=makeQuery(id+"F0.imprint","IMPRINT",FACE,{"disambiguationData":[TD([[makeQuery(id+"F0.imprint","IMPRINT",EDGE,{"derivedFrom":subQ0}),1.0]])]});}
            var Q114;
            {var subQ0=sQuery(id+"F0.wireOp",EDGE,"E11.115.0");Q114=makeQuery(id+"F0.imprint","IMPRINT",FACE,{"disambiguationData":[TD([[makeQuery(id+"F0.imprint","IMPRINT",EDGE,{"derivedFrom":subQ0}),1.0]])]});}
            var Q115;
            {var subQ0=sQuery(id+"F0.wireOp",EDGE,"E11.116.0");Q115=makeQuery(id+"F0.imprint","IMPRINT",FACE,{"disambiguationData":[TD([[makeQuery(id+"F0.imprint","IMPRINT",EDGE,{"derivedFrom":subQ0}),1.0]])]});}
            var Q116;
            {var subQ0=sQuery(id+"F0.wireOp",EDGE,"E11.117.0");Q116=makeQuery(id+"F0.imprint","IMPRINT",FACE,{"disambiguationData":[TD([[makeQuery(id+"F0.imprint","IMPRINT",EDGE,{"derivedFrom":subQ0}),1.0]])]});}
            var Q117;
            {var subQ0=sQuery(id+"F0.wireOp",EDGE,"E11.118.0");Q117=makeQuery(id+"F0.imprint","IMPRINT",FACE,{"disambiguationData":[TD([[makeQuery(id+"F0.imprint","IMPRINT",EDGE,{"derivedFrom":subQ0}),1.0]])]});}
            var Q118;
            {var subQ0=sQuery(id+"F0.wireOp",EDGE,"E11.119.0");Q118=makeQuery(id+"F0.imprint","IMPRINT",FACE,{"disambiguationData":[TD([[makeQuery(id+"F0.imprint","IMPRINT",EDGE,{"derivedFrom":subQ0}),1.0]])]});}
            var Q119;
            {var subQ1=sQuery(id+"F0.wireOp",EDGE,"E11.120.0");Q119=makeQuery(id+"F0.imprint","IMPRINT",FACE,{"disambiguationData":[TD([[makeQuery(id+"F0.imprint","IMPRINT",EDGE,{"derivedFrom":subQ1}),1.0]])]});}
            var Q120;
            {var subQ0=sQuery(id+"F0.wireOp",EDGE,"E11.121.0");Q120=makeQuery(id+"F0.imprint","IMPRINT",FACE,{"disambiguationData":[TD([[makeQuery(id+"F0.imprint","IMPRINT",EDGE,{"derivedFrom":subQ0}),1.0]])]});}
            var Q121;
            {var subQ0=sQuery(id+"F0.wireOp",EDGE,"E11.122.0");Q121=makeQuery(id+"F0.imprint","IMPRINT",FACE,{"disambiguationData":[TD([[makeQuery(id+"F0.imprint","IMPRINT",EDGE,{"derivedFrom":subQ0}),1.0]])]});}
            var Q122;
            {var subQ0=sQuery(id+"F0.wireOp",EDGE,"E11.123.0");Q122=makeQuery(id+"F0.imprint","IMPRINT",FACE,{"disambiguationData":[TD([[makeQuery(id+"F0.imprint","IMPRINT",EDGE,{"derivedFrom":subQ0}),1.0]])]});}
            var Q123;
            {var subQ0=sQuery(id+"F0.wireOp",EDGE,"E11.124.0");Q123=makeQuery(id+"F0.imprint","IMPRINT",FACE,{"disambiguationData":[TD([[makeQuery(id+"F0.imprint","IMPRINT",EDGE,{"derivedFrom":subQ0}),1.0]])]});}
            var Q124;
            {var subQ0=sQuery(id+"F0.wireOp",EDGE,"E11.125.0");Q124=makeQuery(id+"F0.imprint","IMPRINT",FACE,{"disambiguationData":[TD([[makeQuery(id+"F0.imprint","IMPRINT",EDGE,{"derivedFrom":subQ0}),1.0]])]});}
            var Q125;
            {var subQ0=sQuery(id+"F0.wireOp",EDGE,"E11.126.0");Q125=makeQuery(id+"F0.imprint","IMPRINT",FACE,{"disambiguationData":[TD([[makeQuery(id+"F0.imprint","IMPRINT",EDGE,{"derivedFrom":subQ0}),1.0]])]});}
            var Q126;
            {var subQ0=sQuery(id+"F0.wireOp",EDGE,"E11.127.0");Q126=makeQuery(id+"F0.imprint","IMPRINT",FACE,{"disambiguationData":[TD([[makeQuery(id+"F0.imprint","IMPRINT",EDGE,{"derivedFrom":subQ0}),1.0]])]});}
            var Q127;
            {var subQ0=sQuery(id+"F0.wireOp",EDGE,"E11.128.0");Q127=makeQuery(id+"F0.imprint","IMPRINT",FACE,{"disambiguationData":[TD([[makeQuery(id+"F0.imprint","IMPRINT",EDGE,{"derivedFrom":subQ0}),1.0]])]});}
            var Q128;
            {var subQ0=sQuery(id+"F0.wireOp",EDGE,"E11.129.0");Q128=makeQuery(id+"F0.imprint","IMPRINT",FACE,{"disambiguationData":[TD([[makeQuery(id+"F0.imprint","IMPRINT",EDGE,{"derivedFrom":subQ0}),1.0]])]});}
            var Q129;
            {var subQ0=sQuery(id+"F0.wireOp",EDGE,"E11.130.0");Q129=makeQuery(id+"F0.imprint","IMPRINT",FACE,{"disambiguationData":[TD([[makeQuery(id+"F0.imprint","IMPRINT",EDGE,{"derivedFrom":subQ0}),1.0]])]});}
            var Q130;
            {var subQ0=sQuery(id+"F0.wireOp",EDGE,"E11.131.0");Q130=makeQuery(id+"F0.imprint","IMPRINT",FACE,{"disambiguationData":[TD([[makeQuery(id+"F0.imprint","IMPRINT",EDGE,{"derivedFrom":subQ0}),1.0]])]});}
            var Q131;
            {var subQ0=sQuery(id+"F0.wireOp",EDGE,"E11.132.0");Q131=makeQuery(id+"F0.imprint","IMPRINT",FACE,{"disambiguationData":[TD([[makeQuery(id+"F0.imprint","IMPRINT",EDGE,{"derivedFrom":subQ0}),1.0]])]});}
            var Q132;
            {var subQ0=sQuery(id+"F0.wireOp",EDGE,"E11.133.0");Q132=makeQuery(id+"F0.imprint","IMPRINT",FACE,{"disambiguationData":[TD([[makeQuery(id+"F0.imprint","IMPRINT",EDGE,{"derivedFrom":subQ0}),1.0]])]});}
            var Q133;
            {var subQ0=sQuery(id+"F0.wireOp",EDGE,"E11.134.0");Q133=makeQuery(id+"F0.imprint","IMPRINT",FACE,{"disambiguationData":[TD([[makeQuery(id+"F0.imprint","IMPRINT",EDGE,{"derivedFrom":subQ0}),1.0]])]});}
            var Q134;
            {var subQ0=sQuery(id+"F0.wireOp",EDGE,"E11.135.0");Q134=makeQuery(id+"F0.imprint","IMPRINT",FACE,{"disambiguationData":[TD([[makeQuery(id+"F0.imprint","IMPRINT",EDGE,{"derivedFrom":subQ0}),1.0]])]});}
            var Q135;
            {var subQ0=sQuery(id+"F0.wireOp",EDGE,"E11.136.0");Q135=makeQuery(id+"F0.imprint","IMPRINT",FACE,{"disambiguationData":[TD([[makeQuery(id+"F0.imprint","IMPRINT",EDGE,{"derivedFrom":subQ0}),1.0]])]});}
            var Q136;
            {var subQ1=sQuery(id+"F0.wireOp",EDGE,"E11.137.0");Q136=makeQuery(id+"F0.imprint","IMPRINT",FACE,{"disambiguationData":[TD([[makeQuery(id+"F0.imprint","IMPRINT",EDGE,{"derivedFrom":subQ1}),1.0]])]});}
            var Q137;
            {var subQ0=sQuery(id+"F0.wireOp",EDGE,"E11.138.0");Q137=makeQuery(id+"F0.imprint","IMPRINT",FACE,{"disambiguationData":[TD([[makeQuery(id+"F0.imprint","IMPRINT",EDGE,{"derivedFrom":subQ0}),1.0]])]});}
            var Q138;
            {var subQ0=sQuery(id+"F0.wireOp",EDGE,"E11.139.0");Q138=makeQuery(id+"F0.imprint","IMPRINT",FACE,{"disambiguationData":[TD([[makeQuery(id+"F0.imprint","IMPRINT",EDGE,{"derivedFrom":subQ0}),1.0]])]});}
            var Q139;
            {var subQ0=sQuery(id+"F0.wireOp",EDGE,"E11.140.0");Q139=makeQuery(id+"F0.imprint","IMPRINT",FACE,{"disambiguationData":[TD([[makeQuery(id+"F0.imprint","IMPRINT",EDGE,{"derivedFrom":subQ0}),1.0]])]});}
            var Q140;
            {var subQ0=sQuery(id+"F0.wireOp",EDGE,"E11.141.0");Q140=makeQuery(id+"F0.imprint","IMPRINT",FACE,{"disambiguationData":[TD([[makeQuery(id+"F0.imprint","IMPRINT",EDGE,{"derivedFrom":subQ0}),1.0]])]});}
            var Q141;
            {var subQ0=sQuery(id+"F0.wireOp",EDGE,"E11.142.0");Q141=makeQuery(id+"F0.imprint","IMPRINT",FACE,{"disambiguationData":[TD([[makeQuery(id+"F0.imprint","IMPRINT",EDGE,{"derivedFrom":subQ0}),1.0]])]});}
            var Q142;
            {var subQ0=sQuery(id+"F0.wireOp",EDGE,"E11.143.0");Q142=makeQuery(id+"F0.imprint","IMPRINT",FACE,{"disambiguationData":[TD([[makeQuery(id+"F0.imprint","IMPRINT",EDGE,{"derivedFrom":subQ0}),1.0]])]});}
            var Q143;
            {var subQ0=sQuery(id+"F0.wireOp",EDGE,"E11.144.0");Q143=makeQuery(id+"F0.imprint","IMPRINT",FACE,{"disambiguationData":[TD([[makeQuery(id+"F0.imprint","IMPRINT",EDGE,{"derivedFrom":subQ0}),1.0]])]});}
            var Q144;
            {var subQ1=sQuery(id+"F0.wireOp",EDGE,"E11.145.0");Q144=makeQuery(id+"F0.imprint","IMPRINT",FACE,{"disambiguationData":[TD([[makeQuery(id+"F0.imprint","IMPRINT",EDGE,{"derivedFrom":subQ1}),1.0]])]});}
            var Q145;
            {var subQ0=sQuery(id+"F0.wireOp",EDGE,"E11.146.0");Q145=makeQuery(id+"F0.imprint","IMPRINT",FACE,{"disambiguationData":[TD([[makeQuery(id+"F0.imprint","IMPRINT",EDGE,{"derivedFrom":subQ0}),1.0]])]});}
            var Q146;
            {var subQ0=sQuery(id+"F0.wireOp",EDGE,"E11.147.0");Q146=makeQuery(id+"F0.imprint","IMPRINT",FACE,{"disambiguationData":[TD([[makeQuery(id+"F0.imprint","IMPRINT",EDGE,{"derivedFrom":subQ0}),1.0]])]});}
            var Q147;
            {var subQ0=sQuery(id+"F0.wireOp",EDGE,"E11.148.0");Q147=makeQuery(id+"F0.imprint","IMPRINT",FACE,{"disambiguationData":[TD([[makeQuery(id+"F0.imprint","IMPRINT",EDGE,{"derivedFrom":subQ0}),1.0]])]});}
            var Q148;
            {var subQ0=sQuery(id+"F0.wireOp",EDGE,"E11.149.0");Q148=makeQuery(id+"F0.imprint","IMPRINT",FACE,{"disambiguationData":[TD([[makeQuery(id+"F0.imprint","IMPRINT",EDGE,{"derivedFrom":subQ0}),1.0]])]});}
            var Q149;
            {var subQ0=sQuery(id+"F0.wireOp",EDGE,"E11.150.0");Q149=makeQuery(id+"F0.imprint","IMPRINT",FACE,{"disambiguationData":[TD([[makeQuery(id+"F0.imprint","IMPRINT",EDGE,{"derivedFrom":subQ0}),1.0]])]});}
            var Q150;
            {var subQ0=sQuery(id+"F0.wireOp",EDGE,"E11.151.0");Q150=makeQuery(id+"F0.imprint","IMPRINT",FACE,{"disambiguationData":[TD([[makeQuery(id+"F0.imprint","IMPRINT",EDGE,{"derivedFrom":subQ0}),1.0]])]});}
            var Q151;
            {var subQ1=sQuery(id+"F0.wireOp",EDGE,"E11.152.0");Q151=makeQuery(id+"F0.imprint","IMPRINT",FACE,{"disambiguationData":[TD([[makeQuery(id+"F0.imprint","IMPRINT",EDGE,{"derivedFrom":subQ1}),1.0]])]});}
            var Q152;
            {var subQ0=sQuery(id+"F0.wireOp",EDGE,"E11.153.0");Q152=makeQuery(id+"F0.imprint","IMPRINT",FACE,{"disambiguationData":[TD([[makeQuery(id+"F0.imprint","IMPRINT",EDGE,{"derivedFrom":subQ0}),1.0]])]});}
            var Q153;
            {var subQ0=sQuery(id+"F0.wireOp",EDGE,"E11.154.0");Q153=makeQuery(id+"F0.imprint","IMPRINT",FACE,{"disambiguationData":[TD([[makeQuery(id+"F0.imprint","IMPRINT",EDGE,{"derivedFrom":subQ0}),1.0]])]});}
            var Q154;
            {var subQ0=sQuery(id+"F0.wireOp",EDGE,"E11.155.0");Q154=makeQuery(id+"F0.imprint","IMPRINT",FACE,{"disambiguationData":[TD([[makeQuery(id+"F0.imprint","IMPRINT",EDGE,{"derivedFrom":subQ0}),1.0]])]});}
            var Q155;
            {var subQ0=sQuery(id+"F0.wireOp",EDGE,"E11.156.0");Q155=makeQuery(id+"F0.imprint","IMPRINT",FACE,{"disambiguationData":[TD([[makeQuery(id+"F0.imprint","IMPRINT",EDGE,{"derivedFrom":subQ0}),1.0]])]});}
            var Q156;
            {var subQ0=sQuery(id+"F0.wireOp",EDGE,"E11.157.0");Q156=makeQuery(id+"F0.imprint","IMPRINT",FACE,{"disambiguationData":[TD([[makeQuery(id+"F0.imprint","IMPRINT",EDGE,{"derivedFrom":subQ0}),1.0]])]});}
            var Q157;
            {var subQ0=sQuery(id+"F0.wireOp",EDGE,"E11.158.0");Q157=makeQuery(id+"F0.imprint","IMPRINT",FACE,{"disambiguationData":[TD([[makeQuery(id+"F0.imprint","IMPRINT",EDGE,{"derivedFrom":subQ0}),1.0]])]});}
            var Q158;
            {var subQ0=sQuery(id+"F0.wireOp",EDGE,"E11.159.0");Q158=makeQuery(id+"F0.imprint","IMPRINT",FACE,{"disambiguationData":[TD([[makeQuery(id+"F0.imprint","IMPRINT",EDGE,{"derivedFrom":subQ0}),1.0]])]});}
            var Q159;
            {var subQ1=sQuery(id+"F0.wireOp",EDGE,"E11.160.0");Q159=makeQuery(id+"F0.imprint","IMPRINT",FACE,{"disambiguationData":[TD([[makeQuery(id+"F0.imprint","IMPRINT",EDGE,{"derivedFrom":subQ1}),1.0]])]});}
            var Q160;
            {var subQ0=sQuery(id+"F0.wireOp",EDGE,"E11.161.0");Q160=makeQuery(id+"F0.imprint","IMPRINT",FACE,{"disambiguationData":[TD([[makeQuery(id+"F0.imprint","IMPRINT",EDGE,{"derivedFrom":subQ0}),1.0]])]});}
            var Q161;
            {var subQ0=sQuery(id+"F0.wireOp",EDGE,"E11.162.0");Q161=makeQuery(id+"F0.imprint","IMPRINT",FACE,{"disambiguationData":[TD([[makeQuery(id+"F0.imprint","IMPRINT",EDGE,{"derivedFrom":subQ0}),1.0]])]});}
            var Q162;
            {var subQ0=sQuery(id+"F0.wireOp",EDGE,"E11.163.0");Q162=makeQuery(id+"F0.imprint","IMPRINT",FACE,{"disambiguationData":[TD([[makeQuery(id+"F0.imprint","IMPRINT",EDGE,{"derivedFrom":subQ0}),1.0]])]});}
            var Q163;
            {var subQ0=sQuery(id+"F0.wireOp",EDGE,"E11.164.0");Q163=makeQuery(id+"F0.imprint","IMPRINT",FACE,{"disambiguationData":[TD([[makeQuery(id+"F0.imprint","IMPRINT",EDGE,{"derivedFrom":subQ0}),1.0]])]});}
            var Q164;
            {var subQ0=sQuery(id+"F0.wireOp",EDGE,"E11.165.0");Q164=makeQuery(id+"F0.imprint","IMPRINT",FACE,{"disambiguationData":[TD([[makeQuery(id+"F0.imprint","IMPRINT",EDGE,{"derivedFrom":subQ0}),1.0]])]});}
            var Q165;
            {var subQ0=sQuery(id+"F0.wireOp",EDGE,"E11.166.0");Q165=makeQuery(id+"F0.imprint","IMPRINT",FACE,{"disambiguationData":[TD([[makeQuery(id+"F0.imprint","IMPRINT",EDGE,{"derivedFrom":subQ0}),1.0]])]});}
            var Q166;
            {var subQ0=sQuery(id+"F0.wireOp",EDGE,"E11.167.0");Q166=makeQuery(id+"F0.imprint","IMPRINT",FACE,{"disambiguationData":[TD([[makeQuery(id+"F0.imprint","IMPRINT",EDGE,{"derivedFrom":subQ0}),1.0]])]});}
            var Q167;
            {var subQ0=sQuery(id+"F0.wireOp",EDGE,"E11.168.0");Q167=makeQuery(id+"F0.imprint","IMPRINT",FACE,{"disambiguationData":[TD([[makeQuery(id+"F0.imprint","IMPRINT",EDGE,{"derivedFrom":subQ0}),1.0]])]});}
            var Q168;
            {var subQ0=sQuery(id+"F0.wireOp",EDGE,"E11.169.0");Q168=makeQuery(id+"F0.imprint","IMPRINT",FACE,{"disambiguationData":[TD([[makeQuery(id+"F0.imprint","IMPRINT",EDGE,{"derivedFrom":subQ0}),1.0]])]});}
            var Q169;
            {var subQ0=sQuery(id+"F0.wireOp",EDGE,"E11.170.0");Q169=makeQuery(id+"F0.imprint","IMPRINT",FACE,{"disambiguationData":[TD([[makeQuery(id+"F0.imprint","IMPRINT",EDGE,{"derivedFrom":subQ0}),1.0]])]});}
            var Q170;
            {var subQ0=sQuery(id+"F0.wireOp",EDGE,"E11.171.0");Q170=makeQuery(id+"F0.imprint","IMPRINT",FACE,{"disambiguationData":[TD([[makeQuery(id+"F0.imprint","IMPRINT",EDGE,{"derivedFrom":subQ0}),1.0]])]});}
            var Q171;
            {var subQ0=sQuery(id+"F0.wireOp",EDGE,"E11.172.0");Q171=makeQuery(id+"F0.imprint","IMPRINT",FACE,{"disambiguationData":[TD([[makeQuery(id+"F0.imprint","IMPRINT",EDGE,{"derivedFrom":subQ0}),1.0]])]});}
            var Q172;
            {var subQ0=sQuery(id+"F0.wireOp",EDGE,"E11.173.0");Q172=makeQuery(id+"F0.imprint","IMPRINT",FACE,{"disambiguationData":[TD([[makeQuery(id+"F0.imprint","IMPRINT",EDGE,{"derivedFrom":subQ0}),1.0]])]});}
            var Q173;
            {var subQ0=sQuery(id+"F0.wireOp",EDGE,"E11.174.0");Q173=makeQuery(id+"F0.imprint","IMPRINT",FACE,{"disambiguationData":[TD([[makeQuery(id+"F0.imprint","IMPRINT",EDGE,{"derivedFrom":subQ0}),1.0]])]});}
            var Q174;
            {var subQ0=sQuery(id+"F0.wireOp",EDGE,"E11.175.0");Q174=makeQuery(id+"F0.imprint","IMPRINT",FACE,{"disambiguationData":[TD([[makeQuery(id+"F0.imprint","IMPRINT",EDGE,{"derivedFrom":subQ0}),1.0]])]});}
            var Q175;
            {var subQ0=sQuery(id+"F0.wireOp",EDGE,"E11.176.0");Q175=makeQuery(id+"F0.imprint","IMPRINT",FACE,{"disambiguationData":[TD([[makeQuery(id+"F0.imprint","IMPRINT",EDGE,{"derivedFrom":subQ0}),1.0]])]});}
            var Q176;
            {var subQ0=sQuery(id+"F0.wireOp",EDGE,"E11.177.0");Q176=makeQuery(id+"F0.imprint","IMPRINT",FACE,{"disambiguationData":[TD([[makeQuery(id+"F0.imprint","IMPRINT",EDGE,{"derivedFrom":subQ0}),1.0]])]});}
            var Q177;
            {var subQ0=sQuery(id+"F0.wireOp",EDGE,"E11.178.0");Q177=makeQuery(id+"F0.imprint","IMPRINT",FACE,{"disambiguationData":[TD([[makeQuery(id+"F0.imprint","IMPRINT",EDGE,{"derivedFrom":subQ0}),1.0]])]});}
            var Q178;
            {var subQ0=sQuery(id+"F0.wireOp",EDGE,"E11.179.0");Q178=makeQuery(id+"F0.imprint","IMPRINT",FACE,{"disambiguationData":[TD([[makeQuery(id+"F0.imprint","IMPRINT",EDGE,{"derivedFrom":subQ0}),1.0]])]});}
            var Q179;
            {var subQ0=sQuery(id+"F0.wireOp",EDGE,"E11.180.0");Q179=makeQuery(id+"F0.imprint","IMPRINT",FACE,{"disambiguationData":[TD([[makeQuery(id+"F0.imprint","IMPRINT",EDGE,{"derivedFrom":subQ0}),1.0]])]});}
            var Q180;
            {var subQ0=sQuery(id+"F0.wireOp",EDGE,"E11.181.0");Q180=makeQuery(id+"F0.imprint","IMPRINT",FACE,{"disambiguationData":[TD([[makeQuery(id+"F0.imprint","IMPRINT",EDGE,{"derivedFrom":subQ0}),1.0]])]});}
            var Q181;
            {var subQ0=sQuery(id+"F0.wireOp",EDGE,"E11.182.0");Q181=makeQuery(id+"F0.imprint","IMPRINT",FACE,{"disambiguationData":[TD([[makeQuery(id+"F0.imprint","IMPRINT",EDGE,{"derivedFrom":subQ0}),1.0]])]});}
            var Q182;
            {var subQ0=sQuery(id+"F0.wireOp",EDGE,"E11.183.0");Q182=makeQuery(id+"F0.imprint","IMPRINT",FACE,{"disambiguationData":[TD([[makeQuery(id+"F0.imprint","IMPRINT",EDGE,{"derivedFrom":subQ0}),1.0]])]});}
            var Q183;
            {var subQ0=sQuery(id+"F0.wireOp",EDGE,"E11.184.0");Q183=makeQuery(id+"F0.imprint","IMPRINT",FACE,{"disambiguationData":[TD([[makeQuery(id+"F0.imprint","IMPRINT",EDGE,{"derivedFrom":subQ0}),1.0]])]});}
            var Q184;
            {var subQ0=sQuery(id+"F0.wireOp",EDGE,"E11.185.0");Q184=makeQuery(id+"F0.imprint","IMPRINT",FACE,{"disambiguationData":[TD([[makeQuery(id+"F0.imprint","IMPRINT",EDGE,{"derivedFrom":subQ0}),1.0]])]});}
            var Q185;
            {var subQ0=sQuery(id+"F0.wireOp",EDGE,"E11.186.0");Q185=makeQuery(id+"F0.imprint","IMPRINT",FACE,{"disambiguationData":[TD([[makeQuery(id+"F0.imprint","IMPRINT",EDGE,{"derivedFrom":subQ0}),1.0]])]});}
            var Q186;
            {var subQ0=sQuery(id+"F0.wireOp",EDGE,"E11.187.0");Q186=makeQuery(id+"F0.imprint","IMPRINT",FACE,{"disambiguationData":[TD([[makeQuery(id+"F0.imprint","IMPRINT",EDGE,{"derivedFrom":subQ0}),1.0]])]});}
            var Q187;
            {var subQ0=sQuery(id+"F0.wireOp",EDGE,"E11.188.0");Q187=makeQuery(id+"F0.imprint","IMPRINT",FACE,{"disambiguationData":[TD([[makeQuery(id+"F0.imprint","IMPRINT",EDGE,{"derivedFrom":subQ0}),1.0]])]});}
            var Q188;
            {var subQ0=sQuery(id+"F0.wireOp",EDGE,"E11.189.0");Q188=makeQuery(id+"F0.imprint","IMPRINT",FACE,{"disambiguationData":[TD([[makeQuery(id+"F0.imprint","IMPRINT",EDGE,{"derivedFrom":subQ0}),1.0]])]});}
            var Q189;
            {var subQ0=sQuery(id+"F0.wireOp",EDGE,"E11.190.0");Q189=makeQuery(id+"F0.imprint","IMPRINT",FACE,{"disambiguationData":[TD([[makeQuery(id+"F0.imprint","IMPRINT",EDGE,{"derivedFrom":subQ0}),1.0]])]});}
            var Q190;
            {var subQ0=sQuery(id+"F0.wireOp",EDGE,"E11.191.0");Q190=makeQuery(id+"F0.imprint","IMPRINT",FACE,{"disambiguationData":[TD([[makeQuery(id+"F0.imprint","IMPRINT",EDGE,{"derivedFrom":subQ0}),1.0]])]});}
            var Q191;
            {var subQ1=sQuery(id+"F0.wireOp",EDGE,"E11.192.0");Q191=makeQuery(id+"F0.imprint","IMPRINT",FACE,{"disambiguationData":[TD([[makeQuery(id+"F0.imprint","IMPRINT",EDGE,{"derivedFrom":subQ1}),1.0]])]});}
            var Q192;
            {var subQ0=sQuery(id+"F0.wireOp",EDGE,"E11.193.0");Q192=makeQuery(id+"F0.imprint","IMPRINT",FACE,{"disambiguationData":[TD([[makeQuery(id+"F0.imprint","IMPRINT",EDGE,{"derivedFrom":subQ0}),1.0]])]});}
            var Q193;
            {var subQ0=sQuery(id+"F0.wireOp",EDGE,"E11.194.0");Q193=makeQuery(id+"F0.imprint","IMPRINT",FACE,{"disambiguationData":[TD([[makeQuery(id+"F0.imprint","IMPRINT",EDGE,{"derivedFrom":subQ0}),1.0]])]});}
            var Q194;
            {var subQ0=sQuery(id+"F0.wireOp",EDGE,"E11.195.0");Q194=makeQuery(id+"F0.imprint","IMPRINT",FACE,{"disambiguationData":[TD([[makeQuery(id+"F0.imprint","IMPRINT",EDGE,{"derivedFrom":subQ0}),1.0]])]});}
            var Q195;
            {var subQ0=sQuery(id+"F0.wireOp",EDGE,"E11.196.0");Q195=makeQuery(id+"F0.imprint","IMPRINT",FACE,{"disambiguationData":[TD([[makeQuery(id+"F0.imprint","IMPRINT",EDGE,{"derivedFrom":subQ0}),1.0]])]});}
            var Q196;
            {var subQ0=sQuery(id+"F0.wireOp",EDGE,"E11.197.0");Q196=makeQuery(id+"F0.imprint","IMPRINT",FACE,{"disambiguationData":[TD([[makeQuery(id+"F0.imprint","IMPRINT",EDGE,{"derivedFrom":subQ0}),1.0]])]});}
            var Q197;
            {var subQ0=sQuery(id+"F0.wireOp",EDGE,"E11.198.0");Q197=makeQuery(id+"F0.imprint","IMPRINT",FACE,{"disambiguationData":[TD([[makeQuery(id+"F0.imprint","IMPRINT",EDGE,{"derivedFrom":subQ0}),1.0]])]});}
            var Q198;
            {var subQ0=sQuery(id+"F0.wireOp",EDGE,"E11.199.0");Q198=makeQuery(id+"F0.imprint","IMPRINT",FACE,{"disambiguationData":[TD([[makeQuery(id+"F0.imprint","IMPRINT",EDGE,{"derivedFrom":subQ0}),1.0]])]});}
            var Q199;
            {var subQ0=sQuery(id+"F0.wireOp",EDGE,"E11.200.0");Q199=makeQuery(id+"F0.imprint","IMPRINT",FACE,{"disambiguationData":[TD([[makeQuery(id+"F0.imprint","IMPRINT",EDGE,{"derivedFrom":subQ0}),1.0]])]});}
            var Q200;
            {var subQ1=sQuery(id+"F0.wireOp",EDGE,"E11.201.0");Q200=makeQuery(id+"F0.imprint","IMPRINT",FACE,{"disambiguationData":[TD([[makeQuery(id+"F0.imprint","IMPRINT",EDGE,{"derivedFrom":subQ1}),1.0]])]});}
            var Q201;
            {var subQ0=sQuery(id+"F0.wireOp",EDGE,"E11.202.0");Q201=makeQuery(id+"F0.imprint","IMPRINT",FACE,{"disambiguationData":[TD([[makeQuery(id+"F0.imprint","IMPRINT",EDGE,{"derivedFrom":subQ0}),1.0]])]});}
            var Q202;
            {var subQ0=sQuery(id+"F0.wireOp",EDGE,"E11.203.0");Q202=makeQuery(id+"F0.imprint","IMPRINT",FACE,{"disambiguationData":[TD([[makeQuery(id+"F0.imprint","IMPRINT",EDGE,{"derivedFrom":subQ0}),1.0]])]});}
            var Q203;
            {var subQ0=sQuery(id+"F0.wireOp",EDGE,"E11.204.0");Q203=makeQuery(id+"F0.imprint","IMPRINT",FACE,{"disambiguationData":[TD([[makeQuery(id+"F0.imprint","IMPRINT",EDGE,{"derivedFrom":subQ0}),1.0]])]});}
            var Q204;
            {var subQ0=sQuery(id+"F0.wireOp",EDGE,"E11.205.0");Q204=makeQuery(id+"F0.imprint","IMPRINT",FACE,{"disambiguationData":[TD([[makeQuery(id+"F0.imprint","IMPRINT",EDGE,{"derivedFrom":subQ0}),1.0]])]});}
            var Q205;
            {var subQ0=sQuery(id+"F0.wireOp",EDGE,"E11.206.0");Q205=makeQuery(id+"F0.imprint","IMPRINT",FACE,{"disambiguationData":[TD([[makeQuery(id+"F0.imprint","IMPRINT",EDGE,{"derivedFrom":subQ0}),1.0]])]});}
            var Q206;
            {var subQ0=sQuery(id+"F0.wireOp",EDGE,"E11.207.0");Q206=makeQuery(id+"F0.imprint","IMPRINT",FACE,{"disambiguationData":[TD([[makeQuery(id+"F0.imprint","IMPRINT",EDGE,{"derivedFrom":subQ0}),1.0]])]});}
            var Q207;
            {var subQ0=sQuery(id+"F0.wireOp",EDGE,"E11.208.0");Q207=makeQuery(id+"F0.imprint","IMPRINT",FACE,{"disambiguationData":[TD([[makeQuery(id+"F0.imprint","IMPRINT",EDGE,{"derivedFrom":subQ0}),1.0]])]});}
            var Q208;
            {var subQ1=sQuery(id+"F0.wireOp",EDGE,"E11.209.0");Q208=makeQuery(id+"F0.imprint","IMPRINT",FACE,{"disambiguationData":[TD([[makeQuery(id+"F0.imprint","IMPRINT",EDGE,{"derivedFrom":subQ1}),1.0]])]});}
            var Q209;
            {var subQ0=sQuery(id+"F0.wireOp",EDGE,"E11.210.0");Q209=makeQuery(id+"F0.imprint","IMPRINT",FACE,{"disambiguationData":[TD([[makeQuery(id+"F0.imprint","IMPRINT",EDGE,{"derivedFrom":subQ0}),1.0]])]});}
            var Q210;
            {var subQ0=sQuery(id+"F0.wireOp",EDGE,"E11.211.0");Q210=makeQuery(id+"F0.imprint","IMPRINT",FACE,{"disambiguationData":[TD([[makeQuery(id+"F0.imprint","IMPRINT",EDGE,{"derivedFrom":subQ0}),1.0]])]});}
            var Q211;
            {var subQ0=sQuery(id+"F0.wireOp",EDGE,"E11.212.0");Q211=makeQuery(id+"F0.imprint","IMPRINT",FACE,{"disambiguationData":[TD([[makeQuery(id+"F0.imprint","IMPRINT",EDGE,{"derivedFrom":subQ0}),1.0]])]});}
            var Q212;
            {var subQ0=sQuery(id+"F0.wireOp",EDGE,"E11.213.0");Q212=makeQuery(id+"F0.imprint","IMPRINT",FACE,{"disambiguationData":[TD([[makeQuery(id+"F0.imprint","IMPRINT",EDGE,{"derivedFrom":subQ0}),1.0]])]});}
            var Q213;
            {var subQ0=sQuery(id+"F0.wireOp",EDGE,"E11.214.0");Q213=makeQuery(id+"F0.imprint","IMPRINT",FACE,{"disambiguationData":[TD([[makeQuery(id+"F0.imprint","IMPRINT",EDGE,{"derivedFrom":subQ0}),1.0]])]});}
            var Q214;
            {var subQ0=sQuery(id+"F0.wireOp",EDGE,"E11.215.0");Q214=makeQuery(id+"F0.imprint","IMPRINT",FACE,{"disambiguationData":[TD([[makeQuery(id+"F0.imprint","IMPRINT",EDGE,{"derivedFrom":subQ0}),1.0]])]});}
            var Q215;
            {var subQ1=sQuery(id+"F0.wireOp",EDGE,"E11.216.0");Q215=makeQuery(id+"F0.imprint","IMPRINT",FACE,{"disambiguationData":[TD([[makeQuery(id+"F0.imprint","IMPRINT",EDGE,{"derivedFrom":subQ1}),1.0]])]});}
            var Q216;
            {var subQ0=sQuery(id+"F0.wireOp",EDGE,"E11.217.0");Q216=makeQuery(id+"F0.imprint","IMPRINT",FACE,{"disambiguationData":[TD([[makeQuery(id+"F0.imprint","IMPRINT",EDGE,{"derivedFrom":subQ0}),1.0]])]});}
            var Q217;
            {var subQ0=sQuery(id+"F0.wireOp",EDGE,"E11.218.0");Q217=makeQuery(id+"F0.imprint","IMPRINT",FACE,{"disambiguationData":[TD([[makeQuery(id+"F0.imprint","IMPRINT",EDGE,{"derivedFrom":subQ0}),1.0]])]});}
            var Q218;
            {var subQ0=sQuery(id+"F0.wireOp",EDGE,"E11.219.0");Q218=makeQuery(id+"F0.imprint","IMPRINT",FACE,{"disambiguationData":[TD([[makeQuery(id+"F0.imprint","IMPRINT",EDGE,{"derivedFrom":subQ0}),1.0]])]});}
            var Q219;
            {var subQ0=sQuery(id+"F0.wireOp",EDGE,"E11.220.0");Q219=makeQuery(id+"F0.imprint","IMPRINT",FACE,{"disambiguationData":[TD([[makeQuery(id+"F0.imprint","IMPRINT",EDGE,{"derivedFrom":subQ0}),1.0]])]});}
            var Q220;
            {var subQ0=sQuery(id+"F0.wireOp",EDGE,"E11.221.0");Q220=makeQuery(id+"F0.imprint","IMPRINT",FACE,{"disambiguationData":[TD([[makeQuery(id+"F0.imprint","IMPRINT",EDGE,{"derivedFrom":subQ0}),1.0]])]});}
            var Q221;
            {var subQ0=sQuery(id+"F0.wireOp",EDGE,"E11.222.0");Q221=makeQuery(id+"F0.imprint","IMPRINT",FACE,{"disambiguationData":[TD([[makeQuery(id+"F0.imprint","IMPRINT",EDGE,{"derivedFrom":subQ0}),1.0]])]});}
            var Q222;
            {var subQ0=sQuery(id+"F0.wireOp",EDGE,"E11.223.0");Q222=makeQuery(id+"F0.imprint","IMPRINT",FACE,{"disambiguationData":[TD([[makeQuery(id+"F0.imprint","IMPRINT",EDGE,{"derivedFrom":subQ0}),1.0]])]});}
            var Q223;
            {var subQ0=sQuery(id+"F0.wireOp",EDGE,"E11.224.0");Q223=makeQuery(id+"F0.imprint","IMPRINT",FACE,{"disambiguationData":[TD([[makeQuery(id+"F0.imprint","IMPRINT",EDGE,{"derivedFrom":subQ0}),1.0]])]});}
            var Q224;
            {var subQ0=sQuery(id+"F0.wireOp",EDGE,"E11.225.0");Q224=makeQuery(id+"F0.imprint","IMPRINT",FACE,{"disambiguationData":[TD([[makeQuery(id+"F0.imprint","IMPRINT",EDGE,{"derivedFrom":subQ0}),1.0]])]});}
            var Q225;
            {var subQ0=sQuery(id+"F0.wireOp",EDGE,"E11.226.0");Q225=makeQuery(id+"F0.imprint","IMPRINT",FACE,{"disambiguationData":[TD([[makeQuery(id+"F0.imprint","IMPRINT",EDGE,{"derivedFrom":subQ0}),1.0]])]});}
            var Q226;
            {var subQ0=sQuery(id+"F0.wireOp",EDGE,"E11.227.0");Q226=makeQuery(id+"F0.imprint","IMPRINT",FACE,{"disambiguationData":[TD([[makeQuery(id+"F0.imprint","IMPRINT",EDGE,{"derivedFrom":subQ0}),1.0]])]});}
            var Q227;
            {var subQ0=sQuery(id+"F0.wireOp",EDGE,"E11.228.0");Q227=makeQuery(id+"F0.imprint","IMPRINT",FACE,{"disambiguationData":[TD([[makeQuery(id+"F0.imprint","IMPRINT",EDGE,{"derivedFrom":subQ0}),1.0]])]});}
            var Q228;
            {var subQ0=sQuery(id+"F0.wireOp",EDGE,"E11.229.0");Q228=makeQuery(id+"F0.imprint","IMPRINT",FACE,{"disambiguationData":[TD([[makeQuery(id+"F0.imprint","IMPRINT",EDGE,{"derivedFrom":subQ0}),1.0]])]});}
            var Q229;
            {var subQ0=sQuery(id+"F0.wireOp",EDGE,"E11.230.0");Q229=makeQuery(id+"F0.imprint","IMPRINT",FACE,{"disambiguationData":[TD([[makeQuery(id+"F0.imprint","IMPRINT",EDGE,{"derivedFrom":subQ0}),1.0]])]});}
            var Q230;
            {var subQ0=sQuery(id+"F0.wireOp",EDGE,"E11.231.0");Q230=makeQuery(id+"F0.imprint","IMPRINT",FACE,{"disambiguationData":[TD([[makeQuery(id+"F0.imprint","IMPRINT",EDGE,{"derivedFrom":subQ0}),1.0]])]});}
            var Q231;
            {var subQ0=sQuery(id+"F0.wireOp",EDGE,"E11.232.0");Q231=makeQuery(id+"F0.imprint","IMPRINT",FACE,{"disambiguationData":[TD([[makeQuery(id+"F0.imprint","IMPRINT",EDGE,{"derivedFrom":subQ0}),1.0]])]});}
            var Q232;
            {var subQ1=sQuery(id+"F0.wireOp",EDGE,"E11.233.0");Q232=makeQuery(id+"F0.imprint","IMPRINT",FACE,{"disambiguationData":[TD([[makeQuery(id+"F0.imprint","IMPRINT",EDGE,{"derivedFrom":subQ1}),1.0]])]});}
            var Q233;
            {var subQ0=sQuery(id+"F0.wireOp",EDGE,"E11.234.0");Q233=makeQuery(id+"F0.imprint","IMPRINT",FACE,{"disambiguationData":[TD([[makeQuery(id+"F0.imprint","IMPRINT",EDGE,{"derivedFrom":subQ0}),1.0]])]});}
            var Q234;
            {var subQ0=sQuery(id+"F0.wireOp",EDGE,"E11.235.0");Q234=makeQuery(id+"F0.imprint","IMPRINT",FACE,{"disambiguationData":[TD([[makeQuery(id+"F0.imprint","IMPRINT",EDGE,{"derivedFrom":subQ0}),1.0]])]});}
            var Q235;
            {var subQ0=sQuery(id+"F0.wireOp",EDGE,"E11.236.0");Q235=makeQuery(id+"F0.imprint","IMPRINT",FACE,{"disambiguationData":[TD([[makeQuery(id+"F0.imprint","IMPRINT",EDGE,{"derivedFrom":subQ0}),1.0]])]});}
            var Q236;
            {var subQ0=sQuery(id+"F0.wireOp",EDGE,"E11.237.0");Q236=makeQuery(id+"F0.imprint","IMPRINT",FACE,{"disambiguationData":[TD([[makeQuery(id+"F0.imprint","IMPRINT",EDGE,{"derivedFrom":subQ0}),1.0]])]});}
            var Q237;
            {var subQ0=sQuery(id+"F0.wireOp",EDGE,"E11.238.0");Q237=makeQuery(id+"F0.imprint","IMPRINT",FACE,{"disambiguationData":[TD([[makeQuery(id+"F0.imprint","IMPRINT",EDGE,{"derivedFrom":subQ0}),1.0]])]});}
            var Q238;
            {var subQ0=sQuery(id+"F0.wireOp",EDGE,"E11.239.0");Q238=makeQuery(id+"F0.imprint","IMPRINT",FACE,{"disambiguationData":[TD([[makeQuery(id+"F0.imprint","IMPRINT",EDGE,{"derivedFrom":subQ0}),1.0]])]});}
            var Q239;
            Q239=makeQuery(id+"F0.imprint","IMPRINT",FACE,{"disambiguationData":[TD([[makeQuery(id+"F0.imprint","IMPRINT",EDGE,{"derivedFrom":sQuery(id+"F0.wireOp",EDGE,"E1.trimOffspring")}),1.0]])]});
            extrude(context, id + "F1", {"entities" : qUnion([Q0, Q1, Q2, Q3, Q4, Q5, Q6, Q7, Q8, Q9, Q10, Q11, Q12, Q13, Q14, Q15, Q16, Q17, Q18, Q19, Q20, Q21, Q22, Q23, Q24, Q25, Q26, Q27, Q28, Q29, Q30, Q31, Q32, Q33, Q34, Q35, Q36, Q37, Q38, Q39, Q40, Q41, Q42, Q43, Q44, Q45, Q46, Q47, Q48, Q49, Q50, Q51, Q52, Q53, Q54, Q55, Q56, Q57, Q58, Q59, Q60, Q61, Q62, Q63, Q64, Q65, Q66, Q67, Q68, Q69, Q70, Q71, Q72, Q73, Q74, Q75, Q76, Q77, Q78, Q79, Q80, Q81, Q82, Q83, Q84, Q85, Q86, Q87, Q88, Q89, Q90, Q91, Q92, Q93, Q94, Q95, Q96, Q97, Q98, Q99, Q100, Q101, Q102, Q103, Q104, Q105, Q106, Q107, Q108, Q109, Q110, Q111, Q112, Q113, Q114, Q115, Q116, Q117, Q118, Q119, Q120, Q121, Q122, Q123, Q124, Q125, Q126, Q127, Q128, Q129, Q130, Q131, Q132, Q133, Q134, Q135, Q136, Q137, Q138, Q139, Q140, Q141, Q142, Q143, Q144, Q145, Q146, Q147, Q148, Q149, Q150, Q151, Q152, Q153, Q154, Q155, Q156, Q157, Q158, Q159, Q160, Q161, Q162, Q163, Q164, Q165, Q166, Q167, Q168, Q169, Q170, Q171, Q172, Q173, Q174, Q175, Q176, Q177, Q178, Q179, Q180, Q181, Q182, Q183, Q184, Q185, Q186, Q187, Q188, Q189, Q190, Q191, Q192, Q193, Q194, Q195, Q196, Q197, Q198, Q199, Q200, Q201, Q202, Q203, Q204, Q205, Q206, Q207, Q208, Q209, Q210, Q211, Q212, Q213, Q214, Q215, Q216, Q217, Q218, Q219, Q220, Q221, Q222, Q223, Q224, Q225, Q226, Q227, Q228, Q229, Q230, Q231, Q232, Q233, Q234, Q235, Q236, Q237, Q238, Q239]), "depth" : 6.35 * mm});
        }
        {
            var Q0;
            Q0=makeQuery(id+"F1.opExtrude","CAP_FACE",FACE,{"disambiguationData":[OSD([sQuery(id+"F0.wireOp",EDGE,"E0"),sQuery(id+"F0.wireOp",EDGE,"E1.trimOffspring"),sQuery(id+"F0.wireOp",EDGE,"E2"),sQuery(id+"F0.wireOp",EDGE,"E3"),sQuery(id+"F0.wireOp",EDGE,"E4.MirrorCS"),sQuery(id+"F0.wireOp",EDGE,"E5.MirrorCS"),sQuery(id+"F0.wireOp",EDGE,"E6.MirrorCS"),sQuery(id+"F0.wireOp",EDGE,"E9.filletArc"),sQuery(id+"F0.wireOp",EDGE,"E10.filletArc"),sQuery(id+"F0.wireOp",EDGE,"E11.1.0"),sQuery(id+"F0.wireOp",EDGE,"E11.1.1"),sQuery(id+"F0.wireOp",EDGE,"E11.1.2"),sQuery(id+"F0.wireOp",EDGE,"E11.1.3"),sQuery(id+"F0.wireOp",EDGE,"E11.1.4"),sQuery(id+"F0.wireOp",EDGE,"E11.1.5"),sQuery(id+"F0.wireOp",EDGE,"E11.1.6"),sQuery(id+"F0.wireOp",EDGE,"E11.1.7"),sQuery(id+"F0.wireOp",EDGE,"E11.2.0"),sQuery(id+"F0.wireOp",EDGE,"E11.2.1"),sQuery(id+"F0.wireOp",EDGE,"E11.2.2"),sQuery(id+"F0.wireOp",EDGE,"E11.2.3"),sQuery(id+"F0.wireOp",EDGE,"E11.2.4"),sQuery(id+"F0.wireOp",EDGE,"E11.2.5"),sQuery(id+"F0.wireOp",EDGE,"E11.2.6"),sQuery(id+"F0.wireOp",EDGE,"E11.2.7"),sQuery(id+"F0.wireOp",EDGE,"E11.3.0"),sQuery(id+"F0.wireOp",EDGE,"E11.3.1"),sQuery(id+"F0.wireOp",EDGE,"E11.3.2"),sQuery(id+"F0.wireOp",EDGE,"E11.3.3"),sQuery(id+"F0.wireOp",EDGE,"E11.3.4"),sQuery(id+"F0.wireOp",EDGE,"E11.3.5"),sQuery(id+"F0.wireOp",EDGE,"E11.3.6"),sQuery(id+"F0.wireOp",EDGE,"E11.3.7"),sQuery(id+"F0.wireOp",EDGE,"E11.4.0"),sQuery(id+"F0.wireOp",EDGE,"E11.4.1"),sQuery(id+"F0.wireOp",EDGE,"E11.4.2"),sQuery(id+"F0.wireOp",EDGE,"E11.4.3"),sQuery(id+"F0.wireOp",EDGE,"E11.4.4"),sQuery(id+"F0.wireOp",EDGE,"E11.4.5"),sQuery(id+"F0.wireOp",EDGE,"E11.4.6"),sQuery(id+"F0.wireOp",EDGE,"E11.4.7"),sQuery(id+"F0.wireOp",EDGE,"E11.5.0"),sQuery(id+"F0.wireOp",EDGE,"E11.5.1"),sQuery(id+"F0.wireOp",EDGE,"E11.5.2"),sQuery(id+"F0.wireOp",EDGE,"E11.5.3"),sQuery(id+"F0.wireOp",EDGE,"E11.5.4"),sQuery(id+"F0.wireOp",EDGE,"E11.5.5"),sQuery(id+"F0.wireOp",EDGE,"E11.5.6"),sQuery(id+"F0.wireOp",EDGE,"E11.5.7"),sQuery(id+"F0.wireOp",EDGE,"E11.6.0"),sQuery(id+"F0.wireOp",EDGE,"E11.6.1"),sQuery(id+"F0.wireOp",EDGE,"E11.6.2"),sQuery(id+"F0.wireOp",EDGE,"E11.6.3"),sQuery(id+"F0.wireOp",EDGE,"E11.6.4"),sQuery(id+"F0.wireOp",EDGE,"E11.6.5"),sQuery(id+"F0.wireOp",EDGE,"E11.6.6"),sQuery(id+"F0.wireOp",EDGE,"E11.6.7"),sQuery(id+"F0.wireOp",EDGE,"E11.7.0"),sQuery(id+"F0.wireOp",EDGE,"E11.7.1"),sQuery(id+"F0.wireOp",EDGE,"E11.7.2"),sQuery(id+"F0.wireOp",EDGE,"E11.7.3"),sQuery(id+"F0.wireOp",EDGE,"E11.7.4"),sQuery(id+"F0.wireOp",EDGE,"E11.7.5"),sQuery(id+"F0.wireOp",EDGE,"E11.7.6"),sQuery(id+"F0.wireOp",EDGE,"E11.7.7"),sQuery(id+"F0.wireOp",EDGE,"E11.8.0"),sQuery(id+"F0.wireOp",EDGE,"E11.8.1"),sQuery(id+"F0.wireOp",EDGE,"E11.8.2"),sQuery(id+"F0.wireOp",EDGE,"E11.8.3"),sQuery(id+"F0.wireOp",EDGE,"E11.8.4"),sQuery(id+"F0.wireOp",EDGE,"E11.8.5"),sQuery(id+"F0.wireOp",EDGE,"E11.8.6"),sQuery(id+"F0.wireOp",EDGE,"E11.8.7"),sQuery(id+"F0.wireOp",EDGE,"E11.9.0"),sQuery(id+"F0.wireOp",EDGE,"E11.9.1"),sQuery(id+"F0.wireOp",EDGE,"E11.9.2"),sQuery(id+"F0.wireOp",EDGE,"E11.9.3"),sQuery(id+"F0.wireOp",EDGE,"E11.9.4"),sQuery(id+"F0.wireOp",EDGE,"E11.9.5"),sQuery(id+"F0.wireOp",EDGE,"E11.9.6"),sQuery(id+"F0.wireOp",EDGE,"E11.9.7"),sQuery(id+"F0.wireOp",EDGE,"E11.10.0"),sQuery(id+"F0.wireOp",EDGE,"E11.10.1"),sQuery(id+"F0.wireOp",EDGE,"E11.10.2"),sQuery(id+"F0.wireOp",EDGE,"E11.10.3"),sQuery(id+"F0.wireOp",EDGE,"E11.10.4"),sQuery(id+"F0.wireOp",EDGE,"E11.10.5"),sQuery(id+"F0.wireOp",EDGE,"E11.10.6"),sQuery(id+"F0.wireOp",EDGE,"E11.10.7"),sQuery(id+"F0.wireOp",EDGE,"E11.11.0"),sQuery(id+"F0.wireOp",EDGE,"E11.11.1"),sQuery(id+"F0.wireOp",EDGE,"E11.11.2"),sQuery(id+"F0.wireOp",EDGE,"E11.11.3"),sQuery(id+"F0.wireOp",EDGE,"E11.11.4"),sQuery(id+"F0.wireOp",EDGE,"E11.11.5"),sQuery(id+"F0.wireOp",EDGE,"E11.11.6"),sQuery(id+"F0.wireOp",EDGE,"E11.11.7"),sQuery(id+"F0.wireOp",EDGE,"E11.12.0"),sQuery(id+"F0.wireOp",EDGE,"E11.12.1"),sQuery(id+"F0.wireOp",EDGE,"E11.12.2"),sQuery(id+"F0.wireOp",EDGE,"E11.12.3"),sQuery(id+"F0.wireOp",EDGE,"E11.12.4"),sQuery(id+"F0.wireOp",EDGE,"E11.12.5"),sQuery(id+"F0.wireOp",EDGE,"E11.12.6"),sQuery(id+"F0.wireOp",EDGE,"E11.12.7"),sQuery(id+"F0.wireOp",EDGE,"E11.13.0"),sQuery(id+"F0.wireOp",EDGE,"E11.13.1"),sQuery(id+"F0.wireOp",EDGE,"E11.13.2"),sQuery(id+"F0.wireOp",EDGE,"E11.13.3"),sQuery(id+"F0.wireOp",EDGE,"E11.13.4"),sQuery(id+"F0.wireOp",EDGE,"E11.13.5"),sQuery(id+"F0.wireOp",EDGE,"E11.13.6"),sQuery(id+"F0.wireOp",EDGE,"E11.13.7"),sQuery(id+"F0.wireOp",EDGE,"E11.14.0"),sQuery(id+"F0.wireOp",EDGE,"E11.14.1"),sQuery(id+"F0.wireOp",EDGE,"E11.14.2"),sQuery(id+"F0.wireOp",EDGE,"E11.14.3"),sQuery(id+"F0.wireOp",EDGE,"E11.14.4"),sQuery(id+"F0.wireOp",EDGE,"E11.14.5"),sQuery(id+"F0.wireOp",EDGE,"E11.14.6"),sQuery(id+"F0.wireOp",EDGE,"E11.14.7"),sQuery(id+"F0.wireOp",EDGE,"E11.15.0"),sQuery(id+"F0.wireOp",EDGE,"E11.15.1"),sQuery(id+"F0.wireOp",EDGE,"E11.15.2"),sQuery(id+"F0.wireOp",EDGE,"E11.15.3"),sQuery(id+"F0.wireOp",EDGE,"E11.15.4"),sQuery(id+"F0.wireOp",EDGE,"E11.15.5"),sQuery(id+"F0.wireOp",EDGE,"E11.15.6"),sQuery(id+"F0.wireOp",EDGE,"E11.15.7"),sQuery(id+"F0.wireOp",EDGE,"E11.16.0"),sQuery(id+"F0.wireOp",EDGE,"E11.16.1"),sQuery(id+"F0.wireOp",EDGE,"E11.16.2"),sQuery(id+"F0.wireOp",EDGE,"E11.16.3"),sQuery(id+"F0.wireOp",EDGE,"E11.16.4"),sQuery(id+"F0.wireOp",EDGE,"E11.16.5"),sQuery(id+"F0.wireOp",EDGE,"E11.16.6"),sQuery(id+"F0.wireOp",EDGE,"E11.16.7"),sQuery(id+"F0.wireOp",EDGE,"E11.17.0"),sQuery(id+"F0.wireOp",EDGE,"E11.17.1"),sQuery(id+"F0.wireOp",EDGE,"E11.17.2"),sQuery(id+"F0.wireOp",EDGE,"E11.17.3"),sQuery(id+"F0.wireOp",EDGE,"E11.17.4"),sQuery(id+"F0.wireOp",EDGE,"E11.17.5"),sQuery(id+"F0.wireOp",EDGE,"E11.17.6"),sQuery(id+"F0.wireOp",EDGE,"E11.17.7"),sQuery(id+"F0.wireOp",EDGE,"E11.18.0"),sQuery(id+"F0.wireOp",EDGE,"E11.18.1"),sQuery(id+"F0.wireOp",EDGE,"E11.18.2"),sQuery(id+"F0.wireOp",EDGE,"E11.18.3"),sQuery(id+"F0.wireOp",EDGE,"E11.18.4"),sQuery(id+"F0.wireOp",EDGE,"E11.18.5"),sQuery(id+"F0.wireOp",EDGE,"E11.18.6"),sQuery(id+"F0.wireOp",EDGE,"E11.18.7"),sQuery(id+"F0.wireOp",EDGE,"E11.19.0"),sQuery(id+"F0.wireOp",EDGE,"E11.19.1"),sQuery(id+"F0.wireOp",EDGE,"E11.19.2"),sQuery(id+"F0.wireOp",EDGE,"E11.19.3"),sQuery(id+"F0.wireOp",EDGE,"E11.19.4"),sQuery(id+"F0.wireOp",EDGE,"E11.19.5"),sQuery(id+"F0.wireOp",EDGE,"E11.19.6"),sQuery(id+"F0.wireOp",EDGE,"E11.19.7"),sQuery(id+"F0.wireOp",EDGE,"E11.20.0"),sQuery(id+"F0.wireOp",EDGE,"E11.20.1"),sQuery(id+"F0.wireOp",EDGE,"E11.20.2"),sQuery(id+"F0.wireOp",EDGE,"E11.20.3"),sQuery(id+"F0.wireOp",EDGE,"E11.20.4"),sQuery(id+"F0.wireOp",EDGE,"E11.20.5"),sQuery(id+"F0.wireOp",EDGE,"E11.20.6"),sQuery(id+"F0.wireOp",EDGE,"E11.20.7"),sQuery(id+"F0.wireOp",EDGE,"E11.21.0"),sQuery(id+"F0.wireOp",EDGE,"E11.21.1"),sQuery(id+"F0.wireOp",EDGE,"E11.21.2"),sQuery(id+"F0.wireOp",EDGE,"E11.21.3"),sQuery(id+"F0.wireOp",EDGE,"E11.21.4"),sQuery(id+"F0.wireOp",EDGE,"E11.21.5"),sQuery(id+"F0.wireOp",EDGE,"E11.21.6"),sQuery(id+"F0.wireOp",EDGE,"E11.21.7"),sQuery(id+"F0.wireOp",EDGE,"E11.22.0"),sQuery(id+"F0.wireOp",EDGE,"E11.22.1"),sQuery(id+"F0.wireOp",EDGE,"E11.22.2"),sQuery(id+"F0.wireOp",EDGE,"E11.22.3"),sQuery(id+"F0.wireOp",EDGE,"E11.22.4"),sQuery(id+"F0.wireOp",EDGE,"E11.22.5"),sQuery(id+"F0.wireOp",EDGE,"E11.22.6"),sQuery(id+"F0.wireOp",EDGE,"E11.22.7"),sQuery(id+"F0.wireOp",EDGE,"E11.23.0"),sQuery(id+"F0.wireOp",EDGE,"E11.23.1"),sQuery(id+"F0.wireOp",EDGE,"E11.23.2"),sQuery(id+"F0.wireOp",EDGE,"E11.23.3"),sQuery(id+"F0.wireOp",EDGE,"E11.23.4"),sQuery(id+"F0.wireOp",EDGE,"E11.23.5"),sQuery(id+"F0.wireOp",EDGE,"E11.23.6"),sQuery(id+"F0.wireOp",EDGE,"E11.23.7"),sQuery(id+"F0.wireOp",EDGE,"E11.24.0"),sQuery(id+"F0.wireOp",EDGE,"E11.24.1"),sQuery(id+"F0.wireOp",EDGE,"E11.24.2"),sQuery(id+"F0.wireOp",EDGE,"E11.24.3"),sQuery(id+"F0.wireOp",EDGE,"E11.24.4"),sQuery(id+"F0.wireOp",EDGE,"E11.24.5"),sQuery(id+"F0.wireOp",EDGE,"E11.24.6"),sQuery(id+"F0.wireOp",EDGE,"E11.24.7"),sQuery(id+"F0.wireOp",EDGE,"E11.25.0"),sQuery(id+"F0.wireOp",EDGE,"E11.25.1"),sQuery(id+"F0.wireOp",EDGE,"E11.25.2"),sQuery(id+"F0.wireOp",EDGE,"E11.25.3"),sQuery(id+"F0.wireOp",EDGE,"E11.25.4"),sQuery(id+"F0.wireOp",EDGE,"E11.25.5"),sQuery(id+"F0.wireOp",EDGE,"E11.25.6"),sQuery(id+"F0.wireOp",EDGE,"E11.25.7"),sQuery(id+"F0.wireOp",EDGE,"E11.26.0"),sQuery(id+"F0.wireOp",EDGE,"E11.26.1"),sQuery(id+"F0.wireOp",EDGE,"E11.26.2"),sQuery(id+"F0.wireOp",EDGE,"E11.26.3"),sQuery(id+"F0.wireOp",EDGE,"E11.26.4"),sQuery(id+"F0.wireOp",EDGE,"E11.26.5"),sQuery(id+"F0.wireOp",EDGE,"E11.26.6"),sQuery(id+"F0.wireOp",EDGE,"E11.26.7"),sQuery(id+"F0.wireOp",EDGE,"E11.27.0"),sQuery(id+"F0.wireOp",EDGE,"E11.27.1"),sQuery(id+"F0.wireOp",EDGE,"E11.27.2"),sQuery(id+"F0.wireOp",EDGE,"E11.27.3"),sQuery(id+"F0.wireOp",EDGE,"E11.27.4"),sQuery(id+"F0.wireOp",EDGE,"E11.27.5"),sQuery(id+"F0.wireOp",EDGE,"E11.27.6"),sQuery(id+"F0.wireOp",EDGE,"E11.27.7"),sQuery(id+"F0.wireOp",EDGE,"E11.28.0"),sQuery(id+"F0.wireOp",EDGE,"E11.28.1"),sQuery(id+"F0.wireOp",EDGE,"E11.28.2"),sQuery(id+"F0.wireOp",EDGE,"E11.28.3"),sQuery(id+"F0.wireOp",EDGE,"E11.28.4"),sQuery(id+"F0.wireOp",EDGE,"E11.28.5"),sQuery(id+"F0.wireOp",EDGE,"E11.28.6"),sQuery(id+"F0.wireOp",EDGE,"E11.28.7"),sQuery(id+"F0.wireOp",EDGE,"E11.29.0"),sQuery(id+"F0.wireOp",EDGE,"E11.29.1"),sQuery(id+"F0.wireOp",EDGE,"E11.29.2"),sQuery(id+"F0.wireOp",EDGE,"E11.29.3"),sQuery(id+"F0.wireOp",EDGE,"E11.29.4"),sQuery(id+"F0.wireOp",EDGE,"E11.29.5"),sQuery(id+"F0.wireOp",EDGE,"E11.29.6"),sQuery(id+"F0.wireOp",EDGE,"E11.29.7"),sQuery(id+"F0.wireOp",EDGE,"E11.30.0"),sQuery(id+"F0.wireOp",EDGE,"E11.30.1"),sQuery(id+"F0.wireOp",EDGE,"E11.30.2"),sQuery(id+"F0.wireOp",EDGE,"E11.30.3"),sQuery(id+"F0.wireOp",EDGE,"E11.30.4"),sQuery(id+"F0.wireOp",EDGE,"E11.30.5"),sQuery(id+"F0.wireOp",EDGE,"E11.30.6"),sQuery(id+"F0.wireOp",EDGE,"E11.30.7"),sQuery(id+"F0.wireOp",EDGE,"E11.31.0"),sQuery(id+"F0.wireOp",EDGE,"E11.31.1"),sQuery(id+"F0.wireOp",EDGE,"E11.31.2"),sQuery(id+"F0.wireOp",EDGE,"E11.31.3"),sQuery(id+"F0.wireOp",EDGE,"E11.31.4"),sQuery(id+"F0.wireOp",EDGE,"E11.31.5"),sQuery(id+"F0.wireOp",EDGE,"E11.31.6"),sQuery(id+"F0.wireOp",EDGE,"E11.31.7"),sQuery(id+"F0.wireOp",EDGE,"E11.32.0"),sQuery(id+"F0.wireOp",EDGE,"E11.32.1"),sQuery(id+"F0.wireOp",EDGE,"E11.32.2"),sQuery(id+"F0.wireOp",EDGE,"E11.32.3"),sQuery(id+"F0.wireOp",EDGE,"E11.32.4"),sQuery(id+"F0.wireOp",EDGE,"E11.32.5"),sQuery(id+"F0.wireOp",EDGE,"E11.32.6"),sQuery(id+"F0.wireOp",EDGE,"E11.32.7"),sQuery(id+"F0.wireOp",EDGE,"E11.33.0"),sQuery(id+"F0.wireOp",EDGE,"E11.33.1"),sQuery(id+"F0.wireOp",EDGE,"E11.33.2"),sQuery(id+"F0.wireOp",EDGE,"E11.33.3"),sQuery(id+"F0.wireOp",EDGE,"E11.33.4"),sQuery(id+"F0.wireOp",EDGE,"E11.33.5"),sQuery(id+"F0.wireOp",EDGE,"E11.33.6"),sQuery(id+"F0.wireOp",EDGE,"E11.33.7"),sQuery(id+"F0.wireOp",EDGE,"E11.34.0"),sQuery(id+"F0.wireOp",EDGE,"E11.34.1"),sQuery(id+"F0.wireOp",EDGE,"E11.34.2"),sQuery(id+"F0.wireOp",EDGE,"E11.34.3"),sQuery(id+"F0.wireOp",EDGE,"E11.34.4"),sQuery(id+"F0.wireOp",EDGE,"E11.34.5"),sQuery(id+"F0.wireOp",EDGE,"E11.34.6"),sQuery(id+"F0.wireOp",EDGE,"E11.34.7"),sQuery(id+"F0.wireOp",EDGE,"E11.35.0"),sQuery(id+"F0.wireOp",EDGE,"E11.35.1"),sQuery(id+"F0.wireOp",EDGE,"E11.35.2"),sQuery(id+"F0.wireOp",EDGE,"E11.35.3"),sQuery(id+"F0.wireOp",EDGE,"E11.35.4"),sQuery(id+"F0.wireOp",EDGE,"E11.35.5"),sQuery(id+"F0.wireOp",EDGE,"E11.35.6"),sQuery(id+"F0.wireOp",EDGE,"E11.35.7"),sQuery(id+"F0.wireOp",EDGE,"E11.36.0"),sQuery(id+"F0.wireOp",EDGE,"E11.36.1"),sQuery(id+"F0.wireOp",EDGE,"E11.36.2"),sQuery(id+"F0.wireOp",EDGE,"E11.36.3"),sQuery(id+"F0.wireOp",EDGE,"E11.36.4"),sQuery(id+"F0.wireOp",EDGE,"E11.36.5"),sQuery(id+"F0.wireOp",EDGE,"E11.36.6"),sQuery(id+"F0.wireOp",EDGE,"E11.36.7"),sQuery(id+"F0.wireOp",EDGE,"E11.37.0"),sQuery(id+"F0.wireOp",EDGE,"E11.37.1"),sQuery(id+"F0.wireOp",EDGE,"E11.37.2"),sQuery(id+"F0.wireOp",EDGE,"E11.37.3"),sQuery(id+"F0.wireOp",EDGE,"E11.37.4"),sQuery(id+"F0.wireOp",EDGE,"E11.37.5"),sQuery(id+"F0.wireOp",EDGE,"E11.37.6"),sQuery(id+"F0.wireOp",EDGE,"E11.37.7"),sQuery(id+"F0.wireOp",EDGE,"E11.38.0"),sQuery(id+"F0.wireOp",EDGE,"E11.38.1"),sQuery(id+"F0.wireOp",EDGE,"E11.38.2"),sQuery(id+"F0.wireOp",EDGE,"E11.38.3"),sQuery(id+"F0.wireOp",EDGE,"E11.38.4"),sQuery(id+"F0.wireOp",EDGE,"E11.38.5"),sQuery(id+"F0.wireOp",EDGE,"E11.38.6"),sQuery(id+"F0.wireOp",EDGE,"E11.38.7"),sQuery(id+"F0.wireOp",EDGE,"E11.39.0"),sQuery(id+"F0.wireOp",EDGE,"E11.39.1"),sQuery(id+"F0.wireOp",EDGE,"E11.39.2"),sQuery(id+"F0.wireOp",EDGE,"E11.39.3"),sQuery(id+"F0.wireOp",EDGE,"E11.39.4"),sQuery(id+"F0.wireOp",EDGE,"E11.39.5"),sQuery(id+"F0.wireOp",EDGE,"E11.39.6"),sQuery(id+"F0.wireOp",EDGE,"E11.39.7"),sQuery(id+"F0.wireOp",EDGE,"E11.40.0"),sQuery(id+"F0.wireOp",EDGE,"E11.40.1"),sQuery(id+"F0.wireOp",EDGE,"E11.40.2"),sQuery(id+"F0.wireOp",EDGE,"E11.40.3"),sQuery(id+"F0.wireOp",EDGE,"E11.40.4"),sQuery(id+"F0.wireOp",EDGE,"E11.40.5"),sQuery(id+"F0.wireOp",EDGE,"E11.40.6"),sQuery(id+"F0.wireOp",EDGE,"E11.40.7"),sQuery(id+"F0.wireOp",EDGE,"E11.41.0"),sQuery(id+"F0.wireOp",EDGE,"E11.41.1"),sQuery(id+"F0.wireOp",EDGE,"E11.41.2"),sQuery(id+"F0.wireOp",EDGE,"E11.41.3"),sQuery(id+"F0.wireOp",EDGE,"E11.41.4"),sQuery(id+"F0.wireOp",EDGE,"E11.41.5"),sQuery(id+"F0.wireOp",EDGE,"E11.41.6"),sQuery(id+"F0.wireOp",EDGE,"E11.41.7"),sQuery(id+"F0.wireOp",EDGE,"E11.42.0"),sQuery(id+"F0.wireOp",EDGE,"E11.42.1"),sQuery(id+"F0.wireOp",EDGE,"E11.42.2"),sQuery(id+"F0.wireOp",EDGE,"E11.42.3"),sQuery(id+"F0.wireOp",EDGE,"E11.42.4"),sQuery(id+"F0.wireOp",EDGE,"E11.42.5"),sQuery(id+"F0.wireOp",EDGE,"E11.42.6"),sQuery(id+"F0.wireOp",EDGE,"E11.42.7"),sQuery(id+"F0.wireOp",EDGE,"E11.43.0"),sQuery(id+"F0.wireOp",EDGE,"E11.43.1"),sQuery(id+"F0.wireOp",EDGE,"E11.43.2"),sQuery(id+"F0.wireOp",EDGE,"E11.43.3"),sQuery(id+"F0.wireOp",EDGE,"E11.43.4"),sQuery(id+"F0.wireOp",EDGE,"E11.43.5"),sQuery(id+"F0.wireOp",EDGE,"E11.43.6"),sQuery(id+"F0.wireOp",EDGE,"E11.43.7"),sQuery(id+"F0.wireOp",EDGE,"E11.44.0"),sQuery(id+"F0.wireOp",EDGE,"E11.44.1"),sQuery(id+"F0.wireOp",EDGE,"E11.44.2"),sQuery(id+"F0.wireOp",EDGE,"E11.44.3"),sQuery(id+"F0.wireOp",EDGE,"E11.44.4"),sQuery(id+"F0.wireOp",EDGE,"E11.44.5"),sQuery(id+"F0.wireOp",EDGE,"E11.44.6"),sQuery(id+"F0.wireOp",EDGE,"E11.44.7"),sQuery(id+"F0.wireOp",EDGE,"E11.45.0"),sQuery(id+"F0.wireOp",EDGE,"E11.45.1"),sQuery(id+"F0.wireOp",EDGE,"E11.45.2"),sQuery(id+"F0.wireOp",EDGE,"E11.45.3"),sQuery(id+"F0.wireOp",EDGE,"E11.45.4"),sQuery(id+"F0.wireOp",EDGE,"E11.45.5"),sQuery(id+"F0.wireOp",EDGE,"E11.45.6"),sQuery(id+"F0.wireOp",EDGE,"E11.45.7"),sQuery(id+"F0.wireOp",EDGE,"E11.46.0"),sQuery(id+"F0.wireOp",EDGE,"E11.46.1"),sQuery(id+"F0.wireOp",EDGE,"E11.46.2"),sQuery(id+"F0.wireOp",EDGE,"E11.46.3"),sQuery(id+"F0.wireOp",EDGE,"E11.46.4"),sQuery(id+"F0.wireOp",EDGE,"E11.46.5"),sQuery(id+"F0.wireOp",EDGE,"E11.46.6"),sQuery(id+"F0.wireOp",EDGE,"E11.46.7"),sQuery(id+"F0.wireOp",EDGE,"E11.47.0"),sQuery(id+"F0.wireOp",EDGE,"E11.47.1"),sQuery(id+"F0.wireOp",EDGE,"E11.47.2"),sQuery(id+"F0.wireOp",EDGE,"E11.47.3"),sQuery(id+"F0.wireOp",EDGE,"E11.47.4"),sQuery(id+"F0.wireOp",EDGE,"E11.47.5"),sQuery(id+"F0.wireOp",EDGE,"E11.47.6"),sQuery(id+"F0.wireOp",EDGE,"E11.47.7"),sQuery(id+"F0.wireOp",EDGE,"E11.48.0"),sQuery(id+"F0.wireOp",EDGE,"E11.48.1"),sQuery(id+"F0.wireOp",EDGE,"E11.48.2"),sQuery(id+"F0.wireOp",EDGE,"E11.48.3"),sQuery(id+"F0.wireOp",EDGE,"E11.48.4"),sQuery(id+"F0.wireOp",EDGE,"E11.48.5"),sQuery(id+"F0.wireOp",EDGE,"E11.48.6"),sQuery(id+"F0.wireOp",EDGE,"E11.48.7"),sQuery(id+"F0.wireOp",EDGE,"E11.49.0"),sQuery(id+"F0.wireOp",EDGE,"E11.49.1"),sQuery(id+"F0.wireOp",EDGE,"E11.49.2"),sQuery(id+"F0.wireOp",EDGE,"E11.49.3"),sQuery(id+"F0.wireOp",EDGE,"E11.49.4"),sQuery(id+"F0.wireOp",EDGE,"E11.49.5"),sQuery(id+"F0.wireOp",EDGE,"E11.49.6"),sQuery(id+"F0.wireOp",EDGE,"E11.49.7"),sQuery(id+"F0.wireOp",EDGE,"E11.50.0"),sQuery(id+"F0.wireOp",EDGE,"E11.50.1"),sQuery(id+"F0.wireOp",EDGE,"E11.50.2"),sQuery(id+"F0.wireOp",EDGE,"E11.50.3"),sQuery(id+"F0.wireOp",EDGE,"E11.50.4"),sQuery(id+"F0.wireOp",EDGE,"E11.50.5"),sQuery(id+"F0.wireOp",EDGE,"E11.50.6"),sQuery(id+"F0.wireOp",EDGE,"E11.50.7"),sQuery(id+"F0.wireOp",EDGE,"E11.51.0"),sQuery(id+"F0.wireOp",EDGE,"E11.51.1"),sQuery(id+"F0.wireOp",EDGE,"E11.51.2"),sQuery(id+"F0.wireOp",EDGE,"E11.51.3"),sQuery(id+"F0.wireOp",EDGE,"E11.51.4"),sQuery(id+"F0.wireOp",EDGE,"E11.51.5"),sQuery(id+"F0.wireOp",EDGE,"E11.51.6"),sQuery(id+"F0.wireOp",EDGE,"E11.51.7"),sQuery(id+"F0.wireOp",EDGE,"E11.52.0"),sQuery(id+"F0.wireOp",EDGE,"E11.52.1"),sQuery(id+"F0.wireOp",EDGE,"E11.52.2"),sQuery(id+"F0.wireOp",EDGE,"E11.52.3"),sQuery(id+"F0.wireOp",EDGE,"E11.52.4"),sQuery(id+"F0.wireOp",EDGE,"E11.52.5"),sQuery(id+"F0.wireOp",EDGE,"E11.52.6"),sQuery(id+"F0.wireOp",EDGE,"E11.52.7"),sQuery(id+"F0.wireOp",EDGE,"E11.53.0"),sQuery(id+"F0.wireOp",EDGE,"E11.53.1"),sQuery(id+"F0.wireOp",EDGE,"E11.53.2"),sQuery(id+"F0.wireOp",EDGE,"E11.53.3"),sQuery(id+"F0.wireOp",EDGE,"E11.53.4"),sQuery(id+"F0.wireOp",EDGE,"E11.53.5"),sQuery(id+"F0.wireOp",EDGE,"E11.53.6"),sQuery(id+"F0.wireOp",EDGE,"E11.53.7"),sQuery(id+"F0.wireOp",EDGE,"E11.54.0"),sQuery(id+"F0.wireOp",EDGE,"E11.54.1"),sQuery(id+"F0.wireOp",EDGE,"E11.54.2"),sQuery(id+"F0.wireOp",EDGE,"E11.54.3"),sQuery(id+"F0.wireOp",EDGE,"E11.54.4"),sQuery(id+"F0.wireOp",EDGE,"E11.54.5"),sQuery(id+"F0.wireOp",EDGE,"E11.54.6"),sQuery(id+"F0.wireOp",EDGE,"E11.54.7"),sQuery(id+"F0.wireOp",EDGE,"E11.55.0"),sQuery(id+"F0.wireOp",EDGE,"E11.55.1"),sQuery(id+"F0.wireOp",EDGE,"E11.55.2"),sQuery(id+"F0.wireOp",EDGE,"E11.55.3"),sQuery(id+"F0.wireOp",EDGE,"E11.55.4"),sQuery(id+"F0.wireOp",EDGE,"E11.55.5"),sQuery(id+"F0.wireOp",EDGE,"E11.55.6"),sQuery(id+"F0.wireOp",EDGE,"E11.55.7"),sQuery(id+"F0.wireOp",EDGE,"E11.56.0"),sQuery(id+"F0.wireOp",EDGE,"E11.56.1"),sQuery(id+"F0.wireOp",EDGE,"E11.56.2"),sQuery(id+"F0.wireOp",EDGE,"E11.56.3"),sQuery(id+"F0.wireOp",EDGE,"E11.56.4"),sQuery(id+"F0.wireOp",EDGE,"E11.56.5"),sQuery(id+"F0.wireOp",EDGE,"E11.56.6"),sQuery(id+"F0.wireOp",EDGE,"E11.56.7"),sQuery(id+"F0.wireOp",EDGE,"E11.57.0"),sQuery(id+"F0.wireOp",EDGE,"E11.57.1"),sQuery(id+"F0.wireOp",EDGE,"E11.57.2"),sQuery(id+"F0.wireOp",EDGE,"E11.57.3"),sQuery(id+"F0.wireOp",EDGE,"E11.57.4"),sQuery(id+"F0.wireOp",EDGE,"E11.57.5"),sQuery(id+"F0.wireOp",EDGE,"E11.57.6"),sQuery(id+"F0.wireOp",EDGE,"E11.57.7"),sQuery(id+"F0.wireOp",EDGE,"E11.58.0"),sQuery(id+"F0.wireOp",EDGE,"E11.58.1"),sQuery(id+"F0.wireOp",EDGE,"E11.58.2"),sQuery(id+"F0.wireOp",EDGE,"E11.58.3"),sQuery(id+"F0.wireOp",EDGE,"E11.58.4"),sQuery(id+"F0.wireOp",EDGE,"E11.58.5"),sQuery(id+"F0.wireOp",EDGE,"E11.58.6"),sQuery(id+"F0.wireOp",EDGE,"E11.58.7"),sQuery(id+"F0.wireOp",EDGE,"E11.59.0"),sQuery(id+"F0.wireOp",EDGE,"E11.59.1"),sQuery(id+"F0.wireOp",EDGE,"E11.59.2"),sQuery(id+"F0.wireOp",EDGE,"E11.59.3"),sQuery(id+"F0.wireOp",EDGE,"E11.59.4"),sQuery(id+"F0.wireOp",EDGE,"E11.59.5"),sQuery(id+"F0.wireOp",EDGE,"E11.59.6"),sQuery(id+"F0.wireOp",EDGE,"E11.59.7"),sQuery(id+"F0.wireOp",EDGE,"E11.60.0"),sQuery(id+"F0.wireOp",EDGE,"E11.60.1"),sQuery(id+"F0.wireOp",EDGE,"E11.60.2"),sQuery(id+"F0.wireOp",EDGE,"E11.60.3"),sQuery(id+"F0.wireOp",EDGE,"E11.60.4"),sQuery(id+"F0.wireOp",EDGE,"E11.60.5"),sQuery(id+"F0.wireOp",EDGE,"E11.60.6"),sQuery(id+"F0.wireOp",EDGE,"E11.60.7"),sQuery(id+"F0.wireOp",EDGE,"E11.61.0"),sQuery(id+"F0.wireOp",EDGE,"E11.61.1"),sQuery(id+"F0.wireOp",EDGE,"E11.61.2"),sQuery(id+"F0.wireOp",EDGE,"E11.61.3"),sQuery(id+"F0.wireOp",EDGE,"E11.61.4"),sQuery(id+"F0.wireOp",EDGE,"E11.61.5"),sQuery(id+"F0.wireOp",EDGE,"E11.61.6"),sQuery(id+"F0.wireOp",EDGE,"E11.61.7"),sQuery(id+"F0.wireOp",EDGE,"E11.62.0"),sQuery(id+"F0.wireOp",EDGE,"E11.62.1"),sQuery(id+"F0.wireOp",EDGE,"E11.62.2"),sQuery(id+"F0.wireOp",EDGE,"E11.62.3"),sQuery(id+"F0.wireOp",EDGE,"E11.62.4"),sQuery(id+"F0.wireOp",EDGE,"E11.62.5"),sQuery(id+"F0.wireOp",EDGE,"E11.62.6"),sQuery(id+"F0.wireOp",EDGE,"E11.62.7"),sQuery(id+"F0.wireOp",EDGE,"E11.63.0"),sQuery(id+"F0.wireOp",EDGE,"E11.63.1"),sQuery(id+"F0.wireOp",EDGE,"E11.63.2"),sQuery(id+"F0.wireOp",EDGE,"E11.63.3"),sQuery(id+"F0.wireOp",EDGE,"E11.63.4"),sQuery(id+"F0.wireOp",EDGE,"E11.63.5"),sQuery(id+"F0.wireOp",EDGE,"E11.63.6"),sQuery(id+"F0.wireOp",EDGE,"E11.63.7"),sQuery(id+"F0.wireOp",EDGE,"E11.64.0"),sQuery(id+"F0.wireOp",EDGE,"E11.64.1"),sQuery(id+"F0.wireOp",EDGE,"E11.64.2"),sQuery(id+"F0.wireOp",EDGE,"E11.64.3"),sQuery(id+"F0.wireOp",EDGE,"E11.64.4"),sQuery(id+"F0.wireOp",EDGE,"E11.64.5"),sQuery(id+"F0.wireOp",EDGE,"E11.64.6"),sQuery(id+"F0.wireOp",EDGE,"E11.64.7"),sQuery(id+"F0.wireOp",EDGE,"E11.65.0"),sQuery(id+"F0.wireOp",EDGE,"E11.65.1"),sQuery(id+"F0.wireOp",EDGE,"E11.65.2"),sQuery(id+"F0.wireOp",EDGE,"E11.65.3"),sQuery(id+"F0.wireOp",EDGE,"E11.65.4"),sQuery(id+"F0.wireOp",EDGE,"E11.65.5"),sQuery(id+"F0.wireOp",EDGE,"E11.65.6"),sQuery(id+"F0.wireOp",EDGE,"E11.65.7"),sQuery(id+"F0.wireOp",EDGE,"E11.66.0"),sQuery(id+"F0.wireOp",EDGE,"E11.66.1"),sQuery(id+"F0.wireOp",EDGE,"E11.66.2"),sQuery(id+"F0.wireOp",EDGE,"E11.66.3"),sQuery(id+"F0.wireOp",EDGE,"E11.66.4"),sQuery(id+"F0.wireOp",EDGE,"E11.66.5"),sQuery(id+"F0.wireOp",EDGE,"E11.66.6"),sQuery(id+"F0.wireOp",EDGE,"E11.66.7"),sQuery(id+"F0.wireOp",EDGE,"E11.67.0"),sQuery(id+"F0.wireOp",EDGE,"E11.67.1"),sQuery(id+"F0.wireOp",EDGE,"E11.67.2"),sQuery(id+"F0.wireOp",EDGE,"E11.67.3"),sQuery(id+"F0.wireOp",EDGE,"E11.67.4"),sQuery(id+"F0.wireOp",EDGE,"E11.67.5"),sQuery(id+"F0.wireOp",EDGE,"E11.67.6"),sQuery(id+"F0.wireOp",EDGE,"E11.67.7"),sQuery(id+"F0.wireOp",EDGE,"E11.68.0"),sQuery(id+"F0.wireOp",EDGE,"E11.68.1"),sQuery(id+"F0.wireOp",EDGE,"E11.68.2"),sQuery(id+"F0.wireOp",EDGE,"E11.68.3"),sQuery(id+"F0.wireOp",EDGE,"E11.68.4"),sQuery(id+"F0.wireOp",EDGE,"E11.68.5"),sQuery(id+"F0.wireOp",EDGE,"E11.68.6"),sQuery(id+"F0.wireOp",EDGE,"E11.68.7"),sQuery(id+"F0.wireOp",EDGE,"E11.69.0"),sQuery(id+"F0.wireOp",EDGE,"E11.69.1"),sQuery(id+"F0.wireOp",EDGE,"E11.69.2"),sQuery(id+"F0.wireOp",EDGE,"E11.69.3"),sQuery(id+"F0.wireOp",EDGE,"E11.69.4"),sQuery(id+"F0.wireOp",EDGE,"E11.69.5"),sQuery(id+"F0.wireOp",EDGE,"E11.69.6"),sQuery(id+"F0.wireOp",EDGE,"E11.69.7"),sQuery(id+"F0.wireOp",EDGE,"E11.70.0"),sQuery(id+"F0.wireOp",EDGE,"E11.70.1"),sQuery(id+"F0.wireOp",EDGE,"E11.70.2"),sQuery(id+"F0.wireOp",EDGE,"E11.70.3"),sQuery(id+"F0.wireOp",EDGE,"E11.70.4"),sQuery(id+"F0.wireOp",EDGE,"E11.70.5"),sQuery(id+"F0.wireOp",EDGE,"E11.70.6"),sQuery(id+"F0.wireOp",EDGE,"E11.70.7"),sQuery(id+"F0.wireOp",EDGE,"E11.71.0"),sQuery(id+"F0.wireOp",EDGE,"E11.71.1"),sQuery(id+"F0.wireOp",EDGE,"E11.71.2"),sQuery(id+"F0.wireOp",EDGE,"E11.71.3"),sQuery(id+"F0.wireOp",EDGE,"E11.71.4"),sQuery(id+"F0.wireOp",EDGE,"E11.71.5"),sQuery(id+"F0.wireOp",EDGE,"E11.71.6"),sQuery(id+"F0.wireOp",EDGE,"E11.71.7"),sQuery(id+"F0.wireOp",EDGE,"E11.72.0"),sQuery(id+"F0.wireOp",EDGE,"E11.72.1"),sQuery(id+"F0.wireOp",EDGE,"E11.72.2"),sQuery(id+"F0.wireOp",EDGE,"E11.72.3"),sQuery(id+"F0.wireOp",EDGE,"E11.72.4"),sQuery(id+"F0.wireOp",EDGE,"E11.72.5"),sQuery(id+"F0.wireOp",EDGE,"E11.72.6"),sQuery(id+"F0.wireOp",EDGE,"E11.72.7"),sQuery(id+"F0.wireOp",EDGE,"E11.73.0"),sQuery(id+"F0.wireOp",EDGE,"E11.73.1"),sQuery(id+"F0.wireOp",EDGE,"E11.73.2"),sQuery(id+"F0.wireOp",EDGE,"E11.73.3"),sQuery(id+"F0.wireOp",EDGE,"E11.73.4"),sQuery(id+"F0.wireOp",EDGE,"E11.73.5"),sQuery(id+"F0.wireOp",EDGE,"E11.73.6"),sQuery(id+"F0.wireOp",EDGE,"E11.73.7"),sQuery(id+"F0.wireOp",EDGE,"E11.74.0"),sQuery(id+"F0.wireOp",EDGE,"E11.74.1"),sQuery(id+"F0.wireOp",EDGE,"E11.74.2"),sQuery(id+"F0.wireOp",EDGE,"E11.74.3"),sQuery(id+"F0.wireOp",EDGE,"E11.74.4"),sQuery(id+"F0.wireOp",EDGE,"E11.74.5"),sQuery(id+"F0.wireOp",EDGE,"E11.74.6"),sQuery(id+"F0.wireOp",EDGE,"E11.74.7"),sQuery(id+"F0.wireOp",EDGE,"E11.75.0"),sQuery(id+"F0.wireOp",EDGE,"E11.75.1"),sQuery(id+"F0.wireOp",EDGE,"E11.75.2"),sQuery(id+"F0.wireOp",EDGE,"E11.75.3"),sQuery(id+"F0.wireOp",EDGE,"E11.75.4"),sQuery(id+"F0.wireOp",EDGE,"E11.75.5"),sQuery(id+"F0.wireOp",EDGE,"E11.75.6"),sQuery(id+"F0.wireOp",EDGE,"E11.75.7"),sQuery(id+"F0.wireOp",EDGE,"E11.76.0"),sQuery(id+"F0.wireOp",EDGE,"E11.76.1"),sQuery(id+"F0.wireOp",EDGE,"E11.76.2"),sQuery(id+"F0.wireOp",EDGE,"E11.76.3"),sQuery(id+"F0.wireOp",EDGE,"E11.76.4"),sQuery(id+"F0.wireOp",EDGE,"E11.76.5"),sQuery(id+"F0.wireOp",EDGE,"E11.76.6"),sQuery(id+"F0.wireOp",EDGE,"E11.76.7"),sQuery(id+"F0.wireOp",EDGE,"E11.77.0"),sQuery(id+"F0.wireOp",EDGE,"E11.77.1"),sQuery(id+"F0.wireOp",EDGE,"E11.77.2"),sQuery(id+"F0.wireOp",EDGE,"E11.77.3"),sQuery(id+"F0.wireOp",EDGE,"E11.77.4"),sQuery(id+"F0.wireOp",EDGE,"E11.77.5"),sQuery(id+"F0.wireOp",EDGE,"E11.77.6"),sQuery(id+"F0.wireOp",EDGE,"E11.77.7"),sQuery(id+"F0.wireOp",EDGE,"E11.78.0"),sQuery(id+"F0.wireOp",EDGE,"E11.78.1"),sQuery(id+"F0.wireOp",EDGE,"E11.78.2"),sQuery(id+"F0.wireOp",EDGE,"E11.78.3"),sQuery(id+"F0.wireOp",EDGE,"E11.78.4"),sQuery(id+"F0.wireOp",EDGE,"E11.78.5"),sQuery(id+"F0.wireOp",EDGE,"E11.78.6"),sQuery(id+"F0.wireOp",EDGE,"E11.78.7"),sQuery(id+"F0.wireOp",EDGE,"E11.79.0"),sQuery(id+"F0.wireOp",EDGE,"E11.79.1"),sQuery(id+"F0.wireOp",EDGE,"E11.79.2"),sQuery(id+"F0.wireOp",EDGE,"E11.79.3"),sQuery(id+"F0.wireOp",EDGE,"E11.79.4"),sQuery(id+"F0.wireOp",EDGE,"E11.79.5"),sQuery(id+"F0.wireOp",EDGE,"E11.79.6"),sQuery(id+"F0.wireOp",EDGE,"E11.79.7"),sQuery(id+"F0.wireOp",EDGE,"E11.80.0"),sQuery(id+"F0.wireOp",EDGE,"E11.80.1"),sQuery(id+"F0.wireOp",EDGE,"E11.80.2"),sQuery(id+"F0.wireOp",EDGE,"E11.80.3"),sQuery(id+"F0.wireOp",EDGE,"E11.80.4"),sQuery(id+"F0.wireOp",EDGE,"E11.80.5"),sQuery(id+"F0.wireOp",EDGE,"E11.80.6"),sQuery(id+"F0.wireOp",EDGE,"E11.80.7"),sQuery(id+"F0.wireOp",EDGE,"E11.81.0"),sQuery(id+"F0.wireOp",EDGE,"E11.81.1"),sQuery(id+"F0.wireOp",EDGE,"E11.81.2"),sQuery(id+"F0.wireOp",EDGE,"E11.81.3"),sQuery(id+"F0.wireOp",EDGE,"E11.81.4"),sQuery(id+"F0.wireOp",EDGE,"E11.81.5"),sQuery(id+"F0.wireOp",EDGE,"E11.81.6"),sQuery(id+"F0.wireOp",EDGE,"E11.81.7"),sQuery(id+"F0.wireOp",EDGE,"E11.82.0"),sQuery(id+"F0.wireOp",EDGE,"E11.82.1"),sQuery(id+"F0.wireOp",EDGE,"E11.82.2"),sQuery(id+"F0.wireOp",EDGE,"E11.82.3"),sQuery(id+"F0.wireOp",EDGE,"E11.82.4"),sQuery(id+"F0.wireOp",EDGE,"E11.82.5"),sQuery(id+"F0.wireOp",EDGE,"E11.82.6"),sQuery(id+"F0.wireOp",EDGE,"E11.82.7"),sQuery(id+"F0.wireOp",EDGE,"E11.83.0"),sQuery(id+"F0.wireOp",EDGE,"E11.83.1"),sQuery(id+"F0.wireOp",EDGE,"E11.83.2"),sQuery(id+"F0.wireOp",EDGE,"E11.83.3"),sQuery(id+"F0.wireOp",EDGE,"E11.83.4"),sQuery(id+"F0.wireOp",EDGE,"E11.83.5"),sQuery(id+"F0.wireOp",EDGE,"E11.83.6"),sQuery(id+"F0.wireOp",EDGE,"E11.83.7"),sQuery(id+"F0.wireOp",EDGE,"E11.84.0"),sQuery(id+"F0.wireOp",EDGE,"E11.84.1"),sQuery(id+"F0.wireOp",EDGE,"E11.84.2"),sQuery(id+"F0.wireOp",EDGE,"E11.84.3"),sQuery(id+"F0.wireOp",EDGE,"E11.84.4"),sQuery(id+"F0.wireOp",EDGE,"E11.84.5"),sQuery(id+"F0.wireOp",EDGE,"E11.84.6"),sQuery(id+"F0.wireOp",EDGE,"E11.84.7"),sQuery(id+"F0.wireOp",EDGE,"E11.85.0"),sQuery(id+"F0.wireOp",EDGE,"E11.85.1"),sQuery(id+"F0.wireOp",EDGE,"E11.85.2"),sQuery(id+"F0.wireOp",EDGE,"E11.85.3"),sQuery(id+"F0.wireOp",EDGE,"E11.85.4"),sQuery(id+"F0.wireOp",EDGE,"E11.85.5"),sQuery(id+"F0.wireOp",EDGE,"E11.85.6"),sQuery(id+"F0.wireOp",EDGE,"E11.85.7"),sQuery(id+"F0.wireOp",EDGE,"E11.86.0"),sQuery(id+"F0.wireOp",EDGE,"E11.86.1"),sQuery(id+"F0.wireOp",EDGE,"E11.86.2"),sQuery(id+"F0.wireOp",EDGE,"E11.86.3"),sQuery(id+"F0.wireOp",EDGE,"E11.86.4"),sQuery(id+"F0.wireOp",EDGE,"E11.86.5"),sQuery(id+"F0.wireOp",EDGE,"E11.86.6"),sQuery(id+"F0.wireOp",EDGE,"E11.86.7"),sQuery(id+"F0.wireOp",EDGE,"E11.87.0"),sQuery(id+"F0.wireOp",EDGE,"E11.87.1"),sQuery(id+"F0.wireOp",EDGE,"E11.87.2"),sQuery(id+"F0.wireOp",EDGE,"E11.87.3"),sQuery(id+"F0.wireOp",EDGE,"E11.87.4"),sQuery(id+"F0.wireOp",EDGE,"E11.87.5"),sQuery(id+"F0.wireOp",EDGE,"E11.87.6"),sQuery(id+"F0.wireOp",EDGE,"E11.87.7"),sQuery(id+"F0.wireOp",EDGE,"E11.88.0"),sQuery(id+"F0.wireOp",EDGE,"E11.88.1"),sQuery(id+"F0.wireOp",EDGE,"E11.88.2"),sQuery(id+"F0.wireOp",EDGE,"E11.88.3"),sQuery(id+"F0.wireOp",EDGE,"E11.88.4"),sQuery(id+"F0.wireOp",EDGE,"E11.88.5"),sQuery(id+"F0.wireOp",EDGE,"E11.88.6"),sQuery(id+"F0.wireOp",EDGE,"E11.88.7"),sQuery(id+"F0.wireOp",EDGE,"E11.89.0"),sQuery(id+"F0.wireOp",EDGE,"E11.89.1"),sQuery(id+"F0.wireOp",EDGE,"E11.89.2"),sQuery(id+"F0.wireOp",EDGE,"E11.89.3"),sQuery(id+"F0.wireOp",EDGE,"E11.89.4"),sQuery(id+"F0.wireOp",EDGE,"E11.89.5"),sQuery(id+"F0.wireOp",EDGE,"E11.89.6"),sQuery(id+"F0.wireOp",EDGE,"E11.89.7"),sQuery(id+"F0.wireOp",EDGE,"E11.90.0"),sQuery(id+"F0.wireOp",EDGE,"E11.90.1"),sQuery(id+"F0.wireOp",EDGE,"E11.90.2"),sQuery(id+"F0.wireOp",EDGE,"E11.90.3"),sQuery(id+"F0.wireOp",EDGE,"E11.90.4"),sQuery(id+"F0.wireOp",EDGE,"E11.90.5"),sQuery(id+"F0.wireOp",EDGE,"E11.90.6"),sQuery(id+"F0.wireOp",EDGE,"E11.90.7"),sQuery(id+"F0.wireOp",EDGE,"E11.91.0"),sQuery(id+"F0.wireOp",EDGE,"E11.91.1"),sQuery(id+"F0.wireOp",EDGE,"E11.91.2"),sQuery(id+"F0.wireOp",EDGE,"E11.91.3"),sQuery(id+"F0.wireOp",EDGE,"E11.91.4"),sQuery(id+"F0.wireOp",EDGE,"E11.91.5"),sQuery(id+"F0.wireOp",EDGE,"E11.91.6"),sQuery(id+"F0.wireOp",EDGE,"E11.91.7"),sQuery(id+"F0.wireOp",EDGE,"E11.92.0"),sQuery(id+"F0.wireOp",EDGE,"E11.92.1"),sQuery(id+"F0.wireOp",EDGE,"E11.92.2"),sQuery(id+"F0.wireOp",EDGE,"E11.92.3"),sQuery(id+"F0.wireOp",EDGE,"E11.92.4"),sQuery(id+"F0.wireOp",EDGE,"E11.92.5"),sQuery(id+"F0.wireOp",EDGE,"E11.92.6"),sQuery(id+"F0.wireOp",EDGE,"E11.92.7"),sQuery(id+"F0.wireOp",EDGE,"E11.93.0"),sQuery(id+"F0.wireOp",EDGE,"E11.93.1"),sQuery(id+"F0.wireOp",EDGE,"E11.93.2"),sQuery(id+"F0.wireOp",EDGE,"E11.93.3"),sQuery(id+"F0.wireOp",EDGE,"E11.93.4"),sQuery(id+"F0.wireOp",EDGE,"E11.93.5"),sQuery(id+"F0.wireOp",EDGE,"E11.93.6"),sQuery(id+"F0.wireOp",EDGE,"E11.93.7"),sQuery(id+"F0.wireOp",EDGE,"E11.94.0"),sQuery(id+"F0.wireOp",EDGE,"E11.94.1"),sQuery(id+"F0.wireOp",EDGE,"E11.94.2"),sQuery(id+"F0.wireOp",EDGE,"E11.94.3"),sQuery(id+"F0.wireOp",EDGE,"E11.94.4"),sQuery(id+"F0.wireOp",EDGE,"E11.94.5"),sQuery(id+"F0.wireOp",EDGE,"E11.94.6"),sQuery(id+"F0.wireOp",EDGE,"E11.94.7"),sQuery(id+"F0.wireOp",EDGE,"E11.95.0"),sQuery(id+"F0.wireOp",EDGE,"E11.95.1"),sQuery(id+"F0.wireOp",EDGE,"E11.95.2"),sQuery(id+"F0.wireOp",EDGE,"E11.95.3"),sQuery(id+"F0.wireOp",EDGE,"E11.95.4"),sQuery(id+"F0.wireOp",EDGE,"E11.95.5"),sQuery(id+"F0.wireOp",EDGE,"E11.95.6"),sQuery(id+"F0.wireOp",EDGE,"E11.95.7"),sQuery(id+"F0.wireOp",EDGE,"E11.96.0"),sQuery(id+"F0.wireOp",EDGE,"E11.96.1"),sQuery(id+"F0.wireOp",EDGE,"E11.96.2"),sQuery(id+"F0.wireOp",EDGE,"E11.96.3"),sQuery(id+"F0.wireOp",EDGE,"E11.96.4"),sQuery(id+"F0.wireOp",EDGE,"E11.96.5"),sQuery(id+"F0.wireOp",EDGE,"E11.96.6"),sQuery(id+"F0.wireOp",EDGE,"E11.96.7"),sQuery(id+"F0.wireOp",EDGE,"E11.97.0"),sQuery(id+"F0.wireOp",EDGE,"E11.97.1"),sQuery(id+"F0.wireOp",EDGE,"E11.97.2"),sQuery(id+"F0.wireOp",EDGE,"E11.97.3"),sQuery(id+"F0.wireOp",EDGE,"E11.97.4"),sQuery(id+"F0.wireOp",EDGE,"E11.97.5"),sQuery(id+"F0.wireOp",EDGE,"E11.97.6"),sQuery(id+"F0.wireOp",EDGE,"E11.97.7"),sQuery(id+"F0.wireOp",EDGE,"E11.98.0"),sQuery(id+"F0.wireOp",EDGE,"E11.98.1"),sQuery(id+"F0.wireOp",EDGE,"E11.98.2"),sQuery(id+"F0.wireOp",EDGE,"E11.98.3"),sQuery(id+"F0.wireOp",EDGE,"E11.98.4"),sQuery(id+"F0.wireOp",EDGE,"E11.98.5"),sQuery(id+"F0.wireOp",EDGE,"E11.98.6"),sQuery(id+"F0.wireOp",EDGE,"E11.98.7"),sQuery(id+"F0.wireOp",EDGE,"E11.99.0"),sQuery(id+"F0.wireOp",EDGE,"E11.99.1"),sQuery(id+"F0.wireOp",EDGE,"E11.99.2"),sQuery(id+"F0.wireOp",EDGE,"E11.99.3"),sQuery(id+"F0.wireOp",EDGE,"E11.99.4"),sQuery(id+"F0.wireOp",EDGE,"E11.99.5"),sQuery(id+"F0.wireOp",EDGE,"E11.99.6"),sQuery(id+"F0.wireOp",EDGE,"E11.99.7"),sQuery(id+"F0.wireOp",EDGE,"E11.100.0"),sQuery(id+"F0.wireOp",EDGE,"E11.100.1"),sQuery(id+"F0.wireOp",EDGE,"E11.100.2"),sQuery(id+"F0.wireOp",EDGE,"E11.100.3"),sQuery(id+"F0.wireOp",EDGE,"E11.100.4"),sQuery(id+"F0.wireOp",EDGE,"E11.100.5"),sQuery(id+"F0.wireOp",EDGE,"E11.100.6"),sQuery(id+"F0.wireOp",EDGE,"E11.100.7"),sQuery(id+"F0.wireOp",EDGE,"E11.101.0"),sQuery(id+"F0.wireOp",EDGE,"E11.101.1"),sQuery(id+"F0.wireOp",EDGE,"E11.101.2"),sQuery(id+"F0.wireOp",EDGE,"E11.101.3"),sQuery(id+"F0.wireOp",EDGE,"E11.101.4"),sQuery(id+"F0.wireOp",EDGE,"E11.101.5"),sQuery(id+"F0.wireOp",EDGE,"E11.101.6"),sQuery(id+"F0.wireOp",EDGE,"E11.101.7"),sQuery(id+"F0.wireOp",EDGE,"E11.102.0"),sQuery(id+"F0.wireOp",EDGE,"E11.102.1"),sQuery(id+"F0.wireOp",EDGE,"E11.102.2"),sQuery(id+"F0.wireOp",EDGE,"E11.102.3"),sQuery(id+"F0.wireOp",EDGE,"E11.102.4"),sQuery(id+"F0.wireOp",EDGE,"E11.102.5"),sQuery(id+"F0.wireOp",EDGE,"E11.102.6"),sQuery(id+"F0.wireOp",EDGE,"E11.102.7"),sQuery(id+"F0.wireOp",EDGE,"E11.103.0"),sQuery(id+"F0.wireOp",EDGE,"E11.103.1"),sQuery(id+"F0.wireOp",EDGE,"E11.103.2"),sQuery(id+"F0.wireOp",EDGE,"E11.103.3"),sQuery(id+"F0.wireOp",EDGE,"E11.103.4"),sQuery(id+"F0.wireOp",EDGE,"E11.103.5"),sQuery(id+"F0.wireOp",EDGE,"E11.103.6"),sQuery(id+"F0.wireOp",EDGE,"E11.103.7"),sQuery(id+"F0.wireOp",EDGE,"E11.104.0"),sQuery(id+"F0.wireOp",EDGE,"E11.104.1"),sQuery(id+"F0.wireOp",EDGE,"E11.104.2"),sQuery(id+"F0.wireOp",EDGE,"E11.104.3"),sQuery(id+"F0.wireOp",EDGE,"E11.104.4"),sQuery(id+"F0.wireOp",EDGE,"E11.104.5"),sQuery(id+"F0.wireOp",EDGE,"E11.104.6"),sQuery(id+"F0.wireOp",EDGE,"E11.104.7"),sQuery(id+"F0.wireOp",EDGE,"E11.105.0"),sQuery(id+"F0.wireOp",EDGE,"E11.105.1"),sQuery(id+"F0.wireOp",EDGE,"E11.105.2"),sQuery(id+"F0.wireOp",EDGE,"E11.105.3"),sQuery(id+"F0.wireOp",EDGE,"E11.105.4"),sQuery(id+"F0.wireOp",EDGE,"E11.105.5"),sQuery(id+"F0.wireOp",EDGE,"E11.105.6"),sQuery(id+"F0.wireOp",EDGE,"E11.105.7"),sQuery(id+"F0.wireOp",EDGE,"E11.106.0"),sQuery(id+"F0.wireOp",EDGE,"E11.106.1"),sQuery(id+"F0.wireOp",EDGE,"E11.106.2"),sQuery(id+"F0.wireOp",EDGE,"E11.106.3"),sQuery(id+"F0.wireOp",EDGE,"E11.106.4"),sQuery(id+"F0.wireOp",EDGE,"E11.106.5"),sQuery(id+"F0.wireOp",EDGE,"E11.106.6"),sQuery(id+"F0.wireOp",EDGE,"E11.106.7"),sQuery(id+"F0.wireOp",EDGE,"E11.107.0"),sQuery(id+"F0.wireOp",EDGE,"E11.107.1"),sQuery(id+"F0.wireOp",EDGE,"E11.107.2"),sQuery(id+"F0.wireOp",EDGE,"E11.107.3"),sQuery(id+"F0.wireOp",EDGE,"E11.107.4"),sQuery(id+"F0.wireOp",EDGE,"E11.107.5"),sQuery(id+"F0.wireOp",EDGE,"E11.107.6"),sQuery(id+"F0.wireOp",EDGE,"E11.107.7"),sQuery(id+"F0.wireOp",EDGE,"E11.108.0"),sQuery(id+"F0.wireOp",EDGE,"E11.108.1"),sQuery(id+"F0.wireOp",EDGE,"E11.108.2"),sQuery(id+"F0.wireOp",EDGE,"E11.108.3"),sQuery(id+"F0.wireOp",EDGE,"E11.108.4"),sQuery(id+"F0.wireOp",EDGE,"E11.108.5"),sQuery(id+"F0.wireOp",EDGE,"E11.108.6"),sQuery(id+"F0.wireOp",EDGE,"E11.108.7"),sQuery(id+"F0.wireOp",EDGE,"E11.109.0"),sQuery(id+"F0.wireOp",EDGE,"E11.109.1"),sQuery(id+"F0.wireOp",EDGE,"E11.109.2"),sQuery(id+"F0.wireOp",EDGE,"E11.109.3"),sQuery(id+"F0.wireOp",EDGE,"E11.109.4"),sQuery(id+"F0.wireOp",EDGE,"E11.109.5"),sQuery(id+"F0.wireOp",EDGE,"E11.109.6"),sQuery(id+"F0.wireOp",EDGE,"E11.109.7"),sQuery(id+"F0.wireOp",EDGE,"E11.110.0"),sQuery(id+"F0.wireOp",EDGE,"E11.110.1"),sQuery(id+"F0.wireOp",EDGE,"E11.110.2"),sQuery(id+"F0.wireOp",EDGE,"E11.110.3"),sQuery(id+"F0.wireOp",EDGE,"E11.110.4"),sQuery(id+"F0.wireOp",EDGE,"E11.110.5"),sQuery(id+"F0.wireOp",EDGE,"E11.110.6"),sQuery(id+"F0.wireOp",EDGE,"E11.110.7"),sQuery(id+"F0.wireOp",EDGE,"E11.111.0"),sQuery(id+"F0.wireOp",EDGE,"E11.111.1"),sQuery(id+"F0.wireOp",EDGE,"E11.111.2"),sQuery(id+"F0.wireOp",EDGE,"E11.111.3"),sQuery(id+"F0.wireOp",EDGE,"E11.111.4"),sQuery(id+"F0.wireOp",EDGE,"E11.111.5"),sQuery(id+"F0.wireOp",EDGE,"E11.111.6"),sQuery(id+"F0.wireOp",EDGE,"E11.111.7"),sQuery(id+"F0.wireOp",EDGE,"E11.112.0"),sQuery(id+"F0.wireOp",EDGE,"E11.112.1"),sQuery(id+"F0.wireOp",EDGE,"E11.112.2"),sQuery(id+"F0.wireOp",EDGE,"E11.112.3"),sQuery(id+"F0.wireOp",EDGE,"E11.112.4"),sQuery(id+"F0.wireOp",EDGE,"E11.112.5"),sQuery(id+"F0.wireOp",EDGE,"E11.112.6"),sQuery(id+"F0.wireOp",EDGE,"E11.112.7"),sQuery(id+"F0.wireOp",EDGE,"E11.113.0"),sQuery(id+"F0.wireOp",EDGE,"E11.113.1"),sQuery(id+"F0.wireOp",EDGE,"E11.113.2"),sQuery(id+"F0.wireOp",EDGE,"E11.113.3"),sQuery(id+"F0.wireOp",EDGE,"E11.113.4"),sQuery(id+"F0.wireOp",EDGE,"E11.113.5"),sQuery(id+"F0.wireOp",EDGE,"E11.113.6"),sQuery(id+"F0.wireOp",EDGE,"E11.113.7"),sQuery(id+"F0.wireOp",EDGE,"E11.114.0"),sQuery(id+"F0.wireOp",EDGE,"E11.114.1"),sQuery(id+"F0.wireOp",EDGE,"E11.114.2"),sQuery(id+"F0.wireOp",EDGE,"E11.114.3"),sQuery(id+"F0.wireOp",EDGE,"E11.114.4"),sQuery(id+"F0.wireOp",EDGE,"E11.114.5"),sQuery(id+"F0.wireOp",EDGE,"E11.114.6"),sQuery(id+"F0.wireOp",EDGE,"E11.114.7"),sQuery(id+"F0.wireOp",EDGE,"E11.115.0"),sQuery(id+"F0.wireOp",EDGE,"E11.115.1"),sQuery(id+"F0.wireOp",EDGE,"E11.115.2"),sQuery(id+"F0.wireOp",EDGE,"E11.115.3"),sQuery(id+"F0.wireOp",EDGE,"E11.115.4"),sQuery(id+"F0.wireOp",EDGE,"E11.115.5"),sQuery(id+"F0.wireOp",EDGE,"E11.115.6"),sQuery(id+"F0.wireOp",EDGE,"E11.115.7"),sQuery(id+"F0.wireOp",EDGE,"E11.116.0"),sQuery(id+"F0.wireOp",EDGE,"E11.116.1"),sQuery(id+"F0.wireOp",EDGE,"E11.116.2"),sQuery(id+"F0.wireOp",EDGE,"E11.116.3"),sQuery(id+"F0.wireOp",EDGE,"E11.116.4"),sQuery(id+"F0.wireOp",EDGE,"E11.116.5"),sQuery(id+"F0.wireOp",EDGE,"E11.116.6"),sQuery(id+"F0.wireOp",EDGE,"E11.116.7"),sQuery(id+"F0.wireOp",EDGE,"E11.117.0"),sQuery(id+"F0.wireOp",EDGE,"E11.117.1"),sQuery(id+"F0.wireOp",EDGE,"E11.117.2"),sQuery(id+"F0.wireOp",EDGE,"E11.117.3"),sQuery(id+"F0.wireOp",EDGE,"E11.117.4"),sQuery(id+"F0.wireOp",EDGE,"E11.117.5"),sQuery(id+"F0.wireOp",EDGE,"E11.117.6"),sQuery(id+"F0.wireOp",EDGE,"E11.117.7"),sQuery(id+"F0.wireOp",EDGE,"E11.118.0"),sQuery(id+"F0.wireOp",EDGE,"E11.118.1"),sQuery(id+"F0.wireOp",EDGE,"E11.118.2"),sQuery(id+"F0.wireOp",EDGE,"E11.118.3"),sQuery(id+"F0.wireOp",EDGE,"E11.118.4"),sQuery(id+"F0.wireOp",EDGE,"E11.118.5"),sQuery(id+"F0.wireOp",EDGE,"E11.118.6"),sQuery(id+"F0.wireOp",EDGE,"E11.118.7"),sQuery(id+"F0.wireOp",EDGE,"E11.119.0"),sQuery(id+"F0.wireOp",EDGE,"E11.119.1"),sQuery(id+"F0.wireOp",EDGE,"E11.119.2"),sQuery(id+"F0.wireOp",EDGE,"E11.119.3"),sQuery(id+"F0.wireOp",EDGE,"E11.119.4"),sQuery(id+"F0.wireOp",EDGE,"E11.119.5"),sQuery(id+"F0.wireOp",EDGE,"E11.119.6"),sQuery(id+"F0.wireOp",EDGE,"E11.119.7"),sQuery(id+"F0.wireOp",EDGE,"E11.120.0"),sQuery(id+"F0.wireOp",EDGE,"E11.120.1"),sQuery(id+"F0.wireOp",EDGE,"E11.120.2"),sQuery(id+"F0.wireOp",EDGE,"E11.120.3"),sQuery(id+"F0.wireOp",EDGE,"E11.120.4"),sQuery(id+"F0.wireOp",EDGE,"E11.120.5"),sQuery(id+"F0.wireOp",EDGE,"E11.120.6"),sQuery(id+"F0.wireOp",EDGE,"E11.120.7"),sQuery(id+"F0.wireOp",EDGE,"E11.121.0"),sQuery(id+"F0.wireOp",EDGE,"E11.121.1"),sQuery(id+"F0.wireOp",EDGE,"E11.121.2"),sQuery(id+"F0.wireOp",EDGE,"E11.121.3"),sQuery(id+"F0.wireOp",EDGE,"E11.121.4"),sQuery(id+"F0.wireOp",EDGE,"E11.121.5"),sQuery(id+"F0.wireOp",EDGE,"E11.121.6"),sQuery(id+"F0.wireOp",EDGE,"E11.121.7"),sQuery(id+"F0.wireOp",EDGE,"E11.122.0"),sQuery(id+"F0.wireOp",EDGE,"E11.122.1"),sQuery(id+"F0.wireOp",EDGE,"E11.122.2"),sQuery(id+"F0.wireOp",EDGE,"E11.122.3"),sQuery(id+"F0.wireOp",EDGE,"E11.122.4"),sQuery(id+"F0.wireOp",EDGE,"E11.122.5"),sQuery(id+"F0.wireOp",EDGE,"E11.122.6"),sQuery(id+"F0.wireOp",EDGE,"E11.122.7"),sQuery(id+"F0.wireOp",EDGE,"E11.123.0"),sQuery(id+"F0.wireOp",EDGE,"E11.123.1"),sQuery(id+"F0.wireOp",EDGE,"E11.123.2"),sQuery(id+"F0.wireOp",EDGE,"E11.123.3"),sQuery(id+"F0.wireOp",EDGE,"E11.123.4"),sQuery(id+"F0.wireOp",EDGE,"E11.123.5"),sQuery(id+"F0.wireOp",EDGE,"E11.123.6"),sQuery(id+"F0.wireOp",EDGE,"E11.123.7"),sQuery(id+"F0.wireOp",EDGE,"E11.124.0"),sQuery(id+"F0.wireOp",EDGE,"E11.124.1"),sQuery(id+"F0.wireOp",EDGE,"E11.124.2"),sQuery(id+"F0.wireOp",EDGE,"E11.124.3"),sQuery(id+"F0.wireOp",EDGE,"E11.124.4"),sQuery(id+"F0.wireOp",EDGE,"E11.124.5"),sQuery(id+"F0.wireOp",EDGE,"E11.124.6"),sQuery(id+"F0.wireOp",EDGE,"E11.124.7"),sQuery(id+"F0.wireOp",EDGE,"E11.125.0"),sQuery(id+"F0.wireOp",EDGE,"E11.125.1"),sQuery(id+"F0.wireOp",EDGE,"E11.125.2"),sQuery(id+"F0.wireOp",EDGE,"E11.125.3"),sQuery(id+"F0.wireOp",EDGE,"E11.125.4"),sQuery(id+"F0.wireOp",EDGE,"E11.125.5"),sQuery(id+"F0.wireOp",EDGE,"E11.125.6"),sQuery(id+"F0.wireOp",EDGE,"E11.125.7"),sQuery(id+"F0.wireOp",EDGE,"E11.126.0"),sQuery(id+"F0.wireOp",EDGE,"E11.126.1"),sQuery(id+"F0.wireOp",EDGE,"E11.126.2"),sQuery(id+"F0.wireOp",EDGE,"E11.126.3"),sQuery(id+"F0.wireOp",EDGE,"E11.126.4"),sQuery(id+"F0.wireOp",EDGE,"E11.126.5"),sQuery(id+"F0.wireOp",EDGE,"E11.126.6"),sQuery(id+"F0.wireOp",EDGE,"E11.126.7"),sQuery(id+"F0.wireOp",EDGE,"E11.127.0"),sQuery(id+"F0.wireOp",EDGE,"E11.127.1"),sQuery(id+"F0.wireOp",EDGE,"E11.127.2"),sQuery(id+"F0.wireOp",EDGE,"E11.127.3"),sQuery(id+"F0.wireOp",EDGE,"E11.127.4"),sQuery(id+"F0.wireOp",EDGE,"E11.127.5"),sQuery(id+"F0.wireOp",EDGE,"E11.127.6"),sQuery(id+"F0.wireOp",EDGE,"E11.127.7"),sQuery(id+"F0.wireOp",EDGE,"E11.128.0"),sQuery(id+"F0.wireOp",EDGE,"E11.128.1"),sQuery(id+"F0.wireOp",EDGE,"E11.128.2"),sQuery(id+"F0.wireOp",EDGE,"E11.128.3"),sQuery(id+"F0.wireOp",EDGE,"E11.128.4"),sQuery(id+"F0.wireOp",EDGE,"E11.128.5"),sQuery(id+"F0.wireOp",EDGE,"E11.128.6"),sQuery(id+"F0.wireOp",EDGE,"E11.128.7"),sQuery(id+"F0.wireOp",EDGE,"E11.129.0"),sQuery(id+"F0.wireOp",EDGE,"E11.129.1"),sQuery(id+"F0.wireOp",EDGE,"E11.129.2"),sQuery(id+"F0.wireOp",EDGE,"E11.129.3"),sQuery(id+"F0.wireOp",EDGE,"E11.129.4"),sQuery(id+"F0.wireOp",EDGE,"E11.129.5"),sQuery(id+"F0.wireOp",EDGE,"E11.129.6"),sQuery(id+"F0.wireOp",EDGE,"E11.129.7"),sQuery(id+"F0.wireOp",EDGE,"E11.130.0"),sQuery(id+"F0.wireOp",EDGE,"E11.130.1"),sQuery(id+"F0.wireOp",EDGE,"E11.130.2"),sQuery(id+"F0.wireOp",EDGE,"E11.130.3"),sQuery(id+"F0.wireOp",EDGE,"E11.130.4"),sQuery(id+"F0.wireOp",EDGE,"E11.130.5"),sQuery(id+"F0.wireOp",EDGE,"E11.130.6"),sQuery(id+"F0.wireOp",EDGE,"E11.130.7"),sQuery(id+"F0.wireOp",EDGE,"E11.131.0"),sQuery(id+"F0.wireOp",EDGE,"E11.131.1"),sQuery(id+"F0.wireOp",EDGE,"E11.131.2"),sQuery(id+"F0.wireOp",EDGE,"E11.131.3"),sQuery(id+"F0.wireOp",EDGE,"E11.131.4"),sQuery(id+"F0.wireOp",EDGE,"E11.131.5"),sQuery(id+"F0.wireOp",EDGE,"E11.131.6"),sQuery(id+"F0.wireOp",EDGE,"E11.131.7"),sQuery(id+"F0.wireOp",EDGE,"E11.132.0"),sQuery(id+"F0.wireOp",EDGE,"E11.132.1"),sQuery(id+"F0.wireOp",EDGE,"E11.132.2"),sQuery(id+"F0.wireOp",EDGE,"E11.132.3"),sQuery(id+"F0.wireOp",EDGE,"E11.132.4"),sQuery(id+"F0.wireOp",EDGE,"E11.132.5"),sQuery(id+"F0.wireOp",EDGE,"E11.132.6"),sQuery(id+"F0.wireOp",EDGE,"E11.132.7"),sQuery(id+"F0.wireOp",EDGE,"E11.133.0"),sQuery(id+"F0.wireOp",EDGE,"E11.133.1"),sQuery(id+"F0.wireOp",EDGE,"E11.133.2"),sQuery(id+"F0.wireOp",EDGE,"E11.133.3"),sQuery(id+"F0.wireOp",EDGE,"E11.133.4"),sQuery(id+"F0.wireOp",EDGE,"E11.133.5"),sQuery(id+"F0.wireOp",EDGE,"E11.133.6"),sQuery(id+"F0.wireOp",EDGE,"E11.133.7"),sQuery(id+"F0.wireOp",EDGE,"E11.134.0"),sQuery(id+"F0.wireOp",EDGE,"E11.134.1"),sQuery(id+"F0.wireOp",EDGE,"E11.134.2"),sQuery(id+"F0.wireOp",EDGE,"E11.134.3"),sQuery(id+"F0.wireOp",EDGE,"E11.134.4"),sQuery(id+"F0.wireOp",EDGE,"E11.134.5"),sQuery(id+"F0.wireOp",EDGE,"E11.134.6"),sQuery(id+"F0.wireOp",EDGE,"E11.134.7"),sQuery(id+"F0.wireOp",EDGE,"E11.135.0"),sQuery(id+"F0.wireOp",EDGE,"E11.135.1"),sQuery(id+"F0.wireOp",EDGE,"E11.135.2"),sQuery(id+"F0.wireOp",EDGE,"E11.135.3"),sQuery(id+"F0.wireOp",EDGE,"E11.135.4"),sQuery(id+"F0.wireOp",EDGE,"E11.135.5"),sQuery(id+"F0.wireOp",EDGE,"E11.135.6"),sQuery(id+"F0.wireOp",EDGE,"E11.135.7"),sQuery(id+"F0.wireOp",EDGE,"E11.136.0"),sQuery(id+"F0.wireOp",EDGE,"E11.136.1"),sQuery(id+"F0.wireOp",EDGE,"E11.136.2"),sQuery(id+"F0.wireOp",EDGE,"E11.136.3"),sQuery(id+"F0.wireOp",EDGE,"E11.136.4"),sQuery(id+"F0.wireOp",EDGE,"E11.136.5"),sQuery(id+"F0.wireOp",EDGE,"E11.136.6"),sQuery(id+"F0.wireOp",EDGE,"E11.136.7"),sQuery(id+"F0.wireOp",EDGE,"E11.137.0"),sQuery(id+"F0.wireOp",EDGE,"E11.137.1"),sQuery(id+"F0.wireOp",EDGE,"E11.137.2"),sQuery(id+"F0.wireOp",EDGE,"E11.137.3"),sQuery(id+"F0.wireOp",EDGE,"E11.137.4"),sQuery(id+"F0.wireOp",EDGE,"E11.137.5"),sQuery(id+"F0.wireOp",EDGE,"E11.137.6"),sQuery(id+"F0.wireOp",EDGE,"E11.137.7"),sQuery(id+"F0.wireOp",EDGE,"E11.138.0"),sQuery(id+"F0.wireOp",EDGE,"E11.138.1"),sQuery(id+"F0.wireOp",EDGE,"E11.138.2"),sQuery(id+"F0.wireOp",EDGE,"E11.138.3"),sQuery(id+"F0.wireOp",EDGE,"E11.138.4"),sQuery(id+"F0.wireOp",EDGE,"E11.138.5"),sQuery(id+"F0.wireOp",EDGE,"E11.138.6"),sQuery(id+"F0.wireOp",EDGE,"E11.138.7"),sQuery(id+"F0.wireOp",EDGE,"E11.139.0"),sQuery(id+"F0.wireOp",EDGE,"E11.139.1"),sQuery(id+"F0.wireOp",EDGE,"E11.139.2"),sQuery(id+"F0.wireOp",EDGE,"E11.139.3"),sQuery(id+"F0.wireOp",EDGE,"E11.139.4"),sQuery(id+"F0.wireOp",EDGE,"E11.139.5"),sQuery(id+"F0.wireOp",EDGE,"E11.139.6"),sQuery(id+"F0.wireOp",EDGE,"E11.139.7"),sQuery(id+"F0.wireOp",EDGE,"E11.140.0"),sQuery(id+"F0.wireOp",EDGE,"E11.140.1"),sQuery(id+"F0.wireOp",EDGE,"E11.140.2"),sQuery(id+"F0.wireOp",EDGE,"E11.140.3"),sQuery(id+"F0.wireOp",EDGE,"E11.140.4"),sQuery(id+"F0.wireOp",EDGE,"E11.140.5"),sQuery(id+"F0.wireOp",EDGE,"E11.140.6"),sQuery(id+"F0.wireOp",EDGE,"E11.140.7"),sQuery(id+"F0.wireOp",EDGE,"E11.141.0"),sQuery(id+"F0.wireOp",EDGE,"E11.141.1"),sQuery(id+"F0.wireOp",EDGE,"E11.141.2"),sQuery(id+"F0.wireOp",EDGE,"E11.141.3"),sQuery(id+"F0.wireOp",EDGE,"E11.141.4"),sQuery(id+"F0.wireOp",EDGE,"E11.141.5"),sQuery(id+"F0.wireOp",EDGE,"E11.141.6"),sQuery(id+"F0.wireOp",EDGE,"E11.141.7"),sQuery(id+"F0.wireOp",EDGE,"E11.142.0"),sQuery(id+"F0.wireOp",EDGE,"E11.142.1"),sQuery(id+"F0.wireOp",EDGE,"E11.142.2"),sQuery(id+"F0.wireOp",EDGE,"E11.142.3"),sQuery(id+"F0.wireOp",EDGE,"E11.142.4"),sQuery(id+"F0.wireOp",EDGE,"E11.142.5"),sQuery(id+"F0.wireOp",EDGE,"E11.142.6"),sQuery(id+"F0.wireOp",EDGE,"E11.142.7"),sQuery(id+"F0.wireOp",EDGE,"E11.143.0"),sQuery(id+"F0.wireOp",EDGE,"E11.143.1"),sQuery(id+"F0.wireOp",EDGE,"E11.143.2"),sQuery(id+"F0.wireOp",EDGE,"E11.143.3"),sQuery(id+"F0.wireOp",EDGE,"E11.143.4"),sQuery(id+"F0.wireOp",EDGE,"E11.143.5"),sQuery(id+"F0.wireOp",EDGE,"E11.143.6"),sQuery(id+"F0.wireOp",EDGE,"E11.143.7"),sQuery(id+"F0.wireOp",EDGE,"E11.144.0"),sQuery(id+"F0.wireOp",EDGE,"E11.144.1"),sQuery(id+"F0.wireOp",EDGE,"E11.144.2"),sQuery(id+"F0.wireOp",EDGE,"E11.144.3"),sQuery(id+"F0.wireOp",EDGE,"E11.144.4"),sQuery(id+"F0.wireOp",EDGE,"E11.144.5"),sQuery(id+"F0.wireOp",EDGE,"E11.144.6"),sQuery(id+"F0.wireOp",EDGE,"E11.144.7"),sQuery(id+"F0.wireOp",EDGE,"E11.145.0"),sQuery(id+"F0.wireOp",EDGE,"E11.145.1"),sQuery(id+"F0.wireOp",EDGE,"E11.145.2"),sQuery(id+"F0.wireOp",EDGE,"E11.145.3"),sQuery(id+"F0.wireOp",EDGE,"E11.145.4"),sQuery(id+"F0.wireOp",EDGE,"E11.145.5"),sQuery(id+"F0.wireOp",EDGE,"E11.145.6"),sQuery(id+"F0.wireOp",EDGE,"E11.145.7"),sQuery(id+"F0.wireOp",EDGE,"E11.146.0"),sQuery(id+"F0.wireOp",EDGE,"E11.146.1"),sQuery(id+"F0.wireOp",EDGE,"E11.146.2"),sQuery(id+"F0.wireOp",EDGE,"E11.146.3"),sQuery(id+"F0.wireOp",EDGE,"E11.146.4"),sQuery(id+"F0.wireOp",EDGE,"E11.146.5"),sQuery(id+"F0.wireOp",EDGE,"E11.146.6"),sQuery(id+"F0.wireOp",EDGE,"E11.146.7"),sQuery(id+"F0.wireOp",EDGE,"E11.147.0"),sQuery(id+"F0.wireOp",EDGE,"E11.147.1"),sQuery(id+"F0.wireOp",EDGE,"E11.147.2"),sQuery(id+"F0.wireOp",EDGE,"E11.147.3"),sQuery(id+"F0.wireOp",EDGE,"E11.147.4"),sQuery(id+"F0.wireOp",EDGE,"E11.147.5"),sQuery(id+"F0.wireOp",EDGE,"E11.147.6"),sQuery(id+"F0.wireOp",EDGE,"E11.147.7"),sQuery(id+"F0.wireOp",EDGE,"E11.148.0"),sQuery(id+"F0.wireOp",EDGE,"E11.148.1"),sQuery(id+"F0.wireOp",EDGE,"E11.148.2"),sQuery(id+"F0.wireOp",EDGE,"E11.148.3"),sQuery(id+"F0.wireOp",EDGE,"E11.148.4"),sQuery(id+"F0.wireOp",EDGE,"E11.148.5"),sQuery(id+"F0.wireOp",EDGE,"E11.148.6"),sQuery(id+"F0.wireOp",EDGE,"E11.148.7"),sQuery(id+"F0.wireOp",EDGE,"E11.149.0"),sQuery(id+"F0.wireOp",EDGE,"E11.149.1"),sQuery(id+"F0.wireOp",EDGE,"E11.149.2"),sQuery(id+"F0.wireOp",EDGE,"E11.149.3"),sQuery(id+"F0.wireOp",EDGE,"E11.149.4"),sQuery(id+"F0.wireOp",EDGE,"E11.149.5"),sQuery(id+"F0.wireOp",EDGE,"E11.149.6"),sQuery(id+"F0.wireOp",EDGE,"E11.149.7"),sQuery(id+"F0.wireOp",EDGE,"E11.150.0"),sQuery(id+"F0.wireOp",EDGE,"E11.150.1"),sQuery(id+"F0.wireOp",EDGE,"E11.150.2"),sQuery(id+"F0.wireOp",EDGE,"E11.150.3"),sQuery(id+"F0.wireOp",EDGE,"E11.150.4"),sQuery(id+"F0.wireOp",EDGE,"E11.150.5"),sQuery(id+"F0.wireOp",EDGE,"E11.150.6"),sQuery(id+"F0.wireOp",EDGE,"E11.150.7"),sQuery(id+"F0.wireOp",EDGE,"E11.151.0"),sQuery(id+"F0.wireOp",EDGE,"E11.151.1"),sQuery(id+"F0.wireOp",EDGE,"E11.151.2"),sQuery(id+"F0.wireOp",EDGE,"E11.151.3"),sQuery(id+"F0.wireOp",EDGE,"E11.151.4"),sQuery(id+"F0.wireOp",EDGE,"E11.151.5"),sQuery(id+"F0.wireOp",EDGE,"E11.151.6"),sQuery(id+"F0.wireOp",EDGE,"E11.151.7"),sQuery(id+"F0.wireOp",EDGE,"E11.152.0"),sQuery(id+"F0.wireOp",EDGE,"E11.152.1"),sQuery(id+"F0.wireOp",EDGE,"E11.152.2"),sQuery(id+"F0.wireOp",EDGE,"E11.152.3"),sQuery(id+"F0.wireOp",EDGE,"E11.152.4"),sQuery(id+"F0.wireOp",EDGE,"E11.152.5"),sQuery(id+"F0.wireOp",EDGE,"E11.152.6"),sQuery(id+"F0.wireOp",EDGE,"E11.152.7"),sQuery(id+"F0.wireOp",EDGE,"E11.153.0"),sQuery(id+"F0.wireOp",EDGE,"E11.153.1"),sQuery(id+"F0.wireOp",EDGE,"E11.153.2"),sQuery(id+"F0.wireOp",EDGE,"E11.153.3"),sQuery(id+"F0.wireOp",EDGE,"E11.153.4"),sQuery(id+"F0.wireOp",EDGE,"E11.153.5"),sQuery(id+"F0.wireOp",EDGE,"E11.153.6"),sQuery(id+"F0.wireOp",EDGE,"E11.153.7"),sQuery(id+"F0.wireOp",EDGE,"E11.154.0"),sQuery(id+"F0.wireOp",EDGE,"E11.154.1"),sQuery(id+"F0.wireOp",EDGE,"E11.154.2"),sQuery(id+"F0.wireOp",EDGE,"E11.154.3"),sQuery(id+"F0.wireOp",EDGE,"E11.154.4"),sQuery(id+"F0.wireOp",EDGE,"E11.154.5"),sQuery(id+"F0.wireOp",EDGE,"E11.154.6"),sQuery(id+"F0.wireOp",EDGE,"E11.154.7"),sQuery(id+"F0.wireOp",EDGE,"E11.155.0"),sQuery(id+"F0.wireOp",EDGE,"E11.155.1"),sQuery(id+"F0.wireOp",EDGE,"E11.155.2"),sQuery(id+"F0.wireOp",EDGE,"E11.155.3"),sQuery(id+"F0.wireOp",EDGE,"E11.155.4"),sQuery(id+"F0.wireOp",EDGE,"E11.155.5"),sQuery(id+"F0.wireOp",EDGE,"E11.155.6"),sQuery(id+"F0.wireOp",EDGE,"E11.155.7"),sQuery(id+"F0.wireOp",EDGE,"E11.156.0"),sQuery(id+"F0.wireOp",EDGE,"E11.156.1"),sQuery(id+"F0.wireOp",EDGE,"E11.156.2"),sQuery(id+"F0.wireOp",EDGE,"E11.156.3"),sQuery(id+"F0.wireOp",EDGE,"E11.156.4"),sQuery(id+"F0.wireOp",EDGE,"E11.156.5"),sQuery(id+"F0.wireOp",EDGE,"E11.156.6"),sQuery(id+"F0.wireOp",EDGE,"E11.156.7"),sQuery(id+"F0.wireOp",EDGE,"E11.157.0"),sQuery(id+"F0.wireOp",EDGE,"E11.157.1"),sQuery(id+"F0.wireOp",EDGE,"E11.157.2"),sQuery(id+"F0.wireOp",EDGE,"E11.157.3"),sQuery(id+"F0.wireOp",EDGE,"E11.157.4"),sQuery(id+"F0.wireOp",EDGE,"E11.157.5"),sQuery(id+"F0.wireOp",EDGE,"E11.157.6"),sQuery(id+"F0.wireOp",EDGE,"E11.157.7"),sQuery(id+"F0.wireOp",EDGE,"E11.158.0"),sQuery(id+"F0.wireOp",EDGE,"E11.158.1"),sQuery(id+"F0.wireOp",EDGE,"E11.158.2"),sQuery(id+"F0.wireOp",EDGE,"E11.158.3"),sQuery(id+"F0.wireOp",EDGE,"E11.158.4"),sQuery(id+"F0.wireOp",EDGE,"E11.158.5"),sQuery(id+"F0.wireOp",EDGE,"E11.158.6"),sQuery(id+"F0.wireOp",EDGE,"E11.158.7"),sQuery(id+"F0.wireOp",EDGE,"E11.159.0"),sQuery(id+"F0.wireOp",EDGE,"E11.159.1"),sQuery(id+"F0.wireOp",EDGE,"E11.159.2"),sQuery(id+"F0.wireOp",EDGE,"E11.159.3"),sQuery(id+"F0.wireOp",EDGE,"E11.159.4"),sQuery(id+"F0.wireOp",EDGE,"E11.159.5"),sQuery(id+"F0.wireOp",EDGE,"E11.159.6"),sQuery(id+"F0.wireOp",EDGE,"E11.159.7"),sQuery(id+"F0.wireOp",EDGE,"E11.160.0"),sQuery(id+"F0.wireOp",EDGE,"E11.160.1"),sQuery(id+"F0.wireOp",EDGE,"E11.160.2"),sQuery(id+"F0.wireOp",EDGE,"E11.160.3"),sQuery(id+"F0.wireOp",EDGE,"E11.160.4"),sQuery(id+"F0.wireOp",EDGE,"E11.160.5"),sQuery(id+"F0.wireOp",EDGE,"E11.160.6"),sQuery(id+"F0.wireOp",EDGE,"E11.160.7"),sQuery(id+"F0.wireOp",EDGE,"E11.161.0"),sQuery(id+"F0.wireOp",EDGE,"E11.161.1"),sQuery(id+"F0.wireOp",EDGE,"E11.161.2"),sQuery(id+"F0.wireOp",EDGE,"E11.161.3"),sQuery(id+"F0.wireOp",EDGE,"E11.161.4"),sQuery(id+"F0.wireOp",EDGE,"E11.161.5"),sQuery(id+"F0.wireOp",EDGE,"E11.161.6"),sQuery(id+"F0.wireOp",EDGE,"E11.161.7"),sQuery(id+"F0.wireOp",EDGE,"E11.162.0"),sQuery(id+"F0.wireOp",EDGE,"E11.162.1"),sQuery(id+"F0.wireOp",EDGE,"E11.162.2"),sQuery(id+"F0.wireOp",EDGE,"E11.162.3"),sQuery(id+"F0.wireOp",EDGE,"E11.162.4"),sQuery(id+"F0.wireOp",EDGE,"E11.162.5"),sQuery(id+"F0.wireOp",EDGE,"E11.162.6"),sQuery(id+"F0.wireOp",EDGE,"E11.162.7"),sQuery(id+"F0.wireOp",EDGE,"E11.163.0"),sQuery(id+"F0.wireOp",EDGE,"E11.163.1"),sQuery(id+"F0.wireOp",EDGE,"E11.163.2"),sQuery(id+"F0.wireOp",EDGE,"E11.163.3"),sQuery(id+"F0.wireOp",EDGE,"E11.163.4"),sQuery(id+"F0.wireOp",EDGE,"E11.163.5"),sQuery(id+"F0.wireOp",EDGE,"E11.163.6"),sQuery(id+"F0.wireOp",EDGE,"E11.163.7"),sQuery(id+"F0.wireOp",EDGE,"E11.164.0"),sQuery(id+"F0.wireOp",EDGE,"E11.164.1"),sQuery(id+"F0.wireOp",EDGE,"E11.164.2"),sQuery(id+"F0.wireOp",EDGE,"E11.164.3"),sQuery(id+"F0.wireOp",EDGE,"E11.164.4"),sQuery(id+"F0.wireOp",EDGE,"E11.164.5"),sQuery(id+"F0.wireOp",EDGE,"E11.164.6"),sQuery(id+"F0.wireOp",EDGE,"E11.164.7"),sQuery(id+"F0.wireOp",EDGE,"E11.165.0"),sQuery(id+"F0.wireOp",EDGE,"E11.165.1"),sQuery(id+"F0.wireOp",EDGE,"E11.165.2"),sQuery(id+"F0.wireOp",EDGE,"E11.165.3"),sQuery(id+"F0.wireOp",EDGE,"E11.165.4"),sQuery(id+"F0.wireOp",EDGE,"E11.165.5"),sQuery(id+"F0.wireOp",EDGE,"E11.165.6"),sQuery(id+"F0.wireOp",EDGE,"E11.165.7"),sQuery(id+"F0.wireOp",EDGE,"E11.166.0"),sQuery(id+"F0.wireOp",EDGE,"E11.166.1"),sQuery(id+"F0.wireOp",EDGE,"E11.166.2"),sQuery(id+"F0.wireOp",EDGE,"E11.166.3"),sQuery(id+"F0.wireOp",EDGE,"E11.166.4"),sQuery(id+"F0.wireOp",EDGE,"E11.166.5"),sQuery(id+"F0.wireOp",EDGE,"E11.166.6"),sQuery(id+"F0.wireOp",EDGE,"E11.166.7"),sQuery(id+"F0.wireOp",EDGE,"E11.167.0"),sQuery(id+"F0.wireOp",EDGE,"E11.167.1"),sQuery(id+"F0.wireOp",EDGE,"E11.167.2"),sQuery(id+"F0.wireOp",EDGE,"E11.167.3"),sQuery(id+"F0.wireOp",EDGE,"E11.167.4"),sQuery(id+"F0.wireOp",EDGE,"E11.167.5"),sQuery(id+"F0.wireOp",EDGE,"E11.167.6"),sQuery(id+"F0.wireOp",EDGE,"E11.167.7"),sQuery(id+"F0.wireOp",EDGE,"E11.168.0"),sQuery(id+"F0.wireOp",EDGE,"E11.168.1"),sQuery(id+"F0.wireOp",EDGE,"E11.168.2"),sQuery(id+"F0.wireOp",EDGE,"E11.168.3"),sQuery(id+"F0.wireOp",EDGE,"E11.168.4"),sQuery(id+"F0.wireOp",EDGE,"E11.168.5"),sQuery(id+"F0.wireOp",EDGE,"E11.168.6"),sQuery(id+"F0.wireOp",EDGE,"E11.168.7"),sQuery(id+"F0.wireOp",EDGE,"E11.169.0"),sQuery(id+"F0.wireOp",EDGE,"E11.169.1"),sQuery(id+"F0.wireOp",EDGE,"E11.169.2"),sQuery(id+"F0.wireOp",EDGE,"E11.169.3"),sQuery(id+"F0.wireOp",EDGE,"E11.169.4"),sQuery(id+"F0.wireOp",EDGE,"E11.169.5"),sQuery(id+"F0.wireOp",EDGE,"E11.169.6"),sQuery(id+"F0.wireOp",EDGE,"E11.169.7"),sQuery(id+"F0.wireOp",EDGE,"E11.170.0"),sQuery(id+"F0.wireOp",EDGE,"E11.170.1"),sQuery(id+"F0.wireOp",EDGE,"E11.170.2"),sQuery(id+"F0.wireOp",EDGE,"E11.170.3"),sQuery(id+"F0.wireOp",EDGE,"E11.170.4"),sQuery(id+"F0.wireOp",EDGE,"E11.170.5"),sQuery(id+"F0.wireOp",EDGE,"E11.170.6"),sQuery(id+"F0.wireOp",EDGE,"E11.170.7"),sQuery(id+"F0.wireOp",EDGE,"E11.171.0"),sQuery(id+"F0.wireOp",EDGE,"E11.171.1"),sQuery(id+"F0.wireOp",EDGE,"E11.171.2"),sQuery(id+"F0.wireOp",EDGE,"E11.171.3"),sQuery(id+"F0.wireOp",EDGE,"E11.171.4"),sQuery(id+"F0.wireOp",EDGE,"E11.171.5"),sQuery(id+"F0.wireOp",EDGE,"E11.171.6"),sQuery(id+"F0.wireOp",EDGE,"E11.171.7"),sQuery(id+"F0.wireOp",EDGE,"E11.172.0"),sQuery(id+"F0.wireOp",EDGE,"E11.172.1"),sQuery(id+"F0.wireOp",EDGE,"E11.172.2"),sQuery(id+"F0.wireOp",EDGE,"E11.172.3"),sQuery(id+"F0.wireOp",EDGE,"E11.172.4"),sQuery(id+"F0.wireOp",EDGE,"E11.172.5"),sQuery(id+"F0.wireOp",EDGE,"E11.172.6"),sQuery(id+"F0.wireOp",EDGE,"E11.172.7"),sQuery(id+"F0.wireOp",EDGE,"E11.173.0"),sQuery(id+"F0.wireOp",EDGE,"E11.173.1"),sQuery(id+"F0.wireOp",EDGE,"E11.173.2"),sQuery(id+"F0.wireOp",EDGE,"E11.173.3"),sQuery(id+"F0.wireOp",EDGE,"E11.173.4"),sQuery(id+"F0.wireOp",EDGE,"E11.173.5"),sQuery(id+"F0.wireOp",EDGE,"E11.173.6"),sQuery(id+"F0.wireOp",EDGE,"E11.173.7"),sQuery(id+"F0.wireOp",EDGE,"E11.174.0"),sQuery(id+"F0.wireOp",EDGE,"E11.174.1"),sQuery(id+"F0.wireOp",EDGE,"E11.174.2"),sQuery(id+"F0.wireOp",EDGE,"E11.174.3"),sQuery(id+"F0.wireOp",EDGE,"E11.174.4"),sQuery(id+"F0.wireOp",EDGE,"E11.174.5"),sQuery(id+"F0.wireOp",EDGE,"E11.174.6"),sQuery(id+"F0.wireOp",EDGE,"E11.174.7"),sQuery(id+"F0.wireOp",EDGE,"E11.175.0"),sQuery(id+"F0.wireOp",EDGE,"E11.175.1"),sQuery(id+"F0.wireOp",EDGE,"E11.175.2"),sQuery(id+"F0.wireOp",EDGE,"E11.175.3"),sQuery(id+"F0.wireOp",EDGE,"E11.175.4"),sQuery(id+"F0.wireOp",EDGE,"E11.175.5"),sQuery(id+"F0.wireOp",EDGE,"E11.175.6"),sQuery(id+"F0.wireOp",EDGE,"E11.175.7"),sQuery(id+"F0.wireOp",EDGE,"E11.176.0"),sQuery(id+"F0.wireOp",EDGE,"E11.176.1"),sQuery(id+"F0.wireOp",EDGE,"E11.176.2"),sQuery(id+"F0.wireOp",EDGE,"E11.176.3"),sQuery(id+"F0.wireOp",EDGE,"E11.176.4"),sQuery(id+"F0.wireOp",EDGE,"E11.176.5"),sQuery(id+"F0.wireOp",EDGE,"E11.176.6"),sQuery(id+"F0.wireOp",EDGE,"E11.176.7"),sQuery(id+"F0.wireOp",EDGE,"E11.177.0"),sQuery(id+"F0.wireOp",EDGE,"E11.177.1"),sQuery(id+"F0.wireOp",EDGE,"E11.177.2"),sQuery(id+"F0.wireOp",EDGE,"E11.177.3"),sQuery(id+"F0.wireOp",EDGE,"E11.177.4"),sQuery(id+"F0.wireOp",EDGE,"E11.177.5"),sQuery(id+"F0.wireOp",EDGE,"E11.177.6"),sQuery(id+"F0.wireOp",EDGE,"E11.177.7"),sQuery(id+"F0.wireOp",EDGE,"E11.178.0"),sQuery(id+"F0.wireOp",EDGE,"E11.178.1"),sQuery(id+"F0.wireOp",EDGE,"E11.178.2"),sQuery(id+"F0.wireOp",EDGE,"E11.178.3"),sQuery(id+"F0.wireOp",EDGE,"E11.178.4"),sQuery(id+"F0.wireOp",EDGE,"E11.178.5"),sQuery(id+"F0.wireOp",EDGE,"E11.178.6"),sQuery(id+"F0.wireOp",EDGE,"E11.178.7"),sQuery(id+"F0.wireOp",EDGE,"E11.179.0"),sQuery(id+"F0.wireOp",EDGE,"E11.179.1"),sQuery(id+"F0.wireOp",EDGE,"E11.179.2"),sQuery(id+"F0.wireOp",EDGE,"E11.179.3"),sQuery(id+"F0.wireOp",EDGE,"E11.179.4"),sQuery(id+"F0.wireOp",EDGE,"E11.179.5"),sQuery(id+"F0.wireOp",EDGE,"E11.179.6"),sQuery(id+"F0.wireOp",EDGE,"E11.179.7"),sQuery(id+"F0.wireOp",EDGE,"E11.180.0"),sQuery(id+"F0.wireOp",EDGE,"E11.180.1"),sQuery(id+"F0.wireOp",EDGE,"E11.180.2"),sQuery(id+"F0.wireOp",EDGE,"E11.180.3"),sQuery(id+"F0.wireOp",EDGE,"E11.180.4"),sQuery(id+"F0.wireOp",EDGE,"E11.180.5"),sQuery(id+"F0.wireOp",EDGE,"E11.180.6"),sQuery(id+"F0.wireOp",EDGE,"E11.180.7"),sQuery(id+"F0.wireOp",EDGE,"E11.181.0"),sQuery(id+"F0.wireOp",EDGE,"E11.181.1"),sQuery(id+"F0.wireOp",EDGE,"E11.181.2"),sQuery(id+"F0.wireOp",EDGE,"E11.181.3"),sQuery(id+"F0.wireOp",EDGE,"E11.181.4"),sQuery(id+"F0.wireOp",EDGE,"E11.181.5"),sQuery(id+"F0.wireOp",EDGE,"E11.181.6"),sQuery(id+"F0.wireOp",EDGE,"E11.181.7"),sQuery(id+"F0.wireOp",EDGE,"E11.182.0"),sQuery(id+"F0.wireOp",EDGE,"E11.182.1"),sQuery(id+"F0.wireOp",EDGE,"E11.182.2"),sQuery(id+"F0.wireOp",EDGE,"E11.182.3"),sQuery(id+"F0.wireOp",EDGE,"E11.182.4"),sQuery(id+"F0.wireOp",EDGE,"E11.182.5"),sQuery(id+"F0.wireOp",EDGE,"E11.182.6"),sQuery(id+"F0.wireOp",EDGE,"E11.182.7"),sQuery(id+"F0.wireOp",EDGE,"E11.183.0"),sQuery(id+"F0.wireOp",EDGE,"E11.183.1"),sQuery(id+"F0.wireOp",EDGE,"E11.183.2"),sQuery(id+"F0.wireOp",EDGE,"E11.183.3"),sQuery(id+"F0.wireOp",EDGE,"E11.183.4"),sQuery(id+"F0.wireOp",EDGE,"E11.183.5"),sQuery(id+"F0.wireOp",EDGE,"E11.183.6"),sQuery(id+"F0.wireOp",EDGE,"E11.183.7"),sQuery(id+"F0.wireOp",EDGE,"E11.184.0"),sQuery(id+"F0.wireOp",EDGE,"E11.184.1"),sQuery(id+"F0.wireOp",EDGE,"E11.184.2"),sQuery(id+"F0.wireOp",EDGE,"E11.184.3"),sQuery(id+"F0.wireOp",EDGE,"E11.184.4"),sQuery(id+"F0.wireOp",EDGE,"E11.184.5"),sQuery(id+"F0.wireOp",EDGE,"E11.184.6"),sQuery(id+"F0.wireOp",EDGE,"E11.184.7"),sQuery(id+"F0.wireOp",EDGE,"E11.185.0"),sQuery(id+"F0.wireOp",EDGE,"E11.185.1"),sQuery(id+"F0.wireOp",EDGE,"E11.185.2"),sQuery(id+"F0.wireOp",EDGE,"E11.185.3"),sQuery(id+"F0.wireOp",EDGE,"E11.185.4"),sQuery(id+"F0.wireOp",EDGE,"E11.185.5"),sQuery(id+"F0.wireOp",EDGE,"E11.185.6"),sQuery(id+"F0.wireOp",EDGE,"E11.185.7"),sQuery(id+"F0.wireOp",EDGE,"E11.186.0"),sQuery(id+"F0.wireOp",EDGE,"E11.186.1"),sQuery(id+"F0.wireOp",EDGE,"E11.186.2"),sQuery(id+"F0.wireOp",EDGE,"E11.186.3"),sQuery(id+"F0.wireOp",EDGE,"E11.186.4"),sQuery(id+"F0.wireOp",EDGE,"E11.186.5"),sQuery(id+"F0.wireOp",EDGE,"E11.186.6"),sQuery(id+"F0.wireOp",EDGE,"E11.186.7"),sQuery(id+"F0.wireOp",EDGE,"E11.187.0"),sQuery(id+"F0.wireOp",EDGE,"E11.187.1"),sQuery(id+"F0.wireOp",EDGE,"E11.187.2"),sQuery(id+"F0.wireOp",EDGE,"E11.187.3"),sQuery(id+"F0.wireOp",EDGE,"E11.187.4"),sQuery(id+"F0.wireOp",EDGE,"E11.187.5"),sQuery(id+"F0.wireOp",EDGE,"E11.187.6"),sQuery(id+"F0.wireOp",EDGE,"E11.187.7"),sQuery(id+"F0.wireOp",EDGE,"E11.188.0"),sQuery(id+"F0.wireOp",EDGE,"E11.188.1"),sQuery(id+"F0.wireOp",EDGE,"E11.188.2"),sQuery(id+"F0.wireOp",EDGE,"E11.188.3"),sQuery(id+"F0.wireOp",EDGE,"E11.188.4"),sQuery(id+"F0.wireOp",EDGE,"E11.188.5"),sQuery(id+"F0.wireOp",EDGE,"E11.188.6"),sQuery(id+"F0.wireOp",EDGE,"E11.188.7"),sQuery(id+"F0.wireOp",EDGE,"E11.189.0"),sQuery(id+"F0.wireOp",EDGE,"E11.189.1"),sQuery(id+"F0.wireOp",EDGE,"E11.189.2"),sQuery(id+"F0.wireOp",EDGE,"E11.189.3"),sQuery(id+"F0.wireOp",EDGE,"E11.189.4"),sQuery(id+"F0.wireOp",EDGE,"E11.189.5"),sQuery(id+"F0.wireOp",EDGE,"E11.189.6"),sQuery(id+"F0.wireOp",EDGE,"E11.189.7"),sQuery(id+"F0.wireOp",EDGE,"E11.190.0"),sQuery(id+"F0.wireOp",EDGE,"E11.190.1"),sQuery(id+"F0.wireOp",EDGE,"E11.190.2"),sQuery(id+"F0.wireOp",EDGE,"E11.190.3"),sQuery(id+"F0.wireOp",EDGE,"E11.190.4"),sQuery(id+"F0.wireOp",EDGE,"E11.190.5"),sQuery(id+"F0.wireOp",EDGE,"E11.190.6"),sQuery(id+"F0.wireOp",EDGE,"E11.190.7"),sQuery(id+"F0.wireOp",EDGE,"E11.191.0"),sQuery(id+"F0.wireOp",EDGE,"E11.191.1"),sQuery(id+"F0.wireOp",EDGE,"E11.191.2"),sQuery(id+"F0.wireOp",EDGE,"E11.191.3"),sQuery(id+"F0.wireOp",EDGE,"E11.191.4"),sQuery(id+"F0.wireOp",EDGE,"E11.191.5"),sQuery(id+"F0.wireOp",EDGE,"E11.191.6"),sQuery(id+"F0.wireOp",EDGE,"E11.191.7"),sQuery(id+"F0.wireOp",EDGE,"E11.192.0"),sQuery(id+"F0.wireOp",EDGE,"E11.192.1"),sQuery(id+"F0.wireOp",EDGE,"E11.192.2"),sQuery(id+"F0.wireOp",EDGE,"E11.192.3"),sQuery(id+"F0.wireOp",EDGE,"E11.192.4"),sQuery(id+"F0.wireOp",EDGE,"E11.192.5"),sQuery(id+"F0.wireOp",EDGE,"E11.192.6"),sQuery(id+"F0.wireOp",EDGE,"E11.192.7"),sQuery(id+"F0.wireOp",EDGE,"E11.193.0"),sQuery(id+"F0.wireOp",EDGE,"E11.193.1"),sQuery(id+"F0.wireOp",EDGE,"E11.193.2"),sQuery(id+"F0.wireOp",EDGE,"E11.193.3"),sQuery(id+"F0.wireOp",EDGE,"E11.193.4"),sQuery(id+"F0.wireOp",EDGE,"E11.193.5"),sQuery(id+"F0.wireOp",EDGE,"E11.193.6"),sQuery(id+"F0.wireOp",EDGE,"E11.193.7"),sQuery(id+"F0.wireOp",EDGE,"E11.194.0"),sQuery(id+"F0.wireOp",EDGE,"E11.194.1"),sQuery(id+"F0.wireOp",EDGE,"E11.194.2"),sQuery(id+"F0.wireOp",EDGE,"E11.194.3"),sQuery(id+"F0.wireOp",EDGE,"E11.194.4"),sQuery(id+"F0.wireOp",EDGE,"E11.194.5"),sQuery(id+"F0.wireOp",EDGE,"E11.194.6"),sQuery(id+"F0.wireOp",EDGE,"E11.194.7"),sQuery(id+"F0.wireOp",EDGE,"E11.195.0"),sQuery(id+"F0.wireOp",EDGE,"E11.195.1"),sQuery(id+"F0.wireOp",EDGE,"E11.195.2"),sQuery(id+"F0.wireOp",EDGE,"E11.195.3"),sQuery(id+"F0.wireOp",EDGE,"E11.195.4"),sQuery(id+"F0.wireOp",EDGE,"E11.195.5"),sQuery(id+"F0.wireOp",EDGE,"E11.195.6"),sQuery(id+"F0.wireOp",EDGE,"E11.195.7"),sQuery(id+"F0.wireOp",EDGE,"E11.196.0"),sQuery(id+"F0.wireOp",EDGE,"E11.196.1"),sQuery(id+"F0.wireOp",EDGE,"E11.196.2"),sQuery(id+"F0.wireOp",EDGE,"E11.196.3"),sQuery(id+"F0.wireOp",EDGE,"E11.196.4"),sQuery(id+"F0.wireOp",EDGE,"E11.196.5"),sQuery(id+"F0.wireOp",EDGE,"E11.196.6"),sQuery(id+"F0.wireOp",EDGE,"E11.196.7"),sQuery(id+"F0.wireOp",EDGE,"E11.197.0"),sQuery(id+"F0.wireOp",EDGE,"E11.197.1"),sQuery(id+"F0.wireOp",EDGE,"E11.197.2"),sQuery(id+"F0.wireOp",EDGE,"E11.197.3"),sQuery(id+"F0.wireOp",EDGE,"E11.197.4"),sQuery(id+"F0.wireOp",EDGE,"E11.197.5"),sQuery(id+"F0.wireOp",EDGE,"E11.197.6"),sQuery(id+"F0.wireOp",EDGE,"E11.197.7"),sQuery(id+"F0.wireOp",EDGE,"E11.198.0"),sQuery(id+"F0.wireOp",EDGE,"E11.198.1"),sQuery(id+"F0.wireOp",EDGE,"E11.198.2"),sQuery(id+"F0.wireOp",EDGE,"E11.198.3"),sQuery(id+"F0.wireOp",EDGE,"E11.198.4"),sQuery(id+"F0.wireOp",EDGE,"E11.198.5"),sQuery(id+"F0.wireOp",EDGE,"E11.198.6"),sQuery(id+"F0.wireOp",EDGE,"E11.198.7"),sQuery(id+"F0.wireOp",EDGE,"E11.199.0"),sQuery(id+"F0.wireOp",EDGE,"E11.199.1"),sQuery(id+"F0.wireOp",EDGE,"E11.199.2"),sQuery(id+"F0.wireOp",EDGE,"E11.199.3"),sQuery(id+"F0.wireOp",EDGE,"E11.199.4"),sQuery(id+"F0.wireOp",EDGE,"E11.199.5"),sQuery(id+"F0.wireOp",EDGE,"E11.199.6"),sQuery(id+"F0.wireOp",EDGE,"E11.199.7"),sQuery(id+"F0.wireOp",EDGE,"E11.200.0"),sQuery(id+"F0.wireOp",EDGE,"E11.200.1"),sQuery(id+"F0.wireOp",EDGE,"E11.200.2"),sQuery(id+"F0.wireOp",EDGE,"E11.200.3"),sQuery(id+"F0.wireOp",EDGE,"E11.200.4"),sQuery(id+"F0.wireOp",EDGE,"E11.200.5"),sQuery(id+"F0.wireOp",EDGE,"E11.200.6"),sQuery(id+"F0.wireOp",EDGE,"E11.200.7"),sQuery(id+"F0.wireOp",EDGE,"E11.201.0"),sQuery(id+"F0.wireOp",EDGE,"E11.201.1"),sQuery(id+"F0.wireOp",EDGE,"E11.201.2"),sQuery(id+"F0.wireOp",EDGE,"E11.201.3"),sQuery(id+"F0.wireOp",EDGE,"E11.201.4"),sQuery(id+"F0.wireOp",EDGE,"E11.201.5"),sQuery(id+"F0.wireOp",EDGE,"E11.201.6"),sQuery(id+"F0.wireOp",EDGE,"E11.201.7"),sQuery(id+"F0.wireOp",EDGE,"E11.202.0"),sQuery(id+"F0.wireOp",EDGE,"E11.202.1"),sQuery(id+"F0.wireOp",EDGE,"E11.202.2"),sQuery(id+"F0.wireOp",EDGE,"E11.202.3"),sQuery(id+"F0.wireOp",EDGE,"E11.202.4"),sQuery(id+"F0.wireOp",EDGE,"E11.202.5"),sQuery(id+"F0.wireOp",EDGE,"E11.202.6"),sQuery(id+"F0.wireOp",EDGE,"E11.202.7"),sQuery(id+"F0.wireOp",EDGE,"E11.203.0"),sQuery(id+"F0.wireOp",EDGE,"E11.203.1"),sQuery(id+"F0.wireOp",EDGE,"E11.203.2"),sQuery(id+"F0.wireOp",EDGE,"E11.203.3"),sQuery(id+"F0.wireOp",EDGE,"E11.203.4"),sQuery(id+"F0.wireOp",EDGE,"E11.203.5"),sQuery(id+"F0.wireOp",EDGE,"E11.203.6"),sQuery(id+"F0.wireOp",EDGE,"E11.203.7"),sQuery(id+"F0.wireOp",EDGE,"E11.204.0"),sQuery(id+"F0.wireOp",EDGE,"E11.204.1"),sQuery(id+"F0.wireOp",EDGE,"E11.204.2"),sQuery(id+"F0.wireOp",EDGE,"E11.204.3"),sQuery(id+"F0.wireOp",EDGE,"E11.204.4"),sQuery(id+"F0.wireOp",EDGE,"E11.204.5"),sQuery(id+"F0.wireOp",EDGE,"E11.204.6"),sQuery(id+"F0.wireOp",EDGE,"E11.204.7"),sQuery(id+"F0.wireOp",EDGE,"E11.205.0"),sQuery(id+"F0.wireOp",EDGE,"E11.205.1"),sQuery(id+"F0.wireOp",EDGE,"E11.205.2"),sQuery(id+"F0.wireOp",EDGE,"E11.205.3"),sQuery(id+"F0.wireOp",EDGE,"E11.205.4"),sQuery(id+"F0.wireOp",EDGE,"E11.205.5"),sQuery(id+"F0.wireOp",EDGE,"E11.205.6"),sQuery(id+"F0.wireOp",EDGE,"E11.205.7"),sQuery(id+"F0.wireOp",EDGE,"E11.206.0"),sQuery(id+"F0.wireOp",EDGE,"E11.206.1"),sQuery(id+"F0.wireOp",EDGE,"E11.206.2"),sQuery(id+"F0.wireOp",EDGE,"E11.206.3"),sQuery(id+"F0.wireOp",EDGE,"E11.206.4"),sQuery(id+"F0.wireOp",EDGE,"E11.206.5"),sQuery(id+"F0.wireOp",EDGE,"E11.206.6"),sQuery(id+"F0.wireOp",EDGE,"E11.206.7"),sQuery(id+"F0.wireOp",EDGE,"E11.207.0"),sQuery(id+"F0.wireOp",EDGE,"E11.207.1"),sQuery(id+"F0.wireOp",EDGE,"E11.207.2"),sQuery(id+"F0.wireOp",EDGE,"E11.207.3"),sQuery(id+"F0.wireOp",EDGE,"E11.207.4"),sQuery(id+"F0.wireOp",EDGE,"E11.207.5"),sQuery(id+"F0.wireOp",EDGE,"E11.207.6"),sQuery(id+"F0.wireOp",EDGE,"E11.207.7"),sQuery(id+"F0.wireOp",EDGE,"E11.208.0"),sQuery(id+"F0.wireOp",EDGE,"E11.208.1"),sQuery(id+"F0.wireOp",EDGE,"E11.208.2"),sQuery(id+"F0.wireOp",EDGE,"E11.208.3"),sQuery(id+"F0.wireOp",EDGE,"E11.208.4"),sQuery(id+"F0.wireOp",EDGE,"E11.208.5"),sQuery(id+"F0.wireOp",EDGE,"E11.208.6"),sQuery(id+"F0.wireOp",EDGE,"E11.208.7"),sQuery(id+"F0.wireOp",EDGE,"E11.209.0"),sQuery(id+"F0.wireOp",EDGE,"E11.209.1"),sQuery(id+"F0.wireOp",EDGE,"E11.209.2"),sQuery(id+"F0.wireOp",EDGE,"E11.209.3"),sQuery(id+"F0.wireOp",EDGE,"E11.209.4"),sQuery(id+"F0.wireOp",EDGE,"E11.209.5"),sQuery(id+"F0.wireOp",EDGE,"E11.209.6"),sQuery(id+"F0.wireOp",EDGE,"E11.209.7"),sQuery(id+"F0.wireOp",EDGE,"E11.210.0"),sQuery(id+"F0.wireOp",EDGE,"E11.210.1"),sQuery(id+"F0.wireOp",EDGE,"E11.210.2"),sQuery(id+"F0.wireOp",EDGE,"E11.210.3"),sQuery(id+"F0.wireOp",EDGE,"E11.210.4"),sQuery(id+"F0.wireOp",EDGE,"E11.210.5"),sQuery(id+"F0.wireOp",EDGE,"E11.210.6"),sQuery(id+"F0.wireOp",EDGE,"E11.210.7"),sQuery(id+"F0.wireOp",EDGE,"E11.211.0"),sQuery(id+"F0.wireOp",EDGE,"E11.211.1"),sQuery(id+"F0.wireOp",EDGE,"E11.211.2"),sQuery(id+"F0.wireOp",EDGE,"E11.211.3"),sQuery(id+"F0.wireOp",EDGE,"E11.211.4"),sQuery(id+"F0.wireOp",EDGE,"E11.211.5"),sQuery(id+"F0.wireOp",EDGE,"E11.211.6"),sQuery(id+"F0.wireOp",EDGE,"E11.211.7"),sQuery(id+"F0.wireOp",EDGE,"E11.212.0"),sQuery(id+"F0.wireOp",EDGE,"E11.212.1"),sQuery(id+"F0.wireOp",EDGE,"E11.212.2"),sQuery(id+"F0.wireOp",EDGE,"E11.212.3"),sQuery(id+"F0.wireOp",EDGE,"E11.212.4"),sQuery(id+"F0.wireOp",EDGE,"E11.212.5"),sQuery(id+"F0.wireOp",EDGE,"E11.212.6"),sQuery(id+"F0.wireOp",EDGE,"E11.212.7"),sQuery(id+"F0.wireOp",EDGE,"E11.213.0"),sQuery(id+"F0.wireOp",EDGE,"E11.213.1"),sQuery(id+"F0.wireOp",EDGE,"E11.213.2"),sQuery(id+"F0.wireOp",EDGE,"E11.213.3"),sQuery(id+"F0.wireOp",EDGE,"E11.213.4"),sQuery(id+"F0.wireOp",EDGE,"E11.213.5"),sQuery(id+"F0.wireOp",EDGE,"E11.213.6"),sQuery(id+"F0.wireOp",EDGE,"E11.213.7"),sQuery(id+"F0.wireOp",EDGE,"E11.214.0"),sQuery(id+"F0.wireOp",EDGE,"E11.214.1"),sQuery(id+"F0.wireOp",EDGE,"E11.214.2"),sQuery(id+"F0.wireOp",EDGE,"E11.214.3"),sQuery(id+"F0.wireOp",EDGE,"E11.214.4"),sQuery(id+"F0.wireOp",EDGE,"E11.214.5"),sQuery(id+"F0.wireOp",EDGE,"E11.214.6"),sQuery(id+"F0.wireOp",EDGE,"E11.214.7"),sQuery(id+"F0.wireOp",EDGE,"E11.215.0"),sQuery(id+"F0.wireOp",EDGE,"E11.215.1"),sQuery(id+"F0.wireOp",EDGE,"E11.215.2"),sQuery(id+"F0.wireOp",EDGE,"E11.215.3"),sQuery(id+"F0.wireOp",EDGE,"E11.215.4"),sQuery(id+"F0.wireOp",EDGE,"E11.215.5"),sQuery(id+"F0.wireOp",EDGE,"E11.215.6"),sQuery(id+"F0.wireOp",EDGE,"E11.215.7"),sQuery(id+"F0.wireOp",EDGE,"E11.216.0"),sQuery(id+"F0.wireOp",EDGE,"E11.216.1"),sQuery(id+"F0.wireOp",EDGE,"E11.216.2"),sQuery(id+"F0.wireOp",EDGE,"E11.216.3"),sQuery(id+"F0.wireOp",EDGE,"E11.216.4"),sQuery(id+"F0.wireOp",EDGE,"E11.216.5"),sQuery(id+"F0.wireOp",EDGE,"E11.216.6"),sQuery(id+"F0.wireOp",EDGE,"E11.216.7"),sQuery(id+"F0.wireOp",EDGE,"E11.217.0"),sQuery(id+"F0.wireOp",EDGE,"E11.217.1"),sQuery(id+"F0.wireOp",EDGE,"E11.217.2"),sQuery(id+"F0.wireOp",EDGE,"E11.217.3"),sQuery(id+"F0.wireOp",EDGE,"E11.217.4"),sQuery(id+"F0.wireOp",EDGE,"E11.217.5"),sQuery(id+"F0.wireOp",EDGE,"E11.217.6"),sQuery(id+"F0.wireOp",EDGE,"E11.217.7"),sQuery(id+"F0.wireOp",EDGE,"E11.218.0"),sQuery(id+"F0.wireOp",EDGE,"E11.218.1"),sQuery(id+"F0.wireOp",EDGE,"E11.218.2"),sQuery(id+"F0.wireOp",EDGE,"E11.218.3"),sQuery(id+"F0.wireOp",EDGE,"E11.218.4"),sQuery(id+"F0.wireOp",EDGE,"E11.218.5"),sQuery(id+"F0.wireOp",EDGE,"E11.218.6"),sQuery(id+"F0.wireOp",EDGE,"E11.218.7"),sQuery(id+"F0.wireOp",EDGE,"E11.219.0"),sQuery(id+"F0.wireOp",EDGE,"E11.219.1"),sQuery(id+"F0.wireOp",EDGE,"E11.219.2"),sQuery(id+"F0.wireOp",EDGE,"E11.219.3"),sQuery(id+"F0.wireOp",EDGE,"E11.219.4"),sQuery(id+"F0.wireOp",EDGE,"E11.219.5"),sQuery(id+"F0.wireOp",EDGE,"E11.219.6"),sQuery(id+"F0.wireOp",EDGE,"E11.219.7"),sQuery(id+"F0.wireOp",EDGE,"E11.220.0"),sQuery(id+"F0.wireOp",EDGE,"E11.220.1"),sQuery(id+"F0.wireOp",EDGE,"E11.220.2"),sQuery(id+"F0.wireOp",EDGE,"E11.220.3"),sQuery(id+"F0.wireOp",EDGE,"E11.220.4"),sQuery(id+"F0.wireOp",EDGE,"E11.220.5"),sQuery(id+"F0.wireOp",EDGE,"E11.220.6"),sQuery(id+"F0.wireOp",EDGE,"E11.220.7"),sQuery(id+"F0.wireOp",EDGE,"E11.221.0"),sQuery(id+"F0.wireOp",EDGE,"E11.221.1"),sQuery(id+"F0.wireOp",EDGE,"E11.221.2"),sQuery(id+"F0.wireOp",EDGE,"E11.221.3"),sQuery(id+"F0.wireOp",EDGE,"E11.221.4"),sQuery(id+"F0.wireOp",EDGE,"E11.221.5"),sQuery(id+"F0.wireOp",EDGE,"E11.221.6"),sQuery(id+"F0.wireOp",EDGE,"E11.221.7"),sQuery(id+"F0.wireOp",EDGE,"E11.222.0"),sQuery(id+"F0.wireOp",EDGE,"E11.222.1"),sQuery(id+"F0.wireOp",EDGE,"E11.222.2"),sQuery(id+"F0.wireOp",EDGE,"E11.222.3"),sQuery(id+"F0.wireOp",EDGE,"E11.222.4"),sQuery(id+"F0.wireOp",EDGE,"E11.222.5"),sQuery(id+"F0.wireOp",EDGE,"E11.222.6"),sQuery(id+"F0.wireOp",EDGE,"E11.222.7"),sQuery(id+"F0.wireOp",EDGE,"E11.223.0"),sQuery(id+"F0.wireOp",EDGE,"E11.223.1"),sQuery(id+"F0.wireOp",EDGE,"E11.223.2"),sQuery(id+"F0.wireOp",EDGE,"E11.223.3"),sQuery(id+"F0.wireOp",EDGE,"E11.223.4"),sQuery(id+"F0.wireOp",EDGE,"E11.223.5"),sQuery(id+"F0.wireOp",EDGE,"E11.223.6"),sQuery(id+"F0.wireOp",EDGE,"E11.223.7"),sQuery(id+"F0.wireOp",EDGE,"E11.224.0"),sQuery(id+"F0.wireOp",EDGE,"E11.224.1"),sQuery(id+"F0.wireOp",EDGE,"E11.224.2"),sQuery(id+"F0.wireOp",EDGE,"E11.224.3"),sQuery(id+"F0.wireOp",EDGE,"E11.224.4"),sQuery(id+"F0.wireOp",EDGE,"E11.224.5"),sQuery(id+"F0.wireOp",EDGE,"E11.224.6"),sQuery(id+"F0.wireOp",EDGE,"E11.224.7"),sQuery(id+"F0.wireOp",EDGE,"E11.225.0"),sQuery(id+"F0.wireOp",EDGE,"E11.225.1"),sQuery(id+"F0.wireOp",EDGE,"E11.225.2"),sQuery(id+"F0.wireOp",EDGE,"E11.225.3"),sQuery(id+"F0.wireOp",EDGE,"E11.225.4"),sQuery(id+"F0.wireOp",EDGE,"E11.225.5"),sQuery(id+"F0.wireOp",EDGE,"E11.225.6"),sQuery(id+"F0.wireOp",EDGE,"E11.225.7"),sQuery(id+"F0.wireOp",EDGE,"E11.226.0"),sQuery(id+"F0.wireOp",EDGE,"E11.226.1"),sQuery(id+"F0.wireOp",EDGE,"E11.226.2"),sQuery(id+"F0.wireOp",EDGE,"E11.226.3"),sQuery(id+"F0.wireOp",EDGE,"E11.226.4"),sQuery(id+"F0.wireOp",EDGE,"E11.226.5"),sQuery(id+"F0.wireOp",EDGE,"E11.226.6"),sQuery(id+"F0.wireOp",EDGE,"E11.226.7"),sQuery(id+"F0.wireOp",EDGE,"E11.227.0"),sQuery(id+"F0.wireOp",EDGE,"E11.227.1"),sQuery(id+"F0.wireOp",EDGE,"E11.227.2"),sQuery(id+"F0.wireOp",EDGE,"E11.227.3"),sQuery(id+"F0.wireOp",EDGE,"E11.227.4"),sQuery(id+"F0.wireOp",EDGE,"E11.227.5"),sQuery(id+"F0.wireOp",EDGE,"E11.227.6"),sQuery(id+"F0.wireOp",EDGE,"E11.227.7"),sQuery(id+"F0.wireOp",EDGE,"E11.228.0"),sQuery(id+"F0.wireOp",EDGE,"E11.228.1"),sQuery(id+"F0.wireOp",EDGE,"E11.228.2"),sQuery(id+"F0.wireOp",EDGE,"E11.228.3"),sQuery(id+"F0.wireOp",EDGE,"E11.228.4"),sQuery(id+"F0.wireOp",EDGE,"E11.228.5"),sQuery(id+"F0.wireOp",EDGE,"E11.228.6"),sQuery(id+"F0.wireOp",EDGE,"E11.228.7"),sQuery(id+"F0.wireOp",EDGE,"E11.229.0"),sQuery(id+"F0.wireOp",EDGE,"E11.229.1"),sQuery(id+"F0.wireOp",EDGE,"E11.229.2"),sQuery(id+"F0.wireOp",EDGE,"E11.229.3"),sQuery(id+"F0.wireOp",EDGE,"E11.229.4"),sQuery(id+"F0.wireOp",EDGE,"E11.229.5"),sQuery(id+"F0.wireOp",EDGE,"E11.229.6"),sQuery(id+"F0.wireOp",EDGE,"E11.229.7"),sQuery(id+"F0.wireOp",EDGE,"E11.230.0"),sQuery(id+"F0.wireOp",EDGE,"E11.230.1"),sQuery(id+"F0.wireOp",EDGE,"E11.230.2"),sQuery(id+"F0.wireOp",EDGE,"E11.230.3"),sQuery(id+"F0.wireOp",EDGE,"E11.230.4"),sQuery(id+"F0.wireOp",EDGE,"E11.230.5"),sQuery(id+"F0.wireOp",EDGE,"E11.230.6"),sQuery(id+"F0.wireOp",EDGE,"E11.230.7"),sQuery(id+"F0.wireOp",EDGE,"E11.231.0"),sQuery(id+"F0.wireOp",EDGE,"E11.231.1"),sQuery(id+"F0.wireOp",EDGE,"E11.231.2"),sQuery(id+"F0.wireOp",EDGE,"E11.231.3"),sQuery(id+"F0.wireOp",EDGE,"E11.231.4"),sQuery(id+"F0.wireOp",EDGE,"E11.231.5"),sQuery(id+"F0.wireOp",EDGE,"E11.231.6"),sQuery(id+"F0.wireOp",EDGE,"E11.231.7"),sQuery(id+"F0.wireOp",EDGE,"E11.232.0"),sQuery(id+"F0.wireOp",EDGE,"E11.232.1"),sQuery(id+"F0.wireOp",EDGE,"E11.232.2"),sQuery(id+"F0.wireOp",EDGE,"E11.232.3"),sQuery(id+"F0.wireOp",EDGE,"E11.232.4"),sQuery(id+"F0.wireOp",EDGE,"E11.232.5"),sQuery(id+"F0.wireOp",EDGE,"E11.232.6"),sQuery(id+"F0.wireOp",EDGE,"E11.232.7"),sQuery(id+"F0.wireOp",EDGE,"E11.233.0"),sQuery(id+"F0.wireOp",EDGE,"E11.233.1"),sQuery(id+"F0.wireOp",EDGE,"E11.233.2"),sQuery(id+"F0.wireOp",EDGE,"E11.233.3"),sQuery(id+"F0.wireOp",EDGE,"E11.233.4"),sQuery(id+"F0.wireOp",EDGE,"E11.233.5"),sQuery(id+"F0.wireOp",EDGE,"E11.233.6"),sQuery(id+"F0.wireOp",EDGE,"E11.233.7"),sQuery(id+"F0.wireOp",EDGE,"E11.234.0"),sQuery(id+"F0.wireOp",EDGE,"E11.234.1"),sQuery(id+"F0.wireOp",EDGE,"E11.234.2"),sQuery(id+"F0.wireOp",EDGE,"E11.234.3"),sQuery(id+"F0.wireOp",EDGE,"E11.234.4"),sQuery(id+"F0.wireOp",EDGE,"E11.234.5"),sQuery(id+"F0.wireOp",EDGE,"E11.234.6"),sQuery(id+"F0.wireOp",EDGE,"E11.234.7"),sQuery(id+"F0.wireOp",EDGE,"E11.235.0"),sQuery(id+"F0.wireOp",EDGE,"E11.235.1"),sQuery(id+"F0.wireOp",EDGE,"E11.235.2"),sQuery(id+"F0.wireOp",EDGE,"E11.235.3"),sQuery(id+"F0.wireOp",EDGE,"E11.235.4"),sQuery(id+"F0.wireOp",EDGE,"E11.235.5"),sQuery(id+"F0.wireOp",EDGE,"E11.235.6"),sQuery(id+"F0.wireOp",EDGE,"E11.235.7"),sQuery(id+"F0.wireOp",EDGE,"E11.236.0"),sQuery(id+"F0.wireOp",EDGE,"E11.236.1"),sQuery(id+"F0.wireOp",EDGE,"E11.236.2"),sQuery(id+"F0.wireOp",EDGE,"E11.236.3"),sQuery(id+"F0.wireOp",EDGE,"E11.236.4"),sQuery(id+"F0.wireOp",EDGE,"E11.236.5"),sQuery(id+"F0.wireOp",EDGE,"E11.236.6"),sQuery(id+"F0.wireOp",EDGE,"E11.236.7"),sQuery(id+"F0.wireOp",EDGE,"E11.237.0"),sQuery(id+"F0.wireOp",EDGE,"E11.237.1"),sQuery(id+"F0.wireOp",EDGE,"E11.237.2"),sQuery(id+"F0.wireOp",EDGE,"E11.237.3"),sQuery(id+"F0.wireOp",EDGE,"E11.237.4"),sQuery(id+"F0.wireOp",EDGE,"E11.237.5"),sQuery(id+"F0.wireOp",EDGE,"E11.237.6"),sQuery(id+"F0.wireOp",EDGE,"E11.237.7"),sQuery(id+"F0.wireOp",EDGE,"E11.238.0"),sQuery(id+"F0.wireOp",EDGE,"E11.238.1"),sQuery(id+"F0.wireOp",EDGE,"E11.238.2"),sQuery(id+"F0.wireOp",EDGE,"E11.238.3"),sQuery(id+"F0.wireOp",EDGE,"E11.238.4"),sQuery(id+"F0.wireOp",EDGE,"E11.238.5"),sQuery(id+"F0.wireOp",EDGE,"E11.238.6"),sQuery(id+"F0.wireOp",EDGE,"E11.238.7"),sQuery(id+"F0.wireOp",EDGE,"E11.239.0"),sQuery(id+"F0.wireOp",EDGE,"E11.239.1"),sQuery(id+"F0.wireOp",EDGE,"E11.239.2"),sQuery(id+"F0.wireOp",EDGE,"E11.239.3"),sQuery(id+"F0.wireOp",EDGE,"E11.239.4"),sQuery(id+"F0.wireOp",EDGE,"E11.239.5"),sQuery(id+"F0.wireOp",EDGE,"E11.239.6"),sQuery(id+"F0.wireOp",EDGE,"E11.239.7"),sQuery(id+"F0.wireOp",EDGE,"E13"),sQuery(id+"F0.wireOp",EDGE,"E14.1.0"),sQuery(id+"F0.wireOp",EDGE,"E14.2.0"),sQuery(id+"F0.wireOp",EDGE,"E14.3.0"),sQuery(id+"F0.wireOp",EDGE,"E14.4.0"),sQuery(id+"F0.wireOp",EDGE,"E14.5.0"),sQuery(id+"F0.wireOp",EDGE,"E14.6.0"),sQuery(id+"F0.wireOp",EDGE,"E14.7.0"),sQuery(id+"F0.wireOp",EDGE,"E15")])],"isStart":false});
            var sketch = newSketch(context, id + "F2", { "sketchPlane" : qUnion([Q0])});
            skText(sketch, "E16", { "text": "0", "fontName": "RobotoSlab-Regular.ttf"});
            const initialGuessF2  = {"E16": [-0.00281, 0.13446, 1, 0, 0.00862]};
            skSetInitialGuess(sketch, initialGuessF2);
            skSolve(sketch);
        }
        {
            var Q0;
            Q0 = qSketchRegion(id + "F2", true);
            extrude(context, id + "F3", {"entities" : qUnion([Q0]), "operationType" : NewBodyOperationType.REMOVE, "oppositeDirection" : true, "depth" : 2.54 * mm});
        }
    });
